annotation { "Feature Type Name" : "Feature", "Feature Type Description" : "" }
export const myFeature = defineFeature(function(context is Context, id is Id, definition is map)
    precondition{}
    {
        {
            var Q0;
            Q0=qCreatedBy(makeId("Top.planeOp"),FACE);
            var sketch = newSketch(context, id + "F0", { "sketchPlane" : qUnion([Q0])});
            skLineSegment(sketch, "E0.bottom", {"start": v(-160, 35) * mm, "end": v(160, 35) * mm});
            skLineSegment(sketch, "E0.top", {"start": v(-160, -35) * mm, "end": v(160, -35) * mm});
            skLineSegment(sketch, "E0.left", {"start": v(-160, 35) * mm, "end": v(-160, -35) * mm});
            skLineSegment(sketch, "E0.right", {"start": v(160, 35) * mm, "end": v(160, -35) * mm});
            skLineSegment(sketch, "E1", {"start": v(-160, 35) * mm, "end": v(160, -35) * mm, "construction": true});
            skLineSegment(sketch, "E2", {"start": v(-160, -35) * mm, "end": v(160, 35) * mm, "construction": true});
            skText(sketch, "E3", { "text": "Siri Bloch Arnfred\n", "fontName": "Arimo-Bold.ttf"});
            skText(sketch, "E4", { "text": "Jonas Bloch Riisgaard", "fontName": "Arimo-Bold.ttf"});
            const initialGuessF0  = {"E3": [-0.115, 0.011, 1, 0, 0.02], "E4": [-0.15, -0.015, 1, 0, 0.02]};
            skSetInitialGuess(sketch, initialGuessF0);
            skSolve(sketch);
        }
        {
            var Q0;
            Q0=makeQuery(id+"F0.imprint","IMPRINT",FACE,{"disambiguationData":[TD([[makeQuery(id+"F0.imprint","IMPRINT",EDGE,{"derivedFrom":sQuery(id+"F0.wireOp",EDGE,"E3.sketch_text.stroke-0")}),-1.0]])]});
            var Q1;
            Q1=makeQuery(id+"F0.imprint","IMPRINT",FACE,{"disambiguationData":[TD([[makeQuery(id+"F0.imprint","IMPRINT",EDGE,{"derivedFrom":sQuery(id+"F0.wireOp",EDGE,"E3.sketch_text.stroke-28")}),-1.0]])]});
            var Q2;
            Q2=makeQuery(id+"F0.imprint","IMPRINT",FACE,{"disambiguationData":[TD([[makeQuery(id+"F0.imprint","IMPRINT",EDGE,{"derivedFrom":sQuery(id+"F0.wireOp",EDGE,"E3.sketch_text.stroke-33")}),-1.0]])]});
            var Q3;
            Q3=makeQuery(id+"F0.imprint","IMPRINT",FACE,{"disambiguationData":[TD([[makeQuery(id+"F0.imprint","IMPRINT",EDGE,{"derivedFrom":sQuery(id+"F0.wireOp",EDGE,"E3.sketch_text.stroke-37")}),-1.0]])]});
            var Q4;
            Q4=makeQuery(id+"F0.imprint","IMPRINT",FACE,{"disambiguationData":[TD([[makeQuery(id+"F0.imprint","IMPRINT",EDGE,{"derivedFrom":sQuery(id+"F0.wireOp",EDGE,"E3.sketch_text.stroke-50")}),-1.0]])]});
            var Q5;
            Q5=makeQuery(id+"F0.imprint","IMPRINT",FACE,{"disambiguationData":[TD([[makeQuery(id+"F0.imprint","IMPRINT",EDGE,{"derivedFrom":sQuery(id+"F0.wireOp",EDGE,"E3.sketch_text.stroke-55")}),-1.0]])]});
            var Q6;
            Q6=makeQuery(id+"F0.imprint","IMPRINT",FACE,{"disambiguationData":[TD([[makeQuery(id+"F0.imprint","IMPRINT",EDGE,{"derivedFrom":sQuery(id+"F0.wireOp",EDGE,"E3.sketch_text.stroke-60")}),-1.0]])]});
            var Q7;
            Q7=makeQuery(id+"F0.imprint","IMPRINT",FACE,{"disambiguationData":[TD([[makeQuery(id+"F0.imprint","IMPRINT",EDGE,{"derivedFrom":sQuery(id+"F0.wireOp",EDGE,"E3.sketch_text.stroke-56")}),-1.0]])]});
            extrude(context, id + "F1", {"entities" : qUnion([Q0, Q1, Q2, Q3, Q4, Q5, Q6, Q7]), "depth" : 4 * mm});
        }
        {
            var Q0;
            Q0=makeQuery(id+"F0.imprint","IMPRINT",FACE,{"disambiguationData":[TD([[makeQuery(id+"F0.imprint","IMPRINT",EDGE,{"derivedFrom":sQuery(id+"F0.wireOp",EDGE,"E3.sketch_text.stroke-64")}),-1.0]])]});
            var Q1;
            Q1=makeQuery(id+"F0.imprint","IMPRINT",FACE,{"disambiguationData":[TD([[makeQuery(id+"F0.imprint","IMPRINT",EDGE,{"derivedFrom":sQuery(id+"F0.wireOp",EDGE,"E3.sketch_text.stroke-88")}),-1.0]])]});
            var Q2;
            Q2=makeQuery(id+"F0.imprint","IMPRINT",FACE,{"disambiguationData":[TD([[makeQuery(id+"F0.imprint","IMPRINT",EDGE,{"derivedFrom":sQuery(id+"F0.wireOp",EDGE,"E3.sketch_text.stroke-92")}),-1.0]])]});
            var Q3;
            Q3=makeQuery(id+"F0.imprint","IMPRINT",FACE,{"disambiguationData":[TD([[makeQuery(id+"F0.imprint","IMPRINT",EDGE,{"derivedFrom":sQuery(id+"F0.wireOp",EDGE,"E3.sketch_text.stroke-106")}),-1.0]])]});
            var Q4;
            Q4=makeQuery(id+"F0.imprint","IMPRINT",FACE,{"disambiguationData":[TD([[makeQuery(id+"F0.imprint","IMPRINT",EDGE,{"derivedFrom":sQuery(id+"F0.wireOp",EDGE,"E3.sketch_text.stroke-123")}),-1.0]])]});
            extrude(context, id + "F2", {"entities" : qUnion([Q0, Q1, Q2, Q3, Q4]), "depth" : 4 * mm});
        }
        {
            var Q0;
            Q0=makeQuery(id+"F0.imprint","IMPRINT",FACE,{"disambiguationData":[TD([[makeQuery(id+"F0.imprint","IMPRINT",EDGE,{"derivedFrom":sQuery(id+"F0.wireOp",EDGE,"E3.sketch_text.stroke-140")}),-1.0]])]});
            var Q1;
            Q1=makeQuery(id+"F0.imprint","IMPRINT",FACE,{"disambiguationData":[TD([[makeQuery(id+"F0.imprint","IMPRINT",EDGE,{"derivedFrom":sQuery(id+"F0.wireOp",EDGE,"E3.sketch_text.stroke-155")}),-1.0]])]});
            var Q2;
            Q2=makeQuery(id+"F0.imprint","IMPRINT",FACE,{"disambiguationData":[TD([[makeQuery(id+"F0.imprint","IMPRINT",EDGE,{"derivedFrom":sQuery(id+"F0.wireOp",EDGE,"E3.sketch_text.stroke-172")}),-1.0]])]});
            var Q3;
            Q3=makeQuery(id+"F0.imprint","IMPRINT",FACE,{"disambiguationData":[TD([[makeQuery(id+"F0.imprint","IMPRINT",EDGE,{"derivedFrom":sQuery(id+"F0.wireOp",EDGE,"E3.sketch_text.stroke-191")}),-1.0]])]});
            var Q4;
            Q4=makeQuery(id+"F0.imprint","IMPRINT",FACE,{"disambiguationData":[TD([[makeQuery(id+"F0.imprint","IMPRINT",EDGE,{"derivedFrom":sQuery(id+"F0.wireOp",EDGE,"E3.sketch_text.stroke-209")}),-1.0]])]});
            var Q5;
            Q5=makeQuery(id+"F0.imprint","IMPRINT",FACE,{"disambiguationData":[TD([[makeQuery(id+"F0.imprint","IMPRINT",EDGE,{"derivedFrom":sQuery(id+"F0.wireOp",EDGE,"E3.sketch_text.stroke-226")}),-1.0]])]});
            var Q6;
            Q6=makeQuery(id+"F0.imprint","IMPRINT",FACE,{"disambiguationData":[TD([[makeQuery(id+"F0.imprint","IMPRINT",EDGE,{"derivedFrom":sQuery(id+"F0.wireOp",EDGE,"E3.sketch_text.stroke-244")}),-1.0]])]});
            extrude(context, id + "F3", {"entities" : qUnion([Q0, Q1, Q2, Q3, Q4, Q5, Q6]), "depth" : 4 * mm});
        }
        {
            var Q0;
            Q0=makeQuery(id+"F0.imprint","IMPRINT",FACE,{"disambiguationData":[TD([[makeQuery(id+"F0.imprint","IMPRINT",EDGE,{"derivedFrom":sQuery(id+"F0.wireOp",EDGE,"E4.sketch_text.stroke-0")}),-1.0]])]});
            var Q1;
            Q1=makeQuery(id+"F0.imprint","IMPRINT",FACE,{"disambiguationData":[TD([[makeQuery(id+"F0.imprint","IMPRINT",EDGE,{"derivedFrom":sQuery(id+"F0.wireOp",EDGE,"E4.sketch_text.stroke-14")}),-1.0]])]});
            var Q2;
            Q2=makeQuery(id+"F0.imprint","IMPRINT",FACE,{"disambiguationData":[TD([[makeQuery(id+"F0.imprint","IMPRINT",EDGE,{"derivedFrom":sQuery(id+"F0.wireOp",EDGE,"E4.sketch_text.stroke-28")}),-1.0]])]});
            var Q3;
            Q3=makeQuery(id+"F0.imprint","IMPRINT",FACE,{"disambiguationData":[TD([[makeQuery(id+"F0.imprint","IMPRINT",EDGE,{"derivedFrom":sQuery(id+"F0.wireOp",EDGE,"E4.sketch_text.stroke-47")}),-1.0]])]});
            var Q4;
            Q4=makeQuery(id+"F0.imprint","IMPRINT",FACE,{"disambiguationData":[TD([[makeQuery(id+"F0.imprint","IMPRINT",EDGE,{"derivedFrom":sQuery(id+"F0.wireOp",EDGE,"E4.sketch_text.stroke-85")}),-1.0]])]});
            var Q5;
            Q5=makeQuery(id+"F0.imprint","IMPRINT",FACE,{"disambiguationData":[TD([[makeQuery(id+"F0.imprint","IMPRINT",EDGE,{"derivedFrom":sQuery(id+"F0.wireOp",EDGE,"E4.sketch_text.stroke-114")}),-1.0]])]});
            var Q6;
            Q6=makeQuery(id+"F0.imprint","IMPRINT",FACE,{"disambiguationData":[TD([[makeQuery(id+"F0.imprint","IMPRINT",EDGE,{"derivedFrom":sQuery(id+"F0.wireOp",EDGE,"E4.sketch_text.stroke-138")}),-1.0]])]});
            var Q7;
            Q7=makeQuery(id+"F0.imprint","IMPRINT",FACE,{"disambiguationData":[TD([[makeQuery(id+"F0.imprint","IMPRINT",EDGE,{"derivedFrom":sQuery(id+"F0.wireOp",EDGE,"E4.sketch_text.stroke-142")}),-1.0]])]});
            var Q8;
            Q8=makeQuery(id+"F0.imprint","IMPRINT",FACE,{"disambiguationData":[TD([[makeQuery(id+"F0.imprint","IMPRINT",EDGE,{"derivedFrom":sQuery(id+"F0.wireOp",EDGE,"E4.sketch_text.stroke-156")}),-1.0]])]});
            var Q9;
            Q9=makeQuery(id+"F0.imprint","IMPRINT",FACE,{"disambiguationData":[TD([[makeQuery(id+"F0.imprint","IMPRINT",EDGE,{"derivedFrom":sQuery(id+"F0.wireOp",EDGE,"E4.sketch_text.stroke-173")}),-1.0]])]});
            extrude(context, id + "F4", {"entities" : qUnion([Q0, Q1, Q2, Q3, Q4, Q5, Q6, Q7, Q8, Q9]), "depth" : 4 * mm});
        }
        {
            var Q0;
            Q0=makeQuery(id+"F0.imprint","IMPRINT",FACE,{"disambiguationData":[TD([[makeQuery(id+"F0.imprint","IMPRINT",EDGE,{"derivedFrom":sQuery(id+"F0.wireOp",EDGE,"E4.sketch_text.stroke-190")}),-1.0]])]});
            var Q1;
            Q1=makeQuery(id+"F0.imprint","IMPRINT",FACE,{"disambiguationData":[TD([[makeQuery(id+"F0.imprint","IMPRINT",EDGE,{"derivedFrom":sQuery(id+"F0.wireOp",EDGE,"E4.sketch_text.stroke-212")}),-1.0]])]});
            var Q2;
            Q2=makeQuery(id+"F0.imprint","IMPRINT",FACE,{"disambiguationData":[TD([[makeQuery(id+"F0.imprint","IMPRINT",EDGE,{"derivedFrom":sQuery(id+"F0.wireOp",EDGE,"E4.sketch_text.stroke-208")}),-1.0]])]});
            var Q3;
            Q3=makeQuery(id+"F0.imprint","IMPRINT",FACE,{"disambiguationData":[TD([[makeQuery(id+"F0.imprint","IMPRINT",EDGE,{"derivedFrom":sQuery(id+"F0.wireOp",EDGE,"E4.sketch_text.stroke-220")}),-1.0]])]});
            var Q4;
            Q4=makeQuery(id+"F0.imprint","IMPRINT",FACE,{"disambiguationData":[TD([[makeQuery(id+"F0.imprint","IMPRINT",EDGE,{"derivedFrom":sQuery(id+"F0.wireOp",EDGE,"E4.sketch_text.stroke-216")}),-1.0]])]});
            var Q5;
            Q5=makeQuery(id+"F0.imprint","IMPRINT",FACE,{"disambiguationData":[TD([[makeQuery(id+"F0.imprint","IMPRINT",EDGE,{"derivedFrom":sQuery(id+"F0.wireOp",EDGE,"E4.sketch_text.stroke-224")}),-1.0]])]});
            var Q6;
            Q6=makeQuery(id+"F0.imprint","IMPRINT",FACE,{"disambiguationData":[TD([[makeQuery(id+"F0.imprint","IMPRINT",EDGE,{"derivedFrom":sQuery(id+"F0.wireOp",EDGE,"E4.sketch_text.stroke-253")}),-1.0]])]});
            var Q7;
            Q7=makeQuery(id+"F0.imprint","IMPRINT",FACE,{"disambiguationData":[TD([[makeQuery(id+"F0.imprint","IMPRINT",EDGE,{"derivedFrom":sQuery(id+"F0.wireOp",EDGE,"E4.sketch_text.stroke-283")}),-1.0]])]});
            var Q8;
            Q8=makeQuery(id+"F0.imprint","IMPRINT",FACE,{"disambiguationData":[TD([[makeQuery(id+"F0.imprint","IMPRINT",EDGE,{"derivedFrom":sQuery(id+"F0.wireOp",EDGE,"E4.sketch_text.stroke-321")}),-1.0]])]});
            var Q9;
            Q9=makeQuery(id+"F0.imprint","IMPRINT",FACE,{"disambiguationData":[TD([[makeQuery(id+"F0.imprint","IMPRINT",EDGE,{"derivedFrom":sQuery(id+"F0.wireOp",EDGE,"E4.sketch_text.stroke-359")}),-1.0]])]});
            var Q10;
            Q10=makeQuery(id+"F0.imprint","IMPRINT",FACE,{"disambiguationData":[TD([[makeQuery(id+"F0.imprint","IMPRINT",EDGE,{"derivedFrom":sQuery(id+"F0.wireOp",EDGE,"E4.sketch_text.stroke-376")}),-1.0]])]});
            extrude(context, id + "F5", {"entities" : qUnion([Q0, Q1, Q2, Q3, Q4, Q5, Q6, Q7, Q8, Q9, Q10]), "depth" : 4 * mm});
        }
        {
            var Q0;
            Q0=makeQuery(id+"F0.imprint","IMPRINT",FACE,{"disambiguationData":[TD([[makeQuery(id+"F0.imprint","IMPRINT",EDGE,{"derivedFrom":sQuery(id+"F0.wireOp",EDGE,"E0.bottom")}),-1.0]])]});
            extrude(context, id + "F6", {"entities" : qUnion([Q0]), "oppositeDirection" : true, "depth" : 2 * mm});
        }
        {
            var Q0;
            Q0=makeQuery(id+"F6.opExtrude","SWEPT_EDGE",EDGE,{"disambiguationData":[OSD([sQuery(id+"F0.wireOp",EDGE,"E0.bottom"),sQuery(id+"F0.wireOp",EDGE,"E0.left")])]});
            fillet(context, id + "F7", {"entities" : qUnion([Q0]), "radius" : 20 * mm, "tangentPropagation" : true, "allowEdgeOverflow" : false});
        }
        {
            var Q0;
            Q0=makeQuery(id+"F6.opExtrude","SWEPT_EDGE",EDGE,{"disambiguationData":[OSD([sQuery(id+"F0.wireOp",EDGE,"E0.top"),sQuery(id+"F0.wireOp",EDGE,"E0.left")])]});
            fillet(context, id + "F8", {"entities" : qUnion([Q0]), "radius" : 20 * mm, "tangentPropagation" : true, "allowEdgeOverflow" : false});
        }
        {
            var Q0;
            Q0=makeQuery(id+"F6.opExtrude","SWEPT_EDGE",EDGE,{"disambiguationData":[OSD([sQuery(id+"F0.wireOp",EDGE,"E0.top"),sQuery(id+"F0.wireOp",EDGE,"E0.right")])]});
            var Q1;
            Q1=makeQuery(id+"F6.opExtrude","SWEPT_EDGE",EDGE,{"disambiguationData":[OSD([sQuery(id+"F0.wireOp",EDGE,"E0.bottom"),sQuery(id+"F0.wireOp",EDGE,"E0.right")])]});
            fillet(context, id + "F9", {"entities" : qUnion([Q0, Q1]), "radius" : 20 * mm, "tangentPropagation" : true, "allowEdgeOverflow" : false});
        }
        {
            var Q0;
            {var subQ0=sQuery(id+"F0.wireOp",EDGE,"E0.right");var subQ1=sQuery(id+"F0.wireOp",EDGE,"E0.bottom");Q0=makeQuery(id+"F9.opFillet","BLEND_EDGE",EDGE,{"blendedFrom":[makeQuery(id+"F6.opExtrude","SWEPT_EDGE",EDGE,{"disambiguationData":[OSD([subQ1,subQ0])]}),makeQuery(id+"F6.opExtrude","CAP_FACE",FACE,{"disambiguationData":[OSD([subQ1,sQuery(id+"F0.wireOp",EDGE,"E0.top"),sQuery(id+"F0.wireOp",EDGE,"E0.left"),subQ0,sQuery(id+"F0.wireOp",EDGE,"E3.sketch_text.stroke-0"),sQuery(id+"F0.wireOp",EDGE,"E3.sketch_text.stroke-1"),sQuery(id+"F0.wireOp",EDGE,"E3.sketch_text.stroke-2"),sQuery(id+"F0.wireOp",EDGE,"E3.sketch_text.stroke-3"),sQuery(id+"F0.wireOp",EDGE,"E3.sketch_text.stroke-4"),sQuery(id+"F0.wireOp",EDGE,"E3.sketch_text.stroke-5"),sQuery(id+"F0.wireOp",EDGE,"E3.sketch_text.stroke-6"),sQuery(id+"F0.wireOp",EDGE,"E3.sketch_text.stroke-7"),sQuery(id+"F0.wireOp",EDGE,"E3.sketch_text.stroke-8"),sQuery(id+"F0.wireOp",EDGE,"E3.sketch_text.stroke-9"),sQuery(id+"F0.wireOp",EDGE,"E3.sketch_text.stroke-10"),sQuery(id+"F0.wireOp",EDGE,"E3.sketch_text.stroke-11"),sQuery(id+"F0.wireOp",EDGE,"E3.sketch_text.stroke-12"),sQuery(id+"F0.wireOp",EDGE,"E3.sketch_text.stroke-13"),sQuery(id+"F0.wireOp",EDGE,"E3.sketch_text.stroke-14"),sQuery(id+"F0.wireOp",EDGE,"E3.sketch_text.stroke-15"),sQuery(id+"F0.wireOp",EDGE,"E3.sketch_text.stroke-16"),sQuery(id+"F0.wireOp",EDGE,"E3.sketch_text.stroke-17"),sQuery(id+"F0.wireOp",EDGE,"E3.sketch_text.stroke-18"),sQuery(id+"F0.wireOp",EDGE,"E3.sketch_text.stroke-19"),sQuery(id+"F0.wireOp",EDGE,"E3.sketch_text.stroke-20"),sQuery(id+"F0.wireOp",EDGE,"E3.sketch_text.stroke-21"),sQuery(id+"F0.wireOp",EDGE,"E3.sketch_text.stroke-22"),sQuery(id+"F0.wireOp",EDGE,"E3.sketch_text.stroke-23"),sQuery(id+"F0.wireOp",EDGE,"E3.sketch_text.stroke-24"),sQuery(id+"F0.wireOp",EDGE,"E3.sketch_text.stroke-25"),sQuery(id+"F0.wireOp",EDGE,"E3.sketch_text.stroke-26"),sQuery(id+"F0.wireOp",EDGE,"E3.sketch_text.stroke-27"),sQuery(id+"F0.wireOp",EDGE,"E3.sketch_text.stroke-28"),sQuery(id+"F0.wireOp",EDGE,"E3.sketch_text.stroke-29"),sQuery(id+"F0.wireOp",EDGE,"E3.sketch_text.stroke-30"),sQuery(id+"F0.wireOp",EDGE,"E3.sketch_text.stroke-31"),sQuery(id+"F0.wireOp",EDGE,"E3.sketch_text.stroke-32"),sQuery(id+"F0.wireOp",EDGE,"E3.sketch_text.stroke-33"),sQuery(id+"F0.wireOp",EDGE,"E3.sketch_text.stroke-34"),sQuery(id+"F0.wireOp",EDGE,"E3.sketch_text.stroke-35"),sQuery(id+"F0.wireOp",EDGE,"E3.sketch_text.stroke-36"),sQuery(id+"F0.wireOp",EDGE,"E3.sketch_text.stroke-37"),sQuery(id+"F0.wireOp",EDGE,"E3.sketch_text.stroke-38"),sQuery(id+"F0.wireOp",EDGE,"E3.sketch_text.stroke-39"),sQuery(id+"F0.wireOp",EDGE,"E3.sketch_text.stroke-40"),sQuery(id+"F0.wireOp",EDGE,"E3.sketch_text.stroke-41"),sQuery(id+"F0.wireOp",EDGE,"E3.sketch_text.stroke-42"),sQuery(id+"F0.wireOp",EDGE,"E3.sketch_text.stroke-43"),sQuery(id+"F0.wireOp",EDGE,"E3.sketch_text.stroke-44"),sQuery(id+"F0.wireOp",EDGE,"E3.sketch_text.stroke-45"),sQuery(id+"F0.wireOp",EDGE,"E3.sketch_text.stroke-46"),sQuery(id+"F0.wireOp",EDGE,"E3.sketch_text.stroke-47"),sQuery(id+"F0.wireOp",EDGE,"E3.sketch_text.stroke-48"),sQuery(id+"F0.wireOp",EDGE,"E3.sketch_text.stroke-49"),sQuery(id+"F0.wireOp",EDGE,"E3.sketch_text.stroke-50"),sQuery(id+"F0.wireOp",EDGE,"E3.sketch_text.stroke-51"),sQuery(id+"F0.wireOp",EDGE,"E3.sketch_text.stroke-52"),sQuery(id+"F0.wireOp",EDGE,"E3.sketch_text.stroke-53"),sQuery(id+"F0.wireOp",EDGE,"E3.sketch_text.stroke-54"),sQuery(id+"F0.wireOp",EDGE,"E3.sketch_text.stroke-55"),sQuery(id+"F0.wireOp",EDGE,"E3.sketch_text.stroke-56"),sQuery(id+"F0.wireOp",EDGE,"E3.sketch_text.stroke-57"),sQuery(id+"F0.wireOp",EDGE,"E3.sketch_text.stroke-58"),sQuery(id+"F0.wireOp",EDGE,"E3.sketch_text.stroke-59"),sQuery(id+"F0.wireOp",EDGE,"E3.sketch_text.stroke-60"),sQuery(id+"F0.wireOp",EDGE,"E3.sketch_text.stroke-61"),sQuery(id+"F0.wireOp",EDGE,"E3.sketch_text.stroke-62"),sQuery(id+"F0.wireOp",EDGE,"E3.sketch_text.stroke-63"),sQuery(id+"F0.wireOp",EDGE,"E3.sketch_text.stroke-64"),sQuery(id+"F0.wireOp",EDGE,"E3.sketch_text.stroke-65"),sQuery(id+"F0.wireOp",EDGE,"E3.sketch_text.stroke-66"),sQuery(id+"F0.wireOp",EDGE,"E3.sketch_text.stroke-67"),sQuery(id+"F0.wireOp",EDGE,"E3.sketch_text.stroke-68"),sQuery(id+"F0.wireOp",EDGE,"E3.sketch_text.stroke-69"),sQuery(id+"F0.wireOp",EDGE,"E3.sketch_text.stroke-70"),sQuery(id+"F0.wireOp",EDGE,"E3.sketch_text.stroke-71"),sQuery(id+"F0.wireOp",EDGE,"E3.sketch_text.stroke-72"),sQuery(id+"F0.wireOp",EDGE,"E3.sketch_text.stroke-73"),sQuery(id+"F0.wireOp",EDGE,"E3.sketch_text.stroke-74"),sQuery(id+"F0.wireOp",EDGE,"E3.sketch_text.stroke-88"),sQuery(id+"F0.wireOp",EDGE,"E3.sketch_text.stroke-89"),sQuery(id+"F0.wireOp",EDGE,"E3.sketch_text.stroke-90"),sQuery(id+"F0.wireOp",EDGE,"E3.sketch_text.stroke-91"),sQuery(id+"F0.wireOp",EDGE,"E3.sketch_text.stroke-92"),sQuery(id+"F0.wireOp",EDGE,"E3.sketch_text.stroke-93"),sQuery(id+"F0.wireOp",EDGE,"E3.sketch_text.stroke-94"),sQuery(id+"F0.wireOp",EDGE,"E3.sketch_text.stroke-95"),sQuery(id+"F0.wireOp",EDGE,"E3.sketch_text.stroke-96"),sQuery(id+"F0.wireOp",EDGE,"E3.sketch_text.stroke-97"),sQuery(id+"F0.wireOp",EDGE,"E3.sketch_text.stroke-98"),sQuery(id+"F0.wireOp",EDGE,"E3.sketch_text.stroke-99"),sQuery(id+"F0.wireOp",EDGE,"E3.sketch_text.stroke-106"),sQuery(id+"F0.wireOp",EDGE,"E3.sketch_text.stroke-107"),sQuery(id+"F0.wireOp",EDGE,"E3.sketch_text.stroke-108"),sQuery(id+"F0.wireOp",EDGE,"E3.sketch_text.stroke-109"),sQuery(id+"F0.wireOp",EDGE,"E3.sketch_text.stroke-110"),sQuery(id+"F0.wireOp",EDGE,"E3.sketch_text.stroke-111"),sQuery(id+"F0.wireOp",EDGE,"E3.sketch_text.stroke-112"),sQuery(id+"F0.wireOp",EDGE,"E3.sketch_text.stroke-113"),sQuery(id+"F0.wireOp",EDGE,"E3.sketch_text.stroke-114"),sQuery(id+"F0.wireOp",EDGE,"E3.sketch_text.stroke-115"),sQuery(id+"F0.wireOp",EDGE,"E3.sketch_text.stroke-116"),sQuery(id+"F0.wireOp",EDGE,"E3.sketch_text.stroke-117"),sQuery(id+"F0.wireOp",EDGE,"E3.sketch_text.stroke-118"),sQuery(id+"F0.wireOp",EDGE,"E3.sketch_text.stroke-119"),sQuery(id+"F0.wireOp",EDGE,"E3.sketch_text.stroke-120"),sQuery(id+"F0.wireOp",EDGE,"E3.sketch_text.stroke-121"),sQuery(id+"F0.wireOp",EDGE,"E3.sketch_text.stroke-122"),sQuery(id+"F0.wireOp",EDGE,"E3.sketch_text.stroke-123"),sQuery(id+"F0.wireOp",EDGE,"E3.sketch_text.stroke-124"),sQuery(id+"F0.wireOp",EDGE,"E3.sketch_text.stroke-125"),sQuery(id+"F0.wireOp",EDGE,"E3.sketch_text.stroke-126"),sQuery(id+"F0.wireOp",EDGE,"E3.sketch_text.stroke-127"),sQuery(id+"F0.wireOp",EDGE,"E3.sketch_text.stroke-128"),sQuery(id+"F0.wireOp",EDGE,"E3.sketch_text.stroke-129"),sQuery(id+"F0.wireOp",EDGE,"E3.sketch_text.stroke-130"),sQuery(id+"F0.wireOp",EDGE,"E3.sketch_text.stroke-131"),sQuery(id+"F0.wireOp",EDGE,"E3.sketch_text.stroke-132"),sQuery(id+"F0.wireOp",EDGE,"E3.sketch_text.stroke-133"),sQuery(id+"F0.wireOp",EDGE,"E3.sketch_text.stroke-134"),sQuery(id+"F0.wireOp",EDGE,"E3.sketch_text.stroke-135"),sQuery(id+"F0.wireOp",EDGE,"E3.sketch_text.stroke-136"),sQuery(id+"F0.wireOp",EDGE,"E3.sketch_text.stroke-137"),sQuery(id+"F0.wireOp",EDGE,"E3.sketch_text.stroke-138"),sQuery(id+"F0.wireOp",EDGE,"E3.sketch_text.stroke-139"),sQuery(id+"F0.wireOp",EDGE,"E3.sketch_text.stroke-140"),sQuery(id+"F0.wireOp",EDGE,"E3.sketch_text.stroke-141"),sQuery(id+"F0.wireOp",EDGE,"E3.sketch_text.stroke-142"),sQuery(id+"F0.wireOp",EDGE,"E3.sketch_text.stroke-143"),sQuery(id+"F0.wireOp",EDGE,"E3.sketch_text.stroke-144"),sQuery(id+"F0.wireOp",EDGE,"E3.sketch_text.stroke-145"),sQuery(id+"F0.wireOp",EDGE,"E3.sketch_text.stroke-146"),sQuery(id+"F0.wireOp",EDGE,"E3.sketch_text.stroke-147"),sQuery(id+"F0.wireOp",EDGE,"E3.sketch_text.stroke-155"),sQuery(id+"F0.wireOp",EDGE,"E3.sketch_text.stroke-156"),sQuery(id+"F0.wireOp",EDGE,"E3.sketch_text.stroke-157"),sQuery(id+"F0.wireOp",EDGE,"E3.sketch_text.stroke-158"),sQuery(id+"F0.wireOp",EDGE,"E3.sketch_text.stroke-159"),sQuery(id+"F0.wireOp",EDGE,"E3.sketch_text.stroke-160"),sQuery(id+"F0.wireOp",EDGE,"E3.sketch_text.stroke-161"),sQuery(id+"F0.wireOp",EDGE,"E3.sketch_text.stroke-162"),sQuery(id+"F0.wireOp",EDGE,"E3.sketch_text.stroke-163"),sQuery(id+"F0.wireOp",EDGE,"E3.sketch_text.stroke-164"),sQuery(id+"F0.wireOp",EDGE,"E3.sketch_text.stroke-165"),sQuery(id+"F0.wireOp",EDGE,"E3.sketch_text.stroke-166"),sQuery(id+"F0.wireOp",EDGE,"E3.sketch_text.stroke-167"),sQuery(id+"F0.wireOp",EDGE,"E3.sketch_text.stroke-168"),sQuery(id+"F0.wireOp",EDGE,"E3.sketch_text.stroke-169"),sQuery(id+"F0.wireOp",EDGE,"E3.sketch_text.stroke-170"),sQuery(id+"F0.wireOp",EDGE,"E3.sketch_text.stroke-171"),sQuery(id+"F0.wireOp",EDGE,"E3.sketch_text.stroke-172"),sQuery(id+"F0.wireOp",EDGE,"E3.sketch_text.stroke-173"),sQuery(id+"F0.wireOp",EDGE,"E3.sketch_text.stroke-174"),sQuery(id+"F0.wireOp",EDGE,"E3.sketch_text.stroke-175"),sQuery(id+"F0.wireOp",EDGE,"E3.sketch_text.stroke-176"),sQuery(id+"F0.wireOp",EDGE,"E3.sketch_text.stroke-177"),sQuery(id+"F0.wireOp",EDGE,"E3.sketch_text.stroke-178"),sQuery(id+"F0.wireOp",EDGE,"E3.sketch_text.stroke-179"),sQuery(id+"F0.wireOp",EDGE,"E3.sketch_text.stroke-180"),sQuery(id+"F0.wireOp",EDGE,"E3.sketch_text.stroke-181"),sQuery(id+"F0.wireOp",EDGE,"E3.sketch_text.stroke-182"),sQuery(id+"F0.wireOp",EDGE,"E3.sketch_text.stroke-183"),sQuery(id+"F0.wireOp",EDGE,"E3.sketch_text.stroke-184"),sQuery(id+"F0.wireOp",EDGE,"E3.sketch_text.stroke-185"),sQuery(id+"F0.wireOp",EDGE,"E3.sketch_text.stroke-186"),sQuery(id+"F0.wireOp",EDGE,"E3.sketch_text.stroke-187"),sQuery(id+"F0.wireOp",EDGE,"E3.sketch_text.stroke-188"),sQuery(id+"F0.wireOp",EDGE,"E3.sketch_text.stroke-189"),sQuery(id+"F0.wireOp",EDGE,"E3.sketch_text.stroke-190"),sQuery(id+"F0.wireOp",EDGE,"E3.sketch_text.stroke-191"),sQuery(id+"F0.wireOp",EDGE,"E3.sketch_text.stroke-192"),sQuery(id+"F0.wireOp",EDGE,"E3.sketch_text.stroke-193"),sQuery(id+"F0.wireOp",EDGE,"E3.sketch_text.stroke-194"),sQuery(id+"F0.wireOp",EDGE,"E3.sketch_text.stroke-195"),sQuery(id+"F0.wireOp",EDGE,"E3.sketch_text.stroke-196"),sQuery(id+"F0.wireOp",EDGE,"E3.sketch_text.stroke-197"),sQuery(id+"F0.wireOp",EDGE,"E3.sketch_text.stroke-198"),sQuery(id+"F0.wireOp",EDGE,"E3.sketch_text.stroke-199"),sQuery(id+"F0.wireOp",EDGE,"E3.sketch_text.stroke-200"),sQuery(id+"F0.wireOp",EDGE,"E3.sketch_text.stroke-201"),sQuery(id+"F0.wireOp",EDGE,"E3.sketch_text.stroke-202"),sQuery(id+"F0.wireOp",EDGE,"E3.sketch_text.stroke-203"),sQuery(id+"F0.wireOp",EDGE,"E3.sketch_text.stroke-204"),sQuery(id+"F0.wireOp",EDGE,"E3.sketch_text.stroke-205"),sQuery(id+"F0.wireOp",EDGE,"E3.sketch_text.stroke-206"),sQuery(id+"F0.wireOp",EDGE,"E3.sketch_text.stroke-207"),sQuery(id+"F0.wireOp",EDGE,"E3.sketch_text.stroke-208"),sQuery(id+"F0.wireOp",EDGE,"E3.sketch_text.stroke-209"),sQuery(id+"F0.wireOp",EDGE,"E3.sketch_text.stroke-210"),sQuery(id+"F0.wireOp",EDGE,"E3.sketch_text.stroke-211"),sQuery(id+"F0.wireOp",EDGE,"E3.sketch_text.stroke-212"),sQuery(id+"F0.wireOp",EDGE,"E3.sketch_text.stroke-213"),sQuery(id+"F0.wireOp",EDGE,"E3.sketch_text.stroke-214"),sQuery(id+"F0.wireOp",EDGE,"E3.sketch_text.stroke-215"),sQuery(id+"F0.wireOp",EDGE,"E3.sketch_text.stroke-216"),sQuery(id+"F0.wireOp",EDGE,"E3.sketch_text.stroke-217"),sQuery(id+"F0.wireOp",EDGE,"E3.sketch_text.stroke-218"),sQuery(id+"F0.wireOp",EDGE,"E3.sketch_text.stroke-219"),sQuery(id+"F0.wireOp",EDGE,"E3.sketch_text.stroke-220"),sQuery(id+"F0.wireOp",EDGE,"E3.sketch_text.stroke-221"),sQuery(id+"F0.wireOp",EDGE,"E3.sketch_text.stroke-222"),sQuery(id+"F0.wireOp",EDGE,"E3.sketch_text.stroke-223"),sQuery(id+"F0.wireOp",EDGE,"E3.sketch_text.stroke-224"),sQuery(id+"F0.wireOp",EDGE,"E3.sketch_text.stroke-225"),sQuery(id+"F0.wireOp",EDGE,"E3.sketch_text.stroke-226"),sQuery(id+"F0.wireOp",EDGE,"E3.sketch_text.stroke-227"),sQuery(id+"F0.wireOp",EDGE,"E3.sketch_text.stroke-228"),sQuery(id+"F0.wireOp",EDGE,"E3.sketch_text.stroke-229"),sQuery(id+"F0.wireOp",EDGE,"E3.sketch_text.stroke-230"),sQuery(id+"F0.wireOp",EDGE,"E3.sketch_text.stroke-231"),sQuery(id+"F0.wireOp",EDGE,"E3.sketch_text.stroke-232"),sQuery(id+"F0.wireOp",EDGE,"E3.sketch_text.stroke-233"),sQuery(id+"F0.wireOp",EDGE,"E3.sketch_text.stroke-234"),sQuery(id+"F0.wireOp",EDGE,"E3.sketch_text.stroke-235"),sQuery(id+"F0.wireOp",EDGE,"E3.sketch_text.stroke-236"),sQuery(id+"F0.wireOp",EDGE,"E3.sketch_text.stroke-237"),sQuery(id+"F0.wireOp",EDGE,"E3.sketch_text.stroke-238"),sQuery(id+"F0.wireOp",EDGE,"E3.sketch_text.stroke-244"),sQuery(id+"F0.wireOp",EDGE,"E3.sketch_text.stroke-245"),sQuery(id+"F0.wireOp",EDGE,"E3.sketch_text.stroke-246"),sQuery(id+"F0.wireOp",EDGE,"E3.sketch_text.stroke-247"),sQuery(id+"F0.wireOp",EDGE,"E3.sketch_text.stroke-248"),sQuery(id+"F0.wireOp",EDGE,"E3.sketch_text.stroke-249"),sQuery(id+"F0.wireOp",EDGE,"E3.sketch_text.stroke-250"),sQuery(id+"F0.wireOp",EDGE,"E3.sketch_text.stroke-251"),sQuery(id+"F0.wireOp",EDGE,"E3.sketch_text.stroke-252"),sQuery(id+"F0.wireOp",EDGE,"E3.sketch_text.stroke-253"),sQuery(id+"F0.wireOp",EDGE,"E3.sketch_text.stroke-254"),sQuery(id+"F0.wireOp",EDGE,"E3.sketch_text.stroke-255"),sQuery(id+"F0.wireOp",EDGE,"E3.sketch_text.stroke-256"),sQuery(id+"F0.wireOp",EDGE,"E3.sketch_text.stroke-257"),sQuery(id+"F0.wireOp",EDGE,"E3.sketch_text.stroke-258"),sQuery(id+"F0.wireOp",EDGE,"E3.sketch_text.stroke-259"),sQuery(id+"F0.wireOp",EDGE,"E3.sketch_text.stroke-260"),sQuery(id+"F0.wireOp",EDGE,"E4.sketch_text.stroke-0"),sQuery(id+"F0.wireOp",EDGE,"E4.sketch_text.stroke-1"),sQuery(id+"F0.wireOp",EDGE,"E4.sketch_text.stroke-2"),sQuery(id+"F0.wireOp",EDGE,"E4.sketch_text.stroke-3"),sQuery(id+"F0.wireOp",EDGE,"E4.sketch_text.stroke-4"),sQuery(id+"F0.wireOp",EDGE,"E4.sketch_text.stroke-5"),sQuery(id+"F0.wireOp",EDGE,"E4.sketch_text.stroke-6"),sQuery(id+"F0.wireOp",EDGE,"E4.sketch_text.stroke-7"),sQuery(id+"F0.wireOp",EDGE,"E4.sketch_text.stroke-8"),sQuery(id+"F0.wireOp",EDGE,"E4.sketch_text.stroke-9"),sQuery(id+"F0.wireOp",EDGE,"E4.sketch_text.stroke-10"),sQuery(id+"F0.wireOp",EDGE,"E4.sketch_text.stroke-11"),sQuery(id+"F0.wireOp",EDGE,"E4.sketch_text.stroke-12"),sQuery(id+"F0.wireOp",EDGE,"E4.sketch_text.stroke-13"),sQuery(id+"F0.wireOp",EDGE,"E4.sketch_text.stroke-14"),sQuery(id+"F0.wireOp",EDGE,"E4.sketch_text.stroke-15"),sQuery(id+"F0.wireOp",EDGE,"E4.sketch_text.stroke-16"),sQuery(id+"F0.wireOp",EDGE,"E4.sketch_text.stroke-17"),sQuery(id+"F0.wireOp",EDGE,"E4.sketch_text.stroke-18"),sQuery(id+"F0.wireOp",EDGE,"E4.sketch_text.stroke-19"),sQuery(id+"F0.wireOp",EDGE,"E4.sketch_text.stroke-20"),sQuery(id+"F0.wireOp",EDGE,"E4.sketch_text.stroke-21"),sQuery(id+"F0.wireOp",EDGE,"E4.sketch_text.stroke-28"),sQuery(id+"F0.wireOp",EDGE,"E4.sketch_text.stroke-29"),sQuery(id+"F0.wireOp",EDGE,"E4.sketch_text.stroke-30"),sQuery(id+"F0.wireOp",EDGE,"E4.sketch_text.stroke-31"),sQuery(id+"F0.wireOp",EDGE,"E4.sketch_text.stroke-32"),sQuery(id+"F0.wireOp",EDGE,"E4.sketch_text.stroke-33"),sQuery(id+"F0.wireOp",EDGE,"E4.sketch_text.stroke-34"),sQuery(id+"F0.wireOp",EDGE,"E4.sketch_text.stroke-35"),sQuery(id+"F0.wireOp",EDGE,"E4.sketch_text.stroke-36"),sQuery(id+"F0.wireOp",EDGE,"E4.sketch_text.stroke-37"),sQuery(id+"F0.wireOp",EDGE,"E4.sketch_text.stroke-38"),sQuery(id+"F0.wireOp",EDGE,"E4.sketch_text.stroke-39"),sQuery(id+"F0.wireOp",EDGE,"E4.sketch_text.stroke-40"),sQuery(id+"F0.wireOp",EDGE,"E4.sketch_text.stroke-41"),sQuery(id+"F0.wireOp",EDGE,"E4.sketch_text.stroke-42"),sQuery(id+"F0.wireOp",EDGE,"E4.sketch_text.stroke-43"),sQuery(id+"F0.wireOp",EDGE,"E4.sketch_text.stroke-44"),sQuery(id+"F0.wireOp",EDGE,"E4.sketch_text.stroke-45"),sQuery(id+"F0.wireOp",EDGE,"E4.sketch_text.stroke-46"),sQuery(id+"F0.wireOp",EDGE,"E4.sketch_text.stroke-47"),sQuery(id+"F0.wireOp",EDGE,"E4.sketch_text.stroke-48"),sQuery(id+"F0.wireOp",EDGE,"E4.sketch_text.stroke-49"),sQuery(id+"F0.wireOp",EDGE,"E4.sketch_text.stroke-50"),sQuery(id+"F0.wireOp",EDGE,"E4.sketch_text.stroke-51"),sQuery(id+"F0.wireOp",EDGE,"E4.sketch_text.stroke-52"),sQuery(id+"F0.wireOp",EDGE,"E4.sketch_text.stroke-53"),sQuery(id+"F0.wireOp",EDGE,"E4.sketch_text.stroke-54"),sQuery(id+"F0.wireOp",EDGE,"E4.sketch_text.stroke-55"),sQuery(id+"F0.wireOp",EDGE,"E4.sketch_text.stroke-56"),sQuery(id+"F0.wireOp",EDGE,"E4.sketch_text.stroke-57"),sQuery(id+"F0.wireOp",EDGE,"E4.sketch_text.stroke-58"),sQuery(id+"F0.wireOp",EDGE,"E4.sketch_text.stroke-59"),sQuery(id+"F0.wireOp",EDGE,"E4.sketch_text.stroke-60"),sQuery(id+"F0.wireOp",EDGE,"E4.sketch_text.stroke-61"),sQuery(id+"F0.wireOp",EDGE,"E4.sketch_text.stroke-62"),sQuery(id+"F0.wireOp",EDGE,"E4.sketch_text.stroke-63"),sQuery(id+"F0.wireOp",EDGE,"E4.sketch_text.stroke-64"),sQuery(id+"F0.wireOp",EDGE,"E4.sketch_text.stroke-65"),sQuery(id+"F0.wireOp",EDGE,"E4.sketch_text.stroke-66"),sQuery(id+"F0.wireOp",EDGE,"E4.sketch_text.stroke-67"),sQuery(id+"F0.wireOp",EDGE,"E4.sketch_text.stroke-68"),sQuery(id+"F0.wireOp",EDGE,"E4.sketch_text.stroke-69"),sQuery(id+"F0.wireOp",EDGE,"E4.sketch_text.stroke-70"),sQuery(id+"F0.wireOp",EDGE,"E4.sketch_text.stroke-71"),sQuery(id+"F0.wireOp",EDGE,"E4.sketch_text.stroke-72"),sQuery(id+"F0.wireOp",EDGE,"E4.sketch_text.stroke-73"),sQuery(id+"F0.wireOp",EDGE,"E4.sketch_text.stroke-74"),sQuery(id+"F0.wireOp",EDGE,"E4.sketch_text.stroke-85"),sQuery(id+"F0.wireOp",EDGE,"E4.sketch_text.stroke-86"),sQuery(id+"F0.wireOp",EDGE,"E4.sketch_text.stroke-87"),sQuery(id+"F0.wireOp",EDGE,"E4.sketch_text.stroke-88"),sQuery(id+"F0.wireOp",EDGE,"E4.sketch_text.stroke-89"),sQuery(id+"F0.wireOp",EDGE,"E4.sketch_text.stroke-90"),sQuery(id+"F0.wireOp",EDGE,"E4.sketch_text.stroke-91"),sQuery(id+"F0.wireOp",EDGE,"E4.sketch_text.stroke-92"),sQuery(id+"F0.wireOp",EDGE,"E4.sketch_text.stroke-93"),sQuery(id+"F0.wireOp",EDGE,"E4.sketch_text.stroke-94"),sQuery(id+"F0.wireOp",EDGE,"E4.sketch_text.stroke-95"),sQuery(id+"F0.wireOp",EDGE,"E4.sketch_text.stroke-96"),sQuery(id+"F0.wireOp",EDGE,"E4.sketch_text.stroke-97"),sQuery(id+"F0.wireOp",EDGE,"E4.sketch_text.stroke-98"),sQuery(id+"F0.wireOp",EDGE,"E4.sketch_text.stroke-99"),sQuery(id+"F0.wireOp",EDGE,"E4.sketch_text.stroke-100"),sQuery(id+"F0.wireOp",EDGE,"E4.sketch_text.stroke-101"),sQuery(id+"F0.wireOp",EDGE,"E4.sketch_text.stroke-102"),sQuery(id+"F0.wireOp",EDGE,"E4.sketch_text.stroke-103"),sQuery(id+"F0.wireOp",EDGE,"E4.sketch_text.stroke-104"),sQuery(id+"F0.wireOp",EDGE,"E4.sketch_text.stroke-105"),sQuery(id+"F0.wireOp",EDGE,"E4.sketch_text.stroke-106"),sQuery(id+"F0.wireOp",EDGE,"E4.sketch_text.stroke-107"),sQuery(id+"F0.wireOp",EDGE,"E4.sketch_text.stroke-108"),sQuery(id+"F0.wireOp",EDGE,"E4.sketch_text.stroke-109"),sQuery(id+"F0.wireOp",EDGE,"E4.sketch_text.stroke-110"),sQuery(id+"F0.wireOp",EDGE,"E4.sketch_text.stroke-111"),sQuery(id+"F0.wireOp",EDGE,"E4.sketch_text.stroke-112"),sQuery(id+"F0.wireOp",EDGE,"E4.sketch_text.stroke-113"),sQuery(id+"F0.wireOp",EDGE,"E4.sketch_text.stroke-114"),sQuery(id+"F0.wireOp",EDGE,"E4.sketch_text.stroke-115"),sQuery(id+"F0.wireOp",EDGE,"E4.sketch_text.stroke-116"),sQuery(id+"F0.wireOp",EDGE,"E4.sketch_text.stroke-117"),sQuery(id+"F0.wireOp",EDGE,"E4.sketch_text.stroke-118"),sQuery(id+"F0.wireOp",EDGE,"E4.sketch_text.stroke-119"),sQuery(id+"F0.wireOp",EDGE,"E4.sketch_text.stroke-120"),sQuery(id+"F0.wireOp",EDGE,"E4.sketch_text.stroke-121"),sQuery(id+"F0.wireOp",EDGE,"E4.sketch_text.stroke-122"),sQuery(id+"F0.wireOp",EDGE,"E4.sketch_text.stroke-123"),sQuery(id+"F0.wireOp",EDGE,"E4.sketch_text.stroke-124"),sQuery(id+"F0.wireOp",EDGE,"E4.sketch_text.stroke-138"),sQuery(id+"F0.wireOp",EDGE,"E4.sketch_text.stroke-139"),sQuery(id+"F0.wireOp",EDGE,"E4.sketch_text.stroke-140"),sQuery(id+"F0.wireOp",EDGE,"E4.sketch_text.stroke-141"),sQuery(id+"F0.wireOp",EDGE,"E4.sketch_text.stroke-142"),sQuery(id+"F0.wireOp",EDGE,"E4.sketch_text.stroke-143"),sQuery(id+"F0.wireOp",EDGE,"E4.sketch_text.stroke-144"),sQuery(id+"F0.wireOp",EDGE,"E4.sketch_text.stroke-145"),sQuery(id+"F0.wireOp",EDGE,"E4.sketch_text.stroke-146"),sQuery(id+"F0.wireOp",EDGE,"E4.sketch_text.stroke-147"),sQuery(id+"F0.wireOp",EDGE,"E4.sketch_text.stroke-148"),sQuery(id+"F0.wireOp",EDGE,"E4.sketch_text.stroke-149"),sQuery(id+"F0.wireOp",EDGE,"E4.sketch_text.stroke-156"),sQuery(id+"F0.wireOp",EDGE,"E4.sketch_text.stroke-157"),sQuery(id+"F0.wireOp",EDGE,"E4.sketch_text.stroke-158"),sQuery(id+"F0.wireOp",EDGE,"E4.sketch_text.stroke-159"),sQuery(id+"F0.wireOp",EDGE,"E4.sketch_text.stroke-160"),sQuery(id+"F0.wireOp",EDGE,"E4.sketch_text.stroke-161"),sQuery(id+"F0.wireOp",EDGE,"E4.sketch_text.stroke-162"),sQuery(id+"F0.wireOp",EDGE,"E4.sketch_text.stroke-163"),sQuery(id+"F0.wireOp",EDGE,"E4.sketch_text.stroke-164"),sQuery(id+"F0.wireOp",EDGE,"E4.sketch_text.stroke-165"),sQuery(id+"F0.wireOp",EDGE,"E4.sketch_text.stroke-166"),sQuery(id+"F0.wireOp",EDGE,"E4.sketch_text.stroke-167"),sQuery(id+"F0.wireOp",EDGE,"E4.sketch_text.stroke-168"),sQuery(id+"F0.wireOp",EDGE,"E4.sketch_text.stroke-169"),sQuery(id+"F0.wireOp",EDGE,"E4.sketch_text.stroke-170"),sQuery(id+"F0.wireOp",EDGE,"E4.sketch_text.stroke-171"),sQuery(id+"F0.wireOp",EDGE,"E4.sketch_text.stroke-172"),sQuery(id+"F0.wireOp",EDGE,"E4.sketch_text.stroke-173"),sQuery(id+"F0.wireOp",EDGE,"E4.sketch_text.stroke-174"),sQuery(id+"F0.wireOp",EDGE,"E4.sketch_text.stroke-175"),sQuery(id+"F0.wireOp",EDGE,"E4.sketch_text.stroke-176"),sQuery(id+"F0.wireOp",EDGE,"E4.sketch_text.stroke-177"),sQuery(id+"F0.wireOp",EDGE,"E4.sketch_text.stroke-178"),sQuery(id+"F0.wireOp",EDGE,"E4.sketch_text.stroke-179"),sQuery(id+"F0.wireOp",EDGE,"E4.sketch_text.stroke-180"),sQuery(id+"F0.wireOp",EDGE,"E4.sketch_text.stroke-181"),sQuery(id+"F0.wireOp",EDGE,"E4.sketch_text.stroke-182"),sQuery(id+"F0.wireOp",EDGE,"E4.sketch_text.stroke-183"),sQuery(id+"F0.wireOp",EDGE,"E4.sketch_text.stroke-184"),sQuery(id+"F0.wireOp",EDGE,"E4.sketch_text.stroke-185"),sQuery(id+"F0.wireOp",EDGE,"E4.sketch_text.stroke-186"),sQuery(id+"F0.wireOp",EDGE,"E4.sketch_text.stroke-187"),sQuery(id+"F0.wireOp",EDGE,"E4.sketch_text.stroke-188"),sQuery(id+"F0.wireOp",EDGE,"E4.sketch_text.stroke-189"),sQuery(id+"F0.wireOp",EDGE,"E4.sketch_text.stroke-190"),sQuery(id+"F0.wireOp",EDGE,"E4.sketch_text.stroke-191"),sQuery(id+"F0.wireOp",EDGE,"E4.sketch_text.stroke-192"),sQuery(id+"F0.wireOp",EDGE,"E4.sketch_text.stroke-193"),sQuery(id+"F0.wireOp",EDGE,"E4.sketch_text.stroke-194"),sQuery(id+"F0.wireOp",EDGE,"E4.sketch_text.stroke-195"),sQuery(id+"F0.wireOp",EDGE,"E4.sketch_text.stroke-196"),sQuery(id+"F0.wireOp",EDGE,"E4.sketch_text.stroke-197"),sQuery(id+"F0.wireOp",EDGE,"E4.sketch_text.stroke-198"),sQuery(id+"F0.wireOp",EDGE,"E4.sketch_text.stroke-199"),sQuery(id+"F0.wireOp",EDGE,"E4.sketch_text.stroke-200"),sQuery(id+"F0.wireOp",EDGE,"E4.sketch_text.stroke-201"),sQuery(id+"F0.wireOp",EDGE,"E4.sketch_text.stroke-208"),sQuery(id+"F0.wireOp",EDGE,"E4.sketch_text.stroke-209"),sQuery(id+"F0.wireOp",EDGE,"E4.sketch_text.stroke-210"),sQuery(id+"F0.wireOp",EDGE,"E4.sketch_text.stroke-211"),sQuery(id+"F0.wireOp",EDGE,"E4.sketch_text.stroke-212"),sQuery(id+"F0.wireOp",EDGE,"E4.sketch_text.stroke-213"),sQuery(id+"F0.wireOp",EDGE,"E4.sketch_text.stroke-214"),sQuery(id+"F0.wireOp",EDGE,"E4.sketch_text.stroke-215"),sQuery(id+"F0.wireOp",EDGE,"E4.sketch_text.stroke-216"),sQuery(id+"F0.wireOp",EDGE,"E4.sketch_text.stroke-217"),sQuery(id+"F0.wireOp",EDGE,"E4.sketch_text.stroke-218"),sQuery(id+"F0.wireOp",EDGE,"E4.sketch_text.stroke-219"),sQuery(id+"F0.wireOp",EDGE,"E4.sketch_text.stroke-220"),sQuery(id+"F0.wireOp",EDGE,"E4.sketch_text.stroke-221"),sQuery(id+"F0.wireOp",EDGE,"E4.sketch_text.stroke-222"),sQuery(id+"F0.wireOp",EDGE,"E4.sketch_text.stroke-223"),sQuery(id+"F0.wireOp",EDGE,"E4.sketch_text.stroke-224"),sQuery(id+"F0.wireOp",EDGE,"E4.sketch_text.stroke-225"),sQuery(id+"F0.wireOp",EDGE,"E4.sketch_text.stroke-226"),sQuery(id+"F0.wireOp",EDGE,"E4.sketch_text.stroke-227"),sQuery(id+"F0.wireOp",EDGE,"E4.sketch_text.stroke-228"),sQuery(id+"F0.wireOp",EDGE,"E4.sketch_text.stroke-229"),sQuery(id+"F0.wireOp",EDGE,"E4.sketch_text.stroke-230"),sQuery(id+"F0.wireOp",EDGE,"E4.sketch_text.stroke-231"),sQuery(id+"F0.wireOp",EDGE,"E4.sketch_text.stroke-232"),sQuery(id+"F0.wireOp",EDGE,"E4.sketch_text.stroke-233"),sQuery(id+"F0.wireOp",EDGE,"E4.sketch_text.stroke-234"),sQuery(id+"F0.wireOp",EDGE,"E4.sketch_text.stroke-235"),sQuery(id+"F0.wireOp",EDGE,"E4.sketch_text.stroke-236"),sQuery(id+"F0.wireOp",EDGE,"E4.sketch_text.stroke-237"),sQuery(id+"F0.wireOp",EDGE,"E4.sketch_text.stroke-238"),sQuery(id+"F0.wireOp",EDGE,"E4.sketch_text.stroke-239"),sQuery(id+"F0.wireOp",EDGE,"E4.sketch_text.stroke-240"),sQuery(id+"F0.wireOp",EDGE,"E4.sketch_text.stroke-241"),sQuery(id+"F0.wireOp",EDGE,"E4.sketch_text.stroke-242"),sQuery(id+"F0.wireOp",EDGE,"E4.sketch_text.stroke-243"),sQuery(id+"F0.wireOp",EDGE,"E4.sketch_text.stroke-244"),sQuery(id+"F0.wireOp",EDGE,"E4.sketch_text.stroke-245"),sQuery(id+"F0.wireOp",EDGE,"E4.sketch_text.stroke-246"),sQuery(id+"F0.wireOp",EDGE,"E4.sketch_text.stroke-247"),sQuery(id+"F0.wireOp",EDGE,"E4.sketch_text.stroke-248"),sQuery(id+"F0.wireOp",EDGE,"E4.sketch_text.stroke-249"),sQuery(id+"F0.wireOp",EDGE,"E4.sketch_text.stroke-250"),sQuery(id+"F0.wireOp",EDGE,"E4.sketch_text.stroke-251"),sQuery(id+"F0.wireOp",EDGE,"E4.sketch_text.stroke-252"),sQuery(id+"F0.wireOp",EDGE,"E4.sketch_text.stroke-253"),sQuery(id+"F0.wireOp",EDGE,"E4.sketch_text.stroke-254"),sQuery(id+"F0.wireOp",EDGE,"E4.sketch_text.stroke-255"),sQuery(id+"F0.wireOp",EDGE,"E4.sketch_text.stroke-256"),sQuery(id+"F0.wireOp",EDGE,"E4.sketch_text.stroke-257"),sQuery(id+"F0.wireOp",EDGE,"E4.sketch_text.stroke-258"),sQuery(id+"F0.wireOp",EDGE,"E4.sketch_text.stroke-259"),sQuery(id+"F0.wireOp",EDGE,"E4.sketch_text.stroke-260"),sQuery(id+"F0.wireOp",EDGE,"E4.sketch_text.stroke-261"),sQuery(id+"F0.wireOp",EDGE,"E4.sketch_text.stroke-262"),sQuery(id+"F0.wireOp",EDGE,"E4.sketch_text.stroke-263"),sQuery(id+"F0.wireOp",EDGE,"E4.sketch_text.stroke-264"),sQuery(id+"F0.wireOp",EDGE,"E4.sketch_text.stroke-265"),sQuery(id+"F0.wireOp",EDGE,"E4.sketch_text.stroke-266"),sQuery(id+"F0.wireOp",EDGE,"E4.sketch_text.stroke-267"),sQuery(id+"F0.wireOp",EDGE,"E4.sketch_text.stroke-268"),sQuery(id+"F0.wireOp",EDGE,"E4.sketch_text.stroke-269"),sQuery(id+"F0.wireOp",EDGE,"E4.sketch_text.stroke-270"),sQuery(id+"F0.wireOp",EDGE,"E4.sketch_text.stroke-271"),sQuery(id+"F0.wireOp",EDGE,"E4.sketch_text.stroke-272"),sQuery(id+"F0.wireOp",EDGE,"E4.sketch_text.stroke-273"),sQuery(id+"F0.wireOp",EDGE,"E4.sketch_text.stroke-274"),sQuery(id+"F0.wireOp",EDGE,"E4.sketch_text.stroke-275"),sQuery(id+"F0.wireOp",EDGE,"E4.sketch_text.stroke-276"),sQuery(id+"F0.wireOp",EDGE,"E4.sketch_text.stroke-283"),sQuery(id+"F0.wireOp",EDGE,"E4.sketch_text.stroke-284"),sQuery(id+"F0.wireOp",EDGE,"E4.sketch_text.stroke-285"),sQuery(id+"F0.wireOp",EDGE,"E4.sketch_text.stroke-286"),sQuery(id+"F0.wireOp",EDGE,"E4.sketch_text.stroke-287"),sQuery(id+"F0.wireOp",EDGE,"E4.sketch_text.stroke-288"),sQuery(id+"F0.wireOp",EDGE,"E4.sketch_text.stroke-289"),sQuery(id+"F0.wireOp",EDGE,"E4.sketch_text.stroke-290"),sQuery(id+"F0.wireOp",EDGE,"E4.sketch_text.stroke-291"),sQuery(id+"F0.wireOp",EDGE,"E4.sketch_text.stroke-292"),sQuery(id+"F0.wireOp",EDGE,"E4.sketch_text.stroke-293"),sQuery(id+"F0.wireOp",EDGE,"E4.sketch_text.stroke-294"),sQuery(id+"F0.wireOp",EDGE,"E4.sketch_text.stroke-295"),sQuery(id+"F0.wireOp",EDGE,"E4.sketch_text.stroke-296"),sQuery(id+"F0.wireOp",EDGE,"E4.sketch_text.stroke-297"),sQuery(id+"F0.wireOp",EDGE,"E4.sketch_text.stroke-298"),sQuery(id+"F0.wireOp",EDGE,"E4.sketch_text.stroke-299"),sQuery(id+"F0.wireOp",EDGE,"E4.sketch_text.stroke-300"),sQuery(id+"F0.wireOp",EDGE,"E4.sketch_text.stroke-301"),sQuery(id+"F0.wireOp",EDGE,"E4.sketch_text.stroke-302"),sQuery(id+"F0.wireOp",EDGE,"E4.sketch_text.stroke-303"),sQuery(id+"F0.wireOp",EDGE,"E4.sketch_text.stroke-304"),sQuery(id+"F0.wireOp",EDGE,"E4.sketch_text.stroke-305"),sQuery(id+"F0.wireOp",EDGE,"E4.sketch_text.stroke-306"),sQuery(id+"F0.wireOp",EDGE,"E4.sketch_text.stroke-307"),sQuery(id+"F0.wireOp",EDGE,"E4.sketch_text.stroke-308"),sQuery(id+"F0.wireOp",EDGE,"E4.sketch_text.stroke-309"),sQuery(id+"F0.wireOp",EDGE,"E4.sketch_text.stroke-310"),sQuery(id+"F0.wireOp",EDGE,"E4.sketch_text.stroke-321"),sQuery(id+"F0.wireOp",EDGE,"E4.sketch_text.stroke-322"),sQuery(id+"F0.wireOp",EDGE,"E4.sketch_text.stroke-323"),sQuery(id+"F0.wireOp",EDGE,"E4.sketch_text.stroke-324"),sQuery(id+"F0.wireOp",EDGE,"E4.sketch_text.stroke-325"),sQuery(id+"F0.wireOp",EDGE,"E4.sketch_text.stroke-326"),sQuery(id+"F0.wireOp",EDGE,"E4.sketch_text.stroke-327"),sQuery(id+"F0.wireOp",EDGE,"E4.sketch_text.stroke-328"),sQuery(id+"F0.wireOp",EDGE,"E4.sketch_text.stroke-329"),sQuery(id+"F0.wireOp",EDGE,"E4.sketch_text.stroke-330"),sQuery(id+"F0.wireOp",EDGE,"E4.sketch_text.stroke-331"),sQuery(id+"F0.wireOp",EDGE,"E4.sketch_text.stroke-332"),sQuery(id+"F0.wireOp",EDGE,"E4.sketch_text.stroke-333"),sQuery(id+"F0.wireOp",EDGE,"E4.sketch_text.stroke-334"),sQuery(id+"F0.wireOp",EDGE,"E4.sketch_text.stroke-335"),sQuery(id+"F0.wireOp",EDGE,"E4.sketch_text.stroke-336"),sQuery(id+"F0.wireOp",EDGE,"E4.sketch_text.stroke-337"),sQuery(id+"F0.wireOp",EDGE,"E4.sketch_text.stroke-338"),sQuery(id+"F0.wireOp",EDGE,"E4.sketch_text.stroke-339"),sQuery(id+"F0.wireOp",EDGE,"E4.sketch_text.stroke-340"),sQuery(id+"F0.wireOp",EDGE,"E4.sketch_text.stroke-341"),sQuery(id+"F0.wireOp",EDGE,"E4.sketch_text.stroke-342"),sQuery(id+"F0.wireOp",EDGE,"E4.sketch_text.stroke-343"),sQuery(id+"F0.wireOp",EDGE,"E4.sketch_text.stroke-344"),sQuery(id+"F0.wireOp",EDGE,"E4.sketch_text.stroke-345"),sQuery(id+"F0.wireOp",EDGE,"E4.sketch_text.stroke-346"),sQuery(id+"F0.wireOp",EDGE,"E4.sketch_text.stroke-347"),sQuery(id+"F0.wireOp",EDGE,"E4.sketch_text.stroke-348"),sQuery(id+"F0.wireOp",EDGE,"E4.sketch_text.stroke-359"),sQuery(id+"F0.wireOp",EDGE,"E4.sketch_text.stroke-360"),sQuery(id+"F0.wireOp",EDGE,"E4.sketch_text.stroke-361"),sQuery(id+"F0.wireOp",EDGE,"E4.sketch_text.stroke-362"),sQuery(id+"F0.wireOp",EDGE,"E4.sketch_text.stroke-363"),sQuery(id+"F0.wireOp",EDGE,"E4.sketch_text.stroke-364"),sQuery(id+"F0.wireOp",EDGE,"E4.sketch_text.stroke-365"),sQuery(id+"F0.wireOp",EDGE,"E4.sketch_text.stroke-366"),sQuery(id+"F0.wireOp",EDGE,"E4.sketch_text.stroke-367"),sQuery(id+"F0.wireOp",EDGE,"E4.sketch_text.stroke-368"),sQuery(id+"F0.wireOp",EDGE,"E4.sketch_text.stroke-369"),sQuery(id+"F0.wireOp",EDGE,"E4.sketch_text.stroke-370"),sQuery(id+"F0.wireOp",EDGE,"E4.sketch_text.stroke-371"),sQuery(id+"F0.wireOp",EDGE,"E4.sketch_text.stroke-372"),sQuery(id+"F0.wireOp",EDGE,"E4.sketch_text.stroke-373"),sQuery(id+"F0.wireOp",EDGE,"E4.sketch_text.stroke-374"),sQuery(id+"F0.wireOp",EDGE,"E4.sketch_text.stroke-375"),sQuery(id+"F0.wireOp",EDGE,"E4.sketch_text.stroke-376"),sQuery(id+"F0.wireOp",EDGE,"E4.sketch_text.stroke-377"),sQuery(id+"F0.wireOp",EDGE,"E4.sketch_text.stroke-378"),sQuery(id+"F0.wireOp",EDGE,"E4.sketch_text.stroke-379"),sQuery(id+"F0.wireOp",EDGE,"E4.sketch_text.stroke-380"),sQuery(id+"F0.wireOp",EDGE,"E4.sketch_text.stroke-381"),sQuery(id+"F0.wireOp",EDGE,"E4.sketch_text.stroke-382"),sQuery(id+"F0.wireOp",EDGE,"E4.sketch_text.stroke-383"),sQuery(id+"F0.wireOp",EDGE,"E4.sketch_text.stroke-384"),sQuery(id+"F0.wireOp",EDGE,"E4.sketch_text.stroke-385"),sQuery(id+"F0.wireOp",EDGE,"E4.sketch_text.stroke-386"),sQuery(id+"F0.wireOp",EDGE,"E4.sketch_text.stroke-387"),sQuery(id+"F0.wireOp",EDGE,"E4.sketch_text.stroke-388"),sQuery(id+"F0.wireOp",EDGE,"E4.sketch_text.stroke-389"),sQuery(id+"F0.wireOp",EDGE,"E4.sketch_text.stroke-390"),sQuery(id+"F0.wireOp",EDGE,"E4.sketch_text.stroke-391"),sQuery(id+"F0.wireOp",EDGE,"E4.sketch_text.stroke-392")])],"isStart":true})],"blendedInto":[makeQuery(id+"F6.opExtrude","CAP_FACE",FACE,{"disambiguationData":[OSD([subQ1,sQuery(id+"F0.wireOp",EDGE,"E0.top"),sQuery(id+"F0.wireOp",EDGE,"E0.left"),subQ0,sQuery(id+"F0.wireOp",EDGE,"E3.sketch_text.stroke-0"),sQuery(id+"F0.wireOp",EDGE,"E3.sketch_text.stroke-1"),sQuery(id+"F0.wireOp",EDGE,"E3.sketch_text.stroke-2"),sQuery(id+"F0.wireOp",EDGE,"E3.sketch_text.stroke-3"),sQuery(id+"F0.wireOp",EDGE,"E3.sketch_text.stroke-4"),sQuery(id+"F0.wireOp",EDGE,"E3.sketch_text.stroke-5"),sQuery(id+"F0.wireOp",EDGE,"E3.sketch_text.stroke-6"),sQuery(id+"F0.wireOp",EDGE,"E3.sketch_text.stroke-7"),sQuery(id+"F0.wireOp",EDGE,"E3.sketch_text.stroke-8"),sQuery(id+"F0.wireOp",EDGE,"E3.sketch_text.stroke-9"),sQuery(id+"F0.wireOp",EDGE,"E3.sketch_text.stroke-10"),sQuery(id+"F0.wireOp",EDGE,"E3.sketch_text.stroke-11"),sQuery(id+"F0.wireOp",EDGE,"E3.sketch_text.stroke-12"),sQuery(id+"F0.wireOp",EDGE,"E3.sketch_text.stroke-13"),sQuery(id+"F0.wireOp",EDGE,"E3.sketch_text.stroke-14"),sQuery(id+"F0.wireOp",EDGE,"E3.sketch_text.stroke-15"),sQuery(id+"F0.wireOp",EDGE,"E3.sketch_text.stroke-16"),sQuery(id+"F0.wireOp",EDGE,"E3.sketch_text.stroke-17"),sQuery(id+"F0.wireOp",EDGE,"E3.sketch_text.stroke-18"),sQuery(id+"F0.wireOp",EDGE,"E3.sketch_text.stroke-19"),sQuery(id+"F0.wireOp",EDGE,"E3.sketch_text.stroke-20"),sQuery(id+"F0.wireOp",EDGE,"E3.sketch_text.stroke-21"),sQuery(id+"F0.wireOp",EDGE,"E3.sketch_text.stroke-22"),sQuery(id+"F0.wireOp",EDGE,"E3.sketch_text.stroke-23"),sQuery(id+"F0.wireOp",EDGE,"E3.sketch_text.stroke-24"),sQuery(id+"F0.wireOp",EDGE,"E3.sketch_text.stroke-25"),sQuery(id+"F0.wireOp",EDGE,"E3.sketch_text.stroke-26"),sQuery(id+"F0.wireOp",EDGE,"E3.sketch_text.stroke-27"),sQuery(id+"F0.wireOp",EDGE,"E3.sketch_text.stroke-28"),sQuery(id+"F0.wireOp",EDGE,"E3.sketch_text.stroke-29"),sQuery(id+"F0.wireOp",EDGE,"E3.sketch_text.stroke-30"),sQuery(id+"F0.wireOp",EDGE,"E3.sketch_text.stroke-31"),sQuery(id+"F0.wireOp",EDGE,"E3.sketch_text.stroke-32"),sQuery(id+"F0.wireOp",EDGE,"E3.sketch_text.stroke-33"),sQuery(id+"F0.wireOp",EDGE,"E3.sketch_text.stroke-34"),sQuery(id+"F0.wireOp",EDGE,"E3.sketch_text.stroke-35"),sQuery(id+"F0.wireOp",EDGE,"E3.sketch_text.stroke-36"),sQuery(id+"F0.wireOp",EDGE,"E3.sketch_text.stroke-37"),sQuery(id+"F0.wireOp",EDGE,"E3.sketch_text.stroke-38"),sQuery(id+"F0.wireOp",EDGE,"E3.sketch_text.stroke-39"),sQuery(id+"F0.wireOp",EDGE,"E3.sketch_text.stroke-40"),sQuery(id+"F0.wireOp",EDGE,"E3.sketch_text.stroke-41"),sQuery(id+"F0.wireOp",EDGE,"E3.sketch_text.stroke-42"),sQuery(id+"F0.wireOp",EDGE,"E3.sketch_text.stroke-43"),sQuery(id+"F0.wireOp",EDGE,"E3.sketch_text.stroke-44"),sQuery(id+"F0.wireOp",EDGE,"E3.sketch_text.stroke-45"),sQuery(id+"F0.wireOp",EDGE,"E3.sketch_text.stroke-46"),sQuery(id+"F0.wireOp",EDGE,"E3.sketch_text.stroke-47"),sQuery(id+"F0.wireOp",EDGE,"E3.sketch_text.stroke-48"),sQuery(id+"F0.wireOp",EDGE,"E3.sketch_text.stroke-49"),sQuery(id+"F0.wireOp",EDGE,"E3.sketch_text.stroke-50"),sQuery(id+"F0.wireOp",EDGE,"E3.sketch_text.stroke-51"),sQuery(id+"F0.wireOp",EDGE,"E3.sketch_text.stroke-52"),sQuery(id+"F0.wireOp",EDGE,"E3.sketch_text.stroke-53"),sQuery(id+"F0.wireOp",EDGE,"E3.sketch_text.stroke-54"),sQuery(id+"F0.wireOp",EDGE,"E3.sketch_text.stroke-55"),sQuery(id+"F0.wireOp",EDGE,"E3.sketch_text.stroke-56"),sQuery(id+"F0.wireOp",EDGE,"E3.sketch_text.stroke-57"),sQuery(id+"F0.wireOp",EDGE,"E3.sketch_text.stroke-58"),sQuery(id+"F0.wireOp",EDGE,"E3.sketch_text.stroke-59"),sQuery(id+"F0.wireOp",EDGE,"E3.sketch_text.stroke-60"),sQuery(id+"F0.wireOp",EDGE,"E3.sketch_text.stroke-61"),sQuery(id+"F0.wireOp",EDGE,"E3.sketch_text.stroke-62"),sQuery(id+"F0.wireOp",EDGE,"E3.sketch_text.stroke-63"),sQuery(id+"F0.wireOp",EDGE,"E3.sketch_text.stroke-64"),sQuery(id+"F0.wireOp",EDGE,"E3.sketch_text.stroke-65"),sQuery(id+"F0.wireOp",EDGE,"E3.sketch_text.stroke-66"),sQuery(id+"F0.wireOp",EDGE,"E3.sketch_text.stroke-67"),sQuery(id+"F0.wireOp",EDGE,"E3.sketch_text.stroke-68"),sQuery(id+"F0.wireOp",EDGE,"E3.sketch_text.stroke-69"),sQuery(id+"F0.wireOp",EDGE,"E3.sketch_text.stroke-70"),sQuery(id+"F0.wireOp",EDGE,"E3.sketch_text.stroke-71"),sQuery(id+"F0.wireOp",EDGE,"E3.sketch_text.stroke-72"),sQuery(id+"F0.wireOp",EDGE,"E3.sketch_text.stroke-73"),sQuery(id+"F0.wireOp",EDGE,"E3.sketch_text.stroke-74"),sQuery(id+"F0.wireOp",EDGE,"E3.sketch_text.stroke-88"),sQuery(id+"F0.wireOp",EDGE,"E3.sketch_text.stroke-89"),sQuery(id+"F0.wireOp",EDGE,"E3.sketch_text.stroke-90"),sQuery(id+"F0.wireOp",EDGE,"E3.sketch_text.stroke-91"),sQuery(id+"F0.wireOp",EDGE,"E3.sketch_text.stroke-92"),sQuery(id+"F0.wireOp",EDGE,"E3.sketch_text.stroke-93"),sQuery(id+"F0.wireOp",EDGE,"E3.sketch_text.stroke-94"),sQuery(id+"F0.wireOp",EDGE,"E3.sketch_text.stroke-95"),sQuery(id+"F0.wireOp",EDGE,"E3.sketch_text.stroke-96"),sQuery(id+"F0.wireOp",EDGE,"E3.sketch_text.stroke-97"),sQuery(id+"F0.wireOp",EDGE,"E3.sketch_text.stroke-98"),sQuery(id+"F0.wireOp",EDGE,"E3.sketch_text.stroke-99"),sQuery(id+"F0.wireOp",EDGE,"E3.sketch_text.stroke-106"),sQuery(id+"F0.wireOp",EDGE,"E3.sketch_text.stroke-107"),sQuery(id+"F0.wireOp",EDGE,"E3.sketch_text.stroke-108"),sQuery(id+"F0.wireOp",EDGE,"E3.sketch_text.stroke-109"),sQuery(id+"F0.wireOp",EDGE,"E3.sketch_text.stroke-110"),sQuery(id+"F0.wireOp",EDGE,"E3.sketch_text.stroke-111"),sQuery(id+"F0.wireOp",EDGE,"E3.sketch_text.stroke-112"),sQuery(id+"F0.wireOp",EDGE,"E3.sketch_text.stroke-113"),sQuery(id+"F0.wireOp",EDGE,"E3.sketch_text.stroke-114"),sQuery(id+"F0.wireOp",EDGE,"E3.sketch_text.stroke-115"),sQuery(id+"F0.wireOp",EDGE,"E3.sketch_text.stroke-116"),sQuery(id+"F0.wireOp",EDGE,"E3.sketch_text.stroke-117"),sQuery(id+"F0.wireOp",EDGE,"E3.sketch_text.stroke-118"),sQuery(id+"F0.wireOp",EDGE,"E3.sketch_text.stroke-119"),sQuery(id+"F0.wireOp",EDGE,"E3.sketch_text.stroke-120"),sQuery(id+"F0.wireOp",EDGE,"E3.sketch_text.stroke-121"),sQuery(id+"F0.wireOp",EDGE,"E3.sketch_text.stroke-122"),sQuery(id+"F0.wireOp",EDGE,"E3.sketch_text.stroke-123"),sQuery(id+"F0.wireOp",EDGE,"E3.sketch_text.stroke-124"),sQuery(id+"F0.wireOp",EDGE,"E3.sketch_text.stroke-125"),sQuery(id+"F0.wireOp",EDGE,"E3.sketch_text.stroke-126"),sQuery(id+"F0.wireOp",EDGE,"E3.sketch_text.stroke-127"),sQuery(id+"F0.wireOp",EDGE,"E3.sketch_text.stroke-128"),sQuery(id+"F0.wireOp",EDGE,"E3.sketch_text.stroke-129"),sQuery(id+"F0.wireOp",EDGE,"E3.sketch_text.stroke-130"),sQuery(id+"F0.wireOp",EDGE,"E3.sketch_text.stroke-131"),sQuery(id+"F0.wireOp",EDGE,"E3.sketch_text.stroke-132"),sQuery(id+"F0.wireOp",EDGE,"E3.sketch_text.stroke-133"),sQuery(id+"F0.wireOp",EDGE,"E3.sketch_text.stroke-134"),sQuery(id+"F0.wireOp",EDGE,"E3.sketch_text.stroke-135"),sQuery(id+"F0.wireOp",EDGE,"E3.sketch_text.stroke-136"),sQuery(id+"F0.wireOp",EDGE,"E3.sketch_text.stroke-137"),sQuery(id+"F0.wireOp",EDGE,"E3.sketch_text.stroke-138"),sQuery(id+"F0.wireOp",EDGE,"E3.sketch_text.stroke-139"),sQuery(id+"F0.wireOp",EDGE,"E3.sketch_text.stroke-140"),sQuery(id+"F0.wireOp",EDGE,"E3.sketch_text.stroke-141"),sQuery(id+"F0.wireOp",EDGE,"E3.sketch_text.stroke-142"),sQuery(id+"F0.wireOp",EDGE,"E3.sketch_text.stroke-143"),sQuery(id+"F0.wireOp",EDGE,"E3.sketch_text.stroke-144"),sQuery(id+"F0.wireOp",EDGE,"E3.sketch_text.stroke-145"),sQuery(id+"F0.wireOp",EDGE,"E3.sketch_text.stroke-146"),sQuery(id+"F0.wireOp",EDGE,"E3.sketch_text.stroke-147"),sQuery(id+"F0.wireOp",EDGE,"E3.sketch_text.stroke-155"),sQuery(id+"F0.wireOp",EDGE,"E3.sketch_text.stroke-156"),sQuery(id+"F0.wireOp",EDGE,"E3.sketch_text.stroke-157"),sQuery(id+"F0.wireOp",EDGE,"E3.sketch_text.stroke-158"),sQuery(id+"F0.wireOp",EDGE,"E3.sketch_text.stroke-159"),sQuery(id+"F0.wireOp",EDGE,"E3.sketch_text.stroke-160"),sQuery(id+"F0.wireOp",EDGE,"E3.sketch_text.stroke-161"),sQuery(id+"F0.wireOp",EDGE,"E3.sketch_text.stroke-162"),sQuery(id+"F0.wireOp",EDGE,"E3.sketch_text.stroke-163"),sQuery(id+"F0.wireOp",EDGE,"E3.sketch_text.stroke-164"),sQuery(id+"F0.wireOp",EDGE,"E3.sketch_text.stroke-165"),sQuery(id+"F0.wireOp",EDGE,"E3.sketch_text.stroke-166"),sQuery(id+"F0.wireOp",EDGE,"E3.sketch_text.stroke-167"),sQuery(id+"F0.wireOp",EDGE,"E3.sketch_text.stroke-168"),sQuery(id+"F0.wireOp",EDGE,"E3.sketch_text.stroke-169"),sQuery(id+"F0.wireOp",EDGE,"E3.sketch_text.stroke-170"),sQuery(id+"F0.wireOp",EDGE,"E3.sketch_text.stroke-171"),sQuery(id+"F0.wireOp",EDGE,"E3.sketch_text.stroke-172"),sQuery(id+"F0.wireOp",EDGE,"E3.sketch_text.stroke-173"),sQuery(id+"F0.wireOp",EDGE,"E3.sketch_text.stroke-174"),sQuery(id+"F0.wireOp",EDGE,"E3.sketch_text.stroke-175"),sQuery(id+"F0.wireOp",EDGE,"E3.sketch_text.stroke-176"),sQuery(id+"F0.wireOp",EDGE,"E3.sketch_text.stroke-177"),sQuery(id+"F0.wireOp",EDGE,"E3.sketch_text.stroke-178"),sQuery(id+"F0.wireOp",EDGE,"E3.sketch_text.stroke-179"),sQuery(id+"F0.wireOp",EDGE,"E3.sketch_text.stroke-180"),sQuery(id+"F0.wireOp",EDGE,"E3.sketch_text.stroke-181"),sQuery(id+"F0.wireOp",EDGE,"E3.sketch_text.stroke-182"),sQuery(id+"F0.wireOp",EDGE,"E3.sketch_text.stroke-183"),sQuery(id+"F0.wireOp",EDGE,"E3.sketch_text.stroke-184"),sQuery(id+"F0.wireOp",EDGE,"E3.sketch_text.stroke-185"),sQuery(id+"F0.wireOp",EDGE,"E3.sketch_text.stroke-186"),sQuery(id+"F0.wireOp",EDGE,"E3.sketch_text.stroke-187"),sQuery(id+"F0.wireOp",EDGE,"E3.sketch_text.stroke-188"),sQuery(id+"F0.wireOp",EDGE,"E3.sketch_text.stroke-189"),sQuery(id+"F0.wireOp",EDGE,"E3.sketch_text.stroke-190"),sQuery(id+"F0.wireOp",EDGE,"E3.sketch_text.stroke-191"),sQuery(id+"F0.wireOp",EDGE,"E3.sketch_text.stroke-192"),sQuery(id+"F0.wireOp",EDGE,"E3.sketch_text.stroke-193"),sQuery(id+"F0.wireOp",EDGE,"E3.sketch_text.stroke-194"),sQuery(id+"F0.wireOp",EDGE,"E3.sketch_text.stroke-195"),sQuery(id+"F0.wireOp",EDGE,"E3.sketch_text.stroke-196"),sQuery(id+"F0.wireOp",EDGE,"E3.sketch_text.stroke-197"),sQuery(id+"F0.wireOp",EDGE,"E3.sketch_text.stroke-198"),sQuery(id+"F0.wireOp",EDGE,"E3.sketch_text.stroke-199"),sQuery(id+"F0.wireOp",EDGE,"E3.sketch_text.stroke-200"),sQuery(id+"F0.wireOp",EDGE,"E3.sketch_text.stroke-201"),sQuery(id+"F0.wireOp",EDGE,"E3.sketch_text.stroke-202"),sQuery(id+"F0.wireOp",EDGE,"E3.sketch_text.stroke-203"),sQuery(id+"F0.wireOp",EDGE,"E3.sketch_text.stroke-204"),sQuery(id+"F0.wireOp",EDGE,"E3.sketch_text.stroke-205"),sQuery(id+"F0.wireOp",EDGE,"E3.sketch_text.stroke-206"),sQuery(id+"F0.wireOp",EDGE,"E3.sketch_text.stroke-207"),sQuery(id+"F0.wireOp",EDGE,"E3.sketch_text.stroke-208"),sQuery(id+"F0.wireOp",EDGE,"E3.sketch_text.stroke-209"),sQuery(id+"F0.wireOp",EDGE,"E3.sketch_text.stroke-210"),sQuery(id+"F0.wireOp",EDGE,"E3.sketch_text.stroke-211"),sQuery(id+"F0.wireOp",EDGE,"E3.sketch_text.stroke-212"),sQuery(id+"F0.wireOp",EDGE,"E3.sketch_text.stroke-213"),sQuery(id+"F0.wireOp",EDGE,"E3.sketch_text.stroke-214"),sQuery(id+"F0.wireOp",EDGE,"E3.sketch_text.stroke-215"),sQuery(id+"F0.wireOp",EDGE,"E3.sketch_text.stroke-216"),sQuery(id+"F0.wireOp",EDGE,"E3.sketch_text.stroke-217"),sQuery(id+"F0.wireOp",EDGE,"E3.sketch_text.stroke-218"),sQuery(id+"F0.wireOp",EDGE,"E3.sketch_text.stroke-219"),sQuery(id+"F0.wireOp",EDGE,"E3.sketch_text.stroke-220"),sQuery(id+"F0.wireOp",EDGE,"E3.sketch_text.stroke-221"),sQuery(id+"F0.wireOp",EDGE,"E3.sketch_text.stroke-222"),sQuery(id+"F0.wireOp",EDGE,"E3.sketch_text.stroke-223"),sQuery(id+"F0.wireOp",EDGE,"E3.sketch_text.stroke-224"),sQuery(id+"F0.wireOp",EDGE,"E3.sketch_text.stroke-225"),sQuery(id+"F0.wireOp",EDGE,"E3.sketch_text.stroke-226"),sQuery(id+"F0.wireOp",EDGE,"E3.sketch_text.stroke-227"),sQuery(id+"F0.wireOp",EDGE,"E3.sketch_text.stroke-228"),sQuery(id+"F0.wireOp",EDGE,"E3.sketch_text.stroke-229"),sQuery(id+"F0.wireOp",EDGE,"E3.sketch_text.stroke-230"),sQuery(id+"F0.wireOp",EDGE,"E3.sketch_text.stroke-231"),sQuery(id+"F0.wireOp",EDGE,"E3.sketch_text.stroke-232"),sQuery(id+"F0.wireOp",EDGE,"E3.sketch_text.stroke-233"),sQuery(id+"F0.wireOp",EDGE,"E3.sketch_text.stroke-234"),sQuery(id+"F0.wireOp",EDGE,"E3.sketch_text.stroke-235"),sQuery(id+"F0.wireOp",EDGE,"E3.sketch_text.stroke-236"),sQuery(id+"F0.wireOp",EDGE,"E3.sketch_text.stroke-237"),sQuery(id+"F0.wireOp",EDGE,"E3.sketch_text.stroke-238"),sQuery(id+"F0.wireOp",EDGE,"E3.sketch_text.stroke-244"),sQuery(id+"F0.wireOp",EDGE,"E3.sketch_text.stroke-245"),sQuery(id+"F0.wireOp",EDGE,"E3.sketch_text.stroke-246"),sQuery(id+"F0.wireOp",EDGE,"E3.sketch_text.stroke-247"),sQuery(id+"F0.wireOp",EDGE,"E3.sketch_text.stroke-248"),sQuery(id+"F0.wireOp",EDGE,"E3.sketch_text.stroke-249"),sQuery(id+"F0.wireOp",EDGE,"E3.sketch_text.stroke-250"),sQuery(id+"F0.wireOp",EDGE,"E3.sketch_text.stroke-251"),sQuery(id+"F0.wireOp",EDGE,"E3.sketch_text.stroke-252"),sQuery(id+"F0.wireOp",EDGE,"E3.sketch_text.stroke-253"),sQuery(id+"F0.wireOp",EDGE,"E3.sketch_text.stroke-254"),sQuery(id+"F0.wireOp",EDGE,"E3.sketch_text.stroke-255"),sQuery(id+"F0.wireOp",EDGE,"E3.sketch_text.stroke-256"),sQuery(id+"F0.wireOp",EDGE,"E3.sketch_text.stroke-257"),sQuery(id+"F0.wireOp",EDGE,"E3.sketch_text.stroke-258"),sQuery(id+"F0.wireOp",EDGE,"E3.sketch_text.stroke-259"),sQuery(id+"F0.wireOp",EDGE,"E3.sketch_text.stroke-260"),sQuery(id+"F0.wireOp",EDGE,"E4.sketch_text.stroke-0"),sQuery(id+"F0.wireOp",EDGE,"E4.sketch_text.stroke-1"),sQuery(id+"F0.wireOp",EDGE,"E4.sketch_text.stroke-2"),sQuery(id+"F0.wireOp",EDGE,"E4.sketch_text.stroke-3"),sQuery(id+"F0.wireOp",EDGE,"E4.sketch_text.stroke-4"),sQuery(id+"F0.wireOp",EDGE,"E4.sketch_text.stroke-5"),sQuery(id+"F0.wireOp",EDGE,"E4.sketch_text.stroke-6"),sQuery(id+"F0.wireOp",EDGE,"E4.sketch_text.stroke-7"),sQuery(id+"F0.wireOp",EDGE,"E4.sketch_text.stroke-8"),sQuery(id+"F0.wireOp",EDGE,"E4.sketch_text.stroke-9"),sQuery(id+"F0.wireOp",EDGE,"E4.sketch_text.stroke-10"),sQuery(id+"F0.wireOp",EDGE,"E4.sketch_text.stroke-11"),sQuery(id+"F0.wireOp",EDGE,"E4.sketch_text.stroke-12"),sQuery(id+"F0.wireOp",EDGE,"E4.sketch_text.stroke-13"),sQuery(id+"F0.wireOp",EDGE,"E4.sketch_text.stroke-14"),sQuery(id+"F0.wireOp",EDGE,"E4.sketch_text.stroke-15"),sQuery(id+"F0.wireOp",EDGE,"E4.sketch_text.stroke-16"),sQuery(id+"F0.wireOp",EDGE,"E4.sketch_text.stroke-17"),sQuery(id+"F0.wireOp",EDGE,"E4.sketch_text.stroke-18"),sQuery(id+"F0.wireOp",EDGE,"E4.sketch_text.stroke-19"),sQuery(id+"F0.wireOp",EDGE,"E4.sketch_text.stroke-20"),sQuery(id+"F0.wireOp",EDGE,"E4.sketch_text.stroke-21"),sQuery(id+"F0.wireOp",EDGE,"E4.sketch_text.stroke-28"),sQuery(id+"F0.wireOp",EDGE,"E4.sketch_text.stroke-29"),sQuery(id+"F0.wireOp",EDGE,"E4.sketch_text.stroke-30"),sQuery(id+"F0.wireOp",EDGE,"E4.sketch_text.stroke-31"),sQuery(id+"F0.wireOp",EDGE,"E4.sketch_text.stroke-32"),sQuery(id+"F0.wireOp",EDGE,"E4.sketch_text.stroke-33"),sQuery(id+"F0.wireOp",EDGE,"E4.sketch_text.stroke-34"),sQuery(id+"F0.wireOp",EDGE,"E4.sketch_text.stroke-35"),sQuery(id+"F0.wireOp",EDGE,"E4.sketch_text.stroke-36"),sQuery(id+"F0.wireOp",EDGE,"E4.sketch_text.stroke-37"),sQuery(id+"F0.wireOp",EDGE,"E4.sketch_text.stroke-38"),sQuery(id+"F0.wireOp",EDGE,"E4.sketch_text.stroke-39"),sQuery(id+"F0.wireOp",EDGE,"E4.sketch_text.stroke-40"),sQuery(id+"F0.wireOp",EDGE,"E4.sketch_text.stroke-41"),sQuery(id+"F0.wireOp",EDGE,"E4.sketch_text.stroke-42"),sQuery(id+"F0.wireOp",EDGE,"E4.sketch_text.stroke-43"),sQuery(id+"F0.wireOp",EDGE,"E4.sketch_text.stroke-44"),sQuery(id+"F0.wireOp",EDGE,"E4.sketch_text.stroke-45"),sQuery(id+"F0.wireOp",EDGE,"E4.sketch_text.stroke-46"),sQuery(id+"F0.wireOp",EDGE,"E4.sketch_text.stroke-47"),sQuery(id+"F0.wireOp",EDGE,"E4.sketch_text.stroke-48"),sQuery(id+"F0.wireOp",EDGE,"E4.sketch_text.stroke-49"),sQuery(id+"F0.wireOp",EDGE,"E4.sketch_text.stroke-50"),sQuery(id+"F0.wireOp",EDGE,"E4.sketch_text.stroke-51"),sQuery(id+"F0.wireOp",EDGE,"E4.sketch_text.stroke-52"),sQuery(id+"F0.wireOp",EDGE,"E4.sketch_text.stroke-53"),sQuery(id+"F0.wireOp",EDGE,"E4.sketch_text.stroke-54"),sQuery(id+"F0.wireOp",EDGE,"E4.sketch_text.stroke-55"),sQuery(id+"F0.wireOp",EDGE,"E4.sketch_text.stroke-56"),sQuery(id+"F0.wireOp",EDGE,"E4.sketch_text.stroke-57"),sQuery(id+"F0.wireOp",EDGE,"E4.sketch_text.stroke-58"),sQuery(id+"F0.wireOp",EDGE,"E4.sketch_text.stroke-59"),sQuery(id+"F0.wireOp",EDGE,"E4.sketch_text.stroke-60"),sQuery(id+"F0.wireOp",EDGE,"E4.sketch_text.stroke-61"),sQuery(id+"F0.wireOp",EDGE,"E4.sketch_text.stroke-62"),sQuery(id+"F0.wireOp",EDGE,"E4.sketch_text.stroke-63"),sQuery(id+"F0.wireOp",EDGE,"E4.sketch_text.stroke-64"),sQuery(id+"F0.wireOp",EDGE,"E4.sketch_text.stroke-65"),sQuery(id+"F0.wireOp",EDGE,"E4.sketch_text.stroke-66"),sQuery(id+"F0.wireOp",EDGE,"E4.sketch_text.stroke-67"),sQuery(id+"F0.wireOp",EDGE,"E4.sketch_text.stroke-68"),sQuery(id+"F0.wireOp",EDGE,"E4.sketch_text.stroke-69"),sQuery(id+"F0.wireOp",EDGE,"E4.sketch_text.stroke-70"),sQuery(id+"F0.wireOp",EDGE,"E4.sketch_text.stroke-71"),sQuery(id+"F0.wireOp",EDGE,"E4.sketch_text.stroke-72"),sQuery(id+"F0.wireOp",EDGE,"E4.sketch_text.stroke-73"),sQuery(id+"F0.wireOp",EDGE,"E4.sketch_text.stroke-74"),sQuery(id+"F0.wireOp",EDGE,"E4.sketch_text.stroke-85"),sQuery(id+"F0.wireOp",EDGE,"E4.sketch_text.stroke-86"),sQuery(id+"F0.wireOp",EDGE,"E4.sketch_text.stroke-87"),sQuery(id+"F0.wireOp",EDGE,"E4.sketch_text.stroke-88"),sQuery(id+"F0.wireOp",EDGE,"E4.sketch_text.stroke-89"),sQuery(id+"F0.wireOp",EDGE,"E4.sketch_text.stroke-90"),sQuery(id+"F0.wireOp",EDGE,"E4.sketch_text.stroke-91"),sQuery(id+"F0.wireOp",EDGE,"E4.sketch_text.stroke-92"),sQuery(id+"F0.wireOp",EDGE,"E4.sketch_text.stroke-93"),sQuery(id+"F0.wireOp",EDGE,"E4.sketch_text.stroke-94"),sQuery(id+"F0.wireOp",EDGE,"E4.sketch_text.stroke-95"),sQuery(id+"F0.wireOp",EDGE,"E4.sketch_text.stroke-96"),sQuery(id+"F0.wireOp",EDGE,"E4.sketch_text.stroke-97"),sQuery(id+"F0.wireOp",EDGE,"E4.sketch_text.stroke-98"),sQuery(id+"F0.wireOp",EDGE,"E4.sketch_text.stroke-99"),sQuery(id+"F0.wireOp",EDGE,"E4.sketch_text.stroke-100"),sQuery(id+"F0.wireOp",EDGE,"E4.sketch_text.stroke-101"),sQuery(id+"F0.wireOp",EDGE,"E4.sketch_text.stroke-102"),sQuery(id+"F0.wireOp",EDGE,"E4.sketch_text.stroke-103"),sQuery(id+"F0.wireOp",EDGE,"E4.sketch_text.stroke-104"),sQuery(id+"F0.wireOp",EDGE,"E4.sketch_text.stroke-105"),sQuery(id+"F0.wireOp",EDGE,"E4.sketch_text.stroke-106"),sQuery(id+"F0.wireOp",EDGE,"E4.sketch_text.stroke-107"),sQuery(id+"F0.wireOp",EDGE,"E4.sketch_text.stroke-108"),sQuery(id+"F0.wireOp",EDGE,"E4.sketch_text.stroke-109"),sQuery(id+"F0.wireOp",EDGE,"E4.sketch_text.stroke-110"),sQuery(id+"F0.wireOp",EDGE,"E4.sketch_text.stroke-111"),sQuery(id+"F0.wireOp",EDGE,"E4.sketch_text.stroke-112"),sQuery(id+"F0.wireOp",EDGE,"E4.sketch_text.stroke-113"),sQuery(id+"F0.wireOp",EDGE,"E4.sketch_text.stroke-114"),sQuery(id+"F0.wireOp",EDGE,"E4.sketch_text.stroke-115"),sQuery(id+"F0.wireOp",EDGE,"E4.sketch_text.stroke-116"),sQuery(id+"F0.wireOp",EDGE,"E4.sketch_text.stroke-117"),sQuery(id+"F0.wireOp",EDGE,"E4.sketch_text.stroke-118"),sQuery(id+"F0.wireOp",EDGE,"E4.sketch_text.stroke-119"),sQuery(id+"F0.wireOp",EDGE,"E4.sketch_text.stroke-120"),sQuery(id+"F0.wireOp",EDGE,"E4.sketch_text.stroke-121"),sQuery(id+"F0.wireOp",EDGE,"E4.sketch_text.stroke-122"),sQuery(id+"F0.wireOp",EDGE,"E4.sketch_text.stroke-123"),sQuery(id+"F0.wireOp",EDGE,"E4.sketch_text.stroke-124"),sQuery(id+"F0.wireOp",EDGE,"E4.sketch_text.stroke-138"),sQuery(id+"F0.wireOp",EDGE,"E4.sketch_text.stroke-139"),sQuery(id+"F0.wireOp",EDGE,"E4.sketch_text.stroke-140"),sQuery(id+"F0.wireOp",EDGE,"E4.sketch_text.stroke-141"),sQuery(id+"F0.wireOp",EDGE,"E4.sketch_text.stroke-142"),sQuery(id+"F0.wireOp",EDGE,"E4.sketch_text.stroke-143"),sQuery(id+"F0.wireOp",EDGE,"E4.sketch_text.stroke-144"),sQuery(id+"F0.wireOp",EDGE,"E4.sketch_text.stroke-145"),sQuery(id+"F0.wireOp",EDGE,"E4.sketch_text.stroke-146"),sQuery(id+"F0.wireOp",EDGE,"E4.sketch_text.stroke-147"),sQuery(id+"F0.wireOp",EDGE,"E4.sketch_text.stroke-148"),sQuery(id+"F0.wireOp",EDGE,"E4.sketch_text.stroke-149"),sQuery(id+"F0.wireOp",EDGE,"E4.sketch_text.stroke-156"),sQuery(id+"F0.wireOp",EDGE,"E4.sketch_text.stroke-157"),sQuery(id+"F0.wireOp",EDGE,"E4.sketch_text.stroke-158"),sQuery(id+"F0.wireOp",EDGE,"E4.sketch_text.stroke-159"),sQuery(id+"F0.wireOp",EDGE,"E4.sketch_text.stroke-160"),sQuery(id+"F0.wireOp",EDGE,"E4.sketch_text.stroke-161"),sQuery(id+"F0.wireOp",EDGE,"E4.sketch_text.stroke-162"),sQuery(id+"F0.wireOp",EDGE,"E4.sketch_text.stroke-163"),sQuery(id+"F0.wireOp",EDGE,"E4.sketch_text.stroke-164"),sQuery(id+"F0.wireOp",EDGE,"E4.sketch_text.stroke-165"),sQuery(id+"F0.wireOp",EDGE,"E4.sketch_text.stroke-166"),sQuery(id+"F0.wireOp",EDGE,"E4.sketch_text.stroke-167"),sQuery(id+"F0.wireOp",EDGE,"E4.sketch_text.stroke-168"),sQuery(id+"F0.wireOp",EDGE,"E4.sketch_text.stroke-169"),sQuery(id+"F0.wireOp",EDGE,"E4.sketch_text.stroke-170"),sQuery(id+"F0.wireOp",EDGE,"E4.sketch_text.stroke-171"),sQuery(id+"F0.wireOp",EDGE,"E4.sketch_text.stroke-172"),sQuery(id+"F0.wireOp",EDGE,"E4.sketch_text.stroke-173"),sQuery(id+"F0.wireOp",EDGE,"E4.sketch_text.stroke-174"),sQuery(id+"F0.wireOp",EDGE,"E4.sketch_text.stroke-175"),sQuery(id+"F0.wireOp",EDGE,"E4.sketch_text.stroke-176"),sQuery(id+"F0.wireOp",EDGE,"E4.sketch_text.stroke-177"),sQuery(id+"F0.wireOp",EDGE,"E4.sketch_text.stroke-178"),sQuery(id+"F0.wireOp",EDGE,"E4.sketch_text.stroke-179"),sQuery(id+"F0.wireOp",EDGE,"E4.sketch_text.stroke-180"),sQuery(id+"F0.wireOp",EDGE,"E4.sketch_text.stroke-181"),sQuery(id+"F0.wireOp",EDGE,"E4.sketch_text.stroke-182"),sQuery(id+"F0.wireOp",EDGE,"E4.sketch_text.stroke-183"),sQuery(id+"F0.wireOp",EDGE,"E4.sketch_text.stroke-184"),sQuery(id+"F0.wireOp",EDGE,"E4.sketch_text.stroke-185"),sQuery(id+"F0.wireOp",EDGE,"E4.sketch_text.stroke-186"),sQuery(id+"F0.wireOp",EDGE,"E4.sketch_text.stroke-187"),sQuery(id+"F0.wireOp",EDGE,"E4.sketch_text.stroke-188"),sQuery(id+"F0.wireOp",EDGE,"E4.sketch_text.stroke-189"),sQuery(id+"F0.wireOp",EDGE,"E4.sketch_text.stroke-190"),sQuery(id+"F0.wireOp",EDGE,"E4.sketch_text.stroke-191"),sQuery(id+"F0.wireOp",EDGE,"E4.sketch_text.stroke-192"),sQuery(id+"F0.wireOp",EDGE,"E4.sketch_text.stroke-193"),sQuery(id+"F0.wireOp",EDGE,"E4.sketch_text.stroke-194"),sQuery(id+"F0.wireOp",EDGE,"E4.sketch_text.stroke-195"),sQuery(id+"F0.wireOp",EDGE,"E4.sketch_text.stroke-196"),sQuery(id+"F0.wireOp",EDGE,"E4.sketch_text.stroke-197"),sQuery(id+"F0.wireOp",EDGE,"E4.sketch_text.stroke-198"),sQuery(id+"F0.wireOp",EDGE,"E4.sketch_text.stroke-199"),sQuery(id+"F0.wireOp",EDGE,"E4.sketch_text.stroke-200"),sQuery(id+"F0.wireOp",EDGE,"E4.sketch_text.stroke-201"),sQuery(id+"F0.wireOp",EDGE,"E4.sketch_text.stroke-208"),sQuery(id+"F0.wireOp",EDGE,"E4.sketch_text.stroke-209"),sQuery(id+"F0.wireOp",EDGE,"E4.sketch_text.stroke-210"),sQuery(id+"F0.wireOp",EDGE,"E4.sketch_text.stroke-211"),sQuery(id+"F0.wireOp",EDGE,"E4.sketch_text.stroke-212"),sQuery(id+"F0.wireOp",EDGE,"E4.sketch_text.stroke-213"),sQuery(id+"F0.wireOp",EDGE,"E4.sketch_text.stroke-214"),sQuery(id+"F0.wireOp",EDGE,"E4.sketch_text.stroke-215"),sQuery(id+"F0.wireOp",EDGE,"E4.sketch_text.stroke-216"),sQuery(id+"F0.wireOp",EDGE,"E4.sketch_text.stroke-217"),sQuery(id+"F0.wireOp",EDGE,"E4.sketch_text.stroke-218"),sQuery(id+"F0.wireOp",EDGE,"E4.sketch_text.stroke-219"),sQuery(id+"F0.wireOp",EDGE,"E4.sketch_text.stroke-220"),sQuery(id+"F0.wireOp",EDGE,"E4.sketch_text.stroke-221"),sQuery(id+"F0.wireOp",EDGE,"E4.sketch_text.stroke-222"),sQuery(id+"F0.wireOp",EDGE,"E4.sketch_text.stroke-223"),sQuery(id+"F0.wireOp",EDGE,"E4.sketch_text.stroke-224"),sQuery(id+"F0.wireOp",EDGE,"E4.sketch_text.stroke-225"),sQuery(id+"F0.wireOp",EDGE,"E4.sketch_text.stroke-226"),sQuery(id+"F0.wireOp",EDGE,"E4.sketch_text.stroke-227"),sQuery(id+"F0.wireOp",EDGE,"E4.sketch_text.stroke-228"),sQuery(id+"F0.wireOp",EDGE,"E4.sketch_text.stroke-229"),sQuery(id+"F0.wireOp",EDGE,"E4.sketch_text.stroke-230"),sQuery(id+"F0.wireOp",EDGE,"E4.sketch_text.stroke-231"),sQuery(id+"F0.wireOp",EDGE,"E4.sketch_text.stroke-232"),sQuery(id+"F0.wireOp",EDGE,"E4.sketch_text.stroke-233"),sQuery(id+"F0.wireOp",EDGE,"E4.sketch_text.stroke-234"),sQuery(id+"F0.wireOp",EDGE,"E4.sketch_text.stroke-235"),sQuery(id+"F0.wireOp",EDGE,"E4.sketch_text.stroke-236"),sQuery(id+"F0.wireOp",EDGE,"E4.sketch_text.stroke-237"),sQuery(id+"F0.wireOp",EDGE,"E4.sketch_text.stroke-238"),sQuery(id+"F0.wireOp",EDGE,"E4.sketch_text.stroke-239"),sQuery(id+"F0.wireOp",EDGE,"E4.sketch_text.stroke-240"),sQuery(id+"F0.wireOp",EDGE,"E4.sketch_text.stroke-241"),sQuery(id+"F0.wireOp",EDGE,"E4.sketch_text.stroke-242"),sQuery(id+"F0.wireOp",EDGE,"E4.sketch_text.stroke-243"),sQuery(id+"F0.wireOp",EDGE,"E4.sketch_text.stroke-244"),sQuery(id+"F0.wireOp",EDGE,"E4.sketch_text.stroke-245"),sQuery(id+"F0.wireOp",EDGE,"E4.sketch_text.stroke-246"),sQuery(id+"F0.wireOp",EDGE,"E4.sketch_text.stroke-247"),sQuery(id+"F0.wireOp",EDGE,"E4.sketch_text.stroke-248"),sQuery(id+"F0.wireOp",EDGE,"E4.sketch_text.stroke-249"),sQuery(id+"F0.wireOp",EDGE,"E4.sketch_text.stroke-250"),sQuery(id+"F0.wireOp",EDGE,"E4.sketch_text.stroke-251"),sQuery(id+"F0.wireOp",EDGE,"E4.sketch_text.stroke-252"),sQuery(id+"F0.wireOp",EDGE,"E4.sketch_text.stroke-253"),sQuery(id+"F0.wireOp",EDGE,"E4.sketch_text.stroke-254"),sQuery(id+"F0.wireOp",EDGE,"E4.sketch_text.stroke-255"),sQuery(id+"F0.wireOp",EDGE,"E4.sketch_text.stroke-256"),sQuery(id+"F0.wireOp",EDGE,"E4.sketch_text.stroke-257"),sQuery(id+"F0.wireOp",EDGE,"E4.sketch_text.stroke-258"),sQuery(id+"F0.wireOp",EDGE,"E4.sketch_text.stroke-259"),sQuery(id+"F0.wireOp",EDGE,"E4.sketch_text.stroke-260"),sQuery(id+"F0.wireOp",EDGE,"E4.sketch_text.stroke-261"),sQuery(id+"F0.wireOp",EDGE,"E4.sketch_text.stroke-262"),sQuery(id+"F0.wireOp",EDGE,"E4.sketch_text.stroke-263"),sQuery(id+"F0.wireOp",EDGE,"E4.sketch_text.stroke-264"),sQuery(id+"F0.wireOp",EDGE,"E4.sketch_text.stroke-265"),sQuery(id+"F0.wireOp",EDGE,"E4.sketch_text.stroke-266"),sQuery(id+"F0.wireOp",EDGE,"E4.sketch_text.stroke-267"),sQuery(id+"F0.wireOp",EDGE,"E4.sketch_text.stroke-268"),sQuery(id+"F0.wireOp",EDGE,"E4.sketch_text.stroke-269"),sQuery(id+"F0.wireOp",EDGE,"E4.sketch_text.stroke-270"),sQuery(id+"F0.wireOp",EDGE,"E4.sketch_text.stroke-271"),sQuery(id+"F0.wireOp",EDGE,"E4.sketch_text.stroke-272"),sQuery(id+"F0.wireOp",EDGE,"E4.sketch_text.stroke-273"),sQuery(id+"F0.wireOp",EDGE,"E4.sketch_text.stroke-274"),sQuery(id+"F0.wireOp",EDGE,"E4.sketch_text.stroke-275"),sQuery(id+"F0.wireOp",EDGE,"E4.sketch_text.stroke-276"),sQuery(id+"F0.wireOp",EDGE,"E4.sketch_text.stroke-283"),sQuery(id+"F0.wireOp",EDGE,"E4.sketch_text.stroke-284"),sQuery(id+"F0.wireOp",EDGE,"E4.sketch_text.stroke-285"),sQuery(id+"F0.wireOp",EDGE,"E4.sketch_text.stroke-286"),sQuery(id+"F0.wireOp",EDGE,"E4.sketch_text.stroke-287"),sQuery(id+"F0.wireOp",EDGE,"E4.sketch_text.stroke-288"),sQuery(id+"F0.wireOp",EDGE,"E4.sketch_text.stroke-289"),sQuery(id+"F0.wireOp",EDGE,"E4.sketch_text.stroke-290"),sQuery(id+"F0.wireOp",EDGE,"E4.sketch_text.stroke-291"),sQuery(id+"F0.wireOp",EDGE,"E4.sketch_text.stroke-292"),sQuery(id+"F0.wireOp",EDGE,"E4.sketch_text.stroke-293"),sQuery(id+"F0.wireOp",EDGE,"E4.sketch_text.stroke-294"),sQuery(id+"F0.wireOp",EDGE,"E4.sketch_text.stroke-295"),sQuery(id+"F0.wireOp",EDGE,"E4.sketch_text.stroke-296"),sQuery(id+"F0.wireOp",EDGE,"E4.sketch_text.stroke-297"),sQuery(id+"F0.wireOp",EDGE,"E4.sketch_text.stroke-298"),sQuery(id+"F0.wireOp",EDGE,"E4.sketch_text.stroke-299"),sQuery(id+"F0.wireOp",EDGE,"E4.sketch_text.stroke-300"),sQuery(id+"F0.wireOp",EDGE,"E4.sketch_text.stroke-301"),sQuery(id+"F0.wireOp",EDGE,"E4.sketch_text.stroke-302"),sQuery(id+"F0.wireOp",EDGE,"E4.sketch_text.stroke-303"),sQuery(id+"F0.wireOp",EDGE,"E4.sketch_text.stroke-304"),sQuery(id+"F0.wireOp",EDGE,"E4.sketch_text.stroke-305"),sQuery(id+"F0.wireOp",EDGE,"E4.sketch_text.stroke-306"),sQuery(id+"F0.wireOp",EDGE,"E4.sketch_text.stroke-307"),sQuery(id+"F0.wireOp",EDGE,"E4.sketch_text.stroke-308"),sQuery(id+"F0.wireOp",EDGE,"E4.sketch_text.stroke-309"),sQuery(id+"F0.wireOp",EDGE,"E4.sketch_text.stroke-310"),sQuery(id+"F0.wireOp",EDGE,"E4.sketch_text.stroke-321"),sQuery(id+"F0.wireOp",EDGE,"E4.sketch_text.stroke-322"),sQuery(id+"F0.wireOp",EDGE,"E4.sketch_text.stroke-323"),sQuery(id+"F0.wireOp",EDGE,"E4.sketch_text.stroke-324"),sQuery(id+"F0.wireOp",EDGE,"E4.sketch_text.stroke-325"),sQuery(id+"F0.wireOp",EDGE,"E4.sketch_text.stroke-326"),sQuery(id+"F0.wireOp",EDGE,"E4.sketch_text.stroke-327"),sQuery(id+"F0.wireOp",EDGE,"E4.sketch_text.stroke-328"),sQuery(id+"F0.wireOp",EDGE,"E4.sketch_text.stroke-329"),sQuery(id+"F0.wireOp",EDGE,"E4.sketch_text.stroke-330"),sQuery(id+"F0.wireOp",EDGE,"E4.sketch_text.stroke-331"),sQuery(id+"F0.wireOp",EDGE,"E4.sketch_text.stroke-332"),sQuery(id+"F0.wireOp",EDGE,"E4.sketch_text.stroke-333"),sQuery(id+"F0.wireOp",EDGE,"E4.sketch_text.stroke-334"),sQuery(id+"F0.wireOp",EDGE,"E4.sketch_text.stroke-335"),sQuery(id+"F0.wireOp",EDGE,"E4.sketch_text.stroke-336"),sQuery(id+"F0.wireOp",EDGE,"E4.sketch_text.stroke-337"),sQuery(id+"F0.wireOp",EDGE,"E4.sketch_text.stroke-338"),sQuery(id+"F0.wireOp",EDGE,"E4.sketch_text.stroke-339"),sQuery(id+"F0.wireOp",EDGE,"E4.sketch_text.stroke-340"),sQuery(id+"F0.wireOp",EDGE,"E4.sketch_text.stroke-341"),sQuery(id+"F0.wireOp",EDGE,"E4.sketch_text.stroke-342"),sQuery(id+"F0.wireOp",EDGE,"E4.sketch_text.stroke-343"),sQuery(id+"F0.wireOp",EDGE,"E4.sketch_text.stroke-344"),sQuery(id+"F0.wireOp",EDGE,"E4.sketch_text.stroke-345"),sQuery(id+"F0.wireOp",EDGE,"E4.sketch_text.stroke-346"),sQuery(id+"F0.wireOp",EDGE,"E4.sketch_text.stroke-347"),sQuery(id+"F0.wireOp",EDGE,"E4.sketch_text.stroke-348"),sQuery(id+"F0.wireOp",EDGE,"E4.sketch_text.stroke-359"),sQuery(id+"F0.wireOp",EDGE,"E4.sketch_text.stroke-360"),sQuery(id+"F0.wireOp",EDGE,"E4.sketch_text.stroke-361"),sQuery(id+"F0.wireOp",EDGE,"E4.sketch_text.stroke-362"),sQuery(id+"F0.wireOp",EDGE,"E4.sketch_text.stroke-363"),sQuery(id+"F0.wireOp",EDGE,"E4.sketch_text.stroke-364"),sQuery(id+"F0.wireOp",EDGE,"E4.sketch_text.stroke-365"),sQuery(id+"F0.wireOp",EDGE,"E4.sketch_text.stroke-366"),sQuery(id+"F0.wireOp",EDGE,"E4.sketch_text.stroke-367"),sQuery(id+"F0.wireOp",EDGE,"E4.sketch_text.stroke-368"),sQuery(id+"F0.wireOp",EDGE,"E4.sketch_text.stroke-369"),sQuery(id+"F0.wireOp",EDGE,"E4.sketch_text.stroke-370"),sQuery(id+"F0.wireOp",EDGE,"E4.sketch_text.stroke-371"),sQuery(id+"F0.wireOp",EDGE,"E4.sketch_text.stroke-372"),sQuery(id+"F0.wireOp",EDGE,"E4.sketch_text.stroke-373"),sQuery(id+"F0.wireOp",EDGE,"E4.sketch_text.stroke-374"),sQuery(id+"F0.wireOp",EDGE,"E4.sketch_text.stroke-375"),sQuery(id+"F0.wireOp",EDGE,"E4.sketch_text.stroke-376"),sQuery(id+"F0.wireOp",EDGE,"E4.sketch_text.stroke-377"),sQuery(id+"F0.wireOp",EDGE,"E4.sketch_text.stroke-378"),sQuery(id+"F0.wireOp",EDGE,"E4.sketch_text.stroke-379"),sQuery(id+"F0.wireOp",EDGE,"E4.sketch_text.stroke-380"),sQuery(id+"F0.wireOp",EDGE,"E4.sketch_text.stroke-381"),sQuery(id+"F0.wireOp",EDGE,"E4.sketch_text.stroke-382"),sQuery(id+"F0.wireOp",EDGE,"E4.sketch_text.stroke-383"),sQuery(id+"F0.wireOp",EDGE,"E4.sketch_text.stroke-384"),sQuery(id+"F0.wireOp",EDGE,"E4.sketch_text.stroke-385"),sQuery(id+"F0.wireOp",EDGE,"E4.sketch_text.stroke-386"),sQuery(id+"F0.wireOp",EDGE,"E4.sketch_text.stroke-387"),sQuery(id+"F0.wireOp",EDGE,"E4.sketch_text.stroke-388"),sQuery(id+"F0.wireOp",EDGE,"E4.sketch_text.stroke-389"),sQuery(id+"F0.wireOp",EDGE,"E4.sketch_text.stroke-390"),sQuery(id+"F0.wireOp",EDGE,"E4.sketch_text.stroke-391"),sQuery(id+"F0.wireOp",EDGE,"E4.sketch_text.stroke-392")])],"isStart":true})]});}
            var Q1;
            Q1=makeQuery(id+"F6.opExtrude","CAP_EDGE",EDGE,{"disambiguationData":[OSD([sQuery(id+"F0.wireOp",EDGE,"E0.right")])],"isStart":true});
            var Q2;
            Q2=makeQuery(id+"F6.opExtrude","CAP_EDGE",EDGE,{"disambiguationData":[OSD([sQuery(id+"F0.wireOp",EDGE,"E0.top")])],"isStart":true});
            var Q3;
            {var subQ0=sQuery(id+"F0.wireOp",EDGE,"E0.right");var subQ1=sQuery(id+"F0.wireOp",EDGE,"E0.top");Q3=makeQuery(id+"F9.opFillet","BLEND_EDGE",EDGE,{"blendedFrom":[makeQuery(id+"F6.opExtrude","SWEPT_EDGE",EDGE,{"disambiguationData":[OSD([subQ1,subQ0])]}),makeQuery(id+"F6.opExtrude","CAP_FACE",FACE,{"disambiguationData":[OSD([sQuery(id+"F0.wireOp",EDGE,"E0.bottom"),subQ1,sQuery(id+"F0.wireOp",EDGE,"E0.left"),subQ0,sQuery(id+"F0.wireOp",EDGE,"E3.sketch_text.stroke-0"),sQuery(id+"F0.wireOp",EDGE,"E3.sketch_text.stroke-1"),sQuery(id+"F0.wireOp",EDGE,"E3.sketch_text.stroke-2"),sQuery(id+"F0.wireOp",EDGE,"E3.sketch_text.stroke-3"),sQuery(id+"F0.wireOp",EDGE,"E3.sketch_text.stroke-4"),sQuery(id+"F0.wireOp",EDGE,"E3.sketch_text.stroke-5"),sQuery(id+"F0.wireOp",EDGE,"E3.sketch_text.stroke-6"),sQuery(id+"F0.wireOp",EDGE,"E3.sketch_text.stroke-7"),sQuery(id+"F0.wireOp",EDGE,"E3.sketch_text.stroke-8"),sQuery(id+"F0.wireOp",EDGE,"E3.sketch_text.stroke-9"),sQuery(id+"F0.wireOp",EDGE,"E3.sketch_text.stroke-10"),sQuery(id+"F0.wireOp",EDGE,"E3.sketch_text.stroke-11"),sQuery(id+"F0.wireOp",EDGE,"E3.sketch_text.stroke-12"),sQuery(id+"F0.wireOp",EDGE,"E3.sketch_text.stroke-13"),sQuery(id+"F0.wireOp",EDGE,"E3.sketch_text.stroke-14"),sQuery(id+"F0.wireOp",EDGE,"E3.sketch_text.stroke-15"),sQuery(id+"F0.wireOp",EDGE,"E3.sketch_text.stroke-16"),sQuery(id+"F0.wireOp",EDGE,"E3.sketch_text.stroke-17"),sQuery(id+"F0.wireOp",EDGE,"E3.sketch_text.stroke-18"),sQuery(id+"F0.wireOp",EDGE,"E3.sketch_text.stroke-19"),sQuery(id+"F0.wireOp",EDGE,"E3.sketch_text.stroke-20"),sQuery(id+"F0.wireOp",EDGE,"E3.sketch_text.stroke-21"),sQuery(id+"F0.wireOp",EDGE,"E3.sketch_text.stroke-22"),sQuery(id+"F0.wireOp",EDGE,"E3.sketch_text.stroke-23"),sQuery(id+"F0.wireOp",EDGE,"E3.sketch_text.stroke-24"),sQuery(id+"F0.wireOp",EDGE,"E3.sketch_text.stroke-25"),sQuery(id+"F0.wireOp",EDGE,"E3.sketch_text.stroke-26"),sQuery(id+"F0.wireOp",EDGE,"E3.sketch_text.stroke-27"),sQuery(id+"F0.wireOp",EDGE,"E3.sketch_text.stroke-28"),sQuery(id+"F0.wireOp",EDGE,"E3.sketch_text.stroke-29"),sQuery(id+"F0.wireOp",EDGE,"E3.sketch_text.stroke-30"),sQuery(id+"F0.wireOp",EDGE,"E3.sketch_text.stroke-31"),sQuery(id+"F0.wireOp",EDGE,"E3.sketch_text.stroke-32"),sQuery(id+"F0.wireOp",EDGE,"E3.sketch_text.stroke-33"),sQuery(id+"F0.wireOp",EDGE,"E3.sketch_text.stroke-34"),sQuery(id+"F0.wireOp",EDGE,"E3.sketch_text.stroke-35"),sQuery(id+"F0.wireOp",EDGE,"E3.sketch_text.stroke-36"),sQuery(id+"F0.wireOp",EDGE,"E3.sketch_text.stroke-37"),sQuery(id+"F0.wireOp",EDGE,"E3.sketch_text.stroke-38"),sQuery(id+"F0.wireOp",EDGE,"E3.sketch_text.stroke-39"),sQuery(id+"F0.wireOp",EDGE,"E3.sketch_text.stroke-40"),sQuery(id+"F0.wireOp",EDGE,"E3.sketch_text.stroke-41"),sQuery(id+"F0.wireOp",EDGE,"E3.sketch_text.stroke-42"),sQuery(id+"F0.wireOp",EDGE,"E3.sketch_text.stroke-43"),sQuery(id+"F0.wireOp",EDGE,"E3.sketch_text.stroke-44"),sQuery(id+"F0.wireOp",EDGE,"E3.sketch_text.stroke-45"),sQuery(id+"F0.wireOp",EDGE,"E3.sketch_text.stroke-46"),sQuery(id+"F0.wireOp",EDGE,"E3.sketch_text.stroke-47"),sQuery(id+"F0.wireOp",EDGE,"E3.sketch_text.stroke-48"),sQuery(id+"F0.wireOp",EDGE,"E3.sketch_text.stroke-49"),sQuery(id+"F0.wireOp",EDGE,"E3.sketch_text.stroke-50"),sQuery(id+"F0.wireOp",EDGE,"E3.sketch_text.stroke-51"),sQuery(id+"F0.wireOp",EDGE,"E3.sketch_text.stroke-52"),sQuery(id+"F0.wireOp",EDGE,"E3.sketch_text.stroke-53"),sQuery(id+"F0.wireOp",EDGE,"E3.sketch_text.stroke-54"),sQuery(id+"F0.wireOp",EDGE,"E3.sketch_text.stroke-55"),sQuery(id+"F0.wireOp",EDGE,"E3.sketch_text.stroke-56"),sQuery(id+"F0.wireOp",EDGE,"E3.sketch_text.stroke-57"),sQuery(id+"F0.wireOp",EDGE,"E3.sketch_text.stroke-58"),sQuery(id+"F0.wireOp",EDGE,"E3.sketch_text.stroke-59"),sQuery(id+"F0.wireOp",EDGE,"E3.sketch_text.stroke-60"),sQuery(id+"F0.wireOp",EDGE,"E3.sketch_text.stroke-61"),sQuery(id+"F0.wireOp",EDGE,"E3.sketch_text.stroke-62"),sQuery(id+"F0.wireOp",EDGE,"E3.sketch_text.stroke-63"),sQuery(id+"F0.wireOp",EDGE,"E3.sketch_text.stroke-64"),sQuery(id+"F0.wireOp",EDGE,"E3.sketch_text.stroke-65"),sQuery(id+"F0.wireOp",EDGE,"E3.sketch_text.stroke-66"),sQuery(id+"F0.wireOp",EDGE,"E3.sketch_text.stroke-67"),sQuery(id+"F0.wireOp",EDGE,"E3.sketch_text.stroke-68"),sQuery(id+"F0.wireOp",EDGE,"E3.sketch_text.stroke-69"),sQuery(id+"F0.wireOp",EDGE,"E3.sketch_text.stroke-70"),sQuery(id+"F0.wireOp",EDGE,"E3.sketch_text.stroke-71"),sQuery(id+"F0.wireOp",EDGE,"E3.sketch_text.stroke-72"),sQuery(id+"F0.wireOp",EDGE,"E3.sketch_text.stroke-73"),sQuery(id+"F0.wireOp",EDGE,"E3.sketch_text.stroke-74"),sQuery(id+"F0.wireOp",EDGE,"E3.sketch_text.stroke-88"),sQuery(id+"F0.wireOp",EDGE,"E3.sketch_text.stroke-89"),sQuery(id+"F0.wireOp",EDGE,"E3.sketch_text.stroke-90"),sQuery(id+"F0.wireOp",EDGE,"E3.sketch_text.stroke-91"),sQuery(id+"F0.wireOp",EDGE,"E3.sketch_text.stroke-92"),sQuery(id+"F0.wireOp",EDGE,"E3.sketch_text.stroke-93"),sQuery(id+"F0.wireOp",EDGE,"E3.sketch_text.stroke-94"),sQuery(id+"F0.wireOp",EDGE,"E3.sketch_text.stroke-95"),sQuery(id+"F0.wireOp",EDGE,"E3.sketch_text.stroke-96"),sQuery(id+"F0.wireOp",EDGE,"E3.sketch_text.stroke-97"),sQuery(id+"F0.wireOp",EDGE,"E3.sketch_text.stroke-98"),sQuery(id+"F0.wireOp",EDGE,"E3.sketch_text.stroke-99"),sQuery(id+"F0.wireOp",EDGE,"E3.sketch_text.stroke-106"),sQuery(id+"F0.wireOp",EDGE,"E3.sketch_text.stroke-107"),sQuery(id+"F0.wireOp",EDGE,"E3.sketch_text.stroke-108"),sQuery(id+"F0.wireOp",EDGE,"E3.sketch_text.stroke-109"),sQuery(id+"F0.wireOp",EDGE,"E3.sketch_text.stroke-110"),sQuery(id+"F0.wireOp",EDGE,"E3.sketch_text.stroke-111"),sQuery(id+"F0.wireOp",EDGE,"E3.sketch_text.stroke-112"),sQuery(id+"F0.wireOp",EDGE,"E3.sketch_text.stroke-113"),sQuery(id+"F0.wireOp",EDGE,"E3.sketch_text.stroke-114"),sQuery(id+"F0.wireOp",EDGE,"E3.sketch_text.stroke-115"),sQuery(id+"F0.wireOp",EDGE,"E3.sketch_text.stroke-116"),sQuery(id+"F0.wireOp",EDGE,"E3.sketch_text.stroke-117"),sQuery(id+"F0.wireOp",EDGE,"E3.sketch_text.stroke-118"),sQuery(id+"F0.wireOp",EDGE,"E3.sketch_text.stroke-119"),sQuery(id+"F0.wireOp",EDGE,"E3.sketch_text.stroke-120"),sQuery(id+"F0.wireOp",EDGE,"E3.sketch_text.stroke-121"),sQuery(id+"F0.wireOp",EDGE,"E3.sketch_text.stroke-122"),sQuery(id+"F0.wireOp",EDGE,"E3.sketch_text.stroke-123"),sQuery(id+"F0.wireOp",EDGE,"E3.sketch_text.stroke-124"),sQuery(id+"F0.wireOp",EDGE,"E3.sketch_text.stroke-125"),sQuery(id+"F0.wireOp",EDGE,"E3.sketch_text.stroke-126"),sQuery(id+"F0.wireOp",EDGE,"E3.sketch_text.stroke-127"),sQuery(id+"F0.wireOp",EDGE,"E3.sketch_text.stroke-128"),sQuery(id+"F0.wireOp",EDGE,"E3.sketch_text.stroke-129"),sQuery(id+"F0.wireOp",EDGE,"E3.sketch_text.stroke-130"),sQuery(id+"F0.wireOp",EDGE,"E3.sketch_text.stroke-131"),sQuery(id+"F0.wireOp",EDGE,"E3.sketch_text.stroke-132"),sQuery(id+"F0.wireOp",EDGE,"E3.sketch_text.stroke-133"),sQuery(id+"F0.wireOp",EDGE,"E3.sketch_text.stroke-134"),sQuery(id+"F0.wireOp",EDGE,"E3.sketch_text.stroke-135"),sQuery(id+"F0.wireOp",EDGE,"E3.sketch_text.stroke-136"),sQuery(id+"F0.wireOp",EDGE,"E3.sketch_text.stroke-137"),sQuery(id+"F0.wireOp",EDGE,"E3.sketch_text.stroke-138"),sQuery(id+"F0.wireOp",EDGE,"E3.sketch_text.stroke-139"),sQuery(id+"F0.wireOp",EDGE,"E3.sketch_text.stroke-140"),sQuery(id+"F0.wireOp",EDGE,"E3.sketch_text.stroke-141"),sQuery(id+"F0.wireOp",EDGE,"E3.sketch_text.stroke-142"),sQuery(id+"F0.wireOp",EDGE,"E3.sketch_text.stroke-143"),sQuery(id+"F0.wireOp",EDGE,"E3.sketch_text.stroke-144"),sQuery(id+"F0.wireOp",EDGE,"E3.sketch_text.stroke-145"),sQuery(id+"F0.wireOp",EDGE,"E3.sketch_text.stroke-146"),sQuery(id+"F0.wireOp",EDGE,"E3.sketch_text.stroke-147"),sQuery(id+"F0.wireOp",EDGE,"E3.sketch_text.stroke-155"),sQuery(id+"F0.wireOp",EDGE,"E3.sketch_text.stroke-156"),sQuery(id+"F0.wireOp",EDGE,"E3.sketch_text.stroke-157"),sQuery(id+"F0.wireOp",EDGE,"E3.sketch_text.stroke-158"),sQuery(id+"F0.wireOp",EDGE,"E3.sketch_text.stroke-159"),sQuery(id+"F0.wireOp",EDGE,"E3.sketch_text.stroke-160"),sQuery(id+"F0.wireOp",EDGE,"E3.sketch_text.stroke-161"),sQuery(id+"F0.wireOp",EDGE,"E3.sketch_text.stroke-162"),sQuery(id+"F0.wireOp",EDGE,"E3.sketch_text.stroke-163"),sQuery(id+"F0.wireOp",EDGE,"E3.sketch_text.stroke-164"),sQuery(id+"F0.wireOp",EDGE,"E3.sketch_text.stroke-165"),sQuery(id+"F0.wireOp",EDGE,"E3.sketch_text.stroke-166"),sQuery(id+"F0.wireOp",EDGE,"E3.sketch_text.stroke-167"),sQuery(id+"F0.wireOp",EDGE,"E3.sketch_text.stroke-168"),sQuery(id+"F0.wireOp",EDGE,"E3.sketch_text.stroke-169"),sQuery(id+"F0.wireOp",EDGE,"E3.sketch_text.stroke-170"),sQuery(id+"F0.wireOp",EDGE,"E3.sketch_text.stroke-171"),sQuery(id+"F0.wireOp",EDGE,"E3.sketch_text.stroke-172"),sQuery(id+"F0.wireOp",EDGE,"E3.sketch_text.stroke-173"),sQuery(id+"F0.wireOp",EDGE,"E3.sketch_text.stroke-174"),sQuery(id+"F0.wireOp",EDGE,"E3.sketch_text.stroke-175"),sQuery(id+"F0.wireOp",EDGE,"E3.sketch_text.stroke-176"),sQuery(id+"F0.wireOp",EDGE,"E3.sketch_text.stroke-177"),sQuery(id+"F0.wireOp",EDGE,"E3.sketch_text.stroke-178"),sQuery(id+"F0.wireOp",EDGE,"E3.sketch_text.stroke-179"),sQuery(id+"F0.wireOp",EDGE,"E3.sketch_text.stroke-180"),sQuery(id+"F0.wireOp",EDGE,"E3.sketch_text.stroke-181"),sQuery(id+"F0.wireOp",EDGE,"E3.sketch_text.stroke-182"),sQuery(id+"F0.wireOp",EDGE,"E3.sketch_text.stroke-183"),sQuery(id+"F0.wireOp",EDGE,"E3.sketch_text.stroke-184"),sQuery(id+"F0.wireOp",EDGE,"E3.sketch_text.stroke-185"),sQuery(id+"F0.wireOp",EDGE,"E3.sketch_text.stroke-186"),sQuery(id+"F0.wireOp",EDGE,"E3.sketch_text.stroke-187"),sQuery(id+"F0.wireOp",EDGE,"E3.sketch_text.stroke-188"),sQuery(id+"F0.wireOp",EDGE,"E3.sketch_text.stroke-189"),sQuery(id+"F0.wireOp",EDGE,"E3.sketch_text.stroke-190"),sQuery(id+"F0.wireOp",EDGE,"E3.sketch_text.stroke-191"),sQuery(id+"F0.wireOp",EDGE,"E3.sketch_text.stroke-192"),sQuery(id+"F0.wireOp",EDGE,"E3.sketch_text.stroke-193"),sQuery(id+"F0.wireOp",EDGE,"E3.sketch_text.stroke-194"),sQuery(id+"F0.wireOp",EDGE,"E3.sketch_text.stroke-195"),sQuery(id+"F0.wireOp",EDGE,"E3.sketch_text.stroke-196"),sQuery(id+"F0.wireOp",EDGE,"E3.sketch_text.stroke-197"),sQuery(id+"F0.wireOp",EDGE,"E3.sketch_text.stroke-198"),sQuery(id+"F0.wireOp",EDGE,"E3.sketch_text.stroke-199"),sQuery(id+"F0.wireOp",EDGE,"E3.sketch_text.stroke-200"),sQuery(id+"F0.wireOp",EDGE,"E3.sketch_text.stroke-201"),sQuery(id+"F0.wireOp",EDGE,"E3.sketch_text.stroke-202"),sQuery(id+"F0.wireOp",EDGE,"E3.sketch_text.stroke-203"),sQuery(id+"F0.wireOp",EDGE,"E3.sketch_text.stroke-204"),sQuery(id+"F0.wireOp",EDGE,"E3.sketch_text.stroke-205"),sQuery(id+"F0.wireOp",EDGE,"E3.sketch_text.stroke-206"),sQuery(id+"F0.wireOp",EDGE,"E3.sketch_text.stroke-207"),sQuery(id+"F0.wireOp",EDGE,"E3.sketch_text.stroke-208"),sQuery(id+"F0.wireOp",EDGE,"E3.sketch_text.stroke-209"),sQuery(id+"F0.wireOp",EDGE,"E3.sketch_text.stroke-210"),sQuery(id+"F0.wireOp",EDGE,"E3.sketch_text.stroke-211"),sQuery(id+"F0.wireOp",EDGE,"E3.sketch_text.stroke-212"),sQuery(id+"F0.wireOp",EDGE,"E3.sketch_text.stroke-213"),sQuery(id+"F0.wireOp",EDGE,"E3.sketch_text.stroke-214"),sQuery(id+"F0.wireOp",EDGE,"E3.sketch_text.stroke-215"),sQuery(id+"F0.wireOp",EDGE,"E3.sketch_text.stroke-216"),sQuery(id+"F0.wireOp",EDGE,"E3.sketch_text.stroke-217"),sQuery(id+"F0.wireOp",EDGE,"E3.sketch_text.stroke-218"),sQuery(id+"F0.wireOp",EDGE,"E3.sketch_text.stroke-219"),sQuery(id+"F0.wireOp",EDGE,"E3.sketch_text.stroke-220"),sQuery(id+"F0.wireOp",EDGE,"E3.sketch_text.stroke-221"),sQuery(id+"F0.wireOp",EDGE,"E3.sketch_text.stroke-222"),sQuery(id+"F0.wireOp",EDGE,"E3.sketch_text.stroke-223"),sQuery(id+"F0.wireOp",EDGE,"E3.sketch_text.stroke-224"),sQuery(id+"F0.wireOp",EDGE,"E3.sketch_text.stroke-225"),sQuery(id+"F0.wireOp",EDGE,"E3.sketch_text.stroke-226"),sQuery(id+"F0.wireOp",EDGE,"E3.sketch_text.stroke-227"),sQuery(id+"F0.wireOp",EDGE,"E3.sketch_text.stroke-228"),sQuery(id+"F0.wireOp",EDGE,"E3.sketch_text.stroke-229"),sQuery(id+"F0.wireOp",EDGE,"E3.sketch_text.stroke-230"),sQuery(id+"F0.wireOp",EDGE,"E3.sketch_text.stroke-231"),sQuery(id+"F0.wireOp",EDGE,"E3.sketch_text.stroke-232"),sQuery(id+"F0.wireOp",EDGE,"E3.sketch_text.stroke-233"),sQuery(id+"F0.wireOp",EDGE,"E3.sketch_text.stroke-234"),sQuery(id+"F0.wireOp",EDGE,"E3.sketch_text.stroke-235"),sQuery(id+"F0.wireOp",EDGE,"E3.sketch_text.stroke-236"),sQuery(id+"F0.wireOp",EDGE,"E3.sketch_text.stroke-237"),sQuery(id+"F0.wireOp",EDGE,"E3.sketch_text.stroke-238"),sQuery(id+"F0.wireOp",EDGE,"E3.sketch_text.stroke-244"),sQuery(id+"F0.wireOp",EDGE,"E3.sketch_text.stroke-245"),sQuery(id+"F0.wireOp",EDGE,"E3.sketch_text.stroke-246"),sQuery(id+"F0.wireOp",EDGE,"E3.sketch_text.stroke-247"),sQuery(id+"F0.wireOp",EDGE,"E3.sketch_text.stroke-248"),sQuery(id+"F0.wireOp",EDGE,"E3.sketch_text.stroke-249"),sQuery(id+"F0.wireOp",EDGE,"E3.sketch_text.stroke-250"),sQuery(id+"F0.wireOp",EDGE,"E3.sketch_text.stroke-251"),sQuery(id+"F0.wireOp",EDGE,"E3.sketch_text.stroke-252"),sQuery(id+"F0.wireOp",EDGE,"E3.sketch_text.stroke-253"),sQuery(id+"F0.wireOp",EDGE,"E3.sketch_text.stroke-254"),sQuery(id+"F0.wireOp",EDGE,"E3.sketch_text.stroke-255"),sQuery(id+"F0.wireOp",EDGE,"E3.sketch_text.stroke-256"),sQuery(id+"F0.wireOp",EDGE,"E3.sketch_text.stroke-257"),sQuery(id+"F0.wireOp",EDGE,"E3.sketch_text.stroke-258"),sQuery(id+"F0.wireOp",EDGE,"E3.sketch_text.stroke-259"),sQuery(id+"F0.wireOp",EDGE,"E3.sketch_text.stroke-260"),sQuery(id+"F0.wireOp",EDGE,"E4.sketch_text.stroke-0"),sQuery(id+"F0.wireOp",EDGE,"E4.sketch_text.stroke-1"),sQuery(id+"F0.wireOp",EDGE,"E4.sketch_text.stroke-2"),sQuery(id+"F0.wireOp",EDGE,"E4.sketch_text.stroke-3"),sQuery(id+"F0.wireOp",EDGE,"E4.sketch_text.stroke-4"),sQuery(id+"F0.wireOp",EDGE,"E4.sketch_text.stroke-5"),sQuery(id+"F0.wireOp",EDGE,"E4.sketch_text.stroke-6"),sQuery(id+"F0.wireOp",EDGE,"E4.sketch_text.stroke-7"),sQuery(id+"F0.wireOp",EDGE,"E4.sketch_text.stroke-8"),sQuery(id+"F0.wireOp",EDGE,"E4.sketch_text.stroke-9"),sQuery(id+"F0.wireOp",EDGE,"E4.sketch_text.stroke-10"),sQuery(id+"F0.wireOp",EDGE,"E4.sketch_text.stroke-11"),sQuery(id+"F0.wireOp",EDGE,"E4.sketch_text.stroke-12"),sQuery(id+"F0.wireOp",EDGE,"E4.sketch_text.stroke-13"),sQuery(id+"F0.wireOp",EDGE,"E4.sketch_text.stroke-14"),sQuery(id+"F0.wireOp",EDGE,"E4.sketch_text.stroke-15"),sQuery(id+"F0.wireOp",EDGE,"E4.sketch_text.stroke-16"),sQuery(id+"F0.wireOp",EDGE,"E4.sketch_text.stroke-17"),sQuery(id+"F0.wireOp",EDGE,"E4.sketch_text.stroke-18"),sQuery(id+"F0.wireOp",EDGE,"E4.sketch_text.stroke-19"),sQuery(id+"F0.wireOp",EDGE,"E4.sketch_text.stroke-20"),sQuery(id+"F0.wireOp",EDGE,"E4.sketch_text.stroke-21"),sQuery(id+"F0.wireOp",EDGE,"E4.sketch_text.stroke-28"),sQuery(id+"F0.wireOp",EDGE,"E4.sketch_text.stroke-29"),sQuery(id+"F0.wireOp",EDGE,"E4.sketch_text.stroke-30"),sQuery(id+"F0.wireOp",EDGE,"E4.sketch_text.stroke-31"),sQuery(id+"F0.wireOp",EDGE,"E4.sketch_text.stroke-32"),sQuery(id+"F0.wireOp",EDGE,"E4.sketch_text.stroke-33"),sQuery(id+"F0.wireOp",EDGE,"E4.sketch_text.stroke-34"),sQuery(id+"F0.wireOp",EDGE,"E4.sketch_text.stroke-35"),sQuery(id+"F0.wireOp",EDGE,"E4.sketch_text.stroke-36"),sQuery(id+"F0.wireOp",EDGE,"E4.sketch_text.stroke-37"),sQuery(id+"F0.wireOp",EDGE,"E4.sketch_text.stroke-38"),sQuery(id+"F0.wireOp",EDGE,"E4.sketch_text.stroke-39"),sQuery(id+"F0.wireOp",EDGE,"E4.sketch_text.stroke-40"),sQuery(id+"F0.wireOp",EDGE,"E4.sketch_text.stroke-41"),sQuery(id+"F0.wireOp",EDGE,"E4.sketch_text.stroke-42"),sQuery(id+"F0.wireOp",EDGE,"E4.sketch_text.stroke-43"),sQuery(id+"F0.wireOp",EDGE,"E4.sketch_text.stroke-44"),sQuery(id+"F0.wireOp",EDGE,"E4.sketch_text.stroke-45"),sQuery(id+"F0.wireOp",EDGE,"E4.sketch_text.stroke-46"),sQuery(id+"F0.wireOp",EDGE,"E4.sketch_text.stroke-47"),sQuery(id+"F0.wireOp",EDGE,"E4.sketch_text.stroke-48"),sQuery(id+"F0.wireOp",EDGE,"E4.sketch_text.stroke-49"),sQuery(id+"F0.wireOp",EDGE,"E4.sketch_text.stroke-50"),sQuery(id+"F0.wireOp",EDGE,"E4.sketch_text.stroke-51"),sQuery(id+"F0.wireOp",EDGE,"E4.sketch_text.stroke-52"),sQuery(id+"F0.wireOp",EDGE,"E4.sketch_text.stroke-53"),sQuery(id+"F0.wireOp",EDGE,"E4.sketch_text.stroke-54"),sQuery(id+"F0.wireOp",EDGE,"E4.sketch_text.stroke-55"),sQuery(id+"F0.wireOp",EDGE,"E4.sketch_text.stroke-56"),sQuery(id+"F0.wireOp",EDGE,"E4.sketch_text.stroke-57"),sQuery(id+"F0.wireOp",EDGE,"E4.sketch_text.stroke-58"),sQuery(id+"F0.wireOp",EDGE,"E4.sketch_text.stroke-59"),sQuery(id+"F0.wireOp",EDGE,"E4.sketch_text.stroke-60"),sQuery(id+"F0.wireOp",EDGE,"E4.sketch_text.stroke-61"),sQuery(id+"F0.wireOp",EDGE,"E4.sketch_text.stroke-62"),sQuery(id+"F0.wireOp",EDGE,"E4.sketch_text.stroke-63"),sQuery(id+"F0.wireOp",EDGE,"E4.sketch_text.stroke-64"),sQuery(id+"F0.wireOp",EDGE,"E4.sketch_text.stroke-65"),sQuery(id+"F0.wireOp",EDGE,"E4.sketch_text.stroke-66"),sQuery(id+"F0.wireOp",EDGE,"E4.sketch_text.stroke-67"),sQuery(id+"F0.wireOp",EDGE,"E4.sketch_text.stroke-68"),sQuery(id+"F0.wireOp",EDGE,"E4.sketch_text.stroke-69"),sQuery(id+"F0.wireOp",EDGE,"E4.sketch_text.stroke-70"),sQuery(id+"F0.wireOp",EDGE,"E4.sketch_text.stroke-71"),sQuery(id+"F0.wireOp",EDGE,"E4.sketch_text.stroke-72"),sQuery(id+"F0.wireOp",EDGE,"E4.sketch_text.stroke-73"),sQuery(id+"F0.wireOp",EDGE,"E4.sketch_text.stroke-74"),sQuery(id+"F0.wireOp",EDGE,"E4.sketch_text.stroke-85"),sQuery(id+"F0.wireOp",EDGE,"E4.sketch_text.stroke-86"),sQuery(id+"F0.wireOp",EDGE,"E4.sketch_text.stroke-87"),sQuery(id+"F0.wireOp",EDGE,"E4.sketch_text.stroke-88"),sQuery(id+"F0.wireOp",EDGE,"E4.sketch_text.stroke-89"),sQuery(id+"F0.wireOp",EDGE,"E4.sketch_text.stroke-90"),sQuery(id+"F0.wireOp",EDGE,"E4.sketch_text.stroke-91"),sQuery(id+"F0.wireOp",EDGE,"E4.sketch_text.stroke-92"),sQuery(id+"F0.wireOp",EDGE,"E4.sketch_text.stroke-93"),sQuery(id+"F0.wireOp",EDGE,"E4.sketch_text.stroke-94"),sQuery(id+"F0.wireOp",EDGE,"E4.sketch_text.stroke-95"),sQuery(id+"F0.wireOp",EDGE,"E4.sketch_text.stroke-96"),sQuery(id+"F0.wireOp",EDGE,"E4.sketch_text.stroke-97"),sQuery(id+"F0.wireOp",EDGE,"E4.sketch_text.stroke-98"),sQuery(id+"F0.wireOp",EDGE,"E4.sketch_text.stroke-99"),sQuery(id+"F0.wireOp",EDGE,"E4.sketch_text.stroke-100"),sQuery(id+"F0.wireOp",EDGE,"E4.sketch_text.stroke-101"),sQuery(id+"F0.wireOp",EDGE,"E4.sketch_text.stroke-102"),sQuery(id+"F0.wireOp",EDGE,"E4.sketch_text.stroke-103"),sQuery(id+"F0.wireOp",EDGE,"E4.sketch_text.stroke-104"),sQuery(id+"F0.wireOp",EDGE,"E4.sketch_text.stroke-105"),sQuery(id+"F0.wireOp",EDGE,"E4.sketch_text.stroke-106"),sQuery(id+"F0.wireOp",EDGE,"E4.sketch_text.stroke-107"),sQuery(id+"F0.wireOp",EDGE,"E4.sketch_text.stroke-108"),sQuery(id+"F0.wireOp",EDGE,"E4.sketch_text.stroke-109"),sQuery(id+"F0.wireOp",EDGE,"E4.sketch_text.stroke-110"),sQuery(id+"F0.wireOp",EDGE,"E4.sketch_text.stroke-111"),sQuery(id+"F0.wireOp",EDGE,"E4.sketch_text.stroke-112"),sQuery(id+"F0.wireOp",EDGE,"E4.sketch_text.stroke-113"),sQuery(id+"F0.wireOp",EDGE,"E4.sketch_text.stroke-114"),sQuery(id+"F0.wireOp",EDGE,"E4.sketch_text.stroke-115"),sQuery(id+"F0.wireOp",EDGE,"E4.sketch_text.stroke-116"),sQuery(id+"F0.wireOp",EDGE,"E4.sketch_text.stroke-117"),sQuery(id+"F0.wireOp",EDGE,"E4.sketch_text.stroke-118"),sQuery(id+"F0.wireOp",EDGE,"E4.sketch_text.stroke-119"),sQuery(id+"F0.wireOp",EDGE,"E4.sketch_text.stroke-120"),sQuery(id+"F0.wireOp",EDGE,"E4.sketch_text.stroke-121"),sQuery(id+"F0.wireOp",EDGE,"E4.sketch_text.stroke-122"),sQuery(id+"F0.wireOp",EDGE,"E4.sketch_text.stroke-123"),sQuery(id+"F0.wireOp",EDGE,"E4.sketch_text.stroke-124"),sQuery(id+"F0.wireOp",EDGE,"E4.sketch_text.stroke-138"),sQuery(id+"F0.wireOp",EDGE,"E4.sketch_text.stroke-139"),sQuery(id+"F0.wireOp",EDGE,"E4.sketch_text.stroke-140"),sQuery(id+"F0.wireOp",EDGE,"E4.sketch_text.stroke-141"),sQuery(id+"F0.wireOp",EDGE,"E4.sketch_text.stroke-142"),sQuery(id+"F0.wireOp",EDGE,"E4.sketch_text.stroke-143"),sQuery(id+"F0.wireOp",EDGE,"E4.sketch_text.stroke-144"),sQuery(id+"F0.wireOp",EDGE,"E4.sketch_text.stroke-145"),sQuery(id+"F0.wireOp",EDGE,"E4.sketch_text.stroke-146"),sQuery(id+"F0.wireOp",EDGE,"E4.sketch_text.stroke-147"),sQuery(id+"F0.wireOp",EDGE,"E4.sketch_text.stroke-148"),sQuery(id+"F0.wireOp",EDGE,"E4.sketch_text.stroke-149"),sQuery(id+"F0.wireOp",EDGE,"E4.sketch_text.stroke-156"),sQuery(id+"F0.wireOp",EDGE,"E4.sketch_text.stroke-157"),sQuery(id+"F0.wireOp",EDGE,"E4.sketch_text.stroke-158"),sQuery(id+"F0.wireOp",EDGE,"E4.sketch_text.stroke-159"),sQuery(id+"F0.wireOp",EDGE,"E4.sketch_text.stroke-160"),sQuery(id+"F0.wireOp",EDGE,"E4.sketch_text.stroke-161"),sQuery(id+"F0.wireOp",EDGE,"E4.sketch_text.stroke-162"),sQuery(id+"F0.wireOp",EDGE,"E4.sketch_text.stroke-163"),sQuery(id+"F0.wireOp",EDGE,"E4.sketch_text.stroke-164"),sQuery(id+"F0.wireOp",EDGE,"E4.sketch_text.stroke-165"),sQuery(id+"F0.wireOp",EDGE,"E4.sketch_text.stroke-166"),sQuery(id+"F0.wireOp",EDGE,"E4.sketch_text.stroke-167"),sQuery(id+"F0.wireOp",EDGE,"E4.sketch_text.stroke-168"),sQuery(id+"F0.wireOp",EDGE,"E4.sketch_text.stroke-169"),sQuery(id+"F0.wireOp",EDGE,"E4.sketch_text.stroke-170"),sQuery(id+"F0.wireOp",EDGE,"E4.sketch_text.stroke-171"),sQuery(id+"F0.wireOp",EDGE,"E4.sketch_text.stroke-172"),sQuery(id+"F0.wireOp",EDGE,"E4.sketch_text.stroke-173"),sQuery(id+"F0.wireOp",EDGE,"E4.sketch_text.stroke-174"),sQuery(id+"F0.wireOp",EDGE,"E4.sketch_text.stroke-175"),sQuery(id+"F0.wireOp",EDGE,"E4.sketch_text.stroke-176"),sQuery(id+"F0.wireOp",EDGE,"E4.sketch_text.stroke-177"),sQuery(id+"F0.wireOp",EDGE,"E4.sketch_text.stroke-178"),sQuery(id+"F0.wireOp",EDGE,"E4.sketch_text.stroke-179"),sQuery(id+"F0.wireOp",EDGE,"E4.sketch_text.stroke-180"),sQuery(id+"F0.wireOp",EDGE,"E4.sketch_text.stroke-181"),sQuery(id+"F0.wireOp",EDGE,"E4.sketch_text.stroke-182"),sQuery(id+"F0.wireOp",EDGE,"E4.sketch_text.stroke-183"),sQuery(id+"F0.wireOp",EDGE,"E4.sketch_text.stroke-184"),sQuery(id+"F0.wireOp",EDGE,"E4.sketch_text.stroke-185"),sQuery(id+"F0.wireOp",EDGE,"E4.sketch_text.stroke-186"),sQuery(id+"F0.wireOp",EDGE,"E4.sketch_text.stroke-187"),sQuery(id+"F0.wireOp",EDGE,"E4.sketch_text.stroke-188"),sQuery(id+"F0.wireOp",EDGE,"E4.sketch_text.stroke-189"),sQuery(id+"F0.wireOp",EDGE,"E4.sketch_text.stroke-190"),sQuery(id+"F0.wireOp",EDGE,"E4.sketch_text.stroke-191"),sQuery(id+"F0.wireOp",EDGE,"E4.sketch_text.stroke-192"),sQuery(id+"F0.wireOp",EDGE,"E4.sketch_text.stroke-193"),sQuery(id+"F0.wireOp",EDGE,"E4.sketch_text.stroke-194"),sQuery(id+"F0.wireOp",EDGE,"E4.sketch_text.stroke-195"),sQuery(id+"F0.wireOp",EDGE,"E4.sketch_text.stroke-196"),sQuery(id+"F0.wireOp",EDGE,"E4.sketch_text.stroke-197"),sQuery(id+"F0.wireOp",EDGE,"E4.sketch_text.stroke-198"),sQuery(id+"F0.wireOp",EDGE,"E4.sketch_text.stroke-199"),sQuery(id+"F0.wireOp",EDGE,"E4.sketch_text.stroke-200"),sQuery(id+"F0.wireOp",EDGE,"E4.sketch_text.stroke-201"),sQuery(id+"F0.wireOp",EDGE,"E4.sketch_text.stroke-208"),sQuery(id+"F0.wireOp",EDGE,"E4.sketch_text.stroke-209"),sQuery(id+"F0.wireOp",EDGE,"E4.sketch_text.stroke-210"),sQuery(id+"F0.wireOp",EDGE,"E4.sketch_text.stroke-211"),sQuery(id+"F0.wireOp",EDGE,"E4.sketch_text.stroke-212"),sQuery(id+"F0.wireOp",EDGE,"E4.sketch_text.stroke-213"),sQuery(id+"F0.wireOp",EDGE,"E4.sketch_text.stroke-214"),sQuery(id+"F0.wireOp",EDGE,"E4.sketch_text.stroke-215"),sQuery(id+"F0.wireOp",EDGE,"E4.sketch_text.stroke-216"),sQuery(id+"F0.wireOp",EDGE,"E4.sketch_text.stroke-217"),sQuery(id+"F0.wireOp",EDGE,"E4.sketch_text.stroke-218"),sQuery(id+"F0.wireOp",EDGE,"E4.sketch_text.stroke-219"),sQuery(id+"F0.wireOp",EDGE,"E4.sketch_text.stroke-220"),sQuery(id+"F0.wireOp",EDGE,"E4.sketch_text.stroke-221"),sQuery(id+"F0.wireOp",EDGE,"E4.sketch_text.stroke-222"),sQuery(id+"F0.wireOp",EDGE,"E4.sketch_text.stroke-223"),sQuery(id+"F0.wireOp",EDGE,"E4.sketch_text.stroke-224"),sQuery(id+"F0.wireOp",EDGE,"E4.sketch_text.stroke-225"),sQuery(id+"F0.wireOp",EDGE,"E4.sketch_text.stroke-226"),sQuery(id+"F0.wireOp",EDGE,"E4.sketch_text.stroke-227"),sQuery(id+"F0.wireOp",EDGE,"E4.sketch_text.stroke-228"),sQuery(id+"F0.wireOp",EDGE,"E4.sketch_text.stroke-229"),sQuery(id+"F0.wireOp",EDGE,"E4.sketch_text.stroke-230"),sQuery(id+"F0.wireOp",EDGE,"E4.sketch_text.stroke-231"),sQuery(id+"F0.wireOp",EDGE,"E4.sketch_text.stroke-232"),sQuery(id+"F0.wireOp",EDGE,"E4.sketch_text.stroke-233"),sQuery(id+"F0.wireOp",EDGE,"E4.sketch_text.stroke-234"),sQuery(id+"F0.wireOp",EDGE,"E4.sketch_text.stroke-235"),sQuery(id+"F0.wireOp",EDGE,"E4.sketch_text.stroke-236"),sQuery(id+"F0.wireOp",EDGE,"E4.sketch_text.stroke-237"),sQuery(id+"F0.wireOp",EDGE,"E4.sketch_text.stroke-238"),sQuery(id+"F0.wireOp",EDGE,"E4.sketch_text.stroke-239"),sQuery(id+"F0.wireOp",EDGE,"E4.sketch_text.stroke-240"),sQuery(id+"F0.wireOp",EDGE,"E4.sketch_text.stroke-241"),sQuery(id+"F0.wireOp",EDGE,"E4.sketch_text.stroke-242"),sQuery(id+"F0.wireOp",EDGE,"E4.sketch_text.stroke-243"),sQuery(id+"F0.wireOp",EDGE,"E4.sketch_text.stroke-244"),sQuery(id+"F0.wireOp",EDGE,"E4.sketch_text.stroke-245"),sQuery(id+"F0.wireOp",EDGE,"E4.sketch_text.stroke-246"),sQuery(id+"F0.wireOp",EDGE,"E4.sketch_text.stroke-247"),sQuery(id+"F0.wireOp",EDGE,"E4.sketch_text.stroke-248"),sQuery(id+"F0.wireOp",EDGE,"E4.sketch_text.stroke-249"),sQuery(id+"F0.wireOp",EDGE,"E4.sketch_text.stroke-250"),sQuery(id+"F0.wireOp",EDGE,"E4.sketch_text.stroke-251"),sQuery(id+"F0.wireOp",EDGE,"E4.sketch_text.stroke-252"),sQuery(id+"F0.wireOp",EDGE,"E4.sketch_text.stroke-253"),sQuery(id+"F0.wireOp",EDGE,"E4.sketch_text.stroke-254"),sQuery(id+"F0.wireOp",EDGE,"E4.sketch_text.stroke-255"),sQuery(id+"F0.wireOp",EDGE,"E4.sketch_text.stroke-256"),sQuery(id+"F0.wireOp",EDGE,"E4.sketch_text.stroke-257"),sQuery(id+"F0.wireOp",EDGE,"E4.sketch_text.stroke-258"),sQuery(id+"F0.wireOp",EDGE,"E4.sketch_text.stroke-259"),sQuery(id+"F0.wireOp",EDGE,"E4.sketch_text.stroke-260"),sQuery(id+"F0.wireOp",EDGE,"E4.sketch_text.stroke-261"),sQuery(id+"F0.wireOp",EDGE,"E4.sketch_text.stroke-262"),sQuery(id+"F0.wireOp",EDGE,"E4.sketch_text.stroke-263"),sQuery(id+"F0.wireOp",EDGE,"E4.sketch_text.stroke-264"),sQuery(id+"F0.wireOp",EDGE,"E4.sketch_text.stroke-265"),sQuery(id+"F0.wireOp",EDGE,"E4.sketch_text.stroke-266"),sQuery(id+"F0.wireOp",EDGE,"E4.sketch_text.stroke-267"),sQuery(id+"F0.wireOp",EDGE,"E4.sketch_text.stroke-268"),sQuery(id+"F0.wireOp",EDGE,"E4.sketch_text.stroke-269"),sQuery(id+"F0.wireOp",EDGE,"E4.sketch_text.stroke-270"),sQuery(id+"F0.wireOp",EDGE,"E4.sketch_text.stroke-271"),sQuery(id+"F0.wireOp",EDGE,"E4.sketch_text.stroke-272"),sQuery(id+"F0.wireOp",EDGE,"E4.sketch_text.stroke-273"),sQuery(id+"F0.wireOp",EDGE,"E4.sketch_text.stroke-274"),sQuery(id+"F0.wireOp",EDGE,"E4.sketch_text.stroke-275"),sQuery(id+"F0.wireOp",EDGE,"E4.sketch_text.stroke-276"),sQuery(id+"F0.wireOp",EDGE,"E4.sketch_text.stroke-283"),sQuery(id+"F0.wireOp",EDGE,"E4.sketch_text.stroke-284"),sQuery(id+"F0.wireOp",EDGE,"E4.sketch_text.stroke-285"),sQuery(id+"F0.wireOp",EDGE,"E4.sketch_text.stroke-286"),sQuery(id+"F0.wireOp",EDGE,"E4.sketch_text.stroke-287"),sQuery(id+"F0.wireOp",EDGE,"E4.sketch_text.stroke-288"),sQuery(id+"F0.wireOp",EDGE,"E4.sketch_text.stroke-289"),sQuery(id+"F0.wireOp",EDGE,"E4.sketch_text.stroke-290"),sQuery(id+"F0.wireOp",EDGE,"E4.sketch_text.stroke-291"),sQuery(id+"F0.wireOp",EDGE,"E4.sketch_text.stroke-292"),sQuery(id+"F0.wireOp",EDGE,"E4.sketch_text.stroke-293"),sQuery(id+"F0.wireOp",EDGE,"E4.sketch_text.stroke-294"),sQuery(id+"F0.wireOp",EDGE,"E4.sketch_text.stroke-295"),sQuery(id+"F0.wireOp",EDGE,"E4.sketch_text.stroke-296"),sQuery(id+"F0.wireOp",EDGE,"E4.sketch_text.stroke-297"),sQuery(id+"F0.wireOp",EDGE,"E4.sketch_text.stroke-298"),sQuery(id+"F0.wireOp",EDGE,"E4.sketch_text.stroke-299"),sQuery(id+"F0.wireOp",EDGE,"E4.sketch_text.stroke-300"),sQuery(id+"F0.wireOp",EDGE,"E4.sketch_text.stroke-301"),sQuery(id+"F0.wireOp",EDGE,"E4.sketch_text.stroke-302"),sQuery(id+"F0.wireOp",EDGE,"E4.sketch_text.stroke-303"),sQuery(id+"F0.wireOp",EDGE,"E4.sketch_text.stroke-304"),sQuery(id+"F0.wireOp",EDGE,"E4.sketch_text.stroke-305"),sQuery(id+"F0.wireOp",EDGE,"E4.sketch_text.stroke-306"),sQuery(id+"F0.wireOp",EDGE,"E4.sketch_text.stroke-307"),sQuery(id+"F0.wireOp",EDGE,"E4.sketch_text.stroke-308"),sQuery(id+"F0.wireOp",EDGE,"E4.sketch_text.stroke-309"),sQuery(id+"F0.wireOp",EDGE,"E4.sketch_text.stroke-310"),sQuery(id+"F0.wireOp",EDGE,"E4.sketch_text.stroke-321"),sQuery(id+"F0.wireOp",EDGE,"E4.sketch_text.stroke-322"),sQuery(id+"F0.wireOp",EDGE,"E4.sketch_text.stroke-323"),sQuery(id+"F0.wireOp",EDGE,"E4.sketch_text.stroke-324"),sQuery(id+"F0.wireOp",EDGE,"E4.sketch_text.stroke-325"),sQuery(id+"F0.wireOp",EDGE,"E4.sketch_text.stroke-326"),sQuery(id+"F0.wireOp",EDGE,"E4.sketch_text.stroke-327"),sQuery(id+"F0.wireOp",EDGE,"E4.sketch_text.stroke-328"),sQuery(id+"F0.wireOp",EDGE,"E4.sketch_text.stroke-329"),sQuery(id+"F0.wireOp",EDGE,"E4.sketch_text.stroke-330"),sQuery(id+"F0.wireOp",EDGE,"E4.sketch_text.stroke-331"),sQuery(id+"F0.wireOp",EDGE,"E4.sketch_text.stroke-332"),sQuery(id+"F0.wireOp",EDGE,"E4.sketch_text.stroke-333"),sQuery(id+"F0.wireOp",EDGE,"E4.sketch_text.stroke-334"),sQuery(id+"F0.wireOp",EDGE,"E4.sketch_text.stroke-335"),sQuery(id+"F0.wireOp",EDGE,"E4.sketch_text.stroke-336"),sQuery(id+"F0.wireOp",EDGE,"E4.sketch_text.stroke-337"),sQuery(id+"F0.wireOp",EDGE,"E4.sketch_text.stroke-338"),sQuery(id+"F0.wireOp",EDGE,"E4.sketch_text.stroke-339"),sQuery(id+"F0.wireOp",EDGE,"E4.sketch_text.stroke-340"),sQuery(id+"F0.wireOp",EDGE,"E4.sketch_text.stroke-341"),sQuery(id+"F0.wireOp",EDGE,"E4.sketch_text.stroke-342"),sQuery(id+"F0.wireOp",EDGE,"E4.sketch_text.stroke-343"),sQuery(id+"F0.wireOp",EDGE,"E4.sketch_text.stroke-344"),sQuery(id+"F0.wireOp",EDGE,"E4.sketch_text.stroke-345"),sQuery(id+"F0.wireOp",EDGE,"E4.sketch_text.stroke-346"),sQuery(id+"F0.wireOp",EDGE,"E4.sketch_text.stroke-347"),sQuery(id+"F0.wireOp",EDGE,"E4.sketch_text.stroke-348"),sQuery(id+"F0.wireOp",EDGE,"E4.sketch_text.stroke-359"),sQuery(id+"F0.wireOp",EDGE,"E4.sketch_text.stroke-360"),sQuery(id+"F0.wireOp",EDGE,"E4.sketch_text.stroke-361"),sQuery(id+"F0.wireOp",EDGE,"E4.sketch_text.stroke-362"),sQuery(id+"F0.wireOp",EDGE,"E4.sketch_text.stroke-363"),sQuery(id+"F0.wireOp",EDGE,"E4.sketch_text.stroke-364"),sQuery(id+"F0.wireOp",EDGE,"E4.sketch_text.stroke-365"),sQuery(id+"F0.wireOp",EDGE,"E4.sketch_text.stroke-366"),sQuery(id+"F0.wireOp",EDGE,"E4.sketch_text.stroke-367"),sQuery(id+"F0.wireOp",EDGE,"E4.sketch_text.stroke-368"),sQuery(id+"F0.wireOp",EDGE,"E4.sketch_text.stroke-369"),sQuery(id+"F0.wireOp",EDGE,"E4.sketch_text.stroke-370"),sQuery(id+"F0.wireOp",EDGE,"E4.sketch_text.stroke-371"),sQuery(id+"F0.wireOp",EDGE,"E4.sketch_text.stroke-372"),sQuery(id+"F0.wireOp",EDGE,"E4.sketch_text.stroke-373"),sQuery(id+"F0.wireOp",EDGE,"E4.sketch_text.stroke-374"),sQuery(id+"F0.wireOp",EDGE,"E4.sketch_text.stroke-375"),sQuery(id+"F0.wireOp",EDGE,"E4.sketch_text.stroke-376"),sQuery(id+"F0.wireOp",EDGE,"E4.sketch_text.stroke-377"),sQuery(id+"F0.wireOp",EDGE,"E4.sketch_text.stroke-378"),sQuery(id+"F0.wireOp",EDGE,"E4.sketch_text.stroke-379"),sQuery(id+"F0.wireOp",EDGE,"E4.sketch_text.stroke-380"),sQuery(id+"F0.wireOp",EDGE,"E4.sketch_text.stroke-381"),sQuery(id+"F0.wireOp",EDGE,"E4.sketch_text.stroke-382"),sQuery(id+"F0.wireOp",EDGE,"E4.sketch_text.stroke-383"),sQuery(id+"F0.wireOp",EDGE,"E4.sketch_text.stroke-384"),sQuery(id+"F0.wireOp",EDGE,"E4.sketch_text.stroke-385"),sQuery(id+"F0.wireOp",EDGE,"E4.sketch_text.stroke-386"),sQuery(id+"F0.wireOp",EDGE,"E4.sketch_text.stroke-387"),sQuery(id+"F0.wireOp",EDGE,"E4.sketch_text.stroke-388"),sQuery(id+"F0.wireOp",EDGE,"E4.sketch_text.stroke-389"),sQuery(id+"F0.wireOp",EDGE,"E4.sketch_text.stroke-390"),sQuery(id+"F0.wireOp",EDGE,"E4.sketch_text.stroke-391"),sQuery(id+"F0.wireOp",EDGE,"E4.sketch_text.stroke-392")])],"isStart":true})],"blendedInto":[makeQuery(id+"F6.opExtrude","CAP_FACE",FACE,{"disambiguationData":[OSD([sQuery(id+"F0.wireOp",EDGE,"E0.bottom"),subQ1,sQuery(id+"F0.wireOp",EDGE,"E0.left"),subQ0,sQuery(id+"F0.wireOp",EDGE,"E3.sketch_text.stroke-0"),sQuery(id+"F0.wireOp",EDGE,"E3.sketch_text.stroke-1"),sQuery(id+"F0.wireOp",EDGE,"E3.sketch_text.stroke-2"),sQuery(id+"F0.wireOp",EDGE,"E3.sketch_text.stroke-3"),sQuery(id+"F0.wireOp",EDGE,"E3.sketch_text.stroke-4"),sQuery(id+"F0.wireOp",EDGE,"E3.sketch_text.stroke-5"),sQuery(id+"F0.wireOp",EDGE,"E3.sketch_text.stroke-6"),sQuery(id+"F0.wireOp",EDGE,"E3.sketch_text.stroke-7"),sQuery(id+"F0.wireOp",EDGE,"E3.sketch_text.stroke-8"),sQuery(id+"F0.wireOp",EDGE,"E3.sketch_text.stroke-9"),sQuery(id+"F0.wireOp",EDGE,"E3.sketch_text.stroke-10"),sQuery(id+"F0.wireOp",EDGE,"E3.sketch_text.stroke-11"),sQuery(id+"F0.wireOp",EDGE,"E3.sketch_text.stroke-12"),sQuery(id+"F0.wireOp",EDGE,"E3.sketch_text.stroke-13"),sQuery(id+"F0.wireOp",EDGE,"E3.sketch_text.stroke-14"),sQuery(id+"F0.wireOp",EDGE,"E3.sketch_text.stroke-15"),sQuery(id+"F0.wireOp",EDGE,"E3.sketch_text.stroke-16"),sQuery(id+"F0.wireOp",EDGE,"E3.sketch_text.stroke-17"),sQuery(id+"F0.wireOp",EDGE,"E3.sketch_text.stroke-18"),sQuery(id+"F0.wireOp",EDGE,"E3.sketch_text.stroke-19"),sQuery(id+"F0.wireOp",EDGE,"E3.sketch_text.stroke-20"),sQuery(id+"F0.wireOp",EDGE,"E3.sketch_text.stroke-21"),sQuery(id+"F0.wireOp",EDGE,"E3.sketch_text.stroke-22"),sQuery(id+"F0.wireOp",EDGE,"E3.sketch_text.stroke-23"),sQuery(id+"F0.wireOp",EDGE,"E3.sketch_text.stroke-24"),sQuery(id+"F0.wireOp",EDGE,"E3.sketch_text.stroke-25"),sQuery(id+"F0.wireOp",EDGE,"E3.sketch_text.stroke-26"),sQuery(id+"F0.wireOp",EDGE,"E3.sketch_text.stroke-27"),sQuery(id+"F0.wireOp",EDGE,"E3.sketch_text.stroke-28"),sQuery(id+"F0.wireOp",EDGE,"E3.sketch_text.stroke-29"),sQuery(id+"F0.wireOp",EDGE,"E3.sketch_text.stroke-30"),sQuery(id+"F0.wireOp",EDGE,"E3.sketch_text.stroke-31"),sQuery(id+"F0.wireOp",EDGE,"E3.sketch_text.stroke-32"),sQuery(id+"F0.wireOp",EDGE,"E3.sketch_text.stroke-33"),sQuery(id+"F0.wireOp",EDGE,"E3.sketch_text.stroke-34"),sQuery(id+"F0.wireOp",EDGE,"E3.sketch_text.stroke-35"),sQuery(id+"F0.wireOp",EDGE,"E3.sketch_text.stroke-36"),sQuery(id+"F0.wireOp",EDGE,"E3.sketch_text.stroke-37"),sQuery(id+"F0.wireOp",EDGE,"E3.sketch_text.stroke-38"),sQuery(id+"F0.wireOp",EDGE,"E3.sketch_text.stroke-39"),sQuery(id+"F0.wireOp",EDGE,"E3.sketch_text.stroke-40"),sQuery(id+"F0.wireOp",EDGE,"E3.sketch_text.stroke-41"),sQuery(id+"F0.wireOp",EDGE,"E3.sketch_text.stroke-42"),sQuery(id+"F0.wireOp",EDGE,"E3.sketch_text.stroke-43"),sQuery(id+"F0.wireOp",EDGE,"E3.sketch_text.stroke-44"),sQuery(id+"F0.wireOp",EDGE,"E3.sketch_text.stroke-45"),sQuery(id+"F0.wireOp",EDGE,"E3.sketch_text.stroke-46"),sQuery(id+"F0.wireOp",EDGE,"E3.sketch_text.stroke-47"),sQuery(id+"F0.wireOp",EDGE,"E3.sketch_text.stroke-48"),sQuery(id+"F0.wireOp",EDGE,"E3.sketch_text.stroke-49"),sQuery(id+"F0.wireOp",EDGE,"E3.sketch_text.stroke-50"),sQuery(id+"F0.wireOp",EDGE,"E3.sketch_text.stroke-51"),sQuery(id+"F0.wireOp",EDGE,"E3.sketch_text.stroke-52"),sQuery(id+"F0.wireOp",EDGE,"E3.sketch_text.stroke-53"),sQuery(id+"F0.wireOp",EDGE,"E3.sketch_text.stroke-54"),sQuery(id+"F0.wireOp",EDGE,"E3.sketch_text.stroke-55"),sQuery(id+"F0.wireOp",EDGE,"E3.sketch_text.stroke-56"),sQuery(id+"F0.wireOp",EDGE,"E3.sketch_text.stroke-57"),sQuery(id+"F0.wireOp",EDGE,"E3.sketch_text.stroke-58"),sQuery(id+"F0.wireOp",EDGE,"E3.sketch_text.stroke-59"),sQuery(id+"F0.wireOp",EDGE,"E3.sketch_text.stroke-60"),sQuery(id+"F0.wireOp",EDGE,"E3.sketch_text.stroke-61"),sQuery(id+"F0.wireOp",EDGE,"E3.sketch_text.stroke-62"),sQuery(id+"F0.wireOp",EDGE,"E3.sketch_text.stroke-63"),sQuery(id+"F0.wireOp",EDGE,"E3.sketch_text.stroke-64"),sQuery(id+"F0.wireOp",EDGE,"E3.sketch_text.stroke-65"),sQuery(id+"F0.wireOp",EDGE,"E3.sketch_text.stroke-66"),sQuery(id+"F0.wireOp",EDGE,"E3.sketch_text.stroke-67"),sQuery(id+"F0.wireOp",EDGE,"E3.sketch_text.stroke-68"),sQuery(id+"F0.wireOp",EDGE,"E3.sketch_text.stroke-69"),sQuery(id+"F0.wireOp",EDGE,"E3.sketch_text.stroke-70"),sQuery(id+"F0.wireOp",EDGE,"E3.sketch_text.stroke-71"),sQuery(id+"F0.wireOp",EDGE,"E3.sketch_text.stroke-72"),sQuery(id+"F0.wireOp",EDGE,"E3.sketch_text.stroke-73"),sQuery(id+"F0.wireOp",EDGE,"E3.sketch_text.stroke-74"),sQuery(id+"F0.wireOp",EDGE,"E3.sketch_text.stroke-88"),sQuery(id+"F0.wireOp",EDGE,"E3.sketch_text.stroke-89"),sQuery(id+"F0.wireOp",EDGE,"E3.sketch_text.stroke-90"),sQuery(id+"F0.wireOp",EDGE,"E3.sketch_text.stroke-91"),sQuery(id+"F0.wireOp",EDGE,"E3.sketch_text.stroke-92"),sQuery(id+"F0.wireOp",EDGE,"E3.sketch_text.stroke-93"),sQuery(id+"F0.wireOp",EDGE,"E3.sketch_text.stroke-94"),sQuery(id+"F0.wireOp",EDGE,"E3.sketch_text.stroke-95"),sQuery(id+"F0.wireOp",EDGE,"E3.sketch_text.stroke-96"),sQuery(id+"F0.wireOp",EDGE,"E3.sketch_text.stroke-97"),sQuery(id+"F0.wireOp",EDGE,"E3.sketch_text.stroke-98"),sQuery(id+"F0.wireOp",EDGE,"E3.sketch_text.stroke-99"),sQuery(id+"F0.wireOp",EDGE,"E3.sketch_text.stroke-106"),sQuery(id+"F0.wireOp",EDGE,"E3.sketch_text.stroke-107"),sQuery(id+"F0.wireOp",EDGE,"E3.sketch_text.stroke-108"),sQuery(id+"F0.wireOp",EDGE,"E3.sketch_text.stroke-109"),sQuery(id+"F0.wireOp",EDGE,"E3.sketch_text.stroke-110"),sQuery(id+"F0.wireOp",EDGE,"E3.sketch_text.stroke-111"),sQuery(id+"F0.wireOp",EDGE,"E3.sketch_text.stroke-112"),sQuery(id+"F0.wireOp",EDGE,"E3.sketch_text.stroke-113"),sQuery(id+"F0.wireOp",EDGE,"E3.sketch_text.stroke-114"),sQuery(id+"F0.wireOp",EDGE,"E3.sketch_text.stroke-115"),sQuery(id+"F0.wireOp",EDGE,"E3.sketch_text.stroke-116"),sQuery(id+"F0.wireOp",EDGE,"E3.sketch_text.stroke-117"),sQuery(id+"F0.wireOp",EDGE,"E3.sketch_text.stroke-118"),sQuery(id+"F0.wireOp",EDGE,"E3.sketch_text.stroke-119"),sQuery(id+"F0.wireOp",EDGE,"E3.sketch_text.stroke-120"),sQuery(id+"F0.wireOp",EDGE,"E3.sketch_text.stroke-121"),sQuery(id+"F0.wireOp",EDGE,"E3.sketch_text.stroke-122"),sQuery(id+"F0.wireOp",EDGE,"E3.sketch_text.stroke-123"),sQuery(id+"F0.wireOp",EDGE,"E3.sketch_text.stroke-124"),sQuery(id+"F0.wireOp",EDGE,"E3.sketch_text.stroke-125"),sQuery(id+"F0.wireOp",EDGE,"E3.sketch_text.stroke-126"),sQuery(id+"F0.wireOp",EDGE,"E3.sketch_text.stroke-127"),sQuery(id+"F0.wireOp",EDGE,"E3.sketch_text.stroke-128"),sQuery(id+"F0.wireOp",EDGE,"E3.sketch_text.stroke-129"),sQuery(id+"F0.wireOp",EDGE,"E3.sketch_text.stroke-130"),sQuery(id+"F0.wireOp",EDGE,"E3.sketch_text.stroke-131"),sQuery(id+"F0.wireOp",EDGE,"E3.sketch_text.stroke-132"),sQuery(id+"F0.wireOp",EDGE,"E3.sketch_text.stroke-133"),sQuery(id+"F0.wireOp",EDGE,"E3.sketch_text.stroke-134"),sQuery(id+"F0.wireOp",EDGE,"E3.sketch_text.stroke-135"),sQuery(id+"F0.wireOp",EDGE,"E3.sketch_text.stroke-136"),sQuery(id+"F0.wireOp",EDGE,"E3.sketch_text.stroke-137"),sQuery(id+"F0.wireOp",EDGE,"E3.sketch_text.stroke-138"),sQuery(id+"F0.wireOp",EDGE,"E3.sketch_text.stroke-139"),sQuery(id+"F0.wireOp",EDGE,"E3.sketch_text.stroke-140"),sQuery(id+"F0.wireOp",EDGE,"E3.sketch_text.stroke-141"),sQuery(id+"F0.wireOp",EDGE,"E3.sketch_text.stroke-142"),sQuery(id+"F0.wireOp",EDGE,"E3.sketch_text.stroke-143"),sQuery(id+"F0.wireOp",EDGE,"E3.sketch_text.stroke-144"),sQuery(id+"F0.wireOp",EDGE,"E3.sketch_text.stroke-145"),sQuery(id+"F0.wireOp",EDGE,"E3.sketch_text.stroke-146"),sQuery(id+"F0.wireOp",EDGE,"E3.sketch_text.stroke-147"),sQuery(id+"F0.wireOp",EDGE,"E3.sketch_text.stroke-155"),sQuery(id+"F0.wireOp",EDGE,"E3.sketch_text.stroke-156"),sQuery(id+"F0.wireOp",EDGE,"E3.sketch_text.stroke-157"),sQuery(id+"F0.wireOp",EDGE,"E3.sketch_text.stroke-158"),sQuery(id+"F0.wireOp",EDGE,"E3.sketch_text.stroke-159"),sQuery(id+"F0.wireOp",EDGE,"E3.sketch_text.stroke-160"),sQuery(id+"F0.wireOp",EDGE,"E3.sketch_text.stroke-161"),sQuery(id+"F0.wireOp",EDGE,"E3.sketch_text.stroke-162"),sQuery(id+"F0.wireOp",EDGE,"E3.sketch_text.stroke-163"),sQuery(id+"F0.wireOp",EDGE,"E3.sketch_text.stroke-164"),sQuery(id+"F0.wireOp",EDGE,"E3.sketch_text.stroke-165"),sQuery(id+"F0.wireOp",EDGE,"E3.sketch_text.stroke-166"),sQuery(id+"F0.wireOp",EDGE,"E3.sketch_text.stroke-167"),sQuery(id+"F0.wireOp",EDGE,"E3.sketch_text.stroke-168"),sQuery(id+"F0.wireOp",EDGE,"E3.sketch_text.stroke-169"),sQuery(id+"F0.wireOp",EDGE,"E3.sketch_text.stroke-170"),sQuery(id+"F0.wireOp",EDGE,"E3.sketch_text.stroke-171"),sQuery(id+"F0.wireOp",EDGE,"E3.sketch_text.stroke-172"),sQuery(id+"F0.wireOp",EDGE,"E3.sketch_text.stroke-173"),sQuery(id+"F0.wireOp",EDGE,"E3.sketch_text.stroke-174"),sQuery(id+"F0.wireOp",EDGE,"E3.sketch_text.stroke-175"),sQuery(id+"F0.wireOp",EDGE,"E3.sketch_text.stroke-176"),sQuery(id+"F0.wireOp",EDGE,"E3.sketch_text.stroke-177"),sQuery(id+"F0.wireOp",EDGE,"E3.sketch_text.stroke-178"),sQuery(id+"F0.wireOp",EDGE,"E3.sketch_text.stroke-179"),sQuery(id+"F0.wireOp",EDGE,"E3.sketch_text.stroke-180"),sQuery(id+"F0.wireOp",EDGE,"E3.sketch_text.stroke-181"),sQuery(id+"F0.wireOp",EDGE,"E3.sketch_text.stroke-182"),sQuery(id+"F0.wireOp",EDGE,"E3.sketch_text.stroke-183"),sQuery(id+"F0.wireOp",EDGE,"E3.sketch_text.stroke-184"),sQuery(id+"F0.wireOp",EDGE,"E3.sketch_text.stroke-185"),sQuery(id+"F0.wireOp",EDGE,"E3.sketch_text.stroke-186"),sQuery(id+"F0.wireOp",EDGE,"E3.sketch_text.stroke-187"),sQuery(id+"F0.wireOp",EDGE,"E3.sketch_text.stroke-188"),sQuery(id+"F0.wireOp",EDGE,"E3.sketch_text.stroke-189"),sQuery(id+"F0.wireOp",EDGE,"E3.sketch_text.stroke-190"),sQuery(id+"F0.wireOp",EDGE,"E3.sketch_text.stroke-191"),sQuery(id+"F0.wireOp",EDGE,"E3.sketch_text.stroke-192"),sQuery(id+"F0.wireOp",EDGE,"E3.sketch_text.stroke-193"),sQuery(id+"F0.wireOp",EDGE,"E3.sketch_text.stroke-194"),sQuery(id+"F0.wireOp",EDGE,"E3.sketch_text.stroke-195"),sQuery(id+"F0.wireOp",EDGE,"E3.sketch_text.stroke-196"),sQuery(id+"F0.wireOp",EDGE,"E3.sketch_text.stroke-197"),sQuery(id+"F0.wireOp",EDGE,"E3.sketch_text.stroke-198"),sQuery(id+"F0.wireOp",EDGE,"E3.sketch_text.stroke-199"),sQuery(id+"F0.wireOp",EDGE,"E3.sketch_text.stroke-200"),sQuery(id+"F0.wireOp",EDGE,"E3.sketch_text.stroke-201"),sQuery(id+"F0.wireOp",EDGE,"E3.sketch_text.stroke-202"),sQuery(id+"F0.wireOp",EDGE,"E3.sketch_text.stroke-203"),sQuery(id+"F0.wireOp",EDGE,"E3.sketch_text.stroke-204"),sQuery(id+"F0.wireOp",EDGE,"E3.sketch_text.stroke-205"),sQuery(id+"F0.wireOp",EDGE,"E3.sketch_text.stroke-206"),sQuery(id+"F0.wireOp",EDGE,"E3.sketch_text.stroke-207"),sQuery(id+"F0.wireOp",EDGE,"E3.sketch_text.stroke-208"),sQuery(id+"F0.wireOp",EDGE,"E3.sketch_text.stroke-209"),sQuery(id+"F0.wireOp",EDGE,"E3.sketch_text.stroke-210"),sQuery(id+"F0.wireOp",EDGE,"E3.sketch_text.stroke-211"),sQuery(id+"F0.wireOp",EDGE,"E3.sketch_text.stroke-212"),sQuery(id+"F0.wireOp",EDGE,"E3.sketch_text.stroke-213"),sQuery(id+"F0.wireOp",EDGE,"E3.sketch_text.stroke-214"),sQuery(id+"F0.wireOp",EDGE,"E3.sketch_text.stroke-215"),sQuery(id+"F0.wireOp",EDGE,"E3.sketch_text.stroke-216"),sQuery(id+"F0.wireOp",EDGE,"E3.sketch_text.stroke-217"),sQuery(id+"F0.wireOp",EDGE,"E3.sketch_text.stroke-218"),sQuery(id+"F0.wireOp",EDGE,"E3.sketch_text.stroke-219"),sQuery(id+"F0.wireOp",EDGE,"E3.sketch_text.stroke-220"),sQuery(id+"F0.wireOp",EDGE,"E3.sketch_text.stroke-221"),sQuery(id+"F0.wireOp",EDGE,"E3.sketch_text.stroke-222"),sQuery(id+"F0.wireOp",EDGE,"E3.sketch_text.stroke-223"),sQuery(id+"F0.wireOp",EDGE,"E3.sketch_text.stroke-224"),sQuery(id+"F0.wireOp",EDGE,"E3.sketch_text.stroke-225"),sQuery(id+"F0.wireOp",EDGE,"E3.sketch_text.stroke-226"),sQuery(id+"F0.wireOp",EDGE,"E3.sketch_text.stroke-227"),sQuery(id+"F0.wireOp",EDGE,"E3.sketch_text.stroke-228"),sQuery(id+"F0.wireOp",EDGE,"E3.sketch_text.stroke-229"),sQuery(id+"F0.wireOp",EDGE,"E3.sketch_text.stroke-230"),sQuery(id+"F0.wireOp",EDGE,"E3.sketch_text.stroke-231"),sQuery(id+"F0.wireOp",EDGE,"E3.sketch_text.stroke-232"),sQuery(id+"F0.wireOp",EDGE,"E3.sketch_text.stroke-233"),sQuery(id+"F0.wireOp",EDGE,"E3.sketch_text.stroke-234"),sQuery(id+"F0.wireOp",EDGE,"E3.sketch_text.stroke-235"),sQuery(id+"F0.wireOp",EDGE,"E3.sketch_text.stroke-236"),sQuery(id+"F0.wireOp",EDGE,"E3.sketch_text.stroke-237"),sQuery(id+"F0.wireOp",EDGE,"E3.sketch_text.stroke-238"),sQuery(id+"F0.wireOp",EDGE,"E3.sketch_text.stroke-244"),sQuery(id+"F0.wireOp",EDGE,"E3.sketch_text.stroke-245"),sQuery(id+"F0.wireOp",EDGE,"E3.sketch_text.stroke-246"),sQuery(id+"F0.wireOp",EDGE,"E3.sketch_text.stroke-247"),sQuery(id+"F0.wireOp",EDGE,"E3.sketch_text.stroke-248"),sQuery(id+"F0.wireOp",EDGE,"E3.sketch_text.stroke-249"),sQuery(id+"F0.wireOp",EDGE,"E3.sketch_text.stroke-250"),sQuery(id+"F0.wireOp",EDGE,"E3.sketch_text.stroke-251"),sQuery(id+"F0.wireOp",EDGE,"E3.sketch_text.stroke-252"),sQuery(id+"F0.wireOp",EDGE,"E3.sketch_text.stroke-253"),sQuery(id+"F0.wireOp",EDGE,"E3.sketch_text.stroke-254"),sQuery(id+"F0.wireOp",EDGE,"E3.sketch_text.stroke-255"),sQuery(id+"F0.wireOp",EDGE,"E3.sketch_text.stroke-256"),sQuery(id+"F0.wireOp",EDGE,"E3.sketch_text.stroke-257"),sQuery(id+"F0.wireOp",EDGE,"E3.sketch_text.stroke-258"),sQuery(id+"F0.wireOp",EDGE,"E3.sketch_text.stroke-259"),sQuery(id+"F0.wireOp",EDGE,"E3.sketch_text.stroke-260"),sQuery(id+"F0.wireOp",EDGE,"E4.sketch_text.stroke-0"),sQuery(id+"F0.wireOp",EDGE,"E4.sketch_text.stroke-1"),sQuery(id+"F0.wireOp",EDGE,"E4.sketch_text.stroke-2"),sQuery(id+"F0.wireOp",EDGE,"E4.sketch_text.stroke-3"),sQuery(id+"F0.wireOp",EDGE,"E4.sketch_text.stroke-4"),sQuery(id+"F0.wireOp",EDGE,"E4.sketch_text.stroke-5"),sQuery(id+"F0.wireOp",EDGE,"E4.sketch_text.stroke-6"),sQuery(id+"F0.wireOp",EDGE,"E4.sketch_text.stroke-7"),sQuery(id+"F0.wireOp",EDGE,"E4.sketch_text.stroke-8"),sQuery(id+"F0.wireOp",EDGE,"E4.sketch_text.stroke-9"),sQuery(id+"F0.wireOp",EDGE,"E4.sketch_text.stroke-10"),sQuery(id+"F0.wireOp",EDGE,"E4.sketch_text.stroke-11"),sQuery(id+"F0.wireOp",EDGE,"E4.sketch_text.stroke-12"),sQuery(id+"F0.wireOp",EDGE,"E4.sketch_text.stroke-13"),sQuery(id+"F0.wireOp",EDGE,"E4.sketch_text.stroke-14"),sQuery(id+"F0.wireOp",EDGE,"E4.sketch_text.stroke-15"),sQuery(id+"F0.wireOp",EDGE,"E4.sketch_text.stroke-16"),sQuery(id+"F0.wireOp",EDGE,"E4.sketch_text.stroke-17"),sQuery(id+"F0.wireOp",EDGE,"E4.sketch_text.stroke-18"),sQuery(id+"F0.wireOp",EDGE,"E4.sketch_text.stroke-19"),sQuery(id+"F0.wireOp",EDGE,"E4.sketch_text.stroke-20"),sQuery(id+"F0.wireOp",EDGE,"E4.sketch_text.stroke-21"),sQuery(id+"F0.wireOp",EDGE,"E4.sketch_text.stroke-28"),sQuery(id+"F0.wireOp",EDGE,"E4.sketch_text.stroke-29"),sQuery(id+"F0.wireOp",EDGE,"E4.sketch_text.stroke-30"),sQuery(id+"F0.wireOp",EDGE,"E4.sketch_text.stroke-31"),sQuery(id+"F0.wireOp",EDGE,"E4.sketch_text.stroke-32"),sQuery(id+"F0.wireOp",EDGE,"E4.sketch_text.stroke-33"),sQuery(id+"F0.wireOp",EDGE,"E4.sketch_text.stroke-34"),sQuery(id+"F0.wireOp",EDGE,"E4.sketch_text.stroke-35"),sQuery(id+"F0.wireOp",EDGE,"E4.sketch_text.stroke-36"),sQuery(id+"F0.wireOp",EDGE,"E4.sketch_text.stroke-37"),sQuery(id+"F0.wireOp",EDGE,"E4.sketch_text.stroke-38"),sQuery(id+"F0.wireOp",EDGE,"E4.sketch_text.stroke-39"),sQuery(id+"F0.wireOp",EDGE,"E4.sketch_text.stroke-40"),sQuery(id+"F0.wireOp",EDGE,"E4.sketch_text.stroke-41"),sQuery(id+"F0.wireOp",EDGE,"E4.sketch_text.stroke-42"),sQuery(id+"F0.wireOp",EDGE,"E4.sketch_text.stroke-43"),sQuery(id+"F0.wireOp",EDGE,"E4.sketch_text.stroke-44"),sQuery(id+"F0.wireOp",EDGE,"E4.sketch_text.stroke-45"),sQuery(id+"F0.wireOp",EDGE,"E4.sketch_text.stroke-46"),sQuery(id+"F0.wireOp",EDGE,"E4.sketch_text.stroke-47"),sQuery(id+"F0.wireOp",EDGE,"E4.sketch_text.stroke-48"),sQuery(id+"F0.wireOp",EDGE,"E4.sketch_text.stroke-49"),sQuery(id+"F0.wireOp",EDGE,"E4.sketch_text.stroke-50"),sQuery(id+"F0.wireOp",EDGE,"E4.sketch_text.stroke-51"),sQuery(id+"F0.wireOp",EDGE,"E4.sketch_text.stroke-52"),sQuery(id+"F0.wireOp",EDGE,"E4.sketch_text.stroke-53"),sQuery(id+"F0.wireOp",EDGE,"E4.sketch_text.stroke-54"),sQuery(id+"F0.wireOp",EDGE,"E4.sketch_text.stroke-55"),sQuery(id+"F0.wireOp",EDGE,"E4.sketch_text.stroke-56"),sQuery(id+"F0.wireOp",EDGE,"E4.sketch_text.stroke-57"),sQuery(id+"F0.wireOp",EDGE,"E4.sketch_text.stroke-58"),sQuery(id+"F0.wireOp",EDGE,"E4.sketch_text.stroke-59"),sQuery(id+"F0.wireOp",EDGE,"E4.sketch_text.stroke-60"),sQuery(id+"F0.wireOp",EDGE,"E4.sketch_text.stroke-61"),sQuery(id+"F0.wireOp",EDGE,"E4.sketch_text.stroke-62"),sQuery(id+"F0.wireOp",EDGE,"E4.sketch_text.stroke-63"),sQuery(id+"F0.wireOp",EDGE,"E4.sketch_text.stroke-64"),sQuery(id+"F0.wireOp",EDGE,"E4.sketch_text.stroke-65"),sQuery(id+"F0.wireOp",EDGE,"E4.sketch_text.stroke-66"),sQuery(id+"F0.wireOp",EDGE,"E4.sketch_text.stroke-67"),sQuery(id+"F0.wireOp",EDGE,"E4.sketch_text.stroke-68"),sQuery(id+"F0.wireOp",EDGE,"E4.sketch_text.stroke-69"),sQuery(id+"F0.wireOp",EDGE,"E4.sketch_text.stroke-70"),sQuery(id+"F0.wireOp",EDGE,"E4.sketch_text.stroke-71"),sQuery(id+"F0.wireOp",EDGE,"E4.sketch_text.stroke-72"),sQuery(id+"F0.wireOp",EDGE,"E4.sketch_text.stroke-73"),sQuery(id+"F0.wireOp",EDGE,"E4.sketch_text.stroke-74"),sQuery(id+"F0.wireOp",EDGE,"E4.sketch_text.stroke-85"),sQuery(id+"F0.wireOp",EDGE,"E4.sketch_text.stroke-86"),sQuery(id+"F0.wireOp",EDGE,"E4.sketch_text.stroke-87"),sQuery(id+"F0.wireOp",EDGE,"E4.sketch_text.stroke-88"),sQuery(id+"F0.wireOp",EDGE,"E4.sketch_text.stroke-89"),sQuery(id+"F0.wireOp",EDGE,"E4.sketch_text.stroke-90"),sQuery(id+"F0.wireOp",EDGE,"E4.sketch_text.stroke-91"),sQuery(id+"F0.wireOp",EDGE,"E4.sketch_text.stroke-92"),sQuery(id+"F0.wireOp",EDGE,"E4.sketch_text.stroke-93"),sQuery(id+"F0.wireOp",EDGE,"E4.sketch_text.stroke-94"),sQuery(id+"F0.wireOp",EDGE,"E4.sketch_text.stroke-95"),sQuery(id+"F0.wireOp",EDGE,"E4.sketch_text.stroke-96"),sQuery(id+"F0.wireOp",EDGE,"E4.sketch_text.stroke-97"),sQuery(id+"F0.wireOp",EDGE,"E4.sketch_text.stroke-98"),sQuery(id+"F0.wireOp",EDGE,"E4.sketch_text.stroke-99"),sQuery(id+"F0.wireOp",EDGE,"E4.sketch_text.stroke-100"),sQuery(id+"F0.wireOp",EDGE,"E4.sketch_text.stroke-101"),sQuery(id+"F0.wireOp",EDGE,"E4.sketch_text.stroke-102"),sQuery(id+"F0.wireOp",EDGE,"E4.sketch_text.stroke-103"),sQuery(id+"F0.wireOp",EDGE,"E4.sketch_text.stroke-104"),sQuery(id+"F0.wireOp",EDGE,"E4.sketch_text.stroke-105"),sQuery(id+"F0.wireOp",EDGE,"E4.sketch_text.stroke-106"),sQuery(id+"F0.wireOp",EDGE,"E4.sketch_text.stroke-107"),sQuery(id+"F0.wireOp",EDGE,"E4.sketch_text.stroke-108"),sQuery(id+"F0.wireOp",EDGE,"E4.sketch_text.stroke-109"),sQuery(id+"F0.wireOp",EDGE,"E4.sketch_text.stroke-110"),sQuery(id+"F0.wireOp",EDGE,"E4.sketch_text.stroke-111"),sQuery(id+"F0.wireOp",EDGE,"E4.sketch_text.stroke-112"),sQuery(id+"F0.wireOp",EDGE,"E4.sketch_text.stroke-113"),sQuery(id+"F0.wireOp",EDGE,"E4.sketch_text.stroke-114"),sQuery(id+"F0.wireOp",EDGE,"E4.sketch_text.stroke-115"),sQuery(id+"F0.wireOp",EDGE,"E4.sketch_text.stroke-116"),sQuery(id+"F0.wireOp",EDGE,"E4.sketch_text.stroke-117"),sQuery(id+"F0.wireOp",EDGE,"E4.sketch_text.stroke-118"),sQuery(id+"F0.wireOp",EDGE,"E4.sketch_text.stroke-119"),sQuery(id+"F0.wireOp",EDGE,"E4.sketch_text.stroke-120"),sQuery(id+"F0.wireOp",EDGE,"E4.sketch_text.stroke-121"),sQuery(id+"F0.wireOp",EDGE,"E4.sketch_text.stroke-122"),sQuery(id+"F0.wireOp",EDGE,"E4.sketch_text.stroke-123"),sQuery(id+"F0.wireOp",EDGE,"E4.sketch_text.stroke-124"),sQuery(id+"F0.wireOp",EDGE,"E4.sketch_text.stroke-138"),sQuery(id+"F0.wireOp",EDGE,"E4.sketch_text.stroke-139"),sQuery(id+"F0.wireOp",EDGE,"E4.sketch_text.stroke-140"),sQuery(id+"F0.wireOp",EDGE,"E4.sketch_text.stroke-141"),sQuery(id+"F0.wireOp",EDGE,"E4.sketch_text.stroke-142"),sQuery(id+"F0.wireOp",EDGE,"E4.sketch_text.stroke-143"),sQuery(id+"F0.wireOp",EDGE,"E4.sketch_text.stroke-144"),sQuery(id+"F0.wireOp",EDGE,"E4.sketch_text.stroke-145"),sQuery(id+"F0.wireOp",EDGE,"E4.sketch_text.stroke-146"),sQuery(id+"F0.wireOp",EDGE,"E4.sketch_text.stroke-147"),sQuery(id+"F0.wireOp",EDGE,"E4.sketch_text.stroke-148"),sQuery(id+"F0.wireOp",EDGE,"E4.sketch_text.stroke-149"),sQuery(id+"F0.wireOp",EDGE,"E4.sketch_text.stroke-156"),sQuery(id+"F0.wireOp",EDGE,"E4.sketch_text.stroke-157"),sQuery(id+"F0.wireOp",EDGE,"E4.sketch_text.stroke-158"),sQuery(id+"F0.wireOp",EDGE,"E4.sketch_text.stroke-159"),sQuery(id+"F0.wireOp",EDGE,"E4.sketch_text.stroke-160"),sQuery(id+"F0.wireOp",EDGE,"E4.sketch_text.stroke-161"),sQuery(id+"F0.wireOp",EDGE,"E4.sketch_text.stroke-162"),sQuery(id+"F0.wireOp",EDGE,"E4.sketch_text.stroke-163"),sQuery(id+"F0.wireOp",EDGE,"E4.sketch_text.stroke-164"),sQuery(id+"F0.wireOp",EDGE,"E4.sketch_text.stroke-165"),sQuery(id+"F0.wireOp",EDGE,"E4.sketch_text.stroke-166"),sQuery(id+"F0.wireOp",EDGE,"E4.sketch_text.stroke-167"),sQuery(id+"F0.wireOp",EDGE,"E4.sketch_text.stroke-168"),sQuery(id+"F0.wireOp",EDGE,"E4.sketch_text.stroke-169"),sQuery(id+"F0.wireOp",EDGE,"E4.sketch_text.stroke-170"),sQuery(id+"F0.wireOp",EDGE,"E4.sketch_text.stroke-171"),sQuery(id+"F0.wireOp",EDGE,"E4.sketch_text.stroke-172"),sQuery(id+"F0.wireOp",EDGE,"E4.sketch_text.stroke-173"),sQuery(id+"F0.wireOp",EDGE,"E4.sketch_text.stroke-174"),sQuery(id+"F0.wireOp",EDGE,"E4.sketch_text.stroke-175"),sQuery(id+"F0.wireOp",EDGE,"E4.sketch_text.stroke-176"),sQuery(id+"F0.wireOp",EDGE,"E4.sketch_text.stroke-177"),sQuery(id+"F0.wireOp",EDGE,"E4.sketch_text.stroke-178"),sQuery(id+"F0.wireOp",EDGE,"E4.sketch_text.stroke-179"),sQuery(id+"F0.wireOp",EDGE,"E4.sketch_text.stroke-180"),sQuery(id+"F0.wireOp",EDGE,"E4.sketch_text.stroke-181"),sQuery(id+"F0.wireOp",EDGE,"E4.sketch_text.stroke-182"),sQuery(id+"F0.wireOp",EDGE,"E4.sketch_text.stroke-183"),sQuery(id+"F0.wireOp",EDGE,"E4.sketch_text.stroke-184"),sQuery(id+"F0.wireOp",EDGE,"E4.sketch_text.stroke-185"),sQuery(id+"F0.wireOp",EDGE,"E4.sketch_text.stroke-186"),sQuery(id+"F0.wireOp",EDGE,"E4.sketch_text.stroke-187"),sQuery(id+"F0.wireOp",EDGE,"E4.sketch_text.stroke-188"),sQuery(id+"F0.wireOp",EDGE,"E4.sketch_text.stroke-189"),sQuery(id+"F0.wireOp",EDGE,"E4.sketch_text.stroke-190"),sQuery(id+"F0.wireOp",EDGE,"E4.sketch_text.stroke-191"),sQuery(id+"F0.wireOp",EDGE,"E4.sketch_text.stroke-192"),sQuery(id+"F0.wireOp",EDGE,"E4.sketch_text.stroke-193"),sQuery(id+"F0.wireOp",EDGE,"E4.sketch_text.stroke-194"),sQuery(id+"F0.wireOp",EDGE,"E4.sketch_text.stroke-195"),sQuery(id+"F0.wireOp",EDGE,"E4.sketch_text.stroke-196"),sQuery(id+"F0.wireOp",EDGE,"E4.sketch_text.stroke-197"),sQuery(id+"F0.wireOp",EDGE,"E4.sketch_text.stroke-198"),sQuery(id+"F0.wireOp",EDGE,"E4.sketch_text.stroke-199"),sQuery(id+"F0.wireOp",EDGE,"E4.sketch_text.stroke-200"),sQuery(id+"F0.wireOp",EDGE,"E4.sketch_text.stroke-201"),sQuery(id+"F0.wireOp",EDGE,"E4.sketch_text.stroke-208"),sQuery(id+"F0.wireOp",EDGE,"E4.sketch_text.stroke-209"),sQuery(id+"F0.wireOp",EDGE,"E4.sketch_text.stroke-210"),sQuery(id+"F0.wireOp",EDGE,"E4.sketch_text.stroke-211"),sQuery(id+"F0.wireOp",EDGE,"E4.sketch_text.stroke-212"),sQuery(id+"F0.wireOp",EDGE,"E4.sketch_text.stroke-213"),sQuery(id+"F0.wireOp",EDGE,"E4.sketch_text.stroke-214"),sQuery(id+"F0.wireOp",EDGE,"E4.sketch_text.stroke-215"),sQuery(id+"F0.wireOp",EDGE,"E4.sketch_text.stroke-216"),sQuery(id+"F0.wireOp",EDGE,"E4.sketch_text.stroke-217"),sQuery(id+"F0.wireOp",EDGE,"E4.sketch_text.stroke-218"),sQuery(id+"F0.wireOp",EDGE,"E4.sketch_text.stroke-219"),sQuery(id+"F0.wireOp",EDGE,"E4.sketch_text.stroke-220"),sQuery(id+"F0.wireOp",EDGE,"E4.sketch_text.stroke-221"),sQuery(id+"F0.wireOp",EDGE,"E4.sketch_text.stroke-222"),sQuery(id+"F0.wireOp",EDGE,"E4.sketch_text.stroke-223"),sQuery(id+"F0.wireOp",EDGE,"E4.sketch_text.stroke-224"),sQuery(id+"F0.wireOp",EDGE,"E4.sketch_text.stroke-225"),sQuery(id+"F0.wireOp",EDGE,"E4.sketch_text.stroke-226"),sQuery(id+"F0.wireOp",EDGE,"E4.sketch_text.stroke-227"),sQuery(id+"F0.wireOp",EDGE,"E4.sketch_text.stroke-228"),sQuery(id+"F0.wireOp",EDGE,"E4.sketch_text.stroke-229"),sQuery(id+"F0.wireOp",EDGE,"E4.sketch_text.stroke-230"),sQuery(id+"F0.wireOp",EDGE,"E4.sketch_text.stroke-231"),sQuery(id+"F0.wireOp",EDGE,"E4.sketch_text.stroke-232"),sQuery(id+"F0.wireOp",EDGE,"E4.sketch_text.stroke-233"),sQuery(id+"F0.wireOp",EDGE,"E4.sketch_text.stroke-234"),sQuery(id+"F0.wireOp",EDGE,"E4.sketch_text.stroke-235"),sQuery(id+"F0.wireOp",EDGE,"E4.sketch_text.stroke-236"),sQuery(id+"F0.wireOp",EDGE,"E4.sketch_text.stroke-237"),sQuery(id+"F0.wireOp",EDGE,"E4.sketch_text.stroke-238"),sQuery(id+"F0.wireOp",EDGE,"E4.sketch_text.stroke-239"),sQuery(id+"F0.wireOp",EDGE,"E4.sketch_text.stroke-240"),sQuery(id+"F0.wireOp",EDGE,"E4.sketch_text.stroke-241"),sQuery(id+"F0.wireOp",EDGE,"E4.sketch_text.stroke-242"),sQuery(id+"F0.wireOp",EDGE,"E4.sketch_text.stroke-243"),sQuery(id+"F0.wireOp",EDGE,"E4.sketch_text.stroke-244"),sQuery(id+"F0.wireOp",EDGE,"E4.sketch_text.stroke-245"),sQuery(id+"F0.wireOp",EDGE,"E4.sketch_text.stroke-246"),sQuery(id+"F0.wireOp",EDGE,"E4.sketch_text.stroke-247"),sQuery(id+"F0.wireOp",EDGE,"E4.sketch_text.stroke-248"),sQuery(id+"F0.wireOp",EDGE,"E4.sketch_text.stroke-249"),sQuery(id+"F0.wireOp",EDGE,"E4.sketch_text.stroke-250"),sQuery(id+"F0.wireOp",EDGE,"E4.sketch_text.stroke-251"),sQuery(id+"F0.wireOp",EDGE,"E4.sketch_text.stroke-252"),sQuery(id+"F0.wireOp",EDGE,"E4.sketch_text.stroke-253"),sQuery(id+"F0.wireOp",EDGE,"E4.sketch_text.stroke-254"),sQuery(id+"F0.wireOp",EDGE,"E4.sketch_text.stroke-255"),sQuery(id+"F0.wireOp",EDGE,"E4.sketch_text.stroke-256"),sQuery(id+"F0.wireOp",EDGE,"E4.sketch_text.stroke-257"),sQuery(id+"F0.wireOp",EDGE,"E4.sketch_text.stroke-258"),sQuery(id+"F0.wireOp",EDGE,"E4.sketch_text.stroke-259"),sQuery(id+"F0.wireOp",EDGE,"E4.sketch_text.stroke-260"),sQuery(id+"F0.wireOp",EDGE,"E4.sketch_text.stroke-261"),sQuery(id+"F0.wireOp",EDGE,"E4.sketch_text.stroke-262"),sQuery(id+"F0.wireOp",EDGE,"E4.sketch_text.stroke-263"),sQuery(id+"F0.wireOp",EDGE,"E4.sketch_text.stroke-264"),sQuery(id+"F0.wireOp",EDGE,"E4.sketch_text.stroke-265"),sQuery(id+"F0.wireOp",EDGE,"E4.sketch_text.stroke-266"),sQuery(id+"F0.wireOp",EDGE,"E4.sketch_text.stroke-267"),sQuery(id+"F0.wireOp",EDGE,"E4.sketch_text.stroke-268"),sQuery(id+"F0.wireOp",EDGE,"E4.sketch_text.stroke-269"),sQuery(id+"F0.wireOp",EDGE,"E4.sketch_text.stroke-270"),sQuery(id+"F0.wireOp",EDGE,"E4.sketch_text.stroke-271"),sQuery(id+"F0.wireOp",EDGE,"E4.sketch_text.stroke-272"),sQuery(id+"F0.wireOp",EDGE,"E4.sketch_text.stroke-273"),sQuery(id+"F0.wireOp",EDGE,"E4.sketch_text.stroke-274"),sQuery(id+"F0.wireOp",EDGE,"E4.sketch_text.stroke-275"),sQuery(id+"F0.wireOp",EDGE,"E4.sketch_text.stroke-276"),sQuery(id+"F0.wireOp",EDGE,"E4.sketch_text.stroke-283"),sQuery(id+"F0.wireOp",EDGE,"E4.sketch_text.stroke-284"),sQuery(id+"F0.wireOp",EDGE,"E4.sketch_text.stroke-285"),sQuery(id+"F0.wireOp",EDGE,"E4.sketch_text.stroke-286"),sQuery(id+"F0.wireOp",EDGE,"E4.sketch_text.stroke-287"),sQuery(id+"F0.wireOp",EDGE,"E4.sketch_text.stroke-288"),sQuery(id+"F0.wireOp",EDGE,"E4.sketch_text.stroke-289"),sQuery(id+"F0.wireOp",EDGE,"E4.sketch_text.stroke-290"),sQuery(id+"F0.wireOp",EDGE,"E4.sketch_text.stroke-291"),sQuery(id+"F0.wireOp",EDGE,"E4.sketch_text.stroke-292"),sQuery(id+"F0.wireOp",EDGE,"E4.sketch_text.stroke-293"),sQuery(id+"F0.wireOp",EDGE,"E4.sketch_text.stroke-294"),sQuery(id+"F0.wireOp",EDGE,"E4.sketch_text.stroke-295"),sQuery(id+"F0.wireOp",EDGE,"E4.sketch_text.stroke-296"),sQuery(id+"F0.wireOp",EDGE,"E4.sketch_text.stroke-297"),sQuery(id+"F0.wireOp",EDGE,"E4.sketch_text.stroke-298"),sQuery(id+"F0.wireOp",EDGE,"E4.sketch_text.stroke-299"),sQuery(id+"F0.wireOp",EDGE,"E4.sketch_text.stroke-300"),sQuery(id+"F0.wireOp",EDGE,"E4.sketch_text.stroke-301"),sQuery(id+"F0.wireOp",EDGE,"E4.sketch_text.stroke-302"),sQuery(id+"F0.wireOp",EDGE,"E4.sketch_text.stroke-303"),sQuery(id+"F0.wireOp",EDGE,"E4.sketch_text.stroke-304"),sQuery(id+"F0.wireOp",EDGE,"E4.sketch_text.stroke-305"),sQuery(id+"F0.wireOp",EDGE,"E4.sketch_text.stroke-306"),sQuery(id+"F0.wireOp",EDGE,"E4.sketch_text.stroke-307"),sQuery(id+"F0.wireOp",EDGE,"E4.sketch_text.stroke-308"),sQuery(id+"F0.wireOp",EDGE,"E4.sketch_text.stroke-309"),sQuery(id+"F0.wireOp",EDGE,"E4.sketch_text.stroke-310"),sQuery(id+"F0.wireOp",EDGE,"E4.sketch_text.stroke-321"),sQuery(id+"F0.wireOp",EDGE,"E4.sketch_text.stroke-322"),sQuery(id+"F0.wireOp",EDGE,"E4.sketch_text.stroke-323"),sQuery(id+"F0.wireOp",EDGE,"E4.sketch_text.stroke-324"),sQuery(id+"F0.wireOp",EDGE,"E4.sketch_text.stroke-325"),sQuery(id+"F0.wireOp",EDGE,"E4.sketch_text.stroke-326"),sQuery(id+"F0.wireOp",EDGE,"E4.sketch_text.stroke-327"),sQuery(id+"F0.wireOp",EDGE,"E4.sketch_text.stroke-328"),sQuery(id+"F0.wireOp",EDGE,"E4.sketch_text.stroke-329"),sQuery(id+"F0.wireOp",EDGE,"E4.sketch_text.stroke-330"),sQuery(id+"F0.wireOp",EDGE,"E4.sketch_text.stroke-331"),sQuery(id+"F0.wireOp",EDGE,"E4.sketch_text.stroke-332"),sQuery(id+"F0.wireOp",EDGE,"E4.sketch_text.stroke-333"),sQuery(id+"F0.wireOp",EDGE,"E4.sketch_text.stroke-334"),sQuery(id+"F0.wireOp",EDGE,"E4.sketch_text.stroke-335"),sQuery(id+"F0.wireOp",EDGE,"E4.sketch_text.stroke-336"),sQuery(id+"F0.wireOp",EDGE,"E4.sketch_text.stroke-337"),sQuery(id+"F0.wireOp",EDGE,"E4.sketch_text.stroke-338"),sQuery(id+"F0.wireOp",EDGE,"E4.sketch_text.stroke-339"),sQuery(id+"F0.wireOp",EDGE,"E4.sketch_text.stroke-340"),sQuery(id+"F0.wireOp",EDGE,"E4.sketch_text.stroke-341"),sQuery(id+"F0.wireOp",EDGE,"E4.sketch_text.stroke-342"),sQuery(id+"F0.wireOp",EDGE,"E4.sketch_text.stroke-343"),sQuery(id+"F0.wireOp",EDGE,"E4.sketch_text.stroke-344"),sQuery(id+"F0.wireOp",EDGE,"E4.sketch_text.stroke-345"),sQuery(id+"F0.wireOp",EDGE,"E4.sketch_text.stroke-346"),sQuery(id+"F0.wireOp",EDGE,"E4.sketch_text.stroke-347"),sQuery(id+"F0.wireOp",EDGE,"E4.sketch_text.stroke-348"),sQuery(id+"F0.wireOp",EDGE,"E4.sketch_text.stroke-359"),sQuery(id+"F0.wireOp",EDGE,"E4.sketch_text.stroke-360"),sQuery(id+"F0.wireOp",EDGE,"E4.sketch_text.stroke-361"),sQuery(id+"F0.wireOp",EDGE,"E4.sketch_text.stroke-362"),sQuery(id+"F0.wireOp",EDGE,"E4.sketch_text.stroke-363"),sQuery(id+"F0.wireOp",EDGE,"E4.sketch_text.stroke-364"),sQuery(id+"F0.wireOp",EDGE,"E4.sketch_text.stroke-365"),sQuery(id+"F0.wireOp",EDGE,"E4.sketch_text.stroke-366"),sQuery(id+"F0.wireOp",EDGE,"E4.sketch_text.stroke-367"),sQuery(id+"F0.wireOp",EDGE,"E4.sketch_text.stroke-368"),sQuery(id+"F0.wireOp",EDGE,"E4.sketch_text.stroke-369"),sQuery(id+"F0.wireOp",EDGE,"E4.sketch_text.stroke-370"),sQuery(id+"F0.wireOp",EDGE,"E4.sketch_text.stroke-371"),sQuery(id+"F0.wireOp",EDGE,"E4.sketch_text.stroke-372"),sQuery(id+"F0.wireOp",EDGE,"E4.sketch_text.stroke-373"),sQuery(id+"F0.wireOp",EDGE,"E4.sketch_text.stroke-374"),sQuery(id+"F0.wireOp",EDGE,"E4.sketch_text.stroke-375"),sQuery(id+"F0.wireOp",EDGE,"E4.sketch_text.stroke-376"),sQuery(id+"F0.wireOp",EDGE,"E4.sketch_text.stroke-377"),sQuery(id+"F0.wireOp",EDGE,"E4.sketch_text.stroke-378"),sQuery(id+"F0.wireOp",EDGE,"E4.sketch_text.stroke-379"),sQuery(id+"F0.wireOp",EDGE,"E4.sketch_text.stroke-380"),sQuery(id+"F0.wireOp",EDGE,"E4.sketch_text.stroke-381"),sQuery(id+"F0.wireOp",EDGE,"E4.sketch_text.stroke-382"),sQuery(id+"F0.wireOp",EDGE,"E4.sketch_text.stroke-383"),sQuery(id+"F0.wireOp",EDGE,"E4.sketch_text.stroke-384"),sQuery(id+"F0.wireOp",EDGE,"E4.sketch_text.stroke-385"),sQuery(id+"F0.wireOp",EDGE,"E4.sketch_text.stroke-386"),sQuery(id+"F0.wireOp",EDGE,"E4.sketch_text.stroke-387"),sQuery(id+"F0.wireOp",EDGE,"E4.sketch_text.stroke-388"),sQuery(id+"F0.wireOp",EDGE,"E4.sketch_text.stroke-389"),sQuery(id+"F0.wireOp",EDGE,"E4.sketch_text.stroke-390"),sQuery(id+"F0.wireOp",EDGE,"E4.sketch_text.stroke-391"),sQuery(id+"F0.wireOp",EDGE,"E4.sketch_text.stroke-392")])],"isStart":true})]});}
            var Q4;
            {var subQ0=sQuery(id+"F0.wireOp",EDGE,"E0.left");var subQ1=sQuery(id+"F0.wireOp",EDGE,"E0.top");Q4=makeQuery(id+"F8.opFillet","BLEND_EDGE",EDGE,{"blendedFrom":[makeQuery(id+"F6.opExtrude","SWEPT_EDGE",EDGE,{"disambiguationData":[OSD([subQ1,subQ0])]}),makeQuery(id+"F6.opExtrude","CAP_FACE",FACE,{"disambiguationData":[OSD([sQuery(id+"F0.wireOp",EDGE,"E0.bottom"),subQ1,subQ0,sQuery(id+"F0.wireOp",EDGE,"E0.right"),sQuery(id+"F0.wireOp",EDGE,"E3.sketch_text.stroke-0"),sQuery(id+"F0.wireOp",EDGE,"E3.sketch_text.stroke-1"),sQuery(id+"F0.wireOp",EDGE,"E3.sketch_text.stroke-2"),sQuery(id+"F0.wireOp",EDGE,"E3.sketch_text.stroke-3"),sQuery(id+"F0.wireOp",EDGE,"E3.sketch_text.stroke-4"),sQuery(id+"F0.wireOp",EDGE,"E3.sketch_text.stroke-5"),sQuery(id+"F0.wireOp",EDGE,"E3.sketch_text.stroke-6"),sQuery(id+"F0.wireOp",EDGE,"E3.sketch_text.stroke-7"),sQuery(id+"F0.wireOp",EDGE,"E3.sketch_text.stroke-8"),sQuery(id+"F0.wireOp",EDGE,"E3.sketch_text.stroke-9"),sQuery(id+"F0.wireOp",EDGE,"E3.sketch_text.stroke-10"),sQuery(id+"F0.wireOp",EDGE,"E3.sketch_text.stroke-11"),sQuery(id+"F0.wireOp",EDGE,"E3.sketch_text.stroke-12"),sQuery(id+"F0.wireOp",EDGE,"E3.sketch_text.stroke-13"),sQuery(id+"F0.wireOp",EDGE,"E3.sketch_text.stroke-14"),sQuery(id+"F0.wireOp",EDGE,"E3.sketch_text.stroke-15"),sQuery(id+"F0.wireOp",EDGE,"E3.sketch_text.stroke-16"),sQuery(id+"F0.wireOp",EDGE,"E3.sketch_text.stroke-17"),sQuery(id+"F0.wireOp",EDGE,"E3.sketch_text.stroke-18"),sQuery(id+"F0.wireOp",EDGE,"E3.sketch_text.stroke-19"),sQuery(id+"F0.wireOp",EDGE,"E3.sketch_text.stroke-20"),sQuery(id+"F0.wireOp",EDGE,"E3.sketch_text.stroke-21"),sQuery(id+"F0.wireOp",EDGE,"E3.sketch_text.stroke-22"),sQuery(id+"F0.wireOp",EDGE,"E3.sketch_text.stroke-23"),sQuery(id+"F0.wireOp",EDGE,"E3.sketch_text.stroke-24"),sQuery(id+"F0.wireOp",EDGE,"E3.sketch_text.stroke-25"),sQuery(id+"F0.wireOp",EDGE,"E3.sketch_text.stroke-26"),sQuery(id+"F0.wireOp",EDGE,"E3.sketch_text.stroke-27"),sQuery(id+"F0.wireOp",EDGE,"E3.sketch_text.stroke-28"),sQuery(id+"F0.wireOp",EDGE,"E3.sketch_text.stroke-29"),sQuery(id+"F0.wireOp",EDGE,"E3.sketch_text.stroke-30"),sQuery(id+"F0.wireOp",EDGE,"E3.sketch_text.stroke-31"),sQuery(id+"F0.wireOp",EDGE,"E3.sketch_text.stroke-32"),sQuery(id+"F0.wireOp",EDGE,"E3.sketch_text.stroke-33"),sQuery(id+"F0.wireOp",EDGE,"E3.sketch_text.stroke-34"),sQuery(id+"F0.wireOp",EDGE,"E3.sketch_text.stroke-35"),sQuery(id+"F0.wireOp",EDGE,"E3.sketch_text.stroke-36"),sQuery(id+"F0.wireOp",EDGE,"E3.sketch_text.stroke-37"),sQuery(id+"F0.wireOp",EDGE,"E3.sketch_text.stroke-38"),sQuery(id+"F0.wireOp",EDGE,"E3.sketch_text.stroke-39"),sQuery(id+"F0.wireOp",EDGE,"E3.sketch_text.stroke-40"),sQuery(id+"F0.wireOp",EDGE,"E3.sketch_text.stroke-41"),sQuery(id+"F0.wireOp",EDGE,"E3.sketch_text.stroke-42"),sQuery(id+"F0.wireOp",EDGE,"E3.sketch_text.stroke-43"),sQuery(id+"F0.wireOp",EDGE,"E3.sketch_text.stroke-44"),sQuery(id+"F0.wireOp",EDGE,"E3.sketch_text.stroke-45"),sQuery(id+"F0.wireOp",EDGE,"E3.sketch_text.stroke-46"),sQuery(id+"F0.wireOp",EDGE,"E3.sketch_text.stroke-47"),sQuery(id+"F0.wireOp",EDGE,"E3.sketch_text.stroke-48"),sQuery(id+"F0.wireOp",EDGE,"E3.sketch_text.stroke-49"),sQuery(id+"F0.wireOp",EDGE,"E3.sketch_text.stroke-50"),sQuery(id+"F0.wireOp",EDGE,"E3.sketch_text.stroke-51"),sQuery(id+"F0.wireOp",EDGE,"E3.sketch_text.stroke-52"),sQuery(id+"F0.wireOp",EDGE,"E3.sketch_text.stroke-53"),sQuery(id+"F0.wireOp",EDGE,"E3.sketch_text.stroke-54"),sQuery(id+"F0.wireOp",EDGE,"E3.sketch_text.stroke-55"),sQuery(id+"F0.wireOp",EDGE,"E3.sketch_text.stroke-56"),sQuery(id+"F0.wireOp",EDGE,"E3.sketch_text.stroke-57"),sQuery(id+"F0.wireOp",EDGE,"E3.sketch_text.stroke-58"),sQuery(id+"F0.wireOp",EDGE,"E3.sketch_text.stroke-59"),sQuery(id+"F0.wireOp",EDGE,"E3.sketch_text.stroke-60"),sQuery(id+"F0.wireOp",EDGE,"E3.sketch_text.stroke-61"),sQuery(id+"F0.wireOp",EDGE,"E3.sketch_text.stroke-62"),sQuery(id+"F0.wireOp",EDGE,"E3.sketch_text.stroke-63"),sQuery(id+"F0.wireOp",EDGE,"E3.sketch_text.stroke-64"),sQuery(id+"F0.wireOp",EDGE,"E3.sketch_text.stroke-65"),sQuery(id+"F0.wireOp",EDGE,"E3.sketch_text.stroke-66"),sQuery(id+"F0.wireOp",EDGE,"E3.sketch_text.stroke-67"),sQuery(id+"F0.wireOp",EDGE,"E3.sketch_text.stroke-68"),sQuery(id+"F0.wireOp",EDGE,"E3.sketch_text.stroke-69"),sQuery(id+"F0.wireOp",EDGE,"E3.sketch_text.stroke-70"),sQuery(id+"F0.wireOp",EDGE,"E3.sketch_text.stroke-71"),sQuery(id+"F0.wireOp",EDGE,"E3.sketch_text.stroke-72"),sQuery(id+"F0.wireOp",EDGE,"E3.sketch_text.stroke-73"),sQuery(id+"F0.wireOp",EDGE,"E3.sketch_text.stroke-74"),sQuery(id+"F0.wireOp",EDGE,"E3.sketch_text.stroke-88"),sQuery(id+"F0.wireOp",EDGE,"E3.sketch_text.stroke-89"),sQuery(id+"F0.wireOp",EDGE,"E3.sketch_text.stroke-90"),sQuery(id+"F0.wireOp",EDGE,"E3.sketch_text.stroke-91"),sQuery(id+"F0.wireOp",EDGE,"E3.sketch_text.stroke-92"),sQuery(id+"F0.wireOp",EDGE,"E3.sketch_text.stroke-93"),sQuery(id+"F0.wireOp",EDGE,"E3.sketch_text.stroke-94"),sQuery(id+"F0.wireOp",EDGE,"E3.sketch_text.stroke-95"),sQuery(id+"F0.wireOp",EDGE,"E3.sketch_text.stroke-96"),sQuery(id+"F0.wireOp",EDGE,"E3.sketch_text.stroke-97"),sQuery(id+"F0.wireOp",EDGE,"E3.sketch_text.stroke-98"),sQuery(id+"F0.wireOp",EDGE,"E3.sketch_text.stroke-99"),sQuery(id+"F0.wireOp",EDGE,"E3.sketch_text.stroke-106"),sQuery(id+"F0.wireOp",EDGE,"E3.sketch_text.stroke-107"),sQuery(id+"F0.wireOp",EDGE,"E3.sketch_text.stroke-108"),sQuery(id+"F0.wireOp",EDGE,"E3.sketch_text.stroke-109"),sQuery(id+"F0.wireOp",EDGE,"E3.sketch_text.stroke-110"),sQuery(id+"F0.wireOp",EDGE,"E3.sketch_text.stroke-111"),sQuery(id+"F0.wireOp",EDGE,"E3.sketch_text.stroke-112"),sQuery(id+"F0.wireOp",EDGE,"E3.sketch_text.stroke-113"),sQuery(id+"F0.wireOp",EDGE,"E3.sketch_text.stroke-114"),sQuery(id+"F0.wireOp",EDGE,"E3.sketch_text.stroke-115"),sQuery(id+"F0.wireOp",EDGE,"E3.sketch_text.stroke-116"),sQuery(id+"F0.wireOp",EDGE,"E3.sketch_text.stroke-117"),sQuery(id+"F0.wireOp",EDGE,"E3.sketch_text.stroke-118"),sQuery(id+"F0.wireOp",EDGE,"E3.sketch_text.stroke-119"),sQuery(id+"F0.wireOp",EDGE,"E3.sketch_text.stroke-120"),sQuery(id+"F0.wireOp",EDGE,"E3.sketch_text.stroke-121"),sQuery(id+"F0.wireOp",EDGE,"E3.sketch_text.stroke-122"),sQuery(id+"F0.wireOp",EDGE,"E3.sketch_text.stroke-123"),sQuery(id+"F0.wireOp",EDGE,"E3.sketch_text.stroke-124"),sQuery(id+"F0.wireOp",EDGE,"E3.sketch_text.stroke-125"),sQuery(id+"F0.wireOp",EDGE,"E3.sketch_text.stroke-126"),sQuery(id+"F0.wireOp",EDGE,"E3.sketch_text.stroke-127"),sQuery(id+"F0.wireOp",EDGE,"E3.sketch_text.stroke-128"),sQuery(id+"F0.wireOp",EDGE,"E3.sketch_text.stroke-129"),sQuery(id+"F0.wireOp",EDGE,"E3.sketch_text.stroke-130"),sQuery(id+"F0.wireOp",EDGE,"E3.sketch_text.stroke-131"),sQuery(id+"F0.wireOp",EDGE,"E3.sketch_text.stroke-132"),sQuery(id+"F0.wireOp",EDGE,"E3.sketch_text.stroke-133"),sQuery(id+"F0.wireOp",EDGE,"E3.sketch_text.stroke-134"),sQuery(id+"F0.wireOp",EDGE,"E3.sketch_text.stroke-135"),sQuery(id+"F0.wireOp",EDGE,"E3.sketch_text.stroke-136"),sQuery(id+"F0.wireOp",EDGE,"E3.sketch_text.stroke-137"),sQuery(id+"F0.wireOp",EDGE,"E3.sketch_text.stroke-138"),sQuery(id+"F0.wireOp",EDGE,"E3.sketch_text.stroke-139"),sQuery(id+"F0.wireOp",EDGE,"E3.sketch_text.stroke-140"),sQuery(id+"F0.wireOp",EDGE,"E3.sketch_text.stroke-141"),sQuery(id+"F0.wireOp",EDGE,"E3.sketch_text.stroke-142"),sQuery(id+"F0.wireOp",EDGE,"E3.sketch_text.stroke-143"),sQuery(id+"F0.wireOp",EDGE,"E3.sketch_text.stroke-144"),sQuery(id+"F0.wireOp",EDGE,"E3.sketch_text.stroke-145"),sQuery(id+"F0.wireOp",EDGE,"E3.sketch_text.stroke-146"),sQuery(id+"F0.wireOp",EDGE,"E3.sketch_text.stroke-147"),sQuery(id+"F0.wireOp",EDGE,"E3.sketch_text.stroke-155"),sQuery(id+"F0.wireOp",EDGE,"E3.sketch_text.stroke-156"),sQuery(id+"F0.wireOp",EDGE,"E3.sketch_text.stroke-157"),sQuery(id+"F0.wireOp",EDGE,"E3.sketch_text.stroke-158"),sQuery(id+"F0.wireOp",EDGE,"E3.sketch_text.stroke-159"),sQuery(id+"F0.wireOp",EDGE,"E3.sketch_text.stroke-160"),sQuery(id+"F0.wireOp",EDGE,"E3.sketch_text.stroke-161"),sQuery(id+"F0.wireOp",EDGE,"E3.sketch_text.stroke-162"),sQuery(id+"F0.wireOp",EDGE,"E3.sketch_text.stroke-163"),sQuery(id+"F0.wireOp",EDGE,"E3.sketch_text.stroke-164"),sQuery(id+"F0.wireOp",EDGE,"E3.sketch_text.stroke-165"),sQuery(id+"F0.wireOp",EDGE,"E3.sketch_text.stroke-166"),sQuery(id+"F0.wireOp",EDGE,"E3.sketch_text.stroke-167"),sQuery(id+"F0.wireOp",EDGE,"E3.sketch_text.stroke-168"),sQuery(id+"F0.wireOp",EDGE,"E3.sketch_text.stroke-169"),sQuery(id+"F0.wireOp",EDGE,"E3.sketch_text.stroke-170"),sQuery(id+"F0.wireOp",EDGE,"E3.sketch_text.stroke-171"),sQuery(id+"F0.wireOp",EDGE,"E3.sketch_text.stroke-172"),sQuery(id+"F0.wireOp",EDGE,"E3.sketch_text.stroke-173"),sQuery(id+"F0.wireOp",EDGE,"E3.sketch_text.stroke-174"),sQuery(id+"F0.wireOp",EDGE,"E3.sketch_text.stroke-175"),sQuery(id+"F0.wireOp",EDGE,"E3.sketch_text.stroke-176"),sQuery(id+"F0.wireOp",EDGE,"E3.sketch_text.stroke-177"),sQuery(id+"F0.wireOp",EDGE,"E3.sketch_text.stroke-178"),sQuery(id+"F0.wireOp",EDGE,"E3.sketch_text.stroke-179"),sQuery(id+"F0.wireOp",EDGE,"E3.sketch_text.stroke-180"),sQuery(id+"F0.wireOp",EDGE,"E3.sketch_text.stroke-181"),sQuery(id+"F0.wireOp",EDGE,"E3.sketch_text.stroke-182"),sQuery(id+"F0.wireOp",EDGE,"E3.sketch_text.stroke-183"),sQuery(id+"F0.wireOp",EDGE,"E3.sketch_text.stroke-184"),sQuery(id+"F0.wireOp",EDGE,"E3.sketch_text.stroke-185"),sQuery(id+"F0.wireOp",EDGE,"E3.sketch_text.stroke-186"),sQuery(id+"F0.wireOp",EDGE,"E3.sketch_text.stroke-187"),sQuery(id+"F0.wireOp",EDGE,"E3.sketch_text.stroke-188"),sQuery(id+"F0.wireOp",EDGE,"E3.sketch_text.stroke-189"),sQuery(id+"F0.wireOp",EDGE,"E3.sketch_text.stroke-190"),sQuery(id+"F0.wireOp",EDGE,"E3.sketch_text.stroke-191"),sQuery(id+"F0.wireOp",EDGE,"E3.sketch_text.stroke-192"),sQuery(id+"F0.wireOp",EDGE,"E3.sketch_text.stroke-193"),sQuery(id+"F0.wireOp",EDGE,"E3.sketch_text.stroke-194"),sQuery(id+"F0.wireOp",EDGE,"E3.sketch_text.stroke-195"),sQuery(id+"F0.wireOp",EDGE,"E3.sketch_text.stroke-196"),sQuery(id+"F0.wireOp",EDGE,"E3.sketch_text.stroke-197"),sQuery(id+"F0.wireOp",EDGE,"E3.sketch_text.stroke-198"),sQuery(id+"F0.wireOp",EDGE,"E3.sketch_text.stroke-199"),sQuery(id+"F0.wireOp",EDGE,"E3.sketch_text.stroke-200"),sQuery(id+"F0.wireOp",EDGE,"E3.sketch_text.stroke-201"),sQuery(id+"F0.wireOp",EDGE,"E3.sketch_text.stroke-202"),sQuery(id+"F0.wireOp",EDGE,"E3.sketch_text.stroke-203"),sQuery(id+"F0.wireOp",EDGE,"E3.sketch_text.stroke-204"),sQuery(id+"F0.wireOp",EDGE,"E3.sketch_text.stroke-205"),sQuery(id+"F0.wireOp",EDGE,"E3.sketch_text.stroke-206"),sQuery(id+"F0.wireOp",EDGE,"E3.sketch_text.stroke-207"),sQuery(id+"F0.wireOp",EDGE,"E3.sketch_text.stroke-208"),sQuery(id+"F0.wireOp",EDGE,"E3.sketch_text.stroke-209"),sQuery(id+"F0.wireOp",EDGE,"E3.sketch_text.stroke-210"),sQuery(id+"F0.wireOp",EDGE,"E3.sketch_text.stroke-211"),sQuery(id+"F0.wireOp",EDGE,"E3.sketch_text.stroke-212"),sQuery(id+"F0.wireOp",EDGE,"E3.sketch_text.stroke-213"),sQuery(id+"F0.wireOp",EDGE,"E3.sketch_text.stroke-214"),sQuery(id+"F0.wireOp",EDGE,"E3.sketch_text.stroke-215"),sQuery(id+"F0.wireOp",EDGE,"E3.sketch_text.stroke-216"),sQuery(id+"F0.wireOp",EDGE,"E3.sketch_text.stroke-217"),sQuery(id+"F0.wireOp",EDGE,"E3.sketch_text.stroke-218"),sQuery(id+"F0.wireOp",EDGE,"E3.sketch_text.stroke-219"),sQuery(id+"F0.wireOp",EDGE,"E3.sketch_text.stroke-220"),sQuery(id+"F0.wireOp",EDGE,"E3.sketch_text.stroke-221"),sQuery(id+"F0.wireOp",EDGE,"E3.sketch_text.stroke-222"),sQuery(id+"F0.wireOp",EDGE,"E3.sketch_text.stroke-223"),sQuery(id+"F0.wireOp",EDGE,"E3.sketch_text.stroke-224"),sQuery(id+"F0.wireOp",EDGE,"E3.sketch_text.stroke-225"),sQuery(id+"F0.wireOp",EDGE,"E3.sketch_text.stroke-226"),sQuery(id+"F0.wireOp",EDGE,"E3.sketch_text.stroke-227"),sQuery(id+"F0.wireOp",EDGE,"E3.sketch_text.stroke-228"),sQuery(id+"F0.wireOp",EDGE,"E3.sketch_text.stroke-229"),sQuery(id+"F0.wireOp",EDGE,"E3.sketch_text.stroke-230"),sQuery(id+"F0.wireOp",EDGE,"E3.sketch_text.stroke-231"),sQuery(id+"F0.wireOp",EDGE,"E3.sketch_text.stroke-232"),sQuery(id+"F0.wireOp",EDGE,"E3.sketch_text.stroke-233"),sQuery(id+"F0.wireOp",EDGE,"E3.sketch_text.stroke-234"),sQuery(id+"F0.wireOp",EDGE,"E3.sketch_text.stroke-235"),sQuery(id+"F0.wireOp",EDGE,"E3.sketch_text.stroke-236"),sQuery(id+"F0.wireOp",EDGE,"E3.sketch_text.stroke-237"),sQuery(id+"F0.wireOp",EDGE,"E3.sketch_text.stroke-238"),sQuery(id+"F0.wireOp",EDGE,"E3.sketch_text.stroke-244"),sQuery(id+"F0.wireOp",EDGE,"E3.sketch_text.stroke-245"),sQuery(id+"F0.wireOp",EDGE,"E3.sketch_text.stroke-246"),sQuery(id+"F0.wireOp",EDGE,"E3.sketch_text.stroke-247"),sQuery(id+"F0.wireOp",EDGE,"E3.sketch_text.stroke-248"),sQuery(id+"F0.wireOp",EDGE,"E3.sketch_text.stroke-249"),sQuery(id+"F0.wireOp",EDGE,"E3.sketch_text.stroke-250"),sQuery(id+"F0.wireOp",EDGE,"E3.sketch_text.stroke-251"),sQuery(id+"F0.wireOp",EDGE,"E3.sketch_text.stroke-252"),sQuery(id+"F0.wireOp",EDGE,"E3.sketch_text.stroke-253"),sQuery(id+"F0.wireOp",EDGE,"E3.sketch_text.stroke-254"),sQuery(id+"F0.wireOp",EDGE,"E3.sketch_text.stroke-255"),sQuery(id+"F0.wireOp",EDGE,"E3.sketch_text.stroke-256"),sQuery(id+"F0.wireOp",EDGE,"E3.sketch_text.stroke-257"),sQuery(id+"F0.wireOp",EDGE,"E3.sketch_text.stroke-258"),sQuery(id+"F0.wireOp",EDGE,"E3.sketch_text.stroke-259"),sQuery(id+"F0.wireOp",EDGE,"E3.sketch_text.stroke-260"),sQuery(id+"F0.wireOp",EDGE,"E4.sketch_text.stroke-0"),sQuery(id+"F0.wireOp",EDGE,"E4.sketch_text.stroke-1"),sQuery(id+"F0.wireOp",EDGE,"E4.sketch_text.stroke-2"),sQuery(id+"F0.wireOp",EDGE,"E4.sketch_text.stroke-3"),sQuery(id+"F0.wireOp",EDGE,"E4.sketch_text.stroke-4"),sQuery(id+"F0.wireOp",EDGE,"E4.sketch_text.stroke-5"),sQuery(id+"F0.wireOp",EDGE,"E4.sketch_text.stroke-6"),sQuery(id+"F0.wireOp",EDGE,"E4.sketch_text.stroke-7"),sQuery(id+"F0.wireOp",EDGE,"E4.sketch_text.stroke-8"),sQuery(id+"F0.wireOp",EDGE,"E4.sketch_text.stroke-9"),sQuery(id+"F0.wireOp",EDGE,"E4.sketch_text.stroke-10"),sQuery(id+"F0.wireOp",EDGE,"E4.sketch_text.stroke-11"),sQuery(id+"F0.wireOp",EDGE,"E4.sketch_text.stroke-12"),sQuery(id+"F0.wireOp",EDGE,"E4.sketch_text.stroke-13"),sQuery(id+"F0.wireOp",EDGE,"E4.sketch_text.stroke-14"),sQuery(id+"F0.wireOp",EDGE,"E4.sketch_text.stroke-15"),sQuery(id+"F0.wireOp",EDGE,"E4.sketch_text.stroke-16"),sQuery(id+"F0.wireOp",EDGE,"E4.sketch_text.stroke-17"),sQuery(id+"F0.wireOp",EDGE,"E4.sketch_text.stroke-18"),sQuery(id+"F0.wireOp",EDGE,"E4.sketch_text.stroke-19"),sQuery(id+"F0.wireOp",EDGE,"E4.sketch_text.stroke-20"),sQuery(id+"F0.wireOp",EDGE,"E4.sketch_text.stroke-21"),sQuery(id+"F0.wireOp",EDGE,"E4.sketch_text.stroke-28"),sQuery(id+"F0.wireOp",EDGE,"E4.sketch_text.stroke-29"),sQuery(id+"F0.wireOp",EDGE,"E4.sketch_text.stroke-30"),sQuery(id+"F0.wireOp",EDGE,"E4.sketch_text.stroke-31"),sQuery(id+"F0.wireOp",EDGE,"E4.sketch_text.stroke-32"),sQuery(id+"F0.wireOp",EDGE,"E4.sketch_text.stroke-33"),sQuery(id+"F0.wireOp",EDGE,"E4.sketch_text.stroke-34"),sQuery(id+"F0.wireOp",EDGE,"E4.sketch_text.stroke-35"),sQuery(id+"F0.wireOp",EDGE,"E4.sketch_text.stroke-36"),sQuery(id+"F0.wireOp",EDGE,"E4.sketch_text.stroke-37"),sQuery(id+"F0.wireOp",EDGE,"E4.sketch_text.stroke-38"),sQuery(id+"F0.wireOp",EDGE,"E4.sketch_text.stroke-39"),sQuery(id+"F0.wireOp",EDGE,"E4.sketch_text.stroke-40"),sQuery(id+"F0.wireOp",EDGE,"E4.sketch_text.stroke-41"),sQuery(id+"F0.wireOp",EDGE,"E4.sketch_text.stroke-42"),sQuery(id+"F0.wireOp",EDGE,"E4.sketch_text.stroke-43"),sQuery(id+"F0.wireOp",EDGE,"E4.sketch_text.stroke-44"),sQuery(id+"F0.wireOp",EDGE,"E4.sketch_text.stroke-45"),sQuery(id+"F0.wireOp",EDGE,"E4.sketch_text.stroke-46"),sQuery(id+"F0.wireOp",EDGE,"E4.sketch_text.stroke-47"),sQuery(id+"F0.wireOp",EDGE,"E4.sketch_text.stroke-48"),sQuery(id+"F0.wireOp",EDGE,"E4.sketch_text.stroke-49"),sQuery(id+"F0.wireOp",EDGE,"E4.sketch_text.stroke-50"),sQuery(id+"F0.wireOp",EDGE,"E4.sketch_text.stroke-51"),sQuery(id+"F0.wireOp",EDGE,"E4.sketch_text.stroke-52"),sQuery(id+"F0.wireOp",EDGE,"E4.sketch_text.stroke-53"),sQuery(id+"F0.wireOp",EDGE,"E4.sketch_text.stroke-54"),sQuery(id+"F0.wireOp",EDGE,"E4.sketch_text.stroke-55"),sQuery(id+"F0.wireOp",EDGE,"E4.sketch_text.stroke-56"),sQuery(id+"F0.wireOp",EDGE,"E4.sketch_text.stroke-57"),sQuery(id+"F0.wireOp",EDGE,"E4.sketch_text.stroke-58"),sQuery(id+"F0.wireOp",EDGE,"E4.sketch_text.stroke-59"),sQuery(id+"F0.wireOp",EDGE,"E4.sketch_text.stroke-60"),sQuery(id+"F0.wireOp",EDGE,"E4.sketch_text.stroke-61"),sQuery(id+"F0.wireOp",EDGE,"E4.sketch_text.stroke-62"),sQuery(id+"F0.wireOp",EDGE,"E4.sketch_text.stroke-63"),sQuery(id+"F0.wireOp",EDGE,"E4.sketch_text.stroke-64"),sQuery(id+"F0.wireOp",EDGE,"E4.sketch_text.stroke-65"),sQuery(id+"F0.wireOp",EDGE,"E4.sketch_text.stroke-66"),sQuery(id+"F0.wireOp",EDGE,"E4.sketch_text.stroke-67"),sQuery(id+"F0.wireOp",EDGE,"E4.sketch_text.stroke-68"),sQuery(id+"F0.wireOp",EDGE,"E4.sketch_text.stroke-69"),sQuery(id+"F0.wireOp",EDGE,"E4.sketch_text.stroke-70"),sQuery(id+"F0.wireOp",EDGE,"E4.sketch_text.stroke-71"),sQuery(id+"F0.wireOp",EDGE,"E4.sketch_text.stroke-72"),sQuery(id+"F0.wireOp",EDGE,"E4.sketch_text.stroke-73"),sQuery(id+"F0.wireOp",EDGE,"E4.sketch_text.stroke-74"),sQuery(id+"F0.wireOp",EDGE,"E4.sketch_text.stroke-85"),sQuery(id+"F0.wireOp",EDGE,"E4.sketch_text.stroke-86"),sQuery(id+"F0.wireOp",EDGE,"E4.sketch_text.stroke-87"),sQuery(id+"F0.wireOp",EDGE,"E4.sketch_text.stroke-88"),sQuery(id+"F0.wireOp",EDGE,"E4.sketch_text.stroke-89"),sQuery(id+"F0.wireOp",EDGE,"E4.sketch_text.stroke-90"),sQuery(id+"F0.wireOp",EDGE,"E4.sketch_text.stroke-91"),sQuery(id+"F0.wireOp",EDGE,"E4.sketch_text.stroke-92"),sQuery(id+"F0.wireOp",EDGE,"E4.sketch_text.stroke-93"),sQuery(id+"F0.wireOp",EDGE,"E4.sketch_text.stroke-94"),sQuery(id+"F0.wireOp",EDGE,"E4.sketch_text.stroke-95"),sQuery(id+"F0.wireOp",EDGE,"E4.sketch_text.stroke-96"),sQuery(id+"F0.wireOp",EDGE,"E4.sketch_text.stroke-97"),sQuery(id+"F0.wireOp",EDGE,"E4.sketch_text.stroke-98"),sQuery(id+"F0.wireOp",EDGE,"E4.sketch_text.stroke-99"),sQuery(id+"F0.wireOp",EDGE,"E4.sketch_text.stroke-100"),sQuery(id+"F0.wireOp",EDGE,"E4.sketch_text.stroke-101"),sQuery(id+"F0.wireOp",EDGE,"E4.sketch_text.stroke-102"),sQuery(id+"F0.wireOp",EDGE,"E4.sketch_text.stroke-103"),sQuery(id+"F0.wireOp",EDGE,"E4.sketch_text.stroke-104"),sQuery(id+"F0.wireOp",EDGE,"E4.sketch_text.stroke-105"),sQuery(id+"F0.wireOp",EDGE,"E4.sketch_text.stroke-106"),sQuery(id+"F0.wireOp",EDGE,"E4.sketch_text.stroke-107"),sQuery(id+"F0.wireOp",EDGE,"E4.sketch_text.stroke-108"),sQuery(id+"F0.wireOp",EDGE,"E4.sketch_text.stroke-109"),sQuery(id+"F0.wireOp",EDGE,"E4.sketch_text.stroke-110"),sQuery(id+"F0.wireOp",EDGE,"E4.sketch_text.stroke-111"),sQuery(id+"F0.wireOp",EDGE,"E4.sketch_text.stroke-112"),sQuery(id+"F0.wireOp",EDGE,"E4.sketch_text.stroke-113"),sQuery(id+"F0.wireOp",EDGE,"E4.sketch_text.stroke-114"),sQuery(id+"F0.wireOp",EDGE,"E4.sketch_text.stroke-115"),sQuery(id+"F0.wireOp",EDGE,"E4.sketch_text.stroke-116"),sQuery(id+"F0.wireOp",EDGE,"E4.sketch_text.stroke-117"),sQuery(id+"F0.wireOp",EDGE,"E4.sketch_text.stroke-118"),sQuery(id+"F0.wireOp",EDGE,"E4.sketch_text.stroke-119"),sQuery(id+"F0.wireOp",EDGE,"E4.sketch_text.stroke-120"),sQuery(id+"F0.wireOp",EDGE,"E4.sketch_text.stroke-121"),sQuery(id+"F0.wireOp",EDGE,"E4.sketch_text.stroke-122"),sQuery(id+"F0.wireOp",EDGE,"E4.sketch_text.stroke-123"),sQuery(id+"F0.wireOp",EDGE,"E4.sketch_text.stroke-124"),sQuery(id+"F0.wireOp",EDGE,"E4.sketch_text.stroke-138"),sQuery(id+"F0.wireOp",EDGE,"E4.sketch_text.stroke-139"),sQuery(id+"F0.wireOp",EDGE,"E4.sketch_text.stroke-140"),sQuery(id+"F0.wireOp",EDGE,"E4.sketch_text.stroke-141"),sQuery(id+"F0.wireOp",EDGE,"E4.sketch_text.stroke-142"),sQuery(id+"F0.wireOp",EDGE,"E4.sketch_text.stroke-143"),sQuery(id+"F0.wireOp",EDGE,"E4.sketch_text.stroke-144"),sQuery(id+"F0.wireOp",EDGE,"E4.sketch_text.stroke-145"),sQuery(id+"F0.wireOp",EDGE,"E4.sketch_text.stroke-146"),sQuery(id+"F0.wireOp",EDGE,"E4.sketch_text.stroke-147"),sQuery(id+"F0.wireOp",EDGE,"E4.sketch_text.stroke-148"),sQuery(id+"F0.wireOp",EDGE,"E4.sketch_text.stroke-149"),sQuery(id+"F0.wireOp",EDGE,"E4.sketch_text.stroke-156"),sQuery(id+"F0.wireOp",EDGE,"E4.sketch_text.stroke-157"),sQuery(id+"F0.wireOp",EDGE,"E4.sketch_text.stroke-158"),sQuery(id+"F0.wireOp",EDGE,"E4.sketch_text.stroke-159"),sQuery(id+"F0.wireOp",EDGE,"E4.sketch_text.stroke-160"),sQuery(id+"F0.wireOp",EDGE,"E4.sketch_text.stroke-161"),sQuery(id+"F0.wireOp",EDGE,"E4.sketch_text.stroke-162"),sQuery(id+"F0.wireOp",EDGE,"E4.sketch_text.stroke-163"),sQuery(id+"F0.wireOp",EDGE,"E4.sketch_text.stroke-164"),sQuery(id+"F0.wireOp",EDGE,"E4.sketch_text.stroke-165"),sQuery(id+"F0.wireOp",EDGE,"E4.sketch_text.stroke-166"),sQuery(id+"F0.wireOp",EDGE,"E4.sketch_text.stroke-167"),sQuery(id+"F0.wireOp",EDGE,"E4.sketch_text.stroke-168"),sQuery(id+"F0.wireOp",EDGE,"E4.sketch_text.stroke-169"),sQuery(id+"F0.wireOp",EDGE,"E4.sketch_text.stroke-170"),sQuery(id+"F0.wireOp",EDGE,"E4.sketch_text.stroke-171"),sQuery(id+"F0.wireOp",EDGE,"E4.sketch_text.stroke-172"),sQuery(id+"F0.wireOp",EDGE,"E4.sketch_text.stroke-173"),sQuery(id+"F0.wireOp",EDGE,"E4.sketch_text.stroke-174"),sQuery(id+"F0.wireOp",EDGE,"E4.sketch_text.stroke-175"),sQuery(id+"F0.wireOp",EDGE,"E4.sketch_text.stroke-176"),sQuery(id+"F0.wireOp",EDGE,"E4.sketch_text.stroke-177"),sQuery(id+"F0.wireOp",EDGE,"E4.sketch_text.stroke-178"),sQuery(id+"F0.wireOp",EDGE,"E4.sketch_text.stroke-179"),sQuery(id+"F0.wireOp",EDGE,"E4.sketch_text.stroke-180"),sQuery(id+"F0.wireOp",EDGE,"E4.sketch_text.stroke-181"),sQuery(id+"F0.wireOp",EDGE,"E4.sketch_text.stroke-182"),sQuery(id+"F0.wireOp",EDGE,"E4.sketch_text.stroke-183"),sQuery(id+"F0.wireOp",EDGE,"E4.sketch_text.stroke-184"),sQuery(id+"F0.wireOp",EDGE,"E4.sketch_text.stroke-185"),sQuery(id+"F0.wireOp",EDGE,"E4.sketch_text.stroke-186"),sQuery(id+"F0.wireOp",EDGE,"E4.sketch_text.stroke-187"),sQuery(id+"F0.wireOp",EDGE,"E4.sketch_text.stroke-188"),sQuery(id+"F0.wireOp",EDGE,"E4.sketch_text.stroke-189"),sQuery(id+"F0.wireOp",EDGE,"E4.sketch_text.stroke-190"),sQuery(id+"F0.wireOp",EDGE,"E4.sketch_text.stroke-191"),sQuery(id+"F0.wireOp",EDGE,"E4.sketch_text.stroke-192"),sQuery(id+"F0.wireOp",EDGE,"E4.sketch_text.stroke-193"),sQuery(id+"F0.wireOp",EDGE,"E4.sketch_text.stroke-194"),sQuery(id+"F0.wireOp",EDGE,"E4.sketch_text.stroke-195"),sQuery(id+"F0.wireOp",EDGE,"E4.sketch_text.stroke-196"),sQuery(id+"F0.wireOp",EDGE,"E4.sketch_text.stroke-197"),sQuery(id+"F0.wireOp",EDGE,"E4.sketch_text.stroke-198"),sQuery(id+"F0.wireOp",EDGE,"E4.sketch_text.stroke-199"),sQuery(id+"F0.wireOp",EDGE,"E4.sketch_text.stroke-200"),sQuery(id+"F0.wireOp",EDGE,"E4.sketch_text.stroke-201"),sQuery(id+"F0.wireOp",EDGE,"E4.sketch_text.stroke-208"),sQuery(id+"F0.wireOp",EDGE,"E4.sketch_text.stroke-209"),sQuery(id+"F0.wireOp",EDGE,"E4.sketch_text.stroke-210"),sQuery(id+"F0.wireOp",EDGE,"E4.sketch_text.stroke-211"),sQuery(id+"F0.wireOp",EDGE,"E4.sketch_text.stroke-212"),sQuery(id+"F0.wireOp",EDGE,"E4.sketch_text.stroke-213"),sQuery(id+"F0.wireOp",EDGE,"E4.sketch_text.stroke-214"),sQuery(id+"F0.wireOp",EDGE,"E4.sketch_text.stroke-215"),sQuery(id+"F0.wireOp",EDGE,"E4.sketch_text.stroke-216"),sQuery(id+"F0.wireOp",EDGE,"E4.sketch_text.stroke-217"),sQuery(id+"F0.wireOp",EDGE,"E4.sketch_text.stroke-218"),sQuery(id+"F0.wireOp",EDGE,"E4.sketch_text.stroke-219"),sQuery(id+"F0.wireOp",EDGE,"E4.sketch_text.stroke-220"),sQuery(id+"F0.wireOp",EDGE,"E4.sketch_text.stroke-221"),sQuery(id+"F0.wireOp",EDGE,"E4.sketch_text.stroke-222"),sQuery(id+"F0.wireOp",EDGE,"E4.sketch_text.stroke-223"),sQuery(id+"F0.wireOp",EDGE,"E4.sketch_text.stroke-224"),sQuery(id+"F0.wireOp",EDGE,"E4.sketch_text.stroke-225"),sQuery(id+"F0.wireOp",EDGE,"E4.sketch_text.stroke-226"),sQuery(id+"F0.wireOp",EDGE,"E4.sketch_text.stroke-227"),sQuery(id+"F0.wireOp",EDGE,"E4.sketch_text.stroke-228"),sQuery(id+"F0.wireOp",EDGE,"E4.sketch_text.stroke-229"),sQuery(id+"F0.wireOp",EDGE,"E4.sketch_text.stroke-230"),sQuery(id+"F0.wireOp",EDGE,"E4.sketch_text.stroke-231"),sQuery(id+"F0.wireOp",EDGE,"E4.sketch_text.stroke-232"),sQuery(id+"F0.wireOp",EDGE,"E4.sketch_text.stroke-233"),sQuery(id+"F0.wireOp",EDGE,"E4.sketch_text.stroke-234"),sQuery(id+"F0.wireOp",EDGE,"E4.sketch_text.stroke-235"),sQuery(id+"F0.wireOp",EDGE,"E4.sketch_text.stroke-236"),sQuery(id+"F0.wireOp",EDGE,"E4.sketch_text.stroke-237"),sQuery(id+"F0.wireOp",EDGE,"E4.sketch_text.stroke-238"),sQuery(id+"F0.wireOp",EDGE,"E4.sketch_text.stroke-239"),sQuery(id+"F0.wireOp",EDGE,"E4.sketch_text.stroke-240"),sQuery(id+"F0.wireOp",EDGE,"E4.sketch_text.stroke-241"),sQuery(id+"F0.wireOp",EDGE,"E4.sketch_text.stroke-242"),sQuery(id+"F0.wireOp",EDGE,"E4.sketch_text.stroke-243"),sQuery(id+"F0.wireOp",EDGE,"E4.sketch_text.stroke-244"),sQuery(id+"F0.wireOp",EDGE,"E4.sketch_text.stroke-245"),sQuery(id+"F0.wireOp",EDGE,"E4.sketch_text.stroke-246"),sQuery(id+"F0.wireOp",EDGE,"E4.sketch_text.stroke-247"),sQuery(id+"F0.wireOp",EDGE,"E4.sketch_text.stroke-248"),sQuery(id+"F0.wireOp",EDGE,"E4.sketch_text.stroke-249"),sQuery(id+"F0.wireOp",EDGE,"E4.sketch_text.stroke-250"),sQuery(id+"F0.wireOp",EDGE,"E4.sketch_text.stroke-251"),sQuery(id+"F0.wireOp",EDGE,"E4.sketch_text.stroke-252"),sQuery(id+"F0.wireOp",EDGE,"E4.sketch_text.stroke-253"),sQuery(id+"F0.wireOp",EDGE,"E4.sketch_text.stroke-254"),sQuery(id+"F0.wireOp",EDGE,"E4.sketch_text.stroke-255"),sQuery(id+"F0.wireOp",EDGE,"E4.sketch_text.stroke-256"),sQuery(id+"F0.wireOp",EDGE,"E4.sketch_text.stroke-257"),sQuery(id+"F0.wireOp",EDGE,"E4.sketch_text.stroke-258"),sQuery(id+"F0.wireOp",EDGE,"E4.sketch_text.stroke-259"),sQuery(id+"F0.wireOp",EDGE,"E4.sketch_text.stroke-260"),sQuery(id+"F0.wireOp",EDGE,"E4.sketch_text.stroke-261"),sQuery(id+"F0.wireOp",EDGE,"E4.sketch_text.stroke-262"),sQuery(id+"F0.wireOp",EDGE,"E4.sketch_text.stroke-263"),sQuery(id+"F0.wireOp",EDGE,"E4.sketch_text.stroke-264"),sQuery(id+"F0.wireOp",EDGE,"E4.sketch_text.stroke-265"),sQuery(id+"F0.wireOp",EDGE,"E4.sketch_text.stroke-266"),sQuery(id+"F0.wireOp",EDGE,"E4.sketch_text.stroke-267"),sQuery(id+"F0.wireOp",EDGE,"E4.sketch_text.stroke-268"),sQuery(id+"F0.wireOp",EDGE,"E4.sketch_text.stroke-269"),sQuery(id+"F0.wireOp",EDGE,"E4.sketch_text.stroke-270"),sQuery(id+"F0.wireOp",EDGE,"E4.sketch_text.stroke-271"),sQuery(id+"F0.wireOp",EDGE,"E4.sketch_text.stroke-272"),sQuery(id+"F0.wireOp",EDGE,"E4.sketch_text.stroke-273"),sQuery(id+"F0.wireOp",EDGE,"E4.sketch_text.stroke-274"),sQuery(id+"F0.wireOp",EDGE,"E4.sketch_text.stroke-275"),sQuery(id+"F0.wireOp",EDGE,"E4.sketch_text.stroke-276"),sQuery(id+"F0.wireOp",EDGE,"E4.sketch_text.stroke-283"),sQuery(id+"F0.wireOp",EDGE,"E4.sketch_text.stroke-284"),sQuery(id+"F0.wireOp",EDGE,"E4.sketch_text.stroke-285"),sQuery(id+"F0.wireOp",EDGE,"E4.sketch_text.stroke-286"),sQuery(id+"F0.wireOp",EDGE,"E4.sketch_text.stroke-287"),sQuery(id+"F0.wireOp",EDGE,"E4.sketch_text.stroke-288"),sQuery(id+"F0.wireOp",EDGE,"E4.sketch_text.stroke-289"),sQuery(id+"F0.wireOp",EDGE,"E4.sketch_text.stroke-290"),sQuery(id+"F0.wireOp",EDGE,"E4.sketch_text.stroke-291"),sQuery(id+"F0.wireOp",EDGE,"E4.sketch_text.stroke-292"),sQuery(id+"F0.wireOp",EDGE,"E4.sketch_text.stroke-293"),sQuery(id+"F0.wireOp",EDGE,"E4.sketch_text.stroke-294"),sQuery(id+"F0.wireOp",EDGE,"E4.sketch_text.stroke-295"),sQuery(id+"F0.wireOp",EDGE,"E4.sketch_text.stroke-296"),sQuery(id+"F0.wireOp",EDGE,"E4.sketch_text.stroke-297"),sQuery(id+"F0.wireOp",EDGE,"E4.sketch_text.stroke-298"),sQuery(id+"F0.wireOp",EDGE,"E4.sketch_text.stroke-299"),sQuery(id+"F0.wireOp",EDGE,"E4.sketch_text.stroke-300"),sQuery(id+"F0.wireOp",EDGE,"E4.sketch_text.stroke-301"),sQuery(id+"F0.wireOp",EDGE,"E4.sketch_text.stroke-302"),sQuery(id+"F0.wireOp",EDGE,"E4.sketch_text.stroke-303"),sQuery(id+"F0.wireOp",EDGE,"E4.sketch_text.stroke-304"),sQuery(id+"F0.wireOp",EDGE,"E4.sketch_text.stroke-305"),sQuery(id+"F0.wireOp",EDGE,"E4.sketch_text.stroke-306"),sQuery(id+"F0.wireOp",EDGE,"E4.sketch_text.stroke-307"),sQuery(id+"F0.wireOp",EDGE,"E4.sketch_text.stroke-308"),sQuery(id+"F0.wireOp",EDGE,"E4.sketch_text.stroke-309"),sQuery(id+"F0.wireOp",EDGE,"E4.sketch_text.stroke-310"),sQuery(id+"F0.wireOp",EDGE,"E4.sketch_text.stroke-321"),sQuery(id+"F0.wireOp",EDGE,"E4.sketch_text.stroke-322"),sQuery(id+"F0.wireOp",EDGE,"E4.sketch_text.stroke-323"),sQuery(id+"F0.wireOp",EDGE,"E4.sketch_text.stroke-324"),sQuery(id+"F0.wireOp",EDGE,"E4.sketch_text.stroke-325"),sQuery(id+"F0.wireOp",EDGE,"E4.sketch_text.stroke-326"),sQuery(id+"F0.wireOp",EDGE,"E4.sketch_text.stroke-327"),sQuery(id+"F0.wireOp",EDGE,"E4.sketch_text.stroke-328"),sQuery(id+"F0.wireOp",EDGE,"E4.sketch_text.stroke-329"),sQuery(id+"F0.wireOp",EDGE,"E4.sketch_text.stroke-330"),sQuery(id+"F0.wireOp",EDGE,"E4.sketch_text.stroke-331"),sQuery(id+"F0.wireOp",EDGE,"E4.sketch_text.stroke-332"),sQuery(id+"F0.wireOp",EDGE,"E4.sketch_text.stroke-333"),sQuery(id+"F0.wireOp",EDGE,"E4.sketch_text.stroke-334"),sQuery(id+"F0.wireOp",EDGE,"E4.sketch_text.stroke-335"),sQuery(id+"F0.wireOp",EDGE,"E4.sketch_text.stroke-336"),sQuery(id+"F0.wireOp",EDGE,"E4.sketch_text.stroke-337"),sQuery(id+"F0.wireOp",EDGE,"E4.sketch_text.stroke-338"),sQuery(id+"F0.wireOp",EDGE,"E4.sketch_text.stroke-339"),sQuery(id+"F0.wireOp",EDGE,"E4.sketch_text.stroke-340"),sQuery(id+"F0.wireOp",EDGE,"E4.sketch_text.stroke-341"),sQuery(id+"F0.wireOp",EDGE,"E4.sketch_text.stroke-342"),sQuery(id+"F0.wireOp",EDGE,"E4.sketch_text.stroke-343"),sQuery(id+"F0.wireOp",EDGE,"E4.sketch_text.stroke-344"),sQuery(id+"F0.wireOp",EDGE,"E4.sketch_text.stroke-345"),sQuery(id+"F0.wireOp",EDGE,"E4.sketch_text.stroke-346"),sQuery(id+"F0.wireOp",EDGE,"E4.sketch_text.stroke-347"),sQuery(id+"F0.wireOp",EDGE,"E4.sketch_text.stroke-348"),sQuery(id+"F0.wireOp",EDGE,"E4.sketch_text.stroke-359"),sQuery(id+"F0.wireOp",EDGE,"E4.sketch_text.stroke-360"),sQuery(id+"F0.wireOp",EDGE,"E4.sketch_text.stroke-361"),sQuery(id+"F0.wireOp",EDGE,"E4.sketch_text.stroke-362"),sQuery(id+"F0.wireOp",EDGE,"E4.sketch_text.stroke-363"),sQuery(id+"F0.wireOp",EDGE,"E4.sketch_text.stroke-364"),sQuery(id+"F0.wireOp",EDGE,"E4.sketch_text.stroke-365"),sQuery(id+"F0.wireOp",EDGE,"E4.sketch_text.stroke-366"),sQuery(id+"F0.wireOp",EDGE,"E4.sketch_text.stroke-367"),sQuery(id+"F0.wireOp",EDGE,"E4.sketch_text.stroke-368"),sQuery(id+"F0.wireOp",EDGE,"E4.sketch_text.stroke-369"),sQuery(id+"F0.wireOp",EDGE,"E4.sketch_text.stroke-370"),sQuery(id+"F0.wireOp",EDGE,"E4.sketch_text.stroke-371"),sQuery(id+"F0.wireOp",EDGE,"E4.sketch_text.stroke-372"),sQuery(id+"F0.wireOp",EDGE,"E4.sketch_text.stroke-373"),sQuery(id+"F0.wireOp",EDGE,"E4.sketch_text.stroke-374"),sQuery(id+"F0.wireOp",EDGE,"E4.sketch_text.stroke-375"),sQuery(id+"F0.wireOp",EDGE,"E4.sketch_text.stroke-376"),sQuery(id+"F0.wireOp",EDGE,"E4.sketch_text.stroke-377"),sQuery(id+"F0.wireOp",EDGE,"E4.sketch_text.stroke-378"),sQuery(id+"F0.wireOp",EDGE,"E4.sketch_text.stroke-379"),sQuery(id+"F0.wireOp",EDGE,"E4.sketch_text.stroke-380"),sQuery(id+"F0.wireOp",EDGE,"E4.sketch_text.stroke-381"),sQuery(id+"F0.wireOp",EDGE,"E4.sketch_text.stroke-382"),sQuery(id+"F0.wireOp",EDGE,"E4.sketch_text.stroke-383"),sQuery(id+"F0.wireOp",EDGE,"E4.sketch_text.stroke-384"),sQuery(id+"F0.wireOp",EDGE,"E4.sketch_text.stroke-385"),sQuery(id+"F0.wireOp",EDGE,"E4.sketch_text.stroke-386"),sQuery(id+"F0.wireOp",EDGE,"E4.sketch_text.stroke-387"),sQuery(id+"F0.wireOp",EDGE,"E4.sketch_text.stroke-388"),sQuery(id+"F0.wireOp",EDGE,"E4.sketch_text.stroke-389"),sQuery(id+"F0.wireOp",EDGE,"E4.sketch_text.stroke-390"),sQuery(id+"F0.wireOp",EDGE,"E4.sketch_text.stroke-391"),sQuery(id+"F0.wireOp",EDGE,"E4.sketch_text.stroke-392")])],"isStart":true})],"blendedInto":[makeQuery(id+"F6.opExtrude","CAP_FACE",FACE,{"disambiguationData":[OSD([sQuery(id+"F0.wireOp",EDGE,"E0.bottom"),subQ1,subQ0,sQuery(id+"F0.wireOp",EDGE,"E0.right"),sQuery(id+"F0.wireOp",EDGE,"E3.sketch_text.stroke-0"),sQuery(id+"F0.wireOp",EDGE,"E3.sketch_text.stroke-1"),sQuery(id+"F0.wireOp",EDGE,"E3.sketch_text.stroke-2"),sQuery(id+"F0.wireOp",EDGE,"E3.sketch_text.stroke-3"),sQuery(id+"F0.wireOp",EDGE,"E3.sketch_text.stroke-4"),sQuery(id+"F0.wireOp",EDGE,"E3.sketch_text.stroke-5"),sQuery(id+"F0.wireOp",EDGE,"E3.sketch_text.stroke-6"),sQuery(id+"F0.wireOp",EDGE,"E3.sketch_text.stroke-7"),sQuery(id+"F0.wireOp",EDGE,"E3.sketch_text.stroke-8"),sQuery(id+"F0.wireOp",EDGE,"E3.sketch_text.stroke-9"),sQuery(id+"F0.wireOp",EDGE,"E3.sketch_text.stroke-10"),sQuery(id+"F0.wireOp",EDGE,"E3.sketch_text.stroke-11"),sQuery(id+"F0.wireOp",EDGE,"E3.sketch_text.stroke-12"),sQuery(id+"F0.wireOp",EDGE,"E3.sketch_text.stroke-13"),sQuery(id+"F0.wireOp",EDGE,"E3.sketch_text.stroke-14"),sQuery(id+"F0.wireOp",EDGE,"E3.sketch_text.stroke-15"),sQuery(id+"F0.wireOp",EDGE,"E3.sketch_text.stroke-16"),sQuery(id+"F0.wireOp",EDGE,"E3.sketch_text.stroke-17"),sQuery(id+"F0.wireOp",EDGE,"E3.sketch_text.stroke-18"),sQuery(id+"F0.wireOp",EDGE,"E3.sketch_text.stroke-19"),sQuery(id+"F0.wireOp",EDGE,"E3.sketch_text.stroke-20"),sQuery(id+"F0.wireOp",EDGE,"E3.sketch_text.stroke-21"),sQuery(id+"F0.wireOp",EDGE,"E3.sketch_text.stroke-22"),sQuery(id+"F0.wireOp",EDGE,"E3.sketch_text.stroke-23"),sQuery(id+"F0.wireOp",EDGE,"E3.sketch_text.stroke-24"),sQuery(id+"F0.wireOp",EDGE,"E3.sketch_text.stroke-25"),sQuery(id+"F0.wireOp",EDGE,"E3.sketch_text.stroke-26"),sQuery(id+"F0.wireOp",EDGE,"E3.sketch_text.stroke-27"),sQuery(id+"F0.wireOp",EDGE,"E3.sketch_text.stroke-28"),sQuery(id+"F0.wireOp",EDGE,"E3.sketch_text.stroke-29"),sQuery(id+"F0.wireOp",EDGE,"E3.sketch_text.stroke-30"),sQuery(id+"F0.wireOp",EDGE,"E3.sketch_text.stroke-31"),sQuery(id+"F0.wireOp",EDGE,"E3.sketch_text.stroke-32"),sQuery(id+"F0.wireOp",EDGE,"E3.sketch_text.stroke-33"),sQuery(id+"F0.wireOp",EDGE,"E3.sketch_text.stroke-34"),sQuery(id+"F0.wireOp",EDGE,"E3.sketch_text.stroke-35"),sQuery(id+"F0.wireOp",EDGE,"E3.sketch_text.stroke-36"),sQuery(id+"F0.wireOp",EDGE,"E3.sketch_text.stroke-37"),sQuery(id+"F0.wireOp",EDGE,"E3.sketch_text.stroke-38"),sQuery(id+"F0.wireOp",EDGE,"E3.sketch_text.stroke-39"),sQuery(id+"F0.wireOp",EDGE,"E3.sketch_text.stroke-40"),sQuery(id+"F0.wireOp",EDGE,"E3.sketch_text.stroke-41"),sQuery(id+"F0.wireOp",EDGE,"E3.sketch_text.stroke-42"),sQuery(id+"F0.wireOp",EDGE,"E3.sketch_text.stroke-43"),sQuery(id+"F0.wireOp",EDGE,"E3.sketch_text.stroke-44"),sQuery(id+"F0.wireOp",EDGE,"E3.sketch_text.stroke-45"),sQuery(id+"F0.wireOp",EDGE,"E3.sketch_text.stroke-46"),sQuery(id+"F0.wireOp",EDGE,"E3.sketch_text.stroke-47"),sQuery(id+"F0.wireOp",EDGE,"E3.sketch_text.stroke-48"),sQuery(id+"F0.wireOp",EDGE,"E3.sketch_text.stroke-49"),sQuery(id+"F0.wireOp",EDGE,"E3.sketch_text.stroke-50"),sQuery(id+"F0.wireOp",EDGE,"E3.sketch_text.stroke-51"),sQuery(id+"F0.wireOp",EDGE,"E3.sketch_text.stroke-52"),sQuery(id+"F0.wireOp",EDGE,"E3.sketch_text.stroke-53"),sQuery(id+"F0.wireOp",EDGE,"E3.sketch_text.stroke-54"),sQuery(id+"F0.wireOp",EDGE,"E3.sketch_text.stroke-55"),sQuery(id+"F0.wireOp",EDGE,"E3.sketch_text.stroke-56"),sQuery(id+"F0.wireOp",EDGE,"E3.sketch_text.stroke-57"),sQuery(id+"F0.wireOp",EDGE,"E3.sketch_text.stroke-58"),sQuery(id+"F0.wireOp",EDGE,"E3.sketch_text.stroke-59"),sQuery(id+"F0.wireOp",EDGE,"E3.sketch_text.stroke-60"),sQuery(id+"F0.wireOp",EDGE,"E3.sketch_text.stroke-61"),sQuery(id+"F0.wireOp",EDGE,"E3.sketch_text.stroke-62"),sQuery(id+"F0.wireOp",EDGE,"E3.sketch_text.stroke-63"),sQuery(id+"F0.wireOp",EDGE,"E3.sketch_text.stroke-64"),sQuery(id+"F0.wireOp",EDGE,"E3.sketch_text.stroke-65"),sQuery(id+"F0.wireOp",EDGE,"E3.sketch_text.stroke-66"),sQuery(id+"F0.wireOp",EDGE,"E3.sketch_text.stroke-67"),sQuery(id+"F0.wireOp",EDGE,"E3.sketch_text.stroke-68"),sQuery(id+"F0.wireOp",EDGE,"E3.sketch_text.stroke-69"),sQuery(id+"F0.wireOp",EDGE,"E3.sketch_text.stroke-70"),sQuery(id+"F0.wireOp",EDGE,"E3.sketch_text.stroke-71"),sQuery(id+"F0.wireOp",EDGE,"E3.sketch_text.stroke-72"),sQuery(id+"F0.wireOp",EDGE,"E3.sketch_text.stroke-73"),sQuery(id+"F0.wireOp",EDGE,"E3.sketch_text.stroke-74"),sQuery(id+"F0.wireOp",EDGE,"E3.sketch_text.stroke-88"),sQuery(id+"F0.wireOp",EDGE,"E3.sketch_text.stroke-89"),sQuery(id+"F0.wireOp",EDGE,"E3.sketch_text.stroke-90"),sQuery(id+"F0.wireOp",EDGE,"E3.sketch_text.stroke-91"),sQuery(id+"F0.wireOp",EDGE,"E3.sketch_text.stroke-92"),sQuery(id+"F0.wireOp",EDGE,"E3.sketch_text.stroke-93"),sQuery(id+"F0.wireOp",EDGE,"E3.sketch_text.stroke-94"),sQuery(id+"F0.wireOp",EDGE,"E3.sketch_text.stroke-95"),sQuery(id+"F0.wireOp",EDGE,"E3.sketch_text.stroke-96"),sQuery(id+"F0.wireOp",EDGE,"E3.sketch_text.stroke-97"),sQuery(id+"F0.wireOp",EDGE,"E3.sketch_text.stroke-98"),sQuery(id+"F0.wireOp",EDGE,"E3.sketch_text.stroke-99"),sQuery(id+"F0.wireOp",EDGE,"E3.sketch_text.stroke-106"),sQuery(id+"F0.wireOp",EDGE,"E3.sketch_text.stroke-107"),sQuery(id+"F0.wireOp",EDGE,"E3.sketch_text.stroke-108"),sQuery(id+"F0.wireOp",EDGE,"E3.sketch_text.stroke-109"),sQuery(id+"F0.wireOp",EDGE,"E3.sketch_text.stroke-110"),sQuery(id+"F0.wireOp",EDGE,"E3.sketch_text.stroke-111"),sQuery(id+"F0.wireOp",EDGE,"E3.sketch_text.stroke-112"),sQuery(id+"F0.wireOp",EDGE,"E3.sketch_text.stroke-113"),sQuery(id+"F0.wireOp",EDGE,"E3.sketch_text.stroke-114"),sQuery(id+"F0.wireOp",EDGE,"E3.sketch_text.stroke-115"),sQuery(id+"F0.wireOp",EDGE,"E3.sketch_text.stroke-116"),sQuery(id+"F0.wireOp",EDGE,"E3.sketch_text.stroke-117"),sQuery(id+"F0.wireOp",EDGE,"E3.sketch_text.stroke-118"),sQuery(id+"F0.wireOp",EDGE,"E3.sketch_text.stroke-119"),sQuery(id+"F0.wireOp",EDGE,"E3.sketch_text.stroke-120"),sQuery(id+"F0.wireOp",EDGE,"E3.sketch_text.stroke-121"),sQuery(id+"F0.wireOp",EDGE,"E3.sketch_text.stroke-122"),sQuery(id+"F0.wireOp",EDGE,"E3.sketch_text.stroke-123"),sQuery(id+"F0.wireOp",EDGE,"E3.sketch_text.stroke-124"),sQuery(id+"F0.wireOp",EDGE,"E3.sketch_text.stroke-125"),sQuery(id+"F0.wireOp",EDGE,"E3.sketch_text.stroke-126"),sQuery(id+"F0.wireOp",EDGE,"E3.sketch_text.stroke-127"),sQuery(id+"F0.wireOp",EDGE,"E3.sketch_text.stroke-128"),sQuery(id+"F0.wireOp",EDGE,"E3.sketch_text.stroke-129"),sQuery(id+"F0.wireOp",EDGE,"E3.sketch_text.stroke-130"),sQuery(id+"F0.wireOp",EDGE,"E3.sketch_text.stroke-131"),sQuery(id+"F0.wireOp",EDGE,"E3.sketch_text.stroke-132"),sQuery(id+"F0.wireOp",EDGE,"E3.sketch_text.stroke-133"),sQuery(id+"F0.wireOp",EDGE,"E3.sketch_text.stroke-134"),sQuery(id+"F0.wireOp",EDGE,"E3.sketch_text.stroke-135"),sQuery(id+"F0.wireOp",EDGE,"E3.sketch_text.stroke-136"),sQuery(id+"F0.wireOp",EDGE,"E3.sketch_text.stroke-137"),sQuery(id+"F0.wireOp",EDGE,"E3.sketch_text.stroke-138"),sQuery(id+"F0.wireOp",EDGE,"E3.sketch_text.stroke-139"),sQuery(id+"F0.wireOp",EDGE,"E3.sketch_text.stroke-140"),sQuery(id+"F0.wireOp",EDGE,"E3.sketch_text.stroke-141"),sQuery(id+"F0.wireOp",EDGE,"E3.sketch_text.stroke-142"),sQuery(id+"F0.wireOp",EDGE,"E3.sketch_text.stroke-143"),sQuery(id+"F0.wireOp",EDGE,"E3.sketch_text.stroke-144"),sQuery(id+"F0.wireOp",EDGE,"E3.sketch_text.stroke-145"),sQuery(id+"F0.wireOp",EDGE,"E3.sketch_text.stroke-146"),sQuery(id+"F0.wireOp",EDGE,"E3.sketch_text.stroke-147"),sQuery(id+"F0.wireOp",EDGE,"E3.sketch_text.stroke-155"),sQuery(id+"F0.wireOp",EDGE,"E3.sketch_text.stroke-156"),sQuery(id+"F0.wireOp",EDGE,"E3.sketch_text.stroke-157"),sQuery(id+"F0.wireOp",EDGE,"E3.sketch_text.stroke-158"),sQuery(id+"F0.wireOp",EDGE,"E3.sketch_text.stroke-159"),sQuery(id+"F0.wireOp",EDGE,"E3.sketch_text.stroke-160"),sQuery(id+"F0.wireOp",EDGE,"E3.sketch_text.stroke-161"),sQuery(id+"F0.wireOp",EDGE,"E3.sketch_text.stroke-162"),sQuery(id+"F0.wireOp",EDGE,"E3.sketch_text.stroke-163"),sQuery(id+"F0.wireOp",EDGE,"E3.sketch_text.stroke-164"),sQuery(id+"F0.wireOp",EDGE,"E3.sketch_text.stroke-165"),sQuery(id+"F0.wireOp",EDGE,"E3.sketch_text.stroke-166"),sQuery(id+"F0.wireOp",EDGE,"E3.sketch_text.stroke-167"),sQuery(id+"F0.wireOp",EDGE,"E3.sketch_text.stroke-168"),sQuery(id+"F0.wireOp",EDGE,"E3.sketch_text.stroke-169"),sQuery(id+"F0.wireOp",EDGE,"E3.sketch_text.stroke-170"),sQuery(id+"F0.wireOp",EDGE,"E3.sketch_text.stroke-171"),sQuery(id+"F0.wireOp",EDGE,"E3.sketch_text.stroke-172"),sQuery(id+"F0.wireOp",EDGE,"E3.sketch_text.stroke-173"),sQuery(id+"F0.wireOp",EDGE,"E3.sketch_text.stroke-174"),sQuery(id+"F0.wireOp",EDGE,"E3.sketch_text.stroke-175"),sQuery(id+"F0.wireOp",EDGE,"E3.sketch_text.stroke-176"),sQuery(id+"F0.wireOp",EDGE,"E3.sketch_text.stroke-177"),sQuery(id+"F0.wireOp",EDGE,"E3.sketch_text.stroke-178"),sQuery(id+"F0.wireOp",EDGE,"E3.sketch_text.stroke-179"),sQuery(id+"F0.wireOp",EDGE,"E3.sketch_text.stroke-180"),sQuery(id+"F0.wireOp",EDGE,"E3.sketch_text.stroke-181"),sQuery(id+"F0.wireOp",EDGE,"E3.sketch_text.stroke-182"),sQuery(id+"F0.wireOp",EDGE,"E3.sketch_text.stroke-183"),sQuery(id+"F0.wireOp",EDGE,"E3.sketch_text.stroke-184"),sQuery(id+"F0.wireOp",EDGE,"E3.sketch_text.stroke-185"),sQuery(id+"F0.wireOp",EDGE,"E3.sketch_text.stroke-186"),sQuery(id+"F0.wireOp",EDGE,"E3.sketch_text.stroke-187"),sQuery(id+"F0.wireOp",EDGE,"E3.sketch_text.stroke-188"),sQuery(id+"F0.wireOp",EDGE,"E3.sketch_text.stroke-189"),sQuery(id+"F0.wireOp",EDGE,"E3.sketch_text.stroke-190"),sQuery(id+"F0.wireOp",EDGE,"E3.sketch_text.stroke-191"),sQuery(id+"F0.wireOp",EDGE,"E3.sketch_text.stroke-192"),sQuery(id+"F0.wireOp",EDGE,"E3.sketch_text.stroke-193"),sQuery(id+"F0.wireOp",EDGE,"E3.sketch_text.stroke-194"),sQuery(id+"F0.wireOp",EDGE,"E3.sketch_text.stroke-195"),sQuery(id+"F0.wireOp",EDGE,"E3.sketch_text.stroke-196"),sQuery(id+"F0.wireOp",EDGE,"E3.sketch_text.stroke-197"),sQuery(id+"F0.wireOp",EDGE,"E3.sketch_text.stroke-198"),sQuery(id+"F0.wireOp",EDGE,"E3.sketch_text.stroke-199"),sQuery(id+"F0.wireOp",EDGE,"E3.sketch_text.stroke-200"),sQuery(id+"F0.wireOp",EDGE,"E3.sketch_text.stroke-201"),sQuery(id+"F0.wireOp",EDGE,"E3.sketch_text.stroke-202"),sQuery(id+"F0.wireOp",EDGE,"E3.sketch_text.stroke-203"),sQuery(id+"F0.wireOp",EDGE,"E3.sketch_text.stroke-204"),sQuery(id+"F0.wireOp",EDGE,"E3.sketch_text.stroke-205"),sQuery(id+"F0.wireOp",EDGE,"E3.sketch_text.stroke-206"),sQuery(id+"F0.wireOp",EDGE,"E3.sketch_text.stroke-207"),sQuery(id+"F0.wireOp",EDGE,"E3.sketch_text.stroke-208"),sQuery(id+"F0.wireOp",EDGE,"E3.sketch_text.stroke-209"),sQuery(id+"F0.wireOp",EDGE,"E3.sketch_text.stroke-210"),sQuery(id+"F0.wireOp",EDGE,"E3.sketch_text.stroke-211"),sQuery(id+"F0.wireOp",EDGE,"E3.sketch_text.stroke-212"),sQuery(id+"F0.wireOp",EDGE,"E3.sketch_text.stroke-213"),sQuery(id+"F0.wireOp",EDGE,"E3.sketch_text.stroke-214"),sQuery(id+"F0.wireOp",EDGE,"E3.sketch_text.stroke-215"),sQuery(id+"F0.wireOp",EDGE,"E3.sketch_text.stroke-216"),sQuery(id+"F0.wireOp",EDGE,"E3.sketch_text.stroke-217"),sQuery(id+"F0.wireOp",EDGE,"E3.sketch_text.stroke-218"),sQuery(id+"F0.wireOp",EDGE,"E3.sketch_text.stroke-219"),sQuery(id+"F0.wireOp",EDGE,"E3.sketch_text.stroke-220"),sQuery(id+"F0.wireOp",EDGE,"E3.sketch_text.stroke-221"),sQuery(id+"F0.wireOp",EDGE,"E3.sketch_text.stroke-222"),sQuery(id+"F0.wireOp",EDGE,"E3.sketch_text.stroke-223"),sQuery(id+"F0.wireOp",EDGE,"E3.sketch_text.stroke-224"),sQuery(id+"F0.wireOp",EDGE,"E3.sketch_text.stroke-225"),sQuery(id+"F0.wireOp",EDGE,"E3.sketch_text.stroke-226"),sQuery(id+"F0.wireOp",EDGE,"E3.sketch_text.stroke-227"),sQuery(id+"F0.wireOp",EDGE,"E3.sketch_text.stroke-228"),sQuery(id+"F0.wireOp",EDGE,"E3.sketch_text.stroke-229"),sQuery(id+"F0.wireOp",EDGE,"E3.sketch_text.stroke-230"),sQuery(id+"F0.wireOp",EDGE,"E3.sketch_text.stroke-231"),sQuery(id+"F0.wireOp",EDGE,"E3.sketch_text.stroke-232"),sQuery(id+"F0.wireOp",EDGE,"E3.sketch_text.stroke-233"),sQuery(id+"F0.wireOp",EDGE,"E3.sketch_text.stroke-234"),sQuery(id+"F0.wireOp",EDGE,"E3.sketch_text.stroke-235"),sQuery(id+"F0.wireOp",EDGE,"E3.sketch_text.stroke-236"),sQuery(id+"F0.wireOp",EDGE,"E3.sketch_text.stroke-237"),sQuery(id+"F0.wireOp",EDGE,"E3.sketch_text.stroke-238"),sQuery(id+"F0.wireOp",EDGE,"E3.sketch_text.stroke-244"),sQuery(id+"F0.wireOp",EDGE,"E3.sketch_text.stroke-245"),sQuery(id+"F0.wireOp",EDGE,"E3.sketch_text.stroke-246"),sQuery(id+"F0.wireOp",EDGE,"E3.sketch_text.stroke-247"),sQuery(id+"F0.wireOp",EDGE,"E3.sketch_text.stroke-248"),sQuery(id+"F0.wireOp",EDGE,"E3.sketch_text.stroke-249"),sQuery(id+"F0.wireOp",EDGE,"E3.sketch_text.stroke-250"),sQuery(id+"F0.wireOp",EDGE,"E3.sketch_text.stroke-251"),sQuery(id+"F0.wireOp",EDGE,"E3.sketch_text.stroke-252"),sQuery(id+"F0.wireOp",EDGE,"E3.sketch_text.stroke-253"),sQuery(id+"F0.wireOp",EDGE,"E3.sketch_text.stroke-254"),sQuery(id+"F0.wireOp",EDGE,"E3.sketch_text.stroke-255"),sQuery(id+"F0.wireOp",EDGE,"E3.sketch_text.stroke-256"),sQuery(id+"F0.wireOp",EDGE,"E3.sketch_text.stroke-257"),sQuery(id+"F0.wireOp",EDGE,"E3.sketch_text.stroke-258"),sQuery(id+"F0.wireOp",EDGE,"E3.sketch_text.stroke-259"),sQuery(id+"F0.wireOp",EDGE,"E3.sketch_text.stroke-260"),sQuery(id+"F0.wireOp",EDGE,"E4.sketch_text.stroke-0"),sQuery(id+"F0.wireOp",EDGE,"E4.sketch_text.stroke-1"),sQuery(id+"F0.wireOp",EDGE,"E4.sketch_text.stroke-2"),sQuery(id+"F0.wireOp",EDGE,"E4.sketch_text.stroke-3"),sQuery(id+"F0.wireOp",EDGE,"E4.sketch_text.stroke-4"),sQuery(id+"F0.wireOp",EDGE,"E4.sketch_text.stroke-5"),sQuery(id+"F0.wireOp",EDGE,"E4.sketch_text.stroke-6"),sQuery(id+"F0.wireOp",EDGE,"E4.sketch_text.stroke-7"),sQuery(id+"F0.wireOp",EDGE,"E4.sketch_text.stroke-8"),sQuery(id+"F0.wireOp",EDGE,"E4.sketch_text.stroke-9"),sQuery(id+"F0.wireOp",EDGE,"E4.sketch_text.stroke-10"),sQuery(id+"F0.wireOp",EDGE,"E4.sketch_text.stroke-11"),sQuery(id+"F0.wireOp",EDGE,"E4.sketch_text.stroke-12"),sQuery(id+"F0.wireOp",EDGE,"E4.sketch_text.stroke-13"),sQuery(id+"F0.wireOp",EDGE,"E4.sketch_text.stroke-14"),sQuery(id+"F0.wireOp",EDGE,"E4.sketch_text.stroke-15"),sQuery(id+"F0.wireOp",EDGE,"E4.sketch_text.stroke-16"),sQuery(id+"F0.wireOp",EDGE,"E4.sketch_text.stroke-17"),sQuery(id+"F0.wireOp",EDGE,"E4.sketch_text.stroke-18"),sQuery(id+"F0.wireOp",EDGE,"E4.sketch_text.stroke-19"),sQuery(id+"F0.wireOp",EDGE,"E4.sketch_text.stroke-20"),sQuery(id+"F0.wireOp",EDGE,"E4.sketch_text.stroke-21"),sQuery(id+"F0.wireOp",EDGE,"E4.sketch_text.stroke-28"),sQuery(id+"F0.wireOp",EDGE,"E4.sketch_text.stroke-29"),sQuery(id+"F0.wireOp",EDGE,"E4.sketch_text.stroke-30"),sQuery(id+"F0.wireOp",EDGE,"E4.sketch_text.stroke-31"),sQuery(id+"F0.wireOp",EDGE,"E4.sketch_text.stroke-32"),sQuery(id+"F0.wireOp",EDGE,"E4.sketch_text.stroke-33"),sQuery(id+"F0.wireOp",EDGE,"E4.sketch_text.stroke-34"),sQuery(id+"F0.wireOp",EDGE,"E4.sketch_text.stroke-35"),sQuery(id+"F0.wireOp",EDGE,"E4.sketch_text.stroke-36"),sQuery(id+"F0.wireOp",EDGE,"E4.sketch_text.stroke-37"),sQuery(id+"F0.wireOp",EDGE,"E4.sketch_text.stroke-38"),sQuery(id+"F0.wireOp",EDGE,"E4.sketch_text.stroke-39"),sQuery(id+"F0.wireOp",EDGE,"E4.sketch_text.stroke-40"),sQuery(id+"F0.wireOp",EDGE,"E4.sketch_text.stroke-41"),sQuery(id+"F0.wireOp",EDGE,"E4.sketch_text.stroke-42"),sQuery(id+"F0.wireOp",EDGE,"E4.sketch_text.stroke-43"),sQuery(id+"F0.wireOp",EDGE,"E4.sketch_text.stroke-44"),sQuery(id+"F0.wireOp",EDGE,"E4.sketch_text.stroke-45"),sQuery(id+"F0.wireOp",EDGE,"E4.sketch_text.stroke-46"),sQuery(id+"F0.wireOp",EDGE,"E4.sketch_text.stroke-47"),sQuery(id+"F0.wireOp",EDGE,"E4.sketch_text.stroke-48"),sQuery(id+"F0.wireOp",EDGE,"E4.sketch_text.stroke-49"),sQuery(id+"F0.wireOp",EDGE,"E4.sketch_text.stroke-50"),sQuery(id+"F0.wireOp",EDGE,"E4.sketch_text.stroke-51"),sQuery(id+"F0.wireOp",EDGE,"E4.sketch_text.stroke-52"),sQuery(id+"F0.wireOp",EDGE,"E4.sketch_text.stroke-53"),sQuery(id+"F0.wireOp",EDGE,"E4.sketch_text.stroke-54"),sQuery(id+"F0.wireOp",EDGE,"E4.sketch_text.stroke-55"),sQuery(id+"F0.wireOp",EDGE,"E4.sketch_text.stroke-56"),sQuery(id+"F0.wireOp",EDGE,"E4.sketch_text.stroke-57"),sQuery(id+"F0.wireOp",EDGE,"E4.sketch_text.stroke-58"),sQuery(id+"F0.wireOp",EDGE,"E4.sketch_text.stroke-59"),sQuery(id+"F0.wireOp",EDGE,"E4.sketch_text.stroke-60"),sQuery(id+"F0.wireOp",EDGE,"E4.sketch_text.stroke-61"),sQuery(id+"F0.wireOp",EDGE,"E4.sketch_text.stroke-62"),sQuery(id+"F0.wireOp",EDGE,"E4.sketch_text.stroke-63"),sQuery(id+"F0.wireOp",EDGE,"E4.sketch_text.stroke-64"),sQuery(id+"F0.wireOp",EDGE,"E4.sketch_text.stroke-65"),sQuery(id+"F0.wireOp",EDGE,"E4.sketch_text.stroke-66"),sQuery(id+"F0.wireOp",EDGE,"E4.sketch_text.stroke-67"),sQuery(id+"F0.wireOp",EDGE,"E4.sketch_text.stroke-68"),sQuery(id+"F0.wireOp",EDGE,"E4.sketch_text.stroke-69"),sQuery(id+"F0.wireOp",EDGE,"E4.sketch_text.stroke-70"),sQuery(id+"F0.wireOp",EDGE,"E4.sketch_text.stroke-71"),sQuery(id+"F0.wireOp",EDGE,"E4.sketch_text.stroke-72"),sQuery(id+"F0.wireOp",EDGE,"E4.sketch_text.stroke-73"),sQuery(id+"F0.wireOp",EDGE,"E4.sketch_text.stroke-74"),sQuery(id+"F0.wireOp",EDGE,"E4.sketch_text.stroke-85"),sQuery(id+"F0.wireOp",EDGE,"E4.sketch_text.stroke-86"),sQuery(id+"F0.wireOp",EDGE,"E4.sketch_text.stroke-87"),sQuery(id+"F0.wireOp",EDGE,"E4.sketch_text.stroke-88"),sQuery(id+"F0.wireOp",EDGE,"E4.sketch_text.stroke-89"),sQuery(id+"F0.wireOp",EDGE,"E4.sketch_text.stroke-90"),sQuery(id+"F0.wireOp",EDGE,"E4.sketch_text.stroke-91"),sQuery(id+"F0.wireOp",EDGE,"E4.sketch_text.stroke-92"),sQuery(id+"F0.wireOp",EDGE,"E4.sketch_text.stroke-93"),sQuery(id+"F0.wireOp",EDGE,"E4.sketch_text.stroke-94"),sQuery(id+"F0.wireOp",EDGE,"E4.sketch_text.stroke-95"),sQuery(id+"F0.wireOp",EDGE,"E4.sketch_text.stroke-96"),sQuery(id+"F0.wireOp",EDGE,"E4.sketch_text.stroke-97"),sQuery(id+"F0.wireOp",EDGE,"E4.sketch_text.stroke-98"),sQuery(id+"F0.wireOp",EDGE,"E4.sketch_text.stroke-99"),sQuery(id+"F0.wireOp",EDGE,"E4.sketch_text.stroke-100"),sQuery(id+"F0.wireOp",EDGE,"E4.sketch_text.stroke-101"),sQuery(id+"F0.wireOp",EDGE,"E4.sketch_text.stroke-102"),sQuery(id+"F0.wireOp",EDGE,"E4.sketch_text.stroke-103"),sQuery(id+"F0.wireOp",EDGE,"E4.sketch_text.stroke-104"),sQuery(id+"F0.wireOp",EDGE,"E4.sketch_text.stroke-105"),sQuery(id+"F0.wireOp",EDGE,"E4.sketch_text.stroke-106"),sQuery(id+"F0.wireOp",EDGE,"E4.sketch_text.stroke-107"),sQuery(id+"F0.wireOp",EDGE,"E4.sketch_text.stroke-108"),sQuery(id+"F0.wireOp",EDGE,"E4.sketch_text.stroke-109"),sQuery(id+"F0.wireOp",EDGE,"E4.sketch_text.stroke-110"),sQuery(id+"F0.wireOp",EDGE,"E4.sketch_text.stroke-111"),sQuery(id+"F0.wireOp",EDGE,"E4.sketch_text.stroke-112"),sQuery(id+"F0.wireOp",EDGE,"E4.sketch_text.stroke-113"),sQuery(id+"F0.wireOp",EDGE,"E4.sketch_text.stroke-114"),sQuery(id+"F0.wireOp",EDGE,"E4.sketch_text.stroke-115"),sQuery(id+"F0.wireOp",EDGE,"E4.sketch_text.stroke-116"),sQuery(id+"F0.wireOp",EDGE,"E4.sketch_text.stroke-117"),sQuery(id+"F0.wireOp",EDGE,"E4.sketch_text.stroke-118"),sQuery(id+"F0.wireOp",EDGE,"E4.sketch_text.stroke-119"),sQuery(id+"F0.wireOp",EDGE,"E4.sketch_text.stroke-120"),sQuery(id+"F0.wireOp",EDGE,"E4.sketch_text.stroke-121"),sQuery(id+"F0.wireOp",EDGE,"E4.sketch_text.stroke-122"),sQuery(id+"F0.wireOp",EDGE,"E4.sketch_text.stroke-123"),sQuery(id+"F0.wireOp",EDGE,"E4.sketch_text.stroke-124"),sQuery(id+"F0.wireOp",EDGE,"E4.sketch_text.stroke-138"),sQuery(id+"F0.wireOp",EDGE,"E4.sketch_text.stroke-139"),sQuery(id+"F0.wireOp",EDGE,"E4.sketch_text.stroke-140"),sQuery(id+"F0.wireOp",EDGE,"E4.sketch_text.stroke-141"),sQuery(id+"F0.wireOp",EDGE,"E4.sketch_text.stroke-142"),sQuery(id+"F0.wireOp",EDGE,"E4.sketch_text.stroke-143"),sQuery(id+"F0.wireOp",EDGE,"E4.sketch_text.stroke-144"),sQuery(id+"F0.wireOp",EDGE,"E4.sketch_text.stroke-145"),sQuery(id+"F0.wireOp",EDGE,"E4.sketch_text.stroke-146"),sQuery(id+"F0.wireOp",EDGE,"E4.sketch_text.stroke-147"),sQuery(id+"F0.wireOp",EDGE,"E4.sketch_text.stroke-148"),sQuery(id+"F0.wireOp",EDGE,"E4.sketch_text.stroke-149"),sQuery(id+"F0.wireOp",EDGE,"E4.sketch_text.stroke-156"),sQuery(id+"F0.wireOp",EDGE,"E4.sketch_text.stroke-157"),sQuery(id+"F0.wireOp",EDGE,"E4.sketch_text.stroke-158"),sQuery(id+"F0.wireOp",EDGE,"E4.sketch_text.stroke-159"),sQuery(id+"F0.wireOp",EDGE,"E4.sketch_text.stroke-160"),sQuery(id+"F0.wireOp",EDGE,"E4.sketch_text.stroke-161"),sQuery(id+"F0.wireOp",EDGE,"E4.sketch_text.stroke-162"),sQuery(id+"F0.wireOp",EDGE,"E4.sketch_text.stroke-163"),sQuery(id+"F0.wireOp",EDGE,"E4.sketch_text.stroke-164"),sQuery(id+"F0.wireOp",EDGE,"E4.sketch_text.stroke-165"),sQuery(id+"F0.wireOp",EDGE,"E4.sketch_text.stroke-166"),sQuery(id+"F0.wireOp",EDGE,"E4.sketch_text.stroke-167"),sQuery(id+"F0.wireOp",EDGE,"E4.sketch_text.stroke-168"),sQuery(id+"F0.wireOp",EDGE,"E4.sketch_text.stroke-169"),sQuery(id+"F0.wireOp",EDGE,"E4.sketch_text.stroke-170"),sQuery(id+"F0.wireOp",EDGE,"E4.sketch_text.stroke-171"),sQuery(id+"F0.wireOp",EDGE,"E4.sketch_text.stroke-172"),sQuery(id+"F0.wireOp",EDGE,"E4.sketch_text.stroke-173"),sQuery(id+"F0.wireOp",EDGE,"E4.sketch_text.stroke-174"),sQuery(id+"F0.wireOp",EDGE,"E4.sketch_text.stroke-175"),sQuery(id+"F0.wireOp",EDGE,"E4.sketch_text.stroke-176"),sQuery(id+"F0.wireOp",EDGE,"E4.sketch_text.stroke-177"),sQuery(id+"F0.wireOp",EDGE,"E4.sketch_text.stroke-178"),sQuery(id+"F0.wireOp",EDGE,"E4.sketch_text.stroke-179"),sQuery(id+"F0.wireOp",EDGE,"E4.sketch_text.stroke-180"),sQuery(id+"F0.wireOp",EDGE,"E4.sketch_text.stroke-181"),sQuery(id+"F0.wireOp",EDGE,"E4.sketch_text.stroke-182"),sQuery(id+"F0.wireOp",EDGE,"E4.sketch_text.stroke-183"),sQuery(id+"F0.wireOp",EDGE,"E4.sketch_text.stroke-184"),sQuery(id+"F0.wireOp",EDGE,"E4.sketch_text.stroke-185"),sQuery(id+"F0.wireOp",EDGE,"E4.sketch_text.stroke-186"),sQuery(id+"F0.wireOp",EDGE,"E4.sketch_text.stroke-187"),sQuery(id+"F0.wireOp",EDGE,"E4.sketch_text.stroke-188"),sQuery(id+"F0.wireOp",EDGE,"E4.sketch_text.stroke-189"),sQuery(id+"F0.wireOp",EDGE,"E4.sketch_text.stroke-190"),sQuery(id+"F0.wireOp",EDGE,"E4.sketch_text.stroke-191"),sQuery(id+"F0.wireOp",EDGE,"E4.sketch_text.stroke-192"),sQuery(id+"F0.wireOp",EDGE,"E4.sketch_text.stroke-193"),sQuery(id+"F0.wireOp",EDGE,"E4.sketch_text.stroke-194"),sQuery(id+"F0.wireOp",EDGE,"E4.sketch_text.stroke-195"),sQuery(id+"F0.wireOp",EDGE,"E4.sketch_text.stroke-196"),sQuery(id+"F0.wireOp",EDGE,"E4.sketch_text.stroke-197"),sQuery(id+"F0.wireOp",EDGE,"E4.sketch_text.stroke-198"),sQuery(id+"F0.wireOp",EDGE,"E4.sketch_text.stroke-199"),sQuery(id+"F0.wireOp",EDGE,"E4.sketch_text.stroke-200"),sQuery(id+"F0.wireOp",EDGE,"E4.sketch_text.stroke-201"),sQuery(id+"F0.wireOp",EDGE,"E4.sketch_text.stroke-208"),sQuery(id+"F0.wireOp",EDGE,"E4.sketch_text.stroke-209"),sQuery(id+"F0.wireOp",EDGE,"E4.sketch_text.stroke-210"),sQuery(id+"F0.wireOp",EDGE,"E4.sketch_text.stroke-211"),sQuery(id+"F0.wireOp",EDGE,"E4.sketch_text.stroke-212"),sQuery(id+"F0.wireOp",EDGE,"E4.sketch_text.stroke-213"),sQuery(id+"F0.wireOp",EDGE,"E4.sketch_text.stroke-214"),sQuery(id+"F0.wireOp",EDGE,"E4.sketch_text.stroke-215"),sQuery(id+"F0.wireOp",EDGE,"E4.sketch_text.stroke-216"),sQuery(id+"F0.wireOp",EDGE,"E4.sketch_text.stroke-217"),sQuery(id+"F0.wireOp",EDGE,"E4.sketch_text.stroke-218"),sQuery(id+"F0.wireOp",EDGE,"E4.sketch_text.stroke-219"),sQuery(id+"F0.wireOp",EDGE,"E4.sketch_text.stroke-220"),sQuery(id+"F0.wireOp",EDGE,"E4.sketch_text.stroke-221"),sQuery(id+"F0.wireOp",EDGE,"E4.sketch_text.stroke-222"),sQuery(id+"F0.wireOp",EDGE,"E4.sketch_text.stroke-223"),sQuery(id+"F0.wireOp",EDGE,"E4.sketch_text.stroke-224"),sQuery(id+"F0.wireOp",EDGE,"E4.sketch_text.stroke-225"),sQuery(id+"F0.wireOp",EDGE,"E4.sketch_text.stroke-226"),sQuery(id+"F0.wireOp",EDGE,"E4.sketch_text.stroke-227"),sQuery(id+"F0.wireOp",EDGE,"E4.sketch_text.stroke-228"),sQuery(id+"F0.wireOp",EDGE,"E4.sketch_text.stroke-229"),sQuery(id+"F0.wireOp",EDGE,"E4.sketch_text.stroke-230"),sQuery(id+"F0.wireOp",EDGE,"E4.sketch_text.stroke-231"),sQuery(id+"F0.wireOp",EDGE,"E4.sketch_text.stroke-232"),sQuery(id+"F0.wireOp",EDGE,"E4.sketch_text.stroke-233"),sQuery(id+"F0.wireOp",EDGE,"E4.sketch_text.stroke-234"),sQuery(id+"F0.wireOp",EDGE,"E4.sketch_text.stroke-235"),sQuery(id+"F0.wireOp",EDGE,"E4.sketch_text.stroke-236"),sQuery(id+"F0.wireOp",EDGE,"E4.sketch_text.stroke-237"),sQuery(id+"F0.wireOp",EDGE,"E4.sketch_text.stroke-238"),sQuery(id+"F0.wireOp",EDGE,"E4.sketch_text.stroke-239"),sQuery(id+"F0.wireOp",EDGE,"E4.sketch_text.stroke-240"),sQuery(id+"F0.wireOp",EDGE,"E4.sketch_text.stroke-241"),sQuery(id+"F0.wireOp",EDGE,"E4.sketch_text.stroke-242"),sQuery(id+"F0.wireOp",EDGE,"E4.sketch_text.stroke-243"),sQuery(id+"F0.wireOp",EDGE,"E4.sketch_text.stroke-244"),sQuery(id+"F0.wireOp",EDGE,"E4.sketch_text.stroke-245"),sQuery(id+"F0.wireOp",EDGE,"E4.sketch_text.stroke-246"),sQuery(id+"F0.wireOp",EDGE,"E4.sketch_text.stroke-247"),sQuery(id+"F0.wireOp",EDGE,"E4.sketch_text.stroke-248"),sQuery(id+"F0.wireOp",EDGE,"E4.sketch_text.stroke-249"),sQuery(id+"F0.wireOp",EDGE,"E4.sketch_text.stroke-250"),sQuery(id+"F0.wireOp",EDGE,"E4.sketch_text.stroke-251"),sQuery(id+"F0.wireOp",EDGE,"E4.sketch_text.stroke-252"),sQuery(id+"F0.wireOp",EDGE,"E4.sketch_text.stroke-253"),sQuery(id+"F0.wireOp",EDGE,"E4.sketch_text.stroke-254"),sQuery(id+"F0.wireOp",EDGE,"E4.sketch_text.stroke-255"),sQuery(id+"F0.wireOp",EDGE,"E4.sketch_text.stroke-256"),sQuery(id+"F0.wireOp",EDGE,"E4.sketch_text.stroke-257"),sQuery(id+"F0.wireOp",EDGE,"E4.sketch_text.stroke-258"),sQuery(id+"F0.wireOp",EDGE,"E4.sketch_text.stroke-259"),sQuery(id+"F0.wireOp",EDGE,"E4.sketch_text.stroke-260"),sQuery(id+"F0.wireOp",EDGE,"E4.sketch_text.stroke-261"),sQuery(id+"F0.wireOp",EDGE,"E4.sketch_text.stroke-262"),sQuery(id+"F0.wireOp",EDGE,"E4.sketch_text.stroke-263"),sQuery(id+"F0.wireOp",EDGE,"E4.sketch_text.stroke-264"),sQuery(id+"F0.wireOp",EDGE,"E4.sketch_text.stroke-265"),sQuery(id+"F0.wireOp",EDGE,"E4.sketch_text.stroke-266"),sQuery(id+"F0.wireOp",EDGE,"E4.sketch_text.stroke-267"),sQuery(id+"F0.wireOp",EDGE,"E4.sketch_text.stroke-268"),sQuery(id+"F0.wireOp",EDGE,"E4.sketch_text.stroke-269"),sQuery(id+"F0.wireOp",EDGE,"E4.sketch_text.stroke-270"),sQuery(id+"F0.wireOp",EDGE,"E4.sketch_text.stroke-271"),sQuery(id+"F0.wireOp",EDGE,"E4.sketch_text.stroke-272"),sQuery(id+"F0.wireOp",EDGE,"E4.sketch_text.stroke-273"),sQuery(id+"F0.wireOp",EDGE,"E4.sketch_text.stroke-274"),sQuery(id+"F0.wireOp",EDGE,"E4.sketch_text.stroke-275"),sQuery(id+"F0.wireOp",EDGE,"E4.sketch_text.stroke-276"),sQuery(id+"F0.wireOp",EDGE,"E4.sketch_text.stroke-283"),sQuery(id+"F0.wireOp",EDGE,"E4.sketch_text.stroke-284"),sQuery(id+"F0.wireOp",EDGE,"E4.sketch_text.stroke-285"),sQuery(id+"F0.wireOp",EDGE,"E4.sketch_text.stroke-286"),sQuery(id+"F0.wireOp",EDGE,"E4.sketch_text.stroke-287"),sQuery(id+"F0.wireOp",EDGE,"E4.sketch_text.stroke-288"),sQuery(id+"F0.wireOp",EDGE,"E4.sketch_text.stroke-289"),sQuery(id+"F0.wireOp",EDGE,"E4.sketch_text.stroke-290"),sQuery(id+"F0.wireOp",EDGE,"E4.sketch_text.stroke-291"),sQuery(id+"F0.wireOp",EDGE,"E4.sketch_text.stroke-292"),sQuery(id+"F0.wireOp",EDGE,"E4.sketch_text.stroke-293"),sQuery(id+"F0.wireOp",EDGE,"E4.sketch_text.stroke-294"),sQuery(id+"F0.wireOp",EDGE,"E4.sketch_text.stroke-295"),sQuery(id+"F0.wireOp",EDGE,"E4.sketch_text.stroke-296"),sQuery(id+"F0.wireOp",EDGE,"E4.sketch_text.stroke-297"),sQuery(id+"F0.wireOp",EDGE,"E4.sketch_text.stroke-298"),sQuery(id+"F0.wireOp",EDGE,"E4.sketch_text.stroke-299"),sQuery(id+"F0.wireOp",EDGE,"E4.sketch_text.stroke-300"),sQuery(id+"F0.wireOp",EDGE,"E4.sketch_text.stroke-301"),sQuery(id+"F0.wireOp",EDGE,"E4.sketch_text.stroke-302"),sQuery(id+"F0.wireOp",EDGE,"E4.sketch_text.stroke-303"),sQuery(id+"F0.wireOp",EDGE,"E4.sketch_text.stroke-304"),sQuery(id+"F0.wireOp",EDGE,"E4.sketch_text.stroke-305"),sQuery(id+"F0.wireOp",EDGE,"E4.sketch_text.stroke-306"),sQuery(id+"F0.wireOp",EDGE,"E4.sketch_text.stroke-307"),sQuery(id+"F0.wireOp",EDGE,"E4.sketch_text.stroke-308"),sQuery(id+"F0.wireOp",EDGE,"E4.sketch_text.stroke-309"),sQuery(id+"F0.wireOp",EDGE,"E4.sketch_text.stroke-310"),sQuery(id+"F0.wireOp",EDGE,"E4.sketch_text.stroke-321"),sQuery(id+"F0.wireOp",EDGE,"E4.sketch_text.stroke-322"),sQuery(id+"F0.wireOp",EDGE,"E4.sketch_text.stroke-323"),sQuery(id+"F0.wireOp",EDGE,"E4.sketch_text.stroke-324"),sQuery(id+"F0.wireOp",EDGE,"E4.sketch_text.stroke-325"),sQuery(id+"F0.wireOp",EDGE,"E4.sketch_text.stroke-326"),sQuery(id+"F0.wireOp",EDGE,"E4.sketch_text.stroke-327"),sQuery(id+"F0.wireOp",EDGE,"E4.sketch_text.stroke-328"),sQuery(id+"F0.wireOp",EDGE,"E4.sketch_text.stroke-329"),sQuery(id+"F0.wireOp",EDGE,"E4.sketch_text.stroke-330"),sQuery(id+"F0.wireOp",EDGE,"E4.sketch_text.stroke-331"),sQuery(id+"F0.wireOp",EDGE,"E4.sketch_text.stroke-332"),sQuery(id+"F0.wireOp",EDGE,"E4.sketch_text.stroke-333"),sQuery(id+"F0.wireOp",EDGE,"E4.sketch_text.stroke-334"),sQuery(id+"F0.wireOp",EDGE,"E4.sketch_text.stroke-335"),sQuery(id+"F0.wireOp",EDGE,"E4.sketch_text.stroke-336"),sQuery(id+"F0.wireOp",EDGE,"E4.sketch_text.stroke-337"),sQuery(id+"F0.wireOp",EDGE,"E4.sketch_text.stroke-338"),sQuery(id+"F0.wireOp",EDGE,"E4.sketch_text.stroke-339"),sQuery(id+"F0.wireOp",EDGE,"E4.sketch_text.stroke-340"),sQuery(id+"F0.wireOp",EDGE,"E4.sketch_text.stroke-341"),sQuery(id+"F0.wireOp",EDGE,"E4.sketch_text.stroke-342"),sQuery(id+"F0.wireOp",EDGE,"E4.sketch_text.stroke-343"),sQuery(id+"F0.wireOp",EDGE,"E4.sketch_text.stroke-344"),sQuery(id+"F0.wireOp",EDGE,"E4.sketch_text.stroke-345"),sQuery(id+"F0.wireOp",EDGE,"E4.sketch_text.stroke-346"),sQuery(id+"F0.wireOp",EDGE,"E4.sketch_text.stroke-347"),sQuery(id+"F0.wireOp",EDGE,"E4.sketch_text.stroke-348"),sQuery(id+"F0.wireOp",EDGE,"E4.sketch_text.stroke-359"),sQuery(id+"F0.wireOp",EDGE,"E4.sketch_text.stroke-360"),sQuery(id+"F0.wireOp",EDGE,"E4.sketch_text.stroke-361"),sQuery(id+"F0.wireOp",EDGE,"E4.sketch_text.stroke-362"),sQuery(id+"F0.wireOp",EDGE,"E4.sketch_text.stroke-363"),sQuery(id+"F0.wireOp",EDGE,"E4.sketch_text.stroke-364"),sQuery(id+"F0.wireOp",EDGE,"E4.sketch_text.stroke-365"),sQuery(id+"F0.wireOp",EDGE,"E4.sketch_text.stroke-366"),sQuery(id+"F0.wireOp",EDGE,"E4.sketch_text.stroke-367"),sQuery(id+"F0.wireOp",EDGE,"E4.sketch_text.stroke-368"),sQuery(id+"F0.wireOp",EDGE,"E4.sketch_text.stroke-369"),sQuery(id+"F0.wireOp",EDGE,"E4.sketch_text.stroke-370"),sQuery(id+"F0.wireOp",EDGE,"E4.sketch_text.stroke-371"),sQuery(id+"F0.wireOp",EDGE,"E4.sketch_text.stroke-372"),sQuery(id+"F0.wireOp",EDGE,"E4.sketch_text.stroke-373"),sQuery(id+"F0.wireOp",EDGE,"E4.sketch_text.stroke-374"),sQuery(id+"F0.wireOp",EDGE,"E4.sketch_text.stroke-375"),sQuery(id+"F0.wireOp",EDGE,"E4.sketch_text.stroke-376"),sQuery(id+"F0.wireOp",EDGE,"E4.sketch_text.stroke-377"),sQuery(id+"F0.wireOp",EDGE,"E4.sketch_text.stroke-378"),sQuery(id+"F0.wireOp",EDGE,"E4.sketch_text.stroke-379"),sQuery(id+"F0.wireOp",EDGE,"E4.sketch_text.stroke-380"),sQuery(id+"F0.wireOp",EDGE,"E4.sketch_text.stroke-381"),sQuery(id+"F0.wireOp",EDGE,"E4.sketch_text.stroke-382"),sQuery(id+"F0.wireOp",EDGE,"E4.sketch_text.stroke-383"),sQuery(id+"F0.wireOp",EDGE,"E4.sketch_text.stroke-384"),sQuery(id+"F0.wireOp",EDGE,"E4.sketch_text.stroke-385"),sQuery(id+"F0.wireOp",EDGE,"E4.sketch_text.stroke-386"),sQuery(id+"F0.wireOp",EDGE,"E4.sketch_text.stroke-387"),sQuery(id+"F0.wireOp",EDGE,"E4.sketch_text.stroke-388"),sQuery(id+"F0.wireOp",EDGE,"E4.sketch_text.stroke-389"),sQuery(id+"F0.wireOp",EDGE,"E4.sketch_text.stroke-390"),sQuery(id+"F0.wireOp",EDGE,"E4.sketch_text.stroke-391"),sQuery(id+"F0.wireOp",EDGE,"E4.sketch_text.stroke-392")])],"isStart":true})]});}
            var Q5;
            Q5=makeQuery(id+"F6.opExtrude","CAP_EDGE",EDGE,{"disambiguationData":[OSD([sQuery(id+"F0.wireOp",EDGE,"E0.left")])],"isStart":true});
            var Q6;
            {var subQ0=sQuery(id+"F0.wireOp",EDGE,"E0.left");var subQ1=sQuery(id+"F0.wireOp",EDGE,"E0.bottom");Q6=makeQuery(id+"F7.opFillet","BLEND_EDGE",EDGE,{"blendedFrom":[makeQuery(id+"F6.opExtrude","SWEPT_EDGE",EDGE,{"disambiguationData":[OSD([subQ1,subQ0])]}),makeQuery(id+"F6.opExtrude","CAP_FACE",FACE,{"disambiguationData":[OSD([subQ1,sQuery(id+"F0.wireOp",EDGE,"E0.top"),subQ0,sQuery(id+"F0.wireOp",EDGE,"E0.right"),sQuery(id+"F0.wireOp",EDGE,"E3.sketch_text.stroke-0"),sQuery(id+"F0.wireOp",EDGE,"E3.sketch_text.stroke-1"),sQuery(id+"F0.wireOp",EDGE,"E3.sketch_text.stroke-2"),sQuery(id+"F0.wireOp",EDGE,"E3.sketch_text.stroke-3"),sQuery(id+"F0.wireOp",EDGE,"E3.sketch_text.stroke-4"),sQuery(id+"F0.wireOp",EDGE,"E3.sketch_text.stroke-5"),sQuery(id+"F0.wireOp",EDGE,"E3.sketch_text.stroke-6"),sQuery(id+"F0.wireOp",EDGE,"E3.sketch_text.stroke-7"),sQuery(id+"F0.wireOp",EDGE,"E3.sketch_text.stroke-8"),sQuery(id+"F0.wireOp",EDGE,"E3.sketch_text.stroke-9"),sQuery(id+"F0.wireOp",EDGE,"E3.sketch_text.stroke-10"),sQuery(id+"F0.wireOp",EDGE,"E3.sketch_text.stroke-11"),sQuery(id+"F0.wireOp",EDGE,"E3.sketch_text.stroke-12"),sQuery(id+"F0.wireOp",EDGE,"E3.sketch_text.stroke-13"),sQuery(id+"F0.wireOp",EDGE,"E3.sketch_text.stroke-14"),sQuery(id+"F0.wireOp",EDGE,"E3.sketch_text.stroke-15"),sQuery(id+"F0.wireOp",EDGE,"E3.sketch_text.stroke-16"),sQuery(id+"F0.wireOp",EDGE,"E3.sketch_text.stroke-17"),sQuery(id+"F0.wireOp",EDGE,"E3.sketch_text.stroke-18"),sQuery(id+"F0.wireOp",EDGE,"E3.sketch_text.stroke-19"),sQuery(id+"F0.wireOp",EDGE,"E3.sketch_text.stroke-20"),sQuery(id+"F0.wireOp",EDGE,"E3.sketch_text.stroke-21"),sQuery(id+"F0.wireOp",EDGE,"E3.sketch_text.stroke-22"),sQuery(id+"F0.wireOp",EDGE,"E3.sketch_text.stroke-23"),sQuery(id+"F0.wireOp",EDGE,"E3.sketch_text.stroke-24"),sQuery(id+"F0.wireOp",EDGE,"E3.sketch_text.stroke-25"),sQuery(id+"F0.wireOp",EDGE,"E3.sketch_text.stroke-26"),sQuery(id+"F0.wireOp",EDGE,"E3.sketch_text.stroke-27"),sQuery(id+"F0.wireOp",EDGE,"E3.sketch_text.stroke-28"),sQuery(id+"F0.wireOp",EDGE,"E3.sketch_text.stroke-29"),sQuery(id+"F0.wireOp",EDGE,"E3.sketch_text.stroke-30"),sQuery(id+"F0.wireOp",EDGE,"E3.sketch_text.stroke-31"),sQuery(id+"F0.wireOp",EDGE,"E3.sketch_text.stroke-32"),sQuery(id+"F0.wireOp",EDGE,"E3.sketch_text.stroke-33"),sQuery(id+"F0.wireOp",EDGE,"E3.sketch_text.stroke-34"),sQuery(id+"F0.wireOp",EDGE,"E3.sketch_text.stroke-35"),sQuery(id+"F0.wireOp",EDGE,"E3.sketch_text.stroke-36"),sQuery(id+"F0.wireOp",EDGE,"E3.sketch_text.stroke-37"),sQuery(id+"F0.wireOp",EDGE,"E3.sketch_text.stroke-38"),sQuery(id+"F0.wireOp",EDGE,"E3.sketch_text.stroke-39"),sQuery(id+"F0.wireOp",EDGE,"E3.sketch_text.stroke-40"),sQuery(id+"F0.wireOp",EDGE,"E3.sketch_text.stroke-41"),sQuery(id+"F0.wireOp",EDGE,"E3.sketch_text.stroke-42"),sQuery(id+"F0.wireOp",EDGE,"E3.sketch_text.stroke-43"),sQuery(id+"F0.wireOp",EDGE,"E3.sketch_text.stroke-44"),sQuery(id+"F0.wireOp",EDGE,"E3.sketch_text.stroke-45"),sQuery(id+"F0.wireOp",EDGE,"E3.sketch_text.stroke-46"),sQuery(id+"F0.wireOp",EDGE,"E3.sketch_text.stroke-47"),sQuery(id+"F0.wireOp",EDGE,"E3.sketch_text.stroke-48"),sQuery(id+"F0.wireOp",EDGE,"E3.sketch_text.stroke-49"),sQuery(id+"F0.wireOp",EDGE,"E3.sketch_text.stroke-50"),sQuery(id+"F0.wireOp",EDGE,"E3.sketch_text.stroke-51"),sQuery(id+"F0.wireOp",EDGE,"E3.sketch_text.stroke-52"),sQuery(id+"F0.wireOp",EDGE,"E3.sketch_text.stroke-53"),sQuery(id+"F0.wireOp",EDGE,"E3.sketch_text.stroke-54"),sQuery(id+"F0.wireOp",EDGE,"E3.sketch_text.stroke-55"),sQuery(id+"F0.wireOp",EDGE,"E3.sketch_text.stroke-56"),sQuery(id+"F0.wireOp",EDGE,"E3.sketch_text.stroke-57"),sQuery(id+"F0.wireOp",EDGE,"E3.sketch_text.stroke-58"),sQuery(id+"F0.wireOp",EDGE,"E3.sketch_text.stroke-59"),sQuery(id+"F0.wireOp",EDGE,"E3.sketch_text.stroke-60"),sQuery(id+"F0.wireOp",EDGE,"E3.sketch_text.stroke-61"),sQuery(id+"F0.wireOp",EDGE,"E3.sketch_text.stroke-62"),sQuery(id+"F0.wireOp",EDGE,"E3.sketch_text.stroke-63"),sQuery(id+"F0.wireOp",EDGE,"E3.sketch_text.stroke-64"),sQuery(id+"F0.wireOp",EDGE,"E3.sketch_text.stroke-65"),sQuery(id+"F0.wireOp",EDGE,"E3.sketch_text.stroke-66"),sQuery(id+"F0.wireOp",EDGE,"E3.sketch_text.stroke-67"),sQuery(id+"F0.wireOp",EDGE,"E3.sketch_text.stroke-68"),sQuery(id+"F0.wireOp",EDGE,"E3.sketch_text.stroke-69"),sQuery(id+"F0.wireOp",EDGE,"E3.sketch_text.stroke-70"),sQuery(id+"F0.wireOp",EDGE,"E3.sketch_text.stroke-71"),sQuery(id+"F0.wireOp",EDGE,"E3.sketch_text.stroke-72"),sQuery(id+"F0.wireOp",EDGE,"E3.sketch_text.stroke-73"),sQuery(id+"F0.wireOp",EDGE,"E3.sketch_text.stroke-74"),sQuery(id+"F0.wireOp",EDGE,"E3.sketch_text.stroke-88"),sQuery(id+"F0.wireOp",EDGE,"E3.sketch_text.stroke-89"),sQuery(id+"F0.wireOp",EDGE,"E3.sketch_text.stroke-90"),sQuery(id+"F0.wireOp",EDGE,"E3.sketch_text.stroke-91"),sQuery(id+"F0.wireOp",EDGE,"E3.sketch_text.stroke-92"),sQuery(id+"F0.wireOp",EDGE,"E3.sketch_text.stroke-93"),sQuery(id+"F0.wireOp",EDGE,"E3.sketch_text.stroke-94"),sQuery(id+"F0.wireOp",EDGE,"E3.sketch_text.stroke-95"),sQuery(id+"F0.wireOp",EDGE,"E3.sketch_text.stroke-96"),sQuery(id+"F0.wireOp",EDGE,"E3.sketch_text.stroke-97"),sQuery(id+"F0.wireOp",EDGE,"E3.sketch_text.stroke-98"),sQuery(id+"F0.wireOp",EDGE,"E3.sketch_text.stroke-99"),sQuery(id+"F0.wireOp",EDGE,"E3.sketch_text.stroke-106"),sQuery(id+"F0.wireOp",EDGE,"E3.sketch_text.stroke-107"),sQuery(id+"F0.wireOp",EDGE,"E3.sketch_text.stroke-108"),sQuery(id+"F0.wireOp",EDGE,"E3.sketch_text.stroke-109"),sQuery(id+"F0.wireOp",EDGE,"E3.sketch_text.stroke-110"),sQuery(id+"F0.wireOp",EDGE,"E3.sketch_text.stroke-111"),sQuery(id+"F0.wireOp",EDGE,"E3.sketch_text.stroke-112"),sQuery(id+"F0.wireOp",EDGE,"E3.sketch_text.stroke-113"),sQuery(id+"F0.wireOp",EDGE,"E3.sketch_text.stroke-114"),sQuery(id+"F0.wireOp",EDGE,"E3.sketch_text.stroke-115"),sQuery(id+"F0.wireOp",EDGE,"E3.sketch_text.stroke-116"),sQuery(id+"F0.wireOp",EDGE,"E3.sketch_text.stroke-117"),sQuery(id+"F0.wireOp",EDGE,"E3.sketch_text.stroke-118"),sQuery(id+"F0.wireOp",EDGE,"E3.sketch_text.stroke-119"),sQuery(id+"F0.wireOp",EDGE,"E3.sketch_text.stroke-120"),sQuery(id+"F0.wireOp",EDGE,"E3.sketch_text.stroke-121"),sQuery(id+"F0.wireOp",EDGE,"E3.sketch_text.stroke-122"),sQuery(id+"F0.wireOp",EDGE,"E3.sketch_text.stroke-123"),sQuery(id+"F0.wireOp",EDGE,"E3.sketch_text.stroke-124"),sQuery(id+"F0.wireOp",EDGE,"E3.sketch_text.stroke-125"),sQuery(id+"F0.wireOp",EDGE,"E3.sketch_text.stroke-126"),sQuery(id+"F0.wireOp",EDGE,"E3.sketch_text.stroke-127"),sQuery(id+"F0.wireOp",EDGE,"E3.sketch_text.stroke-128"),sQuery(id+"F0.wireOp",EDGE,"E3.sketch_text.stroke-129"),sQuery(id+"F0.wireOp",EDGE,"E3.sketch_text.stroke-130"),sQuery(id+"F0.wireOp",EDGE,"E3.sketch_text.stroke-131"),sQuery(id+"F0.wireOp",EDGE,"E3.sketch_text.stroke-132"),sQuery(id+"F0.wireOp",EDGE,"E3.sketch_text.stroke-133"),sQuery(id+"F0.wireOp",EDGE,"E3.sketch_text.stroke-134"),sQuery(id+"F0.wireOp",EDGE,"E3.sketch_text.stroke-135"),sQuery(id+"F0.wireOp",EDGE,"E3.sketch_text.stroke-136"),sQuery(id+"F0.wireOp",EDGE,"E3.sketch_text.stroke-137"),sQuery(id+"F0.wireOp",EDGE,"E3.sketch_text.stroke-138"),sQuery(id+"F0.wireOp",EDGE,"E3.sketch_text.stroke-139"),sQuery(id+"F0.wireOp",EDGE,"E3.sketch_text.stroke-140"),sQuery(id+"F0.wireOp",EDGE,"E3.sketch_text.stroke-141"),sQuery(id+"F0.wireOp",EDGE,"E3.sketch_text.stroke-142"),sQuery(id+"F0.wireOp",EDGE,"E3.sketch_text.stroke-143"),sQuery(id+"F0.wireOp",EDGE,"E3.sketch_text.stroke-144"),sQuery(id+"F0.wireOp",EDGE,"E3.sketch_text.stroke-145"),sQuery(id+"F0.wireOp",EDGE,"E3.sketch_text.stroke-146"),sQuery(id+"F0.wireOp",EDGE,"E3.sketch_text.stroke-147"),sQuery(id+"F0.wireOp",EDGE,"E3.sketch_text.stroke-155"),sQuery(id+"F0.wireOp",EDGE,"E3.sketch_text.stroke-156"),sQuery(id+"F0.wireOp",EDGE,"E3.sketch_text.stroke-157"),sQuery(id+"F0.wireOp",EDGE,"E3.sketch_text.stroke-158"),sQuery(id+"F0.wireOp",EDGE,"E3.sketch_text.stroke-159"),sQuery(id+"F0.wireOp",EDGE,"E3.sketch_text.stroke-160"),sQuery(id+"F0.wireOp",EDGE,"E3.sketch_text.stroke-161"),sQuery(id+"F0.wireOp",EDGE,"E3.sketch_text.stroke-162"),sQuery(id+"F0.wireOp",EDGE,"E3.sketch_text.stroke-163"),sQuery(id+"F0.wireOp",EDGE,"E3.sketch_text.stroke-164"),sQuery(id+"F0.wireOp",EDGE,"E3.sketch_text.stroke-165"),sQuery(id+"F0.wireOp",EDGE,"E3.sketch_text.stroke-166"),sQuery(id+"F0.wireOp",EDGE,"E3.sketch_text.stroke-167"),sQuery(id+"F0.wireOp",EDGE,"E3.sketch_text.stroke-168"),sQuery(id+"F0.wireOp",EDGE,"E3.sketch_text.stroke-169"),sQuery(id+"F0.wireOp",EDGE,"E3.sketch_text.stroke-170"),sQuery(id+"F0.wireOp",EDGE,"E3.sketch_text.stroke-171"),sQuery(id+"F0.wireOp",EDGE,"E3.sketch_text.stroke-172"),sQuery(id+"F0.wireOp",EDGE,"E3.sketch_text.stroke-173"),sQuery(id+"F0.wireOp",EDGE,"E3.sketch_text.stroke-174"),sQuery(id+"F0.wireOp",EDGE,"E3.sketch_text.stroke-175"),sQuery(id+"F0.wireOp",EDGE,"E3.sketch_text.stroke-176"),sQuery(id+"F0.wireOp",EDGE,"E3.sketch_text.stroke-177"),sQuery(id+"F0.wireOp",EDGE,"E3.sketch_text.stroke-178"),sQuery(id+"F0.wireOp",EDGE,"E3.sketch_text.stroke-179"),sQuery(id+"F0.wireOp",EDGE,"E3.sketch_text.stroke-180"),sQuery(id+"F0.wireOp",EDGE,"E3.sketch_text.stroke-181"),sQuery(id+"F0.wireOp",EDGE,"E3.sketch_text.stroke-182"),sQuery(id+"F0.wireOp",EDGE,"E3.sketch_text.stroke-183"),sQuery(id+"F0.wireOp",EDGE,"E3.sketch_text.stroke-184"),sQuery(id+"F0.wireOp",EDGE,"E3.sketch_text.stroke-185"),sQuery(id+"F0.wireOp",EDGE,"E3.sketch_text.stroke-186"),sQuery(id+"F0.wireOp",EDGE,"E3.sketch_text.stroke-187"),sQuery(id+"F0.wireOp",EDGE,"E3.sketch_text.stroke-188"),sQuery(id+"F0.wireOp",EDGE,"E3.sketch_text.stroke-189"),sQuery(id+"F0.wireOp",EDGE,"E3.sketch_text.stroke-190"),sQuery(id+"F0.wireOp",EDGE,"E3.sketch_text.stroke-191"),sQuery(id+"F0.wireOp",EDGE,"E3.sketch_text.stroke-192"),sQuery(id+"F0.wireOp",EDGE,"E3.sketch_text.stroke-193"),sQuery(id+"F0.wireOp",EDGE,"E3.sketch_text.stroke-194"),sQuery(id+"F0.wireOp",EDGE,"E3.sketch_text.stroke-195"),sQuery(id+"F0.wireOp",EDGE,"E3.sketch_text.stroke-196"),sQuery(id+"F0.wireOp",EDGE,"E3.sketch_text.stroke-197"),sQuery(id+"F0.wireOp",EDGE,"E3.sketch_text.stroke-198"),sQuery(id+"F0.wireOp",EDGE,"E3.sketch_text.stroke-199"),sQuery(id+"F0.wireOp",EDGE,"E3.sketch_text.stroke-200"),sQuery(id+"F0.wireOp",EDGE,"E3.sketch_text.stroke-201"),sQuery(id+"F0.wireOp",EDGE,"E3.sketch_text.stroke-202"),sQuery(id+"F0.wireOp",EDGE,"E3.sketch_text.stroke-203"),sQuery(id+"F0.wireOp",EDGE,"E3.sketch_text.stroke-204"),sQuery(id+"F0.wireOp",EDGE,"E3.sketch_text.stroke-205"),sQuery(id+"F0.wireOp",EDGE,"E3.sketch_text.stroke-206"),sQuery(id+"F0.wireOp",EDGE,"E3.sketch_text.stroke-207"),sQuery(id+"F0.wireOp",EDGE,"E3.sketch_text.stroke-208"),sQuery(id+"F0.wireOp",EDGE,"E3.sketch_text.stroke-209"),sQuery(id+"F0.wireOp",EDGE,"E3.sketch_text.stroke-210"),sQuery(id+"F0.wireOp",EDGE,"E3.sketch_text.stroke-211"),sQuery(id+"F0.wireOp",EDGE,"E3.sketch_text.stroke-212"),sQuery(id+"F0.wireOp",EDGE,"E3.sketch_text.stroke-213"),sQuery(id+"F0.wireOp",EDGE,"E3.sketch_text.stroke-214"),sQuery(id+"F0.wireOp",EDGE,"E3.sketch_text.stroke-215"),sQuery(id+"F0.wireOp",EDGE,"E3.sketch_text.stroke-216"),sQuery(id+"F0.wireOp",EDGE,"E3.sketch_text.stroke-217"),sQuery(id+"F0.wireOp",EDGE,"E3.sketch_text.stroke-218"),sQuery(id+"F0.wireOp",EDGE,"E3.sketch_text.stroke-219"),sQuery(id+"F0.wireOp",EDGE,"E3.sketch_text.stroke-220"),sQuery(id+"F0.wireOp",EDGE,"E3.sketch_text.stroke-221"),sQuery(id+"F0.wireOp",EDGE,"E3.sketch_text.stroke-222"),sQuery(id+"F0.wireOp",EDGE,"E3.sketch_text.stroke-223"),sQuery(id+"F0.wireOp",EDGE,"E3.sketch_text.stroke-224"),sQuery(id+"F0.wireOp",EDGE,"E3.sketch_text.stroke-225"),sQuery(id+"F0.wireOp",EDGE,"E3.sketch_text.stroke-226"),sQuery(id+"F0.wireOp",EDGE,"E3.sketch_text.stroke-227"),sQuery(id+"F0.wireOp",EDGE,"E3.sketch_text.stroke-228"),sQuery(id+"F0.wireOp",EDGE,"E3.sketch_text.stroke-229"),sQuery(id+"F0.wireOp",EDGE,"E3.sketch_text.stroke-230"),sQuery(id+"F0.wireOp",EDGE,"E3.sketch_text.stroke-231"),sQuery(id+"F0.wireOp",EDGE,"E3.sketch_text.stroke-232"),sQuery(id+"F0.wireOp",EDGE,"E3.sketch_text.stroke-233"),sQuery(id+"F0.wireOp",EDGE,"E3.sketch_text.stroke-234"),sQuery(id+"F0.wireOp",EDGE,"E3.sketch_text.stroke-235"),sQuery(id+"F0.wireOp",EDGE,"E3.sketch_text.stroke-236"),sQuery(id+"F0.wireOp",EDGE,"E3.sketch_text.stroke-237"),sQuery(id+"F0.wireOp",EDGE,"E3.sketch_text.stroke-238"),sQuery(id+"F0.wireOp",EDGE,"E3.sketch_text.stroke-244"),sQuery(id+"F0.wireOp",EDGE,"E3.sketch_text.stroke-245"),sQuery(id+"F0.wireOp",EDGE,"E3.sketch_text.stroke-246"),sQuery(id+"F0.wireOp",EDGE,"E3.sketch_text.stroke-247"),sQuery(id+"F0.wireOp",EDGE,"E3.sketch_text.stroke-248"),sQuery(id+"F0.wireOp",EDGE,"E3.sketch_text.stroke-249"),sQuery(id+"F0.wireOp",EDGE,"E3.sketch_text.stroke-250"),sQuery(id+"F0.wireOp",EDGE,"E3.sketch_text.stroke-251"),sQuery(id+"F0.wireOp",EDGE,"E3.sketch_text.stroke-252"),sQuery(id+"F0.wireOp",EDGE,"E3.sketch_text.stroke-253"),sQuery(id+"F0.wireOp",EDGE,"E3.sketch_text.stroke-254"),sQuery(id+"F0.wireOp",EDGE,"E3.sketch_text.stroke-255"),sQuery(id+"F0.wireOp",EDGE,"E3.sketch_text.stroke-256"),sQuery(id+"F0.wireOp",EDGE,"E3.sketch_text.stroke-257"),sQuery(id+"F0.wireOp",EDGE,"E3.sketch_text.stroke-258"),sQuery(id+"F0.wireOp",EDGE,"E3.sketch_text.stroke-259"),sQuery(id+"F0.wireOp",EDGE,"E3.sketch_text.stroke-260"),sQuery(id+"F0.wireOp",EDGE,"E4.sketch_text.stroke-0"),sQuery(id+"F0.wireOp",EDGE,"E4.sketch_text.stroke-1"),sQuery(id+"F0.wireOp",EDGE,"E4.sketch_text.stroke-2"),sQuery(id+"F0.wireOp",EDGE,"E4.sketch_text.stroke-3"),sQuery(id+"F0.wireOp",EDGE,"E4.sketch_text.stroke-4"),sQuery(id+"F0.wireOp",EDGE,"E4.sketch_text.stroke-5"),sQuery(id+"F0.wireOp",EDGE,"E4.sketch_text.stroke-6"),sQuery(id+"F0.wireOp",EDGE,"E4.sketch_text.stroke-7"),sQuery(id+"F0.wireOp",EDGE,"E4.sketch_text.stroke-8"),sQuery(id+"F0.wireOp",EDGE,"E4.sketch_text.stroke-9"),sQuery(id+"F0.wireOp",EDGE,"E4.sketch_text.stroke-10"),sQuery(id+"F0.wireOp",EDGE,"E4.sketch_text.stroke-11"),sQuery(id+"F0.wireOp",EDGE,"E4.sketch_text.stroke-12"),sQuery(id+"F0.wireOp",EDGE,"E4.sketch_text.stroke-13"),sQuery(id+"F0.wireOp",EDGE,"E4.sketch_text.stroke-14"),sQuery(id+"F0.wireOp",EDGE,"E4.sketch_text.stroke-15"),sQuery(id+"F0.wireOp",EDGE,"E4.sketch_text.stroke-16"),sQuery(id+"F0.wireOp",EDGE,"E4.sketch_text.stroke-17"),sQuery(id+"F0.wireOp",EDGE,"E4.sketch_text.stroke-18"),sQuery(id+"F0.wireOp",EDGE,"E4.sketch_text.stroke-19"),sQuery(id+"F0.wireOp",EDGE,"E4.sketch_text.stroke-20"),sQuery(id+"F0.wireOp",EDGE,"E4.sketch_text.stroke-21"),sQuery(id+"F0.wireOp",EDGE,"E4.sketch_text.stroke-28"),sQuery(id+"F0.wireOp",EDGE,"E4.sketch_text.stroke-29"),sQuery(id+"F0.wireOp",EDGE,"E4.sketch_text.stroke-30"),sQuery(id+"F0.wireOp",EDGE,"E4.sketch_text.stroke-31"),sQuery(id+"F0.wireOp",EDGE,"E4.sketch_text.stroke-32"),sQuery(id+"F0.wireOp",EDGE,"E4.sketch_text.stroke-33"),sQuery(id+"F0.wireOp",EDGE,"E4.sketch_text.stroke-34"),sQuery(id+"F0.wireOp",EDGE,"E4.sketch_text.stroke-35"),sQuery(id+"F0.wireOp",EDGE,"E4.sketch_text.stroke-36"),sQuery(id+"F0.wireOp",EDGE,"E4.sketch_text.stroke-37"),sQuery(id+"F0.wireOp",EDGE,"E4.sketch_text.stroke-38"),sQuery(id+"F0.wireOp",EDGE,"E4.sketch_text.stroke-39"),sQuery(id+"F0.wireOp",EDGE,"E4.sketch_text.stroke-40"),sQuery(id+"F0.wireOp",EDGE,"E4.sketch_text.stroke-41"),sQuery(id+"F0.wireOp",EDGE,"E4.sketch_text.stroke-42"),sQuery(id+"F0.wireOp",EDGE,"E4.sketch_text.stroke-43"),sQuery(id+"F0.wireOp",EDGE,"E4.sketch_text.stroke-44"),sQuery(id+"F0.wireOp",EDGE,"E4.sketch_text.stroke-45"),sQuery(id+"F0.wireOp",EDGE,"E4.sketch_text.stroke-46"),sQuery(id+"F0.wireOp",EDGE,"E4.sketch_text.stroke-47"),sQuery(id+"F0.wireOp",EDGE,"E4.sketch_text.stroke-48"),sQuery(id+"F0.wireOp",EDGE,"E4.sketch_text.stroke-49"),sQuery(id+"F0.wireOp",EDGE,"E4.sketch_text.stroke-50"),sQuery(id+"F0.wireOp",EDGE,"E4.sketch_text.stroke-51"),sQuery(id+"F0.wireOp",EDGE,"E4.sketch_text.stroke-52"),sQuery(id+"F0.wireOp",EDGE,"E4.sketch_text.stroke-53"),sQuery(id+"F0.wireOp",EDGE,"E4.sketch_text.stroke-54"),sQuery(id+"F0.wireOp",EDGE,"E4.sketch_text.stroke-55"),sQuery(id+"F0.wireOp",EDGE,"E4.sketch_text.stroke-56"),sQuery(id+"F0.wireOp",EDGE,"E4.sketch_text.stroke-57"),sQuery(id+"F0.wireOp",EDGE,"E4.sketch_text.stroke-58"),sQuery(id+"F0.wireOp",EDGE,"E4.sketch_text.stroke-59"),sQuery(id+"F0.wireOp",EDGE,"E4.sketch_text.stroke-60"),sQuery(id+"F0.wireOp",EDGE,"E4.sketch_text.stroke-61"),sQuery(id+"F0.wireOp",EDGE,"E4.sketch_text.stroke-62"),sQuery(id+"F0.wireOp",EDGE,"E4.sketch_text.stroke-63"),sQuery(id+"F0.wireOp",EDGE,"E4.sketch_text.stroke-64"),sQuery(id+"F0.wireOp",EDGE,"E4.sketch_text.stroke-65"),sQuery(id+"F0.wireOp",EDGE,"E4.sketch_text.stroke-66"),sQuery(id+"F0.wireOp",EDGE,"E4.sketch_text.stroke-67"),sQuery(id+"F0.wireOp",EDGE,"E4.sketch_text.stroke-68"),sQuery(id+"F0.wireOp",EDGE,"E4.sketch_text.stroke-69"),sQuery(id+"F0.wireOp",EDGE,"E4.sketch_text.stroke-70"),sQuery(id+"F0.wireOp",EDGE,"E4.sketch_text.stroke-71"),sQuery(id+"F0.wireOp",EDGE,"E4.sketch_text.stroke-72"),sQuery(id+"F0.wireOp",EDGE,"E4.sketch_text.stroke-73"),sQuery(id+"F0.wireOp",EDGE,"E4.sketch_text.stroke-74"),sQuery(id+"F0.wireOp",EDGE,"E4.sketch_text.stroke-85"),sQuery(id+"F0.wireOp",EDGE,"E4.sketch_text.stroke-86"),sQuery(id+"F0.wireOp",EDGE,"E4.sketch_text.stroke-87"),sQuery(id+"F0.wireOp",EDGE,"E4.sketch_text.stroke-88"),sQuery(id+"F0.wireOp",EDGE,"E4.sketch_text.stroke-89"),sQuery(id+"F0.wireOp",EDGE,"E4.sketch_text.stroke-90"),sQuery(id+"F0.wireOp",EDGE,"E4.sketch_text.stroke-91"),sQuery(id+"F0.wireOp",EDGE,"E4.sketch_text.stroke-92"),sQuery(id+"F0.wireOp",EDGE,"E4.sketch_text.stroke-93"),sQuery(id+"F0.wireOp",EDGE,"E4.sketch_text.stroke-94"),sQuery(id+"F0.wireOp",EDGE,"E4.sketch_text.stroke-95"),sQuery(id+"F0.wireOp",EDGE,"E4.sketch_text.stroke-96"),sQuery(id+"F0.wireOp",EDGE,"E4.sketch_text.stroke-97"),sQuery(id+"F0.wireOp",EDGE,"E4.sketch_text.stroke-98"),sQuery(id+"F0.wireOp",EDGE,"E4.sketch_text.stroke-99"),sQuery(id+"F0.wireOp",EDGE,"E4.sketch_text.stroke-100"),sQuery(id+"F0.wireOp",EDGE,"E4.sketch_text.stroke-101"),sQuery(id+"F0.wireOp",EDGE,"E4.sketch_text.stroke-102"),sQuery(id+"F0.wireOp",EDGE,"E4.sketch_text.stroke-103"),sQuery(id+"F0.wireOp",EDGE,"E4.sketch_text.stroke-104"),sQuery(id+"F0.wireOp",EDGE,"E4.sketch_text.stroke-105"),sQuery(id+"F0.wireOp",EDGE,"E4.sketch_text.stroke-106"),sQuery(id+"F0.wireOp",EDGE,"E4.sketch_text.stroke-107"),sQuery(id+"F0.wireOp",EDGE,"E4.sketch_text.stroke-108"),sQuery(id+"F0.wireOp",EDGE,"E4.sketch_text.stroke-109"),sQuery(id+"F0.wireOp",EDGE,"E4.sketch_text.stroke-110"),sQuery(id+"F0.wireOp",EDGE,"E4.sketch_text.stroke-111"),sQuery(id+"F0.wireOp",EDGE,"E4.sketch_text.stroke-112"),sQuery(id+"F0.wireOp",EDGE,"E4.sketch_text.stroke-113"),sQuery(id+"F0.wireOp",EDGE,"E4.sketch_text.stroke-114"),sQuery(id+"F0.wireOp",EDGE,"E4.sketch_text.stroke-115"),sQuery(id+"F0.wireOp",EDGE,"E4.sketch_text.stroke-116"),sQuery(id+"F0.wireOp",EDGE,"E4.sketch_text.stroke-117"),sQuery(id+"F0.wireOp",EDGE,"E4.sketch_text.stroke-118"),sQuery(id+"F0.wireOp",EDGE,"E4.sketch_text.stroke-119"),sQuery(id+"F0.wireOp",EDGE,"E4.sketch_text.stroke-120"),sQuery(id+"F0.wireOp",EDGE,"E4.sketch_text.stroke-121"),sQuery(id+"F0.wireOp",EDGE,"E4.sketch_text.stroke-122"),sQuery(id+"F0.wireOp",EDGE,"E4.sketch_text.stroke-123"),sQuery(id+"F0.wireOp",EDGE,"E4.sketch_text.stroke-124"),sQuery(id+"F0.wireOp",EDGE,"E4.sketch_text.stroke-138"),sQuery(id+"F0.wireOp",EDGE,"E4.sketch_text.stroke-139"),sQuery(id+"F0.wireOp",EDGE,"E4.sketch_text.stroke-140"),sQuery(id+"F0.wireOp",EDGE,"E4.sketch_text.stroke-141"),sQuery(id+"F0.wireOp",EDGE,"E4.sketch_text.stroke-142"),sQuery(id+"F0.wireOp",EDGE,"E4.sketch_text.stroke-143"),sQuery(id+"F0.wireOp",EDGE,"E4.sketch_text.stroke-144"),sQuery(id+"F0.wireOp",EDGE,"E4.sketch_text.stroke-145"),sQuery(id+"F0.wireOp",EDGE,"E4.sketch_text.stroke-146"),sQuery(id+"F0.wireOp",EDGE,"E4.sketch_text.stroke-147"),sQuery(id+"F0.wireOp",EDGE,"E4.sketch_text.stroke-148"),sQuery(id+"F0.wireOp",EDGE,"E4.sketch_text.stroke-149"),sQuery(id+"F0.wireOp",EDGE,"E4.sketch_text.stroke-156"),sQuery(id+"F0.wireOp",EDGE,"E4.sketch_text.stroke-157"),sQuery(id+"F0.wireOp",EDGE,"E4.sketch_text.stroke-158"),sQuery(id+"F0.wireOp",EDGE,"E4.sketch_text.stroke-159"),sQuery(id+"F0.wireOp",EDGE,"E4.sketch_text.stroke-160"),sQuery(id+"F0.wireOp",EDGE,"E4.sketch_text.stroke-161"),sQuery(id+"F0.wireOp",EDGE,"E4.sketch_text.stroke-162"),sQuery(id+"F0.wireOp",EDGE,"E4.sketch_text.stroke-163"),sQuery(id+"F0.wireOp",EDGE,"E4.sketch_text.stroke-164"),sQuery(id+"F0.wireOp",EDGE,"E4.sketch_text.stroke-165"),sQuery(id+"F0.wireOp",EDGE,"E4.sketch_text.stroke-166"),sQuery(id+"F0.wireOp",EDGE,"E4.sketch_text.stroke-167"),sQuery(id+"F0.wireOp",EDGE,"E4.sketch_text.stroke-168"),sQuery(id+"F0.wireOp",EDGE,"E4.sketch_text.stroke-169"),sQuery(id+"F0.wireOp",EDGE,"E4.sketch_text.stroke-170"),sQuery(id+"F0.wireOp",EDGE,"E4.sketch_text.stroke-171"),sQuery(id+"F0.wireOp",EDGE,"E4.sketch_text.stroke-172"),sQuery(id+"F0.wireOp",EDGE,"E4.sketch_text.stroke-173"),sQuery(id+"F0.wireOp",EDGE,"E4.sketch_text.stroke-174"),sQuery(id+"F0.wireOp",EDGE,"E4.sketch_text.stroke-175"),sQuery(id+"F0.wireOp",EDGE,"E4.sketch_text.stroke-176"),sQuery(id+"F0.wireOp",EDGE,"E4.sketch_text.stroke-177"),sQuery(id+"F0.wireOp",EDGE,"E4.sketch_text.stroke-178"),sQuery(id+"F0.wireOp",EDGE,"E4.sketch_text.stroke-179"),sQuery(id+"F0.wireOp",EDGE,"E4.sketch_text.stroke-180"),sQuery(id+"F0.wireOp",EDGE,"E4.sketch_text.stroke-181"),sQuery(id+"F0.wireOp",EDGE,"E4.sketch_text.stroke-182"),sQuery(id+"F0.wireOp",EDGE,"E4.sketch_text.stroke-183"),sQuery(id+"F0.wireOp",EDGE,"E4.sketch_text.stroke-184"),sQuery(id+"F0.wireOp",EDGE,"E4.sketch_text.stroke-185"),sQuery(id+"F0.wireOp",EDGE,"E4.sketch_text.stroke-186"),sQuery(id+"F0.wireOp",EDGE,"E4.sketch_text.stroke-187"),sQuery(id+"F0.wireOp",EDGE,"E4.sketch_text.stroke-188"),sQuery(id+"F0.wireOp",EDGE,"E4.sketch_text.stroke-189"),sQuery(id+"F0.wireOp",EDGE,"E4.sketch_text.stroke-190"),sQuery(id+"F0.wireOp",EDGE,"E4.sketch_text.stroke-191"),sQuery(id+"F0.wireOp",EDGE,"E4.sketch_text.stroke-192"),sQuery(id+"F0.wireOp",EDGE,"E4.sketch_text.stroke-193"),sQuery(id+"F0.wireOp",EDGE,"E4.sketch_text.stroke-194"),sQuery(id+"F0.wireOp",EDGE,"E4.sketch_text.stroke-195"),sQuery(id+"F0.wireOp",EDGE,"E4.sketch_text.stroke-196"),sQuery(id+"F0.wireOp",EDGE,"E4.sketch_text.stroke-197"),sQuery(id+"F0.wireOp",EDGE,"E4.sketch_text.stroke-198"),sQuery(id+"F0.wireOp",EDGE,"E4.sketch_text.stroke-199"),sQuery(id+"F0.wireOp",EDGE,"E4.sketch_text.stroke-200"),sQuery(id+"F0.wireOp",EDGE,"E4.sketch_text.stroke-201"),sQuery(id+"F0.wireOp",EDGE,"E4.sketch_text.stroke-208"),sQuery(id+"F0.wireOp",EDGE,"E4.sketch_text.stroke-209"),sQuery(id+"F0.wireOp",EDGE,"E4.sketch_text.stroke-210"),sQuery(id+"F0.wireOp",EDGE,"E4.sketch_text.stroke-211"),sQuery(id+"F0.wireOp",EDGE,"E4.sketch_text.stroke-212"),sQuery(id+"F0.wireOp",EDGE,"E4.sketch_text.stroke-213"),sQuery(id+"F0.wireOp",EDGE,"E4.sketch_text.stroke-214"),sQuery(id+"F0.wireOp",EDGE,"E4.sketch_text.stroke-215"),sQuery(id+"F0.wireOp",EDGE,"E4.sketch_text.stroke-216"),sQuery(id+"F0.wireOp",EDGE,"E4.sketch_text.stroke-217"),sQuery(id+"F0.wireOp",EDGE,"E4.sketch_text.stroke-218"),sQuery(id+"F0.wireOp",EDGE,"E4.sketch_text.stroke-219"),sQuery(id+"F0.wireOp",EDGE,"E4.sketch_text.stroke-220"),sQuery(id+"F0.wireOp",EDGE,"E4.sketch_text.stroke-221"),sQuery(id+"F0.wireOp",EDGE,"E4.sketch_text.stroke-222"),sQuery(id+"F0.wireOp",EDGE,"E4.sketch_text.stroke-223"),sQuery(id+"F0.wireOp",EDGE,"E4.sketch_text.stroke-224"),sQuery(id+"F0.wireOp",EDGE,"E4.sketch_text.stroke-225"),sQuery(id+"F0.wireOp",EDGE,"E4.sketch_text.stroke-226"),sQuery(id+"F0.wireOp",EDGE,"E4.sketch_text.stroke-227"),sQuery(id+"F0.wireOp",EDGE,"E4.sketch_text.stroke-228"),sQuery(id+"F0.wireOp",EDGE,"E4.sketch_text.stroke-229"),sQuery(id+"F0.wireOp",EDGE,"E4.sketch_text.stroke-230"),sQuery(id+"F0.wireOp",EDGE,"E4.sketch_text.stroke-231"),sQuery(id+"F0.wireOp",EDGE,"E4.sketch_text.stroke-232"),sQuery(id+"F0.wireOp",EDGE,"E4.sketch_text.stroke-233"),sQuery(id+"F0.wireOp",EDGE,"E4.sketch_text.stroke-234"),sQuery(id+"F0.wireOp",EDGE,"E4.sketch_text.stroke-235"),sQuery(id+"F0.wireOp",EDGE,"E4.sketch_text.stroke-236"),sQuery(id+"F0.wireOp",EDGE,"E4.sketch_text.stroke-237"),sQuery(id+"F0.wireOp",EDGE,"E4.sketch_text.stroke-238"),sQuery(id+"F0.wireOp",EDGE,"E4.sketch_text.stroke-239"),sQuery(id+"F0.wireOp",EDGE,"E4.sketch_text.stroke-240"),sQuery(id+"F0.wireOp",EDGE,"E4.sketch_text.stroke-241"),sQuery(id+"F0.wireOp",EDGE,"E4.sketch_text.stroke-242"),sQuery(id+"F0.wireOp",EDGE,"E4.sketch_text.stroke-243"),sQuery(id+"F0.wireOp",EDGE,"E4.sketch_text.stroke-244"),sQuery(id+"F0.wireOp",EDGE,"E4.sketch_text.stroke-245"),sQuery(id+"F0.wireOp",EDGE,"E4.sketch_text.stroke-246"),sQuery(id+"F0.wireOp",EDGE,"E4.sketch_text.stroke-247"),sQuery(id+"F0.wireOp",EDGE,"E4.sketch_text.stroke-248"),sQuery(id+"F0.wireOp",EDGE,"E4.sketch_text.stroke-249"),sQuery(id+"F0.wireOp",EDGE,"E4.sketch_text.stroke-250"),sQuery(id+"F0.wireOp",EDGE,"E4.sketch_text.stroke-251"),sQuery(id+"F0.wireOp",EDGE,"E4.sketch_text.stroke-252"),sQuery(id+"F0.wireOp",EDGE,"E4.sketch_text.stroke-253"),sQuery(id+"F0.wireOp",EDGE,"E4.sketch_text.stroke-254"),sQuery(id+"F0.wireOp",EDGE,"E4.sketch_text.stroke-255"),sQuery(id+"F0.wireOp",EDGE,"E4.sketch_text.stroke-256"),sQuery(id+"F0.wireOp",EDGE,"E4.sketch_text.stroke-257"),sQuery(id+"F0.wireOp",EDGE,"E4.sketch_text.stroke-258"),sQuery(id+"F0.wireOp",EDGE,"E4.sketch_text.stroke-259"),sQuery(id+"F0.wireOp",EDGE,"E4.sketch_text.stroke-260"),sQuery(id+"F0.wireOp",EDGE,"E4.sketch_text.stroke-261"),sQuery(id+"F0.wireOp",EDGE,"E4.sketch_text.stroke-262"),sQuery(id+"F0.wireOp",EDGE,"E4.sketch_text.stroke-263"),sQuery(id+"F0.wireOp",EDGE,"E4.sketch_text.stroke-264"),sQuery(id+"F0.wireOp",EDGE,"E4.sketch_text.stroke-265"),sQuery(id+"F0.wireOp",EDGE,"E4.sketch_text.stroke-266"),sQuery(id+"F0.wireOp",EDGE,"E4.sketch_text.stroke-267"),sQuery(id+"F0.wireOp",EDGE,"E4.sketch_text.stroke-268"),sQuery(id+"F0.wireOp",EDGE,"E4.sketch_text.stroke-269"),sQuery(id+"F0.wireOp",EDGE,"E4.sketch_text.stroke-270"),sQuery(id+"F0.wireOp",EDGE,"E4.sketch_text.stroke-271"),sQuery(id+"F0.wireOp",EDGE,"E4.sketch_text.stroke-272"),sQuery(id+"F0.wireOp",EDGE,"E4.sketch_text.stroke-273"),sQuery(id+"F0.wireOp",EDGE,"E4.sketch_text.stroke-274"),sQuery(id+"F0.wireOp",EDGE,"E4.sketch_text.stroke-275"),sQuery(id+"F0.wireOp",EDGE,"E4.sketch_text.stroke-276"),sQuery(id+"F0.wireOp",EDGE,"E4.sketch_text.stroke-283"),sQuery(id+"F0.wireOp",EDGE,"E4.sketch_text.stroke-284"),sQuery(id+"F0.wireOp",EDGE,"E4.sketch_text.stroke-285"),sQuery(id+"F0.wireOp",EDGE,"E4.sketch_text.stroke-286"),sQuery(id+"F0.wireOp",EDGE,"E4.sketch_text.stroke-287"),sQuery(id+"F0.wireOp",EDGE,"E4.sketch_text.stroke-288"),sQuery(id+"F0.wireOp",EDGE,"E4.sketch_text.stroke-289"),sQuery(id+"F0.wireOp",EDGE,"E4.sketch_text.stroke-290"),sQuery(id+"F0.wireOp",EDGE,"E4.sketch_text.stroke-291"),sQuery(id+"F0.wireOp",EDGE,"E4.sketch_text.stroke-292"),sQuery(id+"F0.wireOp",EDGE,"E4.sketch_text.stroke-293"),sQuery(id+"F0.wireOp",EDGE,"E4.sketch_text.stroke-294"),sQuery(id+"F0.wireOp",EDGE,"E4.sketch_text.stroke-295"),sQuery(id+"F0.wireOp",EDGE,"E4.sketch_text.stroke-296"),sQuery(id+"F0.wireOp",EDGE,"E4.sketch_text.stroke-297"),sQuery(id+"F0.wireOp",EDGE,"E4.sketch_text.stroke-298"),sQuery(id+"F0.wireOp",EDGE,"E4.sketch_text.stroke-299"),sQuery(id+"F0.wireOp",EDGE,"E4.sketch_text.stroke-300"),sQuery(id+"F0.wireOp",EDGE,"E4.sketch_text.stroke-301"),sQuery(id+"F0.wireOp",EDGE,"E4.sketch_text.stroke-302"),sQuery(id+"F0.wireOp",EDGE,"E4.sketch_text.stroke-303"),sQuery(id+"F0.wireOp",EDGE,"E4.sketch_text.stroke-304"),sQuery(id+"F0.wireOp",EDGE,"E4.sketch_text.stroke-305"),sQuery(id+"F0.wireOp",EDGE,"E4.sketch_text.stroke-306"),sQuery(id+"F0.wireOp",EDGE,"E4.sketch_text.stroke-307"),sQuery(id+"F0.wireOp",EDGE,"E4.sketch_text.stroke-308"),sQuery(id+"F0.wireOp",EDGE,"E4.sketch_text.stroke-309"),sQuery(id+"F0.wireOp",EDGE,"E4.sketch_text.stroke-310"),sQuery(id+"F0.wireOp",EDGE,"E4.sketch_text.stroke-321"),sQuery(id+"F0.wireOp",EDGE,"E4.sketch_text.stroke-322"),sQuery(id+"F0.wireOp",EDGE,"E4.sketch_text.stroke-323"),sQuery(id+"F0.wireOp",EDGE,"E4.sketch_text.stroke-324"),sQuery(id+"F0.wireOp",EDGE,"E4.sketch_text.stroke-325"),sQuery(id+"F0.wireOp",EDGE,"E4.sketch_text.stroke-326"),sQuery(id+"F0.wireOp",EDGE,"E4.sketch_text.stroke-327"),sQuery(id+"F0.wireOp",EDGE,"E4.sketch_text.stroke-328"),sQuery(id+"F0.wireOp",EDGE,"E4.sketch_text.stroke-329"),sQuery(id+"F0.wireOp",EDGE,"E4.sketch_text.stroke-330"),sQuery(id+"F0.wireOp",EDGE,"E4.sketch_text.stroke-331"),sQuery(id+"F0.wireOp",EDGE,"E4.sketch_text.stroke-332"),sQuery(id+"F0.wireOp",EDGE,"E4.sketch_text.stroke-333"),sQuery(id+"F0.wireOp",EDGE,"E4.sketch_text.stroke-334"),sQuery(id+"F0.wireOp",EDGE,"E4.sketch_text.stroke-335"),sQuery(id+"F0.wireOp",EDGE,"E4.sketch_text.stroke-336"),sQuery(id+"F0.wireOp",EDGE,"E4.sketch_text.stroke-337"),sQuery(id+"F0.wireOp",EDGE,"E4.sketch_text.stroke-338"),sQuery(id+"F0.wireOp",EDGE,"E4.sketch_text.stroke-339"),sQuery(id+"F0.wireOp",EDGE,"E4.sketch_text.stroke-340"),sQuery(id+"F0.wireOp",EDGE,"E4.sketch_text.stroke-341"),sQuery(id+"F0.wireOp",EDGE,"E4.sketch_text.stroke-342"),sQuery(id+"F0.wireOp",EDGE,"E4.sketch_text.stroke-343"),sQuery(id+"F0.wireOp",EDGE,"E4.sketch_text.stroke-344"),sQuery(id+"F0.wireOp",EDGE,"E4.sketch_text.stroke-345"),sQuery(id+"F0.wireOp",EDGE,"E4.sketch_text.stroke-346"),sQuery(id+"F0.wireOp",EDGE,"E4.sketch_text.stroke-347"),sQuery(id+"F0.wireOp",EDGE,"E4.sketch_text.stroke-348"),sQuery(id+"F0.wireOp",EDGE,"E4.sketch_text.stroke-359"),sQuery(id+"F0.wireOp",EDGE,"E4.sketch_text.stroke-360"),sQuery(id+"F0.wireOp",EDGE,"E4.sketch_text.stroke-361"),sQuery(id+"F0.wireOp",EDGE,"E4.sketch_text.stroke-362"),sQuery(id+"F0.wireOp",EDGE,"E4.sketch_text.stroke-363"),sQuery(id+"F0.wireOp",EDGE,"E4.sketch_text.stroke-364"),sQuery(id+"F0.wireOp",EDGE,"E4.sketch_text.stroke-365"),sQuery(id+"F0.wireOp",EDGE,"E4.sketch_text.stroke-366"),sQuery(id+"F0.wireOp",EDGE,"E4.sketch_text.stroke-367"),sQuery(id+"F0.wireOp",EDGE,"E4.sketch_text.stroke-368"),sQuery(id+"F0.wireOp",EDGE,"E4.sketch_text.stroke-369"),sQuery(id+"F0.wireOp",EDGE,"E4.sketch_text.stroke-370"),sQuery(id+"F0.wireOp",EDGE,"E4.sketch_text.stroke-371"),sQuery(id+"F0.wireOp",EDGE,"E4.sketch_text.stroke-372"),sQuery(id+"F0.wireOp",EDGE,"E4.sketch_text.stroke-373"),sQuery(id+"F0.wireOp",EDGE,"E4.sketch_text.stroke-374"),sQuery(id+"F0.wireOp",EDGE,"E4.sketch_text.stroke-375"),sQuery(id+"F0.wireOp",EDGE,"E4.sketch_text.stroke-376"),sQuery(id+"F0.wireOp",EDGE,"E4.sketch_text.stroke-377"),sQuery(id+"F0.wireOp",EDGE,"E4.sketch_text.stroke-378"),sQuery(id+"F0.wireOp",EDGE,"E4.sketch_text.stroke-379"),sQuery(id+"F0.wireOp",EDGE,"E4.sketch_text.stroke-380"),sQuery(id+"F0.wireOp",EDGE,"E4.sketch_text.stroke-381"),sQuery(id+"F0.wireOp",EDGE,"E4.sketch_text.stroke-382"),sQuery(id+"F0.wireOp",EDGE,"E4.sketch_text.stroke-383"),sQuery(id+"F0.wireOp",EDGE,"E4.sketch_text.stroke-384"),sQuery(id+"F0.wireOp",EDGE,"E4.sketch_text.stroke-385"),sQuery(id+"F0.wireOp",EDGE,"E4.sketch_text.stroke-386"),sQuery(id+"F0.wireOp",EDGE,"E4.sketch_text.stroke-387"),sQuery(id+"F0.wireOp",EDGE,"E4.sketch_text.stroke-388"),sQuery(id+"F0.wireOp",EDGE,"E4.sketch_text.stroke-389"),sQuery(id+"F0.wireOp",EDGE,"E4.sketch_text.stroke-390"),sQuery(id+"F0.wireOp",EDGE,"E4.sketch_text.stroke-391"),sQuery(id+"F0.wireOp",EDGE,"E4.sketch_text.stroke-392")])],"isStart":true})],"blendedInto":[makeQuery(id+"F6.opExtrude","CAP_FACE",FACE,{"disambiguationData":[OSD([subQ1,sQuery(id+"F0.wireOp",EDGE,"E0.top"),subQ0,sQuery(id+"F0.wireOp",EDGE,"E0.right"),sQuery(id+"F0.wireOp",EDGE,"E3.sketch_text.stroke-0"),sQuery(id+"F0.wireOp",EDGE,"E3.sketch_text.stroke-1"),sQuery(id+"F0.wireOp",EDGE,"E3.sketch_text.stroke-2"),sQuery(id+"F0.wireOp",EDGE,"E3.sketch_text.stroke-3"),sQuery(id+"F0.wireOp",EDGE,"E3.sketch_text.stroke-4"),sQuery(id+"F0.wireOp",EDGE,"E3.sketch_text.stroke-5"),sQuery(id+"F0.wireOp",EDGE,"E3.sketch_text.stroke-6"),sQuery(id+"F0.wireOp",EDGE,"E3.sketch_text.stroke-7"),sQuery(id+"F0.wireOp",EDGE,"E3.sketch_text.stroke-8"),sQuery(id+"F0.wireOp",EDGE,"E3.sketch_text.stroke-9"),sQuery(id+"F0.wireOp",EDGE,"E3.sketch_text.stroke-10"),sQuery(id+"F0.wireOp",EDGE,"E3.sketch_text.stroke-11"),sQuery(id+"F0.wireOp",EDGE,"E3.sketch_text.stroke-12"),sQuery(id+"F0.wireOp",EDGE,"E3.sketch_text.stroke-13"),sQuery(id+"F0.wireOp",EDGE,"E3.sketch_text.stroke-14"),sQuery(id+"F0.wireOp",EDGE,"E3.sketch_text.stroke-15"),sQuery(id+"F0.wireOp",EDGE,"E3.sketch_text.stroke-16"),sQuery(id+"F0.wireOp",EDGE,"E3.sketch_text.stroke-17"),sQuery(id+"F0.wireOp",EDGE,"E3.sketch_text.stroke-18"),sQuery(id+"F0.wireOp",EDGE,"E3.sketch_text.stroke-19"),sQuery(id+"F0.wireOp",EDGE,"E3.sketch_text.stroke-20"),sQuery(id+"F0.wireOp",EDGE,"E3.sketch_text.stroke-21"),sQuery(id+"F0.wireOp",EDGE,"E3.sketch_text.stroke-22"),sQuery(id+"F0.wireOp",EDGE,"E3.sketch_text.stroke-23"),sQuery(id+"F0.wireOp",EDGE,"E3.sketch_text.stroke-24"),sQuery(id+"F0.wireOp",EDGE,"E3.sketch_text.stroke-25"),sQuery(id+"F0.wireOp",EDGE,"E3.sketch_text.stroke-26"),sQuery(id+"F0.wireOp",EDGE,"E3.sketch_text.stroke-27"),sQuery(id+"F0.wireOp",EDGE,"E3.sketch_text.stroke-28"),sQuery(id+"F0.wireOp",EDGE,"E3.sketch_text.stroke-29"),sQuery(id+"F0.wireOp",EDGE,"E3.sketch_text.stroke-30"),sQuery(id+"F0.wireOp",EDGE,"E3.sketch_text.stroke-31"),sQuery(id+"F0.wireOp",EDGE,"E3.sketch_text.stroke-32"),sQuery(id+"F0.wireOp",EDGE,"E3.sketch_text.stroke-33"),sQuery(id+"F0.wireOp",EDGE,"E3.sketch_text.stroke-34"),sQuery(id+"F0.wireOp",EDGE,"E3.sketch_text.stroke-35"),sQuery(id+"F0.wireOp",EDGE,"E3.sketch_text.stroke-36"),sQuery(id+"F0.wireOp",EDGE,"E3.sketch_text.stroke-37"),sQuery(id+"F0.wireOp",EDGE,"E3.sketch_text.stroke-38"),sQuery(id+"F0.wireOp",EDGE,"E3.sketch_text.stroke-39"),sQuery(id+"F0.wireOp",EDGE,"E3.sketch_text.stroke-40"),sQuery(id+"F0.wireOp",EDGE,"E3.sketch_text.stroke-41"),sQuery(id+"F0.wireOp",EDGE,"E3.sketch_text.stroke-42"),sQuery(id+"F0.wireOp",EDGE,"E3.sketch_text.stroke-43"),sQuery(id+"F0.wireOp",EDGE,"E3.sketch_text.stroke-44"),sQuery(id+"F0.wireOp",EDGE,"E3.sketch_text.stroke-45"),sQuery(id+"F0.wireOp",EDGE,"E3.sketch_text.stroke-46"),sQuery(id+"F0.wireOp",EDGE,"E3.sketch_text.stroke-47"),sQuery(id+"F0.wireOp",EDGE,"E3.sketch_text.stroke-48"),sQuery(id+"F0.wireOp",EDGE,"E3.sketch_text.stroke-49"),sQuery(id+"F0.wireOp",EDGE,"E3.sketch_text.stroke-50"),sQuery(id+"F0.wireOp",EDGE,"E3.sketch_text.stroke-51"),sQuery(id+"F0.wireOp",EDGE,"E3.sketch_text.stroke-52"),sQuery(id+"F0.wireOp",EDGE,"E3.sketch_text.stroke-53"),sQuery(id+"F0.wireOp",EDGE,"E3.sketch_text.stroke-54"),sQuery(id+"F0.wireOp",EDGE,"E3.sketch_text.stroke-55"),sQuery(id+"F0.wireOp",EDGE,"E3.sketch_text.stroke-56"),sQuery(id+"F0.wireOp",EDGE,"E3.sketch_text.stroke-57"),sQuery(id+"F0.wireOp",EDGE,"E3.sketch_text.stroke-58"),sQuery(id+"F0.wireOp",EDGE,"E3.sketch_text.stroke-59"),sQuery(id+"F0.wireOp",EDGE,"E3.sketch_text.stroke-60"),sQuery(id+"F0.wireOp",EDGE,"E3.sketch_text.stroke-61"),sQuery(id+"F0.wireOp",EDGE,"E3.sketch_text.stroke-62"),sQuery(id+"F0.wireOp",EDGE,"E3.sketch_text.stroke-63"),sQuery(id+"F0.wireOp",EDGE,"E3.sketch_text.stroke-64"),sQuery(id+"F0.wireOp",EDGE,"E3.sketch_text.stroke-65"),sQuery(id+"F0.wireOp",EDGE,"E3.sketch_text.stroke-66"),sQuery(id+"F0.wireOp",EDGE,"E3.sketch_text.stroke-67"),sQuery(id+"F0.wireOp",EDGE,"E3.sketch_text.stroke-68"),sQuery(id+"F0.wireOp",EDGE,"E3.sketch_text.stroke-69"),sQuery(id+"F0.wireOp",EDGE,"E3.sketch_text.stroke-70"),sQuery(id+"F0.wireOp",EDGE,"E3.sketch_text.stroke-71"),sQuery(id+"F0.wireOp",EDGE,"E3.sketch_text.stroke-72"),sQuery(id+"F0.wireOp",EDGE,"E3.sketch_text.stroke-73"),sQuery(id+"F0.wireOp",EDGE,"E3.sketch_text.stroke-74"),sQuery(id+"F0.wireOp",EDGE,"E3.sketch_text.stroke-88"),sQuery(id+"F0.wireOp",EDGE,"E3.sketch_text.stroke-89"),sQuery(id+"F0.wireOp",EDGE,"E3.sketch_text.stroke-90"),sQuery(id+"F0.wireOp",EDGE,"E3.sketch_text.stroke-91"),sQuery(id+"F0.wireOp",EDGE,"E3.sketch_text.stroke-92"),sQuery(id+"F0.wireOp",EDGE,"E3.sketch_text.stroke-93"),sQuery(id+"F0.wireOp",EDGE,"E3.sketch_text.stroke-94"),sQuery(id+"F0.wireOp",EDGE,"E3.sketch_text.stroke-95"),sQuery(id+"F0.wireOp",EDGE,"E3.sketch_text.stroke-96"),sQuery(id+"F0.wireOp",EDGE,"E3.sketch_text.stroke-97"),sQuery(id+"F0.wireOp",EDGE,"E3.sketch_text.stroke-98"),sQuery(id+"F0.wireOp",EDGE,"E3.sketch_text.stroke-99"),sQuery(id+"F0.wireOp",EDGE,"E3.sketch_text.stroke-106"),sQuery(id+"F0.wireOp",EDGE,"E3.sketch_text.stroke-107"),sQuery(id+"F0.wireOp",EDGE,"E3.sketch_text.stroke-108"),sQuery(id+"F0.wireOp",EDGE,"E3.sketch_text.stroke-109"),sQuery(id+"F0.wireOp",EDGE,"E3.sketch_text.stroke-110"),sQuery(id+"F0.wireOp",EDGE,"E3.sketch_text.stroke-111"),sQuery(id+"F0.wireOp",EDGE,"E3.sketch_text.stroke-112"),sQuery(id+"F0.wireOp",EDGE,"E3.sketch_text.stroke-113"),sQuery(id+"F0.wireOp",EDGE,"E3.sketch_text.stroke-114"),sQuery(id+"F0.wireOp",EDGE,"E3.sketch_text.stroke-115"),sQuery(id+"F0.wireOp",EDGE,"E3.sketch_text.stroke-116"),sQuery(id+"F0.wireOp",EDGE,"E3.sketch_text.stroke-117"),sQuery(id+"F0.wireOp",EDGE,"E3.sketch_text.stroke-118"),sQuery(id+"F0.wireOp",EDGE,"E3.sketch_text.stroke-119"),sQuery(id+"F0.wireOp",EDGE,"E3.sketch_text.stroke-120"),sQuery(id+"F0.wireOp",EDGE,"E3.sketch_text.stroke-121"),sQuery(id+"F0.wireOp",EDGE,"E3.sketch_text.stroke-122"),sQuery(id+"F0.wireOp",EDGE,"E3.sketch_text.stroke-123"),sQuery(id+"F0.wireOp",EDGE,"E3.sketch_text.stroke-124"),sQuery(id+"F0.wireOp",EDGE,"E3.sketch_text.stroke-125"),sQuery(id+"F0.wireOp",EDGE,"E3.sketch_text.stroke-126"),sQuery(id+"F0.wireOp",EDGE,"E3.sketch_text.stroke-127"),sQuery(id+"F0.wireOp",EDGE,"E3.sketch_text.stroke-128"),sQuery(id+"F0.wireOp",EDGE,"E3.sketch_text.stroke-129"),sQuery(id+"F0.wireOp",EDGE,"E3.sketch_text.stroke-130"),sQuery(id+"F0.wireOp",EDGE,"E3.sketch_text.stroke-131"),sQuery(id+"F0.wireOp",EDGE,"E3.sketch_text.stroke-132"),sQuery(id+"F0.wireOp",EDGE,"E3.sketch_text.stroke-133"),sQuery(id+"F0.wireOp",EDGE,"E3.sketch_text.stroke-134"),sQuery(id+"F0.wireOp",EDGE,"E3.sketch_text.stroke-135"),sQuery(id+"F0.wireOp",EDGE,"E3.sketch_text.stroke-136"),sQuery(id+"F0.wireOp",EDGE,"E3.sketch_text.stroke-137"),sQuery(id+"F0.wireOp",EDGE,"E3.sketch_text.stroke-138"),sQuery(id+"F0.wireOp",EDGE,"E3.sketch_text.stroke-139"),sQuery(id+"F0.wireOp",EDGE,"E3.sketch_text.stroke-140"),sQuery(id+"F0.wireOp",EDGE,"E3.sketch_text.stroke-141"),sQuery(id+"F0.wireOp",EDGE,"E3.sketch_text.stroke-142"),sQuery(id+"F0.wireOp",EDGE,"E3.sketch_text.stroke-143"),sQuery(id+"F0.wireOp",EDGE,"E3.sketch_text.stroke-144"),sQuery(id+"F0.wireOp",EDGE,"E3.sketch_text.stroke-145"),sQuery(id+"F0.wireOp",EDGE,"E3.sketch_text.stroke-146"),sQuery(id+"F0.wireOp",EDGE,"E3.sketch_text.stroke-147"),sQuery(id+"F0.wireOp",EDGE,"E3.sketch_text.stroke-155"),sQuery(id+"F0.wireOp",EDGE,"E3.sketch_text.stroke-156"),sQuery(id+"F0.wireOp",EDGE,"E3.sketch_text.stroke-157"),sQuery(id+"F0.wireOp",EDGE,"E3.sketch_text.stroke-158"),sQuery(id+"F0.wireOp",EDGE,"E3.sketch_text.stroke-159"),sQuery(id+"F0.wireOp",EDGE,"E3.sketch_text.stroke-160"),sQuery(id+"F0.wireOp",EDGE,"E3.sketch_text.stroke-161"),sQuery(id+"F0.wireOp",EDGE,"E3.sketch_text.stroke-162"),sQuery(id+"F0.wireOp",EDGE,"E3.sketch_text.stroke-163"),sQuery(id+"F0.wireOp",EDGE,"E3.sketch_text.stroke-164"),sQuery(id+"F0.wireOp",EDGE,"E3.sketch_text.stroke-165"),sQuery(id+"F0.wireOp",EDGE,"E3.sketch_text.stroke-166"),sQuery(id+"F0.wireOp",EDGE,"E3.sketch_text.stroke-167"),sQuery(id+"F0.wireOp",EDGE,"E3.sketch_text.stroke-168"),sQuery(id+"F0.wireOp",EDGE,"E3.sketch_text.stroke-169"),sQuery(id+"F0.wireOp",EDGE,"E3.sketch_text.stroke-170"),sQuery(id+"F0.wireOp",EDGE,"E3.sketch_text.stroke-171"),sQuery(id+"F0.wireOp",EDGE,"E3.sketch_text.stroke-172"),sQuery(id+"F0.wireOp",EDGE,"E3.sketch_text.stroke-173"),sQuery(id+"F0.wireOp",EDGE,"E3.sketch_text.stroke-174"),sQuery(id+"F0.wireOp",EDGE,"E3.sketch_text.stroke-175"),sQuery(id+"F0.wireOp",EDGE,"E3.sketch_text.stroke-176"),sQuery(id+"F0.wireOp",EDGE,"E3.sketch_text.stroke-177"),sQuery(id+"F0.wireOp",EDGE,"E3.sketch_text.stroke-178"),sQuery(id+"F0.wireOp",EDGE,"E3.sketch_text.stroke-179"),sQuery(id+"F0.wireOp",EDGE,"E3.sketch_text.stroke-180"),sQuery(id+"F0.wireOp",EDGE,"E3.sketch_text.stroke-181"),sQuery(id+"F0.wireOp",EDGE,"E3.sketch_text.stroke-182"),sQuery(id+"F0.wireOp",EDGE,"E3.sketch_text.stroke-183"),sQuery(id+"F0.wireOp",EDGE,"E3.sketch_text.stroke-184"),sQuery(id+"F0.wireOp",EDGE,"E3.sketch_text.stroke-185"),sQuery(id+"F0.wireOp",EDGE,"E3.sketch_text.stroke-186"),sQuery(id+"F0.wireOp",EDGE,"E3.sketch_text.stroke-187"),sQuery(id+"F0.wireOp",EDGE,"E3.sketch_text.stroke-188"),sQuery(id+"F0.wireOp",EDGE,"E3.sketch_text.stroke-189"),sQuery(id+"F0.wireOp",EDGE,"E3.sketch_text.stroke-190"),sQuery(id+"F0.wireOp",EDGE,"E3.sketch_text.stroke-191"),sQuery(id+"F0.wireOp",EDGE,"E3.sketch_text.stroke-192"),sQuery(id+"F0.wireOp",EDGE,"E3.sketch_text.stroke-193"),sQuery(id+"F0.wireOp",EDGE,"E3.sketch_text.stroke-194"),sQuery(id+"F0.wireOp",EDGE,"E3.sketch_text.stroke-195"),sQuery(id+"F0.wireOp",EDGE,"E3.sketch_text.stroke-196"),sQuery(id+"F0.wireOp",EDGE,"E3.sketch_text.stroke-197"),sQuery(id+"F0.wireOp",EDGE,"E3.sketch_text.stroke-198"),sQuery(id+"F0.wireOp",EDGE,"E3.sketch_text.stroke-199"),sQuery(id+"F0.wireOp",EDGE,"E3.sketch_text.stroke-200"),sQuery(id+"F0.wireOp",EDGE,"E3.sketch_text.stroke-201"),sQuery(id+"F0.wireOp",EDGE,"E3.sketch_text.stroke-202"),sQuery(id+"F0.wireOp",EDGE,"E3.sketch_text.stroke-203"),sQuery(id+"F0.wireOp",EDGE,"E3.sketch_text.stroke-204"),sQuery(id+"F0.wireOp",EDGE,"E3.sketch_text.stroke-205"),sQuery(id+"F0.wireOp",EDGE,"E3.sketch_text.stroke-206"),sQuery(id+"F0.wireOp",EDGE,"E3.sketch_text.stroke-207"),sQuery(id+"F0.wireOp",EDGE,"E3.sketch_text.stroke-208"),sQuery(id+"F0.wireOp",EDGE,"E3.sketch_text.stroke-209"),sQuery(id+"F0.wireOp",EDGE,"E3.sketch_text.stroke-210"),sQuery(id+"F0.wireOp",EDGE,"E3.sketch_text.stroke-211"),sQuery(id+"F0.wireOp",EDGE,"E3.sketch_text.stroke-212"),sQuery(id+"F0.wireOp",EDGE,"E3.sketch_text.stroke-213"),sQuery(id+"F0.wireOp",EDGE,"E3.sketch_text.stroke-214"),sQuery(id+"F0.wireOp",EDGE,"E3.sketch_text.stroke-215"),sQuery(id+"F0.wireOp",EDGE,"E3.sketch_text.stroke-216"),sQuery(id+"F0.wireOp",EDGE,"E3.sketch_text.stroke-217"),sQuery(id+"F0.wireOp",EDGE,"E3.sketch_text.stroke-218"),sQuery(id+"F0.wireOp",EDGE,"E3.sketch_text.stroke-219"),sQuery(id+"F0.wireOp",EDGE,"E3.sketch_text.stroke-220"),sQuery(id+"F0.wireOp",EDGE,"E3.sketch_text.stroke-221"),sQuery(id+"F0.wireOp",EDGE,"E3.sketch_text.stroke-222"),sQuery(id+"F0.wireOp",EDGE,"E3.sketch_text.stroke-223"),sQuery(id+"F0.wireOp",EDGE,"E3.sketch_text.stroke-224"),sQuery(id+"F0.wireOp",EDGE,"E3.sketch_text.stroke-225"),sQuery(id+"F0.wireOp",EDGE,"E3.sketch_text.stroke-226"),sQuery(id+"F0.wireOp",EDGE,"E3.sketch_text.stroke-227"),sQuery(id+"F0.wireOp",EDGE,"E3.sketch_text.stroke-228"),sQuery(id+"F0.wireOp",EDGE,"E3.sketch_text.stroke-229"),sQuery(id+"F0.wireOp",EDGE,"E3.sketch_text.stroke-230"),sQuery(id+"F0.wireOp",EDGE,"E3.sketch_text.stroke-231"),sQuery(id+"F0.wireOp",EDGE,"E3.sketch_text.stroke-232"),sQuery(id+"F0.wireOp",EDGE,"E3.sketch_text.stroke-233"),sQuery(id+"F0.wireOp",EDGE,"E3.sketch_text.stroke-234"),sQuery(id+"F0.wireOp",EDGE,"E3.sketch_text.stroke-235"),sQuery(id+"F0.wireOp",EDGE,"E3.sketch_text.stroke-236"),sQuery(id+"F0.wireOp",EDGE,"E3.sketch_text.stroke-237"),sQuery(id+"F0.wireOp",EDGE,"E3.sketch_text.stroke-238"),sQuery(id+"F0.wireOp",EDGE,"E3.sketch_text.stroke-244"),sQuery(id+"F0.wireOp",EDGE,"E3.sketch_text.stroke-245"),sQuery(id+"F0.wireOp",EDGE,"E3.sketch_text.stroke-246"),sQuery(id+"F0.wireOp",EDGE,"E3.sketch_text.stroke-247"),sQuery(id+"F0.wireOp",EDGE,"E3.sketch_text.stroke-248"),sQuery(id+"F0.wireOp",EDGE,"E3.sketch_text.stroke-249"),sQuery(id+"F0.wireOp",EDGE,"E3.sketch_text.stroke-250"),sQuery(id+"F0.wireOp",EDGE,"E3.sketch_text.stroke-251"),sQuery(id+"F0.wireOp",EDGE,"E3.sketch_text.stroke-252"),sQuery(id+"F0.wireOp",EDGE,"E3.sketch_text.stroke-253"),sQuery(id+"F0.wireOp",EDGE,"E3.sketch_text.stroke-254"),sQuery(id+"F0.wireOp",EDGE,"E3.sketch_text.stroke-255"),sQuery(id+"F0.wireOp",EDGE,"E3.sketch_text.stroke-256"),sQuery(id+"F0.wireOp",EDGE,"E3.sketch_text.stroke-257"),sQuery(id+"F0.wireOp",EDGE,"E3.sketch_text.stroke-258"),sQuery(id+"F0.wireOp",EDGE,"E3.sketch_text.stroke-259"),sQuery(id+"F0.wireOp",EDGE,"E3.sketch_text.stroke-260"),sQuery(id+"F0.wireOp",EDGE,"E4.sketch_text.stroke-0"),sQuery(id+"F0.wireOp",EDGE,"E4.sketch_text.stroke-1"),sQuery(id+"F0.wireOp",EDGE,"E4.sketch_text.stroke-2"),sQuery(id+"F0.wireOp",EDGE,"E4.sketch_text.stroke-3"),sQuery(id+"F0.wireOp",EDGE,"E4.sketch_text.stroke-4"),sQuery(id+"F0.wireOp",EDGE,"E4.sketch_text.stroke-5"),sQuery(id+"F0.wireOp",EDGE,"E4.sketch_text.stroke-6"),sQuery(id+"F0.wireOp",EDGE,"E4.sketch_text.stroke-7"),sQuery(id+"F0.wireOp",EDGE,"E4.sketch_text.stroke-8"),sQuery(id+"F0.wireOp",EDGE,"E4.sketch_text.stroke-9"),sQuery(id+"F0.wireOp",EDGE,"E4.sketch_text.stroke-10"),sQuery(id+"F0.wireOp",EDGE,"E4.sketch_text.stroke-11"),sQuery(id+"F0.wireOp",EDGE,"E4.sketch_text.stroke-12"),sQuery(id+"F0.wireOp",EDGE,"E4.sketch_text.stroke-13"),sQuery(id+"F0.wireOp",EDGE,"E4.sketch_text.stroke-14"),sQuery(id+"F0.wireOp",EDGE,"E4.sketch_text.stroke-15"),sQuery(id+"F0.wireOp",EDGE,"E4.sketch_text.stroke-16"),sQuery(id+"F0.wireOp",EDGE,"E4.sketch_text.stroke-17"),sQuery(id+"F0.wireOp",EDGE,"E4.sketch_text.stroke-18"),sQuery(id+"F0.wireOp",EDGE,"E4.sketch_text.stroke-19"),sQuery(id+"F0.wireOp",EDGE,"E4.sketch_text.stroke-20"),sQuery(id+"F0.wireOp",EDGE,"E4.sketch_text.stroke-21"),sQuery(id+"F0.wireOp",EDGE,"E4.sketch_text.stroke-28"),sQuery(id+"F0.wireOp",EDGE,"E4.sketch_text.stroke-29"),sQuery(id+"F0.wireOp",EDGE,"E4.sketch_text.stroke-30"),sQuery(id+"F0.wireOp",EDGE,"E4.sketch_text.stroke-31"),sQuery(id+"F0.wireOp",EDGE,"E4.sketch_text.stroke-32"),sQuery(id+"F0.wireOp",EDGE,"E4.sketch_text.stroke-33"),sQuery(id+"F0.wireOp",EDGE,"E4.sketch_text.stroke-34"),sQuery(id+"F0.wireOp",EDGE,"E4.sketch_text.stroke-35"),sQuery(id+"F0.wireOp",EDGE,"E4.sketch_text.stroke-36"),sQuery(id+"F0.wireOp",EDGE,"E4.sketch_text.stroke-37"),sQuery(id+"F0.wireOp",EDGE,"E4.sketch_text.stroke-38"),sQuery(id+"F0.wireOp",EDGE,"E4.sketch_text.stroke-39"),sQuery(id+"F0.wireOp",EDGE,"E4.sketch_text.stroke-40"),sQuery(id+"F0.wireOp",EDGE,"E4.sketch_text.stroke-41"),sQuery(id+"F0.wireOp",EDGE,"E4.sketch_text.stroke-42"),sQuery(id+"F0.wireOp",EDGE,"E4.sketch_text.stroke-43"),sQuery(id+"F0.wireOp",EDGE,"E4.sketch_text.stroke-44"),sQuery(id+"F0.wireOp",EDGE,"E4.sketch_text.stroke-45"),sQuery(id+"F0.wireOp",EDGE,"E4.sketch_text.stroke-46"),sQuery(id+"F0.wireOp",EDGE,"E4.sketch_text.stroke-47"),sQuery(id+"F0.wireOp",EDGE,"E4.sketch_text.stroke-48"),sQuery(id+"F0.wireOp",EDGE,"E4.sketch_text.stroke-49"),sQuery(id+"F0.wireOp",EDGE,"E4.sketch_text.stroke-50"),sQuery(id+"F0.wireOp",EDGE,"E4.sketch_text.stroke-51"),sQuery(id+"F0.wireOp",EDGE,"E4.sketch_text.stroke-52"),sQuery(id+"F0.wireOp",EDGE,"E4.sketch_text.stroke-53"),sQuery(id+"F0.wireOp",EDGE,"E4.sketch_text.stroke-54"),sQuery(id+"F0.wireOp",EDGE,"E4.sketch_text.stroke-55"),sQuery(id+"F0.wireOp",EDGE,"E4.sketch_text.stroke-56"),sQuery(id+"F0.wireOp",EDGE,"E4.sketch_text.stroke-57"),sQuery(id+"F0.wireOp",EDGE,"E4.sketch_text.stroke-58"),sQuery(id+"F0.wireOp",EDGE,"E4.sketch_text.stroke-59"),sQuery(id+"F0.wireOp",EDGE,"E4.sketch_text.stroke-60"),sQuery(id+"F0.wireOp",EDGE,"E4.sketch_text.stroke-61"),sQuery(id+"F0.wireOp",EDGE,"E4.sketch_text.stroke-62"),sQuery(id+"F0.wireOp",EDGE,"E4.sketch_text.stroke-63"),sQuery(id+"F0.wireOp",EDGE,"E4.sketch_text.stroke-64"),sQuery(id+"F0.wireOp",EDGE,"E4.sketch_text.stroke-65"),sQuery(id+"F0.wireOp",EDGE,"E4.sketch_text.stroke-66"),sQuery(id+"F0.wireOp",EDGE,"E4.sketch_text.stroke-67"),sQuery(id+"F0.wireOp",EDGE,"E4.sketch_text.stroke-68"),sQuery(id+"F0.wireOp",EDGE,"E4.sketch_text.stroke-69"),sQuery(id+"F0.wireOp",EDGE,"E4.sketch_text.stroke-70"),sQuery(id+"F0.wireOp",EDGE,"E4.sketch_text.stroke-71"),sQuery(id+"F0.wireOp",EDGE,"E4.sketch_text.stroke-72"),sQuery(id+"F0.wireOp",EDGE,"E4.sketch_text.stroke-73"),sQuery(id+"F0.wireOp",EDGE,"E4.sketch_text.stroke-74"),sQuery(id+"F0.wireOp",EDGE,"E4.sketch_text.stroke-85"),sQuery(id+"F0.wireOp",EDGE,"E4.sketch_text.stroke-86"),sQuery(id+"F0.wireOp",EDGE,"E4.sketch_text.stroke-87"),sQuery(id+"F0.wireOp",EDGE,"E4.sketch_text.stroke-88"),sQuery(id+"F0.wireOp",EDGE,"E4.sketch_text.stroke-89"),sQuery(id+"F0.wireOp",EDGE,"E4.sketch_text.stroke-90"),sQuery(id+"F0.wireOp",EDGE,"E4.sketch_text.stroke-91"),sQuery(id+"F0.wireOp",EDGE,"E4.sketch_text.stroke-92"),sQuery(id+"F0.wireOp",EDGE,"E4.sketch_text.stroke-93"),sQuery(id+"F0.wireOp",EDGE,"E4.sketch_text.stroke-94"),sQuery(id+"F0.wireOp",EDGE,"E4.sketch_text.stroke-95"),sQuery(id+"F0.wireOp",EDGE,"E4.sketch_text.stroke-96"),sQuery(id+"F0.wireOp",EDGE,"E4.sketch_text.stroke-97"),sQuery(id+"F0.wireOp",EDGE,"E4.sketch_text.stroke-98"),sQuery(id+"F0.wireOp",EDGE,"E4.sketch_text.stroke-99"),sQuery(id+"F0.wireOp",EDGE,"E4.sketch_text.stroke-100"),sQuery(id+"F0.wireOp",EDGE,"E4.sketch_text.stroke-101"),sQuery(id+"F0.wireOp",EDGE,"E4.sketch_text.stroke-102"),sQuery(id+"F0.wireOp",EDGE,"E4.sketch_text.stroke-103"),sQuery(id+"F0.wireOp",EDGE,"E4.sketch_text.stroke-104"),sQuery(id+"F0.wireOp",EDGE,"E4.sketch_text.stroke-105"),sQuery(id+"F0.wireOp",EDGE,"E4.sketch_text.stroke-106"),sQuery(id+"F0.wireOp",EDGE,"E4.sketch_text.stroke-107"),sQuery(id+"F0.wireOp",EDGE,"E4.sketch_text.stroke-108"),sQuery(id+"F0.wireOp",EDGE,"E4.sketch_text.stroke-109"),sQuery(id+"F0.wireOp",EDGE,"E4.sketch_text.stroke-110"),sQuery(id+"F0.wireOp",EDGE,"E4.sketch_text.stroke-111"),sQuery(id+"F0.wireOp",EDGE,"E4.sketch_text.stroke-112"),sQuery(id+"F0.wireOp",EDGE,"E4.sketch_text.stroke-113"),sQuery(id+"F0.wireOp",EDGE,"E4.sketch_text.stroke-114"),sQuery(id+"F0.wireOp",EDGE,"E4.sketch_text.stroke-115"),sQuery(id+"F0.wireOp",EDGE,"E4.sketch_text.stroke-116"),sQuery(id+"F0.wireOp",EDGE,"E4.sketch_text.stroke-117"),sQuery(id+"F0.wireOp",EDGE,"E4.sketch_text.stroke-118"),sQuery(id+"F0.wireOp",EDGE,"E4.sketch_text.stroke-119"),sQuery(id+"F0.wireOp",EDGE,"E4.sketch_text.stroke-120"),sQuery(id+"F0.wireOp",EDGE,"E4.sketch_text.stroke-121"),sQuery(id+"F0.wireOp",EDGE,"E4.sketch_text.stroke-122"),sQuery(id+"F0.wireOp",EDGE,"E4.sketch_text.stroke-123"),sQuery(id+"F0.wireOp",EDGE,"E4.sketch_text.stroke-124"),sQuery(id+"F0.wireOp",EDGE,"E4.sketch_text.stroke-138"),sQuery(id+"F0.wireOp",EDGE,"E4.sketch_text.stroke-139"),sQuery(id+"F0.wireOp",EDGE,"E4.sketch_text.stroke-140"),sQuery(id+"F0.wireOp",EDGE,"E4.sketch_text.stroke-141"),sQuery(id+"F0.wireOp",EDGE,"E4.sketch_text.stroke-142"),sQuery(id+"F0.wireOp",EDGE,"E4.sketch_text.stroke-143"),sQuery(id+"F0.wireOp",EDGE,"E4.sketch_text.stroke-144"),sQuery(id+"F0.wireOp",EDGE,"E4.sketch_text.stroke-145"),sQuery(id+"F0.wireOp",EDGE,"E4.sketch_text.stroke-146"),sQuery(id+"F0.wireOp",EDGE,"E4.sketch_text.stroke-147"),sQuery(id+"F0.wireOp",EDGE,"E4.sketch_text.stroke-148"),sQuery(id+"F0.wireOp",EDGE,"E4.sketch_text.stroke-149"),sQuery(id+"F0.wireOp",EDGE,"E4.sketch_text.stroke-156"),sQuery(id+"F0.wireOp",EDGE,"E4.sketch_text.stroke-157"),sQuery(id+"F0.wireOp",EDGE,"E4.sketch_text.stroke-158"),sQuery(id+"F0.wireOp",EDGE,"E4.sketch_text.stroke-159"),sQuery(id+"F0.wireOp",EDGE,"E4.sketch_text.stroke-160"),sQuery(id+"F0.wireOp",EDGE,"E4.sketch_text.stroke-161"),sQuery(id+"F0.wireOp",EDGE,"E4.sketch_text.stroke-162"),sQuery(id+"F0.wireOp",EDGE,"E4.sketch_text.stroke-163"),sQuery(id+"F0.wireOp",EDGE,"E4.sketch_text.stroke-164"),sQuery(id+"F0.wireOp",EDGE,"E4.sketch_text.stroke-165"),sQuery(id+"F0.wireOp",EDGE,"E4.sketch_text.stroke-166"),sQuery(id+"F0.wireOp",EDGE,"E4.sketch_text.stroke-167"),sQuery(id+"F0.wireOp",EDGE,"E4.sketch_text.stroke-168"),sQuery(id+"F0.wireOp",EDGE,"E4.sketch_text.stroke-169"),sQuery(id+"F0.wireOp",EDGE,"E4.sketch_text.stroke-170"),sQuery(id+"F0.wireOp",EDGE,"E4.sketch_text.stroke-171"),sQuery(id+"F0.wireOp",EDGE,"E4.sketch_text.stroke-172"),sQuery(id+"F0.wireOp",EDGE,"E4.sketch_text.stroke-173"),sQuery(id+"F0.wireOp",EDGE,"E4.sketch_text.stroke-174"),sQuery(id+"F0.wireOp",EDGE,"E4.sketch_text.stroke-175"),sQuery(id+"F0.wireOp",EDGE,"E4.sketch_text.stroke-176"),sQuery(id+"F0.wireOp",EDGE,"E4.sketch_text.stroke-177"),sQuery(id+"F0.wireOp",EDGE,"E4.sketch_text.stroke-178"),sQuery(id+"F0.wireOp",EDGE,"E4.sketch_text.stroke-179"),sQuery(id+"F0.wireOp",EDGE,"E4.sketch_text.stroke-180"),sQuery(id+"F0.wireOp",EDGE,"E4.sketch_text.stroke-181"),sQuery(id+"F0.wireOp",EDGE,"E4.sketch_text.stroke-182"),sQuery(id+"F0.wireOp",EDGE,"E4.sketch_text.stroke-183"),sQuery(id+"F0.wireOp",EDGE,"E4.sketch_text.stroke-184"),sQuery(id+"F0.wireOp",EDGE,"E4.sketch_text.stroke-185"),sQuery(id+"F0.wireOp",EDGE,"E4.sketch_text.stroke-186"),sQuery(id+"F0.wireOp",EDGE,"E4.sketch_text.stroke-187"),sQuery(id+"F0.wireOp",EDGE,"E4.sketch_text.stroke-188"),sQuery(id+"F0.wireOp",EDGE,"E4.sketch_text.stroke-189"),sQuery(id+"F0.wireOp",EDGE,"E4.sketch_text.stroke-190"),sQuery(id+"F0.wireOp",EDGE,"E4.sketch_text.stroke-191"),sQuery(id+"F0.wireOp",EDGE,"E4.sketch_text.stroke-192"),sQuery(id+"F0.wireOp",EDGE,"E4.sketch_text.stroke-193"),sQuery(id+"F0.wireOp",EDGE,"E4.sketch_text.stroke-194"),sQuery(id+"F0.wireOp",EDGE,"E4.sketch_text.stroke-195"),sQuery(id+"F0.wireOp",EDGE,"E4.sketch_text.stroke-196"),sQuery(id+"F0.wireOp",EDGE,"E4.sketch_text.stroke-197"),sQuery(id+"F0.wireOp",EDGE,"E4.sketch_text.stroke-198"),sQuery(id+"F0.wireOp",EDGE,"E4.sketch_text.stroke-199"),sQuery(id+"F0.wireOp",EDGE,"E4.sketch_text.stroke-200"),sQuery(id+"F0.wireOp",EDGE,"E4.sketch_text.stroke-201"),sQuery(id+"F0.wireOp",EDGE,"E4.sketch_text.stroke-208"),sQuery(id+"F0.wireOp",EDGE,"E4.sketch_text.stroke-209"),sQuery(id+"F0.wireOp",EDGE,"E4.sketch_text.stroke-210"),sQuery(id+"F0.wireOp",EDGE,"E4.sketch_text.stroke-211"),sQuery(id+"F0.wireOp",EDGE,"E4.sketch_text.stroke-212"),sQuery(id+"F0.wireOp",EDGE,"E4.sketch_text.stroke-213"),sQuery(id+"F0.wireOp",EDGE,"E4.sketch_text.stroke-214"),sQuery(id+"F0.wireOp",EDGE,"E4.sketch_text.stroke-215"),sQuery(id+"F0.wireOp",EDGE,"E4.sketch_text.stroke-216"),sQuery(id+"F0.wireOp",EDGE,"E4.sketch_text.stroke-217"),sQuery(id+"F0.wireOp",EDGE,"E4.sketch_text.stroke-218"),sQuery(id+"F0.wireOp",EDGE,"E4.sketch_text.stroke-219"),sQuery(id+"F0.wireOp",EDGE,"E4.sketch_text.stroke-220"),sQuery(id+"F0.wireOp",EDGE,"E4.sketch_text.stroke-221"),sQuery(id+"F0.wireOp",EDGE,"E4.sketch_text.stroke-222"),sQuery(id+"F0.wireOp",EDGE,"E4.sketch_text.stroke-223"),sQuery(id+"F0.wireOp",EDGE,"E4.sketch_text.stroke-224"),sQuery(id+"F0.wireOp",EDGE,"E4.sketch_text.stroke-225"),sQuery(id+"F0.wireOp",EDGE,"E4.sketch_text.stroke-226"),sQuery(id+"F0.wireOp",EDGE,"E4.sketch_text.stroke-227"),sQuery(id+"F0.wireOp",EDGE,"E4.sketch_text.stroke-228"),sQuery(id+"F0.wireOp",EDGE,"E4.sketch_text.stroke-229"),sQuery(id+"F0.wireOp",EDGE,"E4.sketch_text.stroke-230"),sQuery(id+"F0.wireOp",EDGE,"E4.sketch_text.stroke-231"),sQuery(id+"F0.wireOp",EDGE,"E4.sketch_text.stroke-232"),sQuery(id+"F0.wireOp",EDGE,"E4.sketch_text.stroke-233"),sQuery(id+"F0.wireOp",EDGE,"E4.sketch_text.stroke-234"),sQuery(id+"F0.wireOp",EDGE,"E4.sketch_text.stroke-235"),sQuery(id+"F0.wireOp",EDGE,"E4.sketch_text.stroke-236"),sQuery(id+"F0.wireOp",EDGE,"E4.sketch_text.stroke-237"),sQuery(id+"F0.wireOp",EDGE,"E4.sketch_text.stroke-238"),sQuery(id+"F0.wireOp",EDGE,"E4.sketch_text.stroke-239"),sQuery(id+"F0.wireOp",EDGE,"E4.sketch_text.stroke-240"),sQuery(id+"F0.wireOp",EDGE,"E4.sketch_text.stroke-241"),sQuery(id+"F0.wireOp",EDGE,"E4.sketch_text.stroke-242"),sQuery(id+"F0.wireOp",EDGE,"E4.sketch_text.stroke-243"),sQuery(id+"F0.wireOp",EDGE,"E4.sketch_text.stroke-244"),sQuery(id+"F0.wireOp",EDGE,"E4.sketch_text.stroke-245"),sQuery(id+"F0.wireOp",EDGE,"E4.sketch_text.stroke-246"),sQuery(id+"F0.wireOp",EDGE,"E4.sketch_text.stroke-247"),sQuery(id+"F0.wireOp",EDGE,"E4.sketch_text.stroke-248"),sQuery(id+"F0.wireOp",EDGE,"E4.sketch_text.stroke-249"),sQuery(id+"F0.wireOp",EDGE,"E4.sketch_text.stroke-250"),sQuery(id+"F0.wireOp",EDGE,"E4.sketch_text.stroke-251"),sQuery(id+"F0.wireOp",EDGE,"E4.sketch_text.stroke-252"),sQuery(id+"F0.wireOp",EDGE,"E4.sketch_text.stroke-253"),sQuery(id+"F0.wireOp",EDGE,"E4.sketch_text.stroke-254"),sQuery(id+"F0.wireOp",EDGE,"E4.sketch_text.stroke-255"),sQuery(id+"F0.wireOp",EDGE,"E4.sketch_text.stroke-256"),sQuery(id+"F0.wireOp",EDGE,"E4.sketch_text.stroke-257"),sQuery(id+"F0.wireOp",EDGE,"E4.sketch_text.stroke-258"),sQuery(id+"F0.wireOp",EDGE,"E4.sketch_text.stroke-259"),sQuery(id+"F0.wireOp",EDGE,"E4.sketch_text.stroke-260"),sQuery(id+"F0.wireOp",EDGE,"E4.sketch_text.stroke-261"),sQuery(id+"F0.wireOp",EDGE,"E4.sketch_text.stroke-262"),sQuery(id+"F0.wireOp",EDGE,"E4.sketch_text.stroke-263"),sQuery(id+"F0.wireOp",EDGE,"E4.sketch_text.stroke-264"),sQuery(id+"F0.wireOp",EDGE,"E4.sketch_text.stroke-265"),sQuery(id+"F0.wireOp",EDGE,"E4.sketch_text.stroke-266"),sQuery(id+"F0.wireOp",EDGE,"E4.sketch_text.stroke-267"),sQuery(id+"F0.wireOp",EDGE,"E4.sketch_text.stroke-268"),sQuery(id+"F0.wireOp",EDGE,"E4.sketch_text.stroke-269"),sQuery(id+"F0.wireOp",EDGE,"E4.sketch_text.stroke-270"),sQuery(id+"F0.wireOp",EDGE,"E4.sketch_text.stroke-271"),sQuery(id+"F0.wireOp",EDGE,"E4.sketch_text.stroke-272"),sQuery(id+"F0.wireOp",EDGE,"E4.sketch_text.stroke-273"),sQuery(id+"F0.wireOp",EDGE,"E4.sketch_text.stroke-274"),sQuery(id+"F0.wireOp",EDGE,"E4.sketch_text.stroke-275"),sQuery(id+"F0.wireOp",EDGE,"E4.sketch_text.stroke-276"),sQuery(id+"F0.wireOp",EDGE,"E4.sketch_text.stroke-283"),sQuery(id+"F0.wireOp",EDGE,"E4.sketch_text.stroke-284"),sQuery(id+"F0.wireOp",EDGE,"E4.sketch_text.stroke-285"),sQuery(id+"F0.wireOp",EDGE,"E4.sketch_text.stroke-286"),sQuery(id+"F0.wireOp",EDGE,"E4.sketch_text.stroke-287"),sQuery(id+"F0.wireOp",EDGE,"E4.sketch_text.stroke-288"),sQuery(id+"F0.wireOp",EDGE,"E4.sketch_text.stroke-289"),sQuery(id+"F0.wireOp",EDGE,"E4.sketch_text.stroke-290"),sQuery(id+"F0.wireOp",EDGE,"E4.sketch_text.stroke-291"),sQuery(id+"F0.wireOp",EDGE,"E4.sketch_text.stroke-292"),sQuery(id+"F0.wireOp",EDGE,"E4.sketch_text.stroke-293"),sQuery(id+"F0.wireOp",EDGE,"E4.sketch_text.stroke-294"),sQuery(id+"F0.wireOp",EDGE,"E4.sketch_text.stroke-295"),sQuery(id+"F0.wireOp",EDGE,"E4.sketch_text.stroke-296"),sQuery(id+"F0.wireOp",EDGE,"E4.sketch_text.stroke-297"),sQuery(id+"F0.wireOp",EDGE,"E4.sketch_text.stroke-298"),sQuery(id+"F0.wireOp",EDGE,"E4.sketch_text.stroke-299"),sQuery(id+"F0.wireOp",EDGE,"E4.sketch_text.stroke-300"),sQuery(id+"F0.wireOp",EDGE,"E4.sketch_text.stroke-301"),sQuery(id+"F0.wireOp",EDGE,"E4.sketch_text.stroke-302"),sQuery(id+"F0.wireOp",EDGE,"E4.sketch_text.stroke-303"),sQuery(id+"F0.wireOp",EDGE,"E4.sketch_text.stroke-304"),sQuery(id+"F0.wireOp",EDGE,"E4.sketch_text.stroke-305"),sQuery(id+"F0.wireOp",EDGE,"E4.sketch_text.stroke-306"),sQuery(id+"F0.wireOp",EDGE,"E4.sketch_text.stroke-307"),sQuery(id+"F0.wireOp",EDGE,"E4.sketch_text.stroke-308"),sQuery(id+"F0.wireOp",EDGE,"E4.sketch_text.stroke-309"),sQuery(id+"F0.wireOp",EDGE,"E4.sketch_text.stroke-310"),sQuery(id+"F0.wireOp",EDGE,"E4.sketch_text.stroke-321"),sQuery(id+"F0.wireOp",EDGE,"E4.sketch_text.stroke-322"),sQuery(id+"F0.wireOp",EDGE,"E4.sketch_text.stroke-323"),sQuery(id+"F0.wireOp",EDGE,"E4.sketch_text.stroke-324"),sQuery(id+"F0.wireOp",EDGE,"E4.sketch_text.stroke-325"),sQuery(id+"F0.wireOp",EDGE,"E4.sketch_text.stroke-326"),sQuery(id+"F0.wireOp",EDGE,"E4.sketch_text.stroke-327"),sQuery(id+"F0.wireOp",EDGE,"E4.sketch_text.stroke-328"),sQuery(id+"F0.wireOp",EDGE,"E4.sketch_text.stroke-329"),sQuery(id+"F0.wireOp",EDGE,"E4.sketch_text.stroke-330"),sQuery(id+"F0.wireOp",EDGE,"E4.sketch_text.stroke-331"),sQuery(id+"F0.wireOp",EDGE,"E4.sketch_text.stroke-332"),sQuery(id+"F0.wireOp",EDGE,"E4.sketch_text.stroke-333"),sQuery(id+"F0.wireOp",EDGE,"E4.sketch_text.stroke-334"),sQuery(id+"F0.wireOp",EDGE,"E4.sketch_text.stroke-335"),sQuery(id+"F0.wireOp",EDGE,"E4.sketch_text.stroke-336"),sQuery(id+"F0.wireOp",EDGE,"E4.sketch_text.stroke-337"),sQuery(id+"F0.wireOp",EDGE,"E4.sketch_text.stroke-338"),sQuery(id+"F0.wireOp",EDGE,"E4.sketch_text.stroke-339"),sQuery(id+"F0.wireOp",EDGE,"E4.sketch_text.stroke-340"),sQuery(id+"F0.wireOp",EDGE,"E4.sketch_text.stroke-341"),sQuery(id+"F0.wireOp",EDGE,"E4.sketch_text.stroke-342"),sQuery(id+"F0.wireOp",EDGE,"E4.sketch_text.stroke-343"),sQuery(id+"F0.wireOp",EDGE,"E4.sketch_text.stroke-344"),sQuery(id+"F0.wireOp",EDGE,"E4.sketch_text.stroke-345"),sQuery(id+"F0.wireOp",EDGE,"E4.sketch_text.stroke-346"),sQuery(id+"F0.wireOp",EDGE,"E4.sketch_text.stroke-347"),sQuery(id+"F0.wireOp",EDGE,"E4.sketch_text.stroke-348"),sQuery(id+"F0.wireOp",EDGE,"E4.sketch_text.stroke-359"),sQuery(id+"F0.wireOp",EDGE,"E4.sketch_text.stroke-360"),sQuery(id+"F0.wireOp",EDGE,"E4.sketch_text.stroke-361"),sQuery(id+"F0.wireOp",EDGE,"E4.sketch_text.stroke-362"),sQuery(id+"F0.wireOp",EDGE,"E4.sketch_text.stroke-363"),sQuery(id+"F0.wireOp",EDGE,"E4.sketch_text.stroke-364"),sQuery(id+"F0.wireOp",EDGE,"E4.sketch_text.stroke-365"),sQuery(id+"F0.wireOp",EDGE,"E4.sketch_text.stroke-366"),sQuery(id+"F0.wireOp",EDGE,"E4.sketch_text.stroke-367"),sQuery(id+"F0.wireOp",EDGE,"E4.sketch_text.stroke-368"),sQuery(id+"F0.wireOp",EDGE,"E4.sketch_text.stroke-369"),sQuery(id+"F0.wireOp",EDGE,"E4.sketch_text.stroke-370"),sQuery(id+"F0.wireOp",EDGE,"E4.sketch_text.stroke-371"),sQuery(id+"F0.wireOp",EDGE,"E4.sketch_text.stroke-372"),sQuery(id+"F0.wireOp",EDGE,"E4.sketch_text.stroke-373"),sQuery(id+"F0.wireOp",EDGE,"E4.sketch_text.stroke-374"),sQuery(id+"F0.wireOp",EDGE,"E4.sketch_text.stroke-375"),sQuery(id+"F0.wireOp",EDGE,"E4.sketch_text.stroke-376"),sQuery(id+"F0.wireOp",EDGE,"E4.sketch_text.stroke-377"),sQuery(id+"F0.wireOp",EDGE,"E4.sketch_text.stroke-378"),sQuery(id+"F0.wireOp",EDGE,"E4.sketch_text.stroke-379"),sQuery(id+"F0.wireOp",EDGE,"E4.sketch_text.stroke-380"),sQuery(id+"F0.wireOp",EDGE,"E4.sketch_text.stroke-381"),sQuery(id+"F0.wireOp",EDGE,"E4.sketch_text.stroke-382"),sQuery(id+"F0.wireOp",EDGE,"E4.sketch_text.stroke-383"),sQuery(id+"F0.wireOp",EDGE,"E4.sketch_text.stroke-384"),sQuery(id+"F0.wireOp",EDGE,"E4.sketch_text.stroke-385"),sQuery(id+"F0.wireOp",EDGE,"E4.sketch_text.stroke-386"),sQuery(id+"F0.wireOp",EDGE,"E4.sketch_text.stroke-387"),sQuery(id+"F0.wireOp",EDGE,"E4.sketch_text.stroke-388"),sQuery(id+"F0.wireOp",EDGE,"E4.sketch_text.stroke-389"),sQuery(id+"F0.wireOp",EDGE,"E4.sketch_text.stroke-390"),sQuery(id+"F0.wireOp",EDGE,"E4.sketch_text.stroke-391"),sQuery(id+"F0.wireOp",EDGE,"E4.sketch_text.stroke-392")])],"isStart":true})]});}
            fillet(context, id + "F10", {"entities" : qUnion([Q0, Q1, Q2, Q3, Q4, Q5, Q6]), "radius" : 1 * mm, "tangentPropagation" : true, "allowEdgeOverflow" : false});
        }
    });